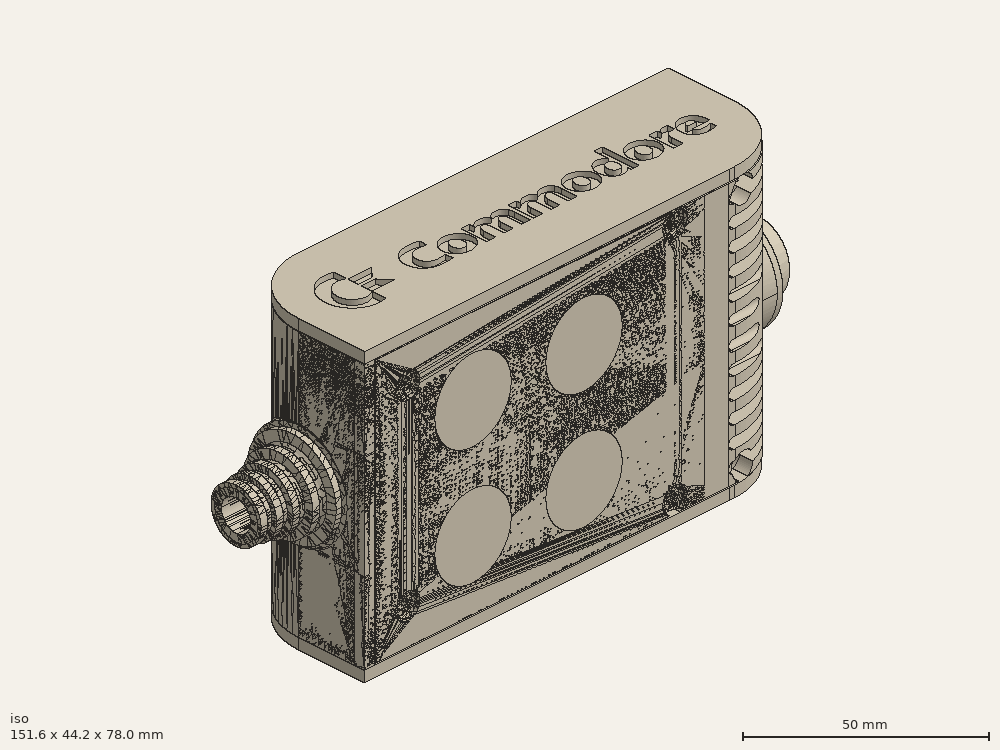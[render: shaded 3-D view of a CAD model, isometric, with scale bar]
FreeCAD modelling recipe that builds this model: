
FCSTD DOCUMENT  (FreeCAD 0.19R0.19.2)
Label: enclosure_218FCStd
License: All rights reserved
LicenseURL: http://en.wikipedia.org/wiki/All_rights_reserved
objects: Part::Revolution×152, Part::MultiFuse×146, Part::Feature×146, Sketcher::SketchObject×89, Part::Extrusion×74, Part::Cut×72, Part::Cylinder×70, Part::Fillet×58, Part::Box×36, App::MeasureDistance×4, Part::Chamfer×4, Part::FeaturePython×2, Image::ImagePlane×1, PartDesign::Body×1, Part::Mirroring×1
note: 851 computed .brp shape members not serialized (recipe doc carries the construction recipe); baked Part::Feature solids carry a one-line shape summary decoded from their .brp

FEATURE [Sketcher::SketchObject] Sketch  label="topSketch"
  FullyConstrained = true
  sketch-geometry (20):
    g0: LineSegment StartX=5.21097e-06 StartY=3 StartZ=0 EndX=5.21097e-06 EndY=19 EndZ=0
    g1: ArcOfCircle CenterX=19 CenterY=19 CenterZ=0 NormalX=0 NormalY=0 NormalZ=1 AngleXU=0 Radius=19 StartAngle=1.5708 EndAngle=3.14159
    g2: ArcOfCircle CenterX=19 CenterY=19 CenterZ=0 NormalX=0 NormalY=0 NormalZ=1 AngleXU=0 Radius=16 StartAngle=1.5708 EndAngle=3.14159
    g3: LineSegment StartX=114 StartY=35 StartZ=0 EndX=19 EndY=35 EndZ=0
    g4: LineSegment StartX=5.21097e-06 StartY=3 StartZ=0 EndX=5.21097e-06 EndY=0 EndZ=0
    g5: LineSegment StartX=3 StartY=0 StartZ=0 EndX=5.21097e-06 EndY=0 EndZ=0
    g6: LineSegment StartX=3 StartY=19 StartZ=0 EndX=3 EndY=0 EndZ=0
    g7: LineSegment StartX=19 StartY=38 StartZ=0 EndX=124 EndY=38 EndZ=0
    g8: Circle CenterX=119 CenterY=35 CenterZ=0 NormalX=0 NormalY=0 NormalZ=1 AngleXU=0 Radius=1
    g9: Circle CenterX=121 CenterY=35 CenterZ=0 NormalX=0 NormalY=0 NormalZ=1 AngleXU=0 Radius=1
    g10: Circle CenterX=121 CenterY=33 CenterZ=0 NormalX=0 NormalY=0 NormalZ=1 AngleXU=0 Radius=1
    g11: BSplineCurve PolesCount=3 KnotsCount=2 Degree=2 IsPeriodic=0
    g12: GeomPoint X=119 Y=35 Z=0
    g13: GeomPoint X=121 Y=33 Z=0
    g14: LineSegment StartX=119 StartY=35 StartZ=0 EndX=114 EndY=35 EndZ=0
    g15: ArcOfCircle CenterX=105 CenterY=19 CenterZ=0 NormalX=0 NormalY=0 NormalZ=1 AngleXU=0 Radius=19 StartAngle=5.7297 EndAngle=6.28319
    g16: ArcOfCircle CenterX=105 CenterY=19 CenterZ=0 NormalX=0 NormalY=0 NormalZ=1 AngleXU=0 Radius=16 StartAngle=5.60905 EndAngle=6.28319
    g17: LineSegment StartX=121 StartY=33 StartZ=0 EndX=121 EndY=19 EndZ=0
    g18: LineSegment StartX=124 StartY=38 StartZ=0 EndX=124 EndY=19 EndZ=0
    g19: LineSegment StartX=117.5 StartY=9.01251 StartZ=0 EndX=121.163 EndY=9.0125 EndZ=0
  constraints (46):
    c: Vertical(g0)
    c: Block(g0)
    c: Coincident(g1,g0)
    c: Block(g1)
    c: Coincident(g2,g1)
    c: Block(g2)
    c: Coincident(g3,g2)
    c: Horizontal(g3)
    c: Tangent(g3,g2)
    c: Coincident(g4,g0)
    c: Distance(g4) = 3
    c: Vertical(g4)
    c: Coincident(g5,g4)
    c: Horizontal(g5)
    c: Coincident(g6,g2)
    c: Coincident(g6,g5)
    c: Vertical(g6)
    c: Horizontal(g7)
    c: Distance(g7) = 105
    c: Coincident(g7,g1)
    c: Block(g3)
    c: Weight(g8) = 1
    c: Equal(g8,g9)
    c: Equal(g8,g10)
    c: InternalAlignment(g8,g11)
    c: InternalAlignment(g9,g11)
    c: InternalAlignment(g10,g11)
    c: InternalAlignment(g12,g11)
    c: InternalAlignment(g13,g11)
    c: Block(g11)
    c: Coincident(g14,g11)
    c: Coincident(g14,g3)
    c: Horizontal(g14)
    c: Block(g15)
    c: Coincident(g16,g15)
    c: Block(g16)
    c: Coincident(g17,g11)
    c: Coincident(g17,g16)
    c: Vertical(g17)
    c: Distance(g17) = 14
    c: Coincident(g18,g7)
    c: Coincident(g18,g15)
    c: Vertical(g18)
    c: Distance(g18) = 19
    c: Coincident(g19,g16)
    c: Coincident(g19,g15)
FEATURE [Sketcher::SketchObject] Sketch001  label="bottomSketch"
  FullyConstrained = true
  sketch-geometry (32):
    g0: LineSegment StartX=3.3 StartY=-6.03275e-07 StartZ=0 EndX=98 EndY=-6.03275e-07 EndZ=0
    g1: ArcOfCircle CenterX=98 CenterY=19 CenterZ=0 NormalX=0 NormalY=0 NormalZ=1 AngleXU=0 Radius=19 StartAngle=4.71239 EndAngle=5.71103
    g2: LineSegment StartX=6.3 StartY=8 StartZ=0 EndX=3.3 EndY=8 EndZ=0
    g3: LineSegment StartX=3.3 StartY=8 StartZ=0 EndX=3.3 EndY=-6.03275e-07 EndZ=0
    g4: ArcOfCircle CenterX=8.3 CenterY=5 CenterZ=0 NormalX=0 NormalY=0 NormalZ=1 AngleXU=0 Radius=2 StartAngle=3.14159 EndAngle=4.71239
    g5: LineSegment StartX=6.3 StartY=8 StartZ=0 EndX=6.3 EndY=5 EndZ=0
    g6: ArcOfCircle CenterX=98 CenterY=19 CenterZ=0 NormalX=0 NormalY=0 NormalZ=1 AngleXU=0 Radius=12.7 StartAngle=4.71239 EndAngle=6.28319
    g7: LineSegment StartX=94.7 StartY=3 StartZ=0 EndX=8.3 EndY=3 EndZ=0
    g8-g12: Circle x5 (B-spline internal-alignment scaffolding for g13; pole/knot coordinates omitted)
    g13: BSplineCurve PolesCount=5 KnotsCount=3 Degree=3 IsPeriodic=0
    g14: GeomPoint X=98 Y=6.3 Z=0
    g15: GeomPoint X=96.3938 Y=4.71946 Z=0
    g16: GeomPoint X=94.7 Y=3 Z=0
    g17-g23: Circle x7 (B-spline internal-alignment scaffolding for g24; pole/knot coordinates omitted)
    g24: BSplineCurve PolesCount=7 KnotsCount=5 Degree=3 IsPeriodic=0
    g25-g29: GeomPoint x5 (B-spline internal-alignment scaffolding for g24; pole/knot coordinates omitted)
    g30: ArcOfCircle CenterX=98 CenterY=19 CenterZ=0 NormalX=0 NormalY=0 NormalZ=1 AngleXU=0 Radius=15.7 StartAngle=5.81226 EndAngle=6.28319
    g31: LineSegment StartX=110.7 StartY=19 StartZ=0 EndX=113.7 EndY=19 EndZ=0
  constraints (41):
    c: Horizontal(g0)
    c: Coincident(g1,g0)
    c: Block(g1)
    c: Horizontal(g2)
    c: Distance(g2) = 3
    c: Coincident(g3,g2)
    c: Vertical(g3)
    c: Coincident(g3,g0)
    c: Block(g4)
    c: Block(g2)
    c: Coincident(g5,g2)
    c: Coincident(g5,g4)
    c: Vertical(g5)
    c: Coincident(g6,g1)
    c: Block(g6)
    c: Coincident(g7,g4)
    c: Horizontal(g7)
    c: Block(g0)
    c: Block(g7)
    c: Block(g3)
    c: Coincident(g13,g6)
    c: Weight(g8) = 1
    c: Equal(g8, g9-g12) x4
    c: Coincident(g13,g7)
    c: InternalAlignment(g8-g12 -> g13) x5
    c: InternalAlignment(g14,g13)
    c: InternalAlignment(g15,g13)
    c: InternalAlignment(g16,g13)
    c: Block(g13)
    c: Weight(g17) = 1
    c: Equal(g17, g18-g23) x6
    c: Coincident(g24,g1)
    c: InternalAlignment(g17-g23 -> g24) x7
    c: InternalAlignment(g25-g29 -> g24) x5
    c: Block(g24)
    c: Coincident(g30,g24)
    c: Coincident(g31,g6)
    c: Coincident(g31,g30)
    c: Horizontal(g31)
    c: Block(g31)
    c: Block(g30)
FEATURE [Part::Extrusion] Extrude  label="top"
  Base = -> Sketch
  Dir = (0,0,1)
  DirMode = 2
  FaceMakerClass = Part::FaceMakerBullseye
  LengthFwd = 72
  LengthRev = 0
  Solid = true
  Symmetric = false
FEATURE [Part::Extrusion] Extrude001  label="bottom"
  Base = -> Sketch001
  Dir = (0,0,1)
  DirMode = 2
  FaceMakerClass = Part::FaceMakerBullseye
  LengthFwd = 71.4
  LengthRev = 0
  Placement = pos=(0,0,0.3) rot=(0,0,1;0rad)
  Solid = true
  Symmetric = false
FEATURE [Sketcher::SketchObject] Sketch002  label="topSketch001"
  FullyConstrained = true
  sketch-geometry (8):
    g0: ArcOfCircle CenterX=19 CenterY=19.0975 CenterZ=0 NormalX=0 NormalY=0 NormalZ=1 AngleXU=0 Radius=18.9025 StartAngle=1.5708 EndAngle=3.14674
    g1: LineSegment StartX=0.0977805 StartY=19.0003 StartZ=0 EndX=0.0977805 EndY=0.000251602 EndZ=0
    g2: LineSegment StartX=19 StartY=38 StartZ=0 EndX=124 EndY=38 EndZ=0
    g3: LineSegment StartX=0.0977805 StartY=0.000251602 StartZ=0 EndX=105.098 EndY=0.000251602 EndZ=0
    g4: LineSegment StartX=124 StartY=38 StartZ=0 EndX=125.616 EndY=38 EndZ=0
    g5: LineSegment StartX=105.098 StartY=0.000251602 StartZ=0 EndX=106.713 EndY=0.000251602 EndZ=0
    g6: ArcOfCircle CenterX=106.616 CenterY=19 CenterZ=0 NormalX=0 NormalY=0 NormalZ=1 AngleXU=0 Radius=19 StartAngle=4.71754 EndAngle=6.28319
    g7: LineSegment StartX=125.616 StartY=38 StartZ=0 EndX=125.616 EndY=19 EndZ=0
  constraints (21):
    c: Block(g0)
    c: Coincident(g1,g0)
    c: Vertical(g1)
    c: Horizontal(g2)
    c: Distance(g2) = 105
    c: Coincident(g2,g0)
    c: Distance(g1) = 19
    c: Coincident(g3,g1)
    c: Horizontal(g3)
    c: Distance(g3) = 105
    c: Coincident(g4,g2)
    c: Horizontal(g4)
    c: Distance(g4) = 1.61553
    c: Horizontal(g5)
    c: Equal(g4,g5) = 1.61553
    c: Coincident(g5,g3)
    c: Block(g6)
    c: Coincident(g6,g5)
    c: Coincident(g7,g4)
    c: Coincident(g7,g6)
    c: Vertical(g7)
FEATURE [Part::Extrusion] Extrude002  label="sideA"
  Base = -> Sketch002
  Dir = (0,0,1)
  DirMode = 2
  FaceMakerClass = Part::FaceMakerBullseye
  LengthFwd = 3
  LengthRev = 0
  Placement = pos=(0,0,-3) rot=(0,0,1;0rad)
  Solid = true
  Symmetric = false
FEATURE [Sketcher::SketchObject] Sketch003  label="topSketch002"
  FullyConstrained = true
  sketch-geometry (6):
    g0: LineSegment StartX=19 StartY=38 StartZ=0 EndX=117 EndY=38 EndZ=0
    g1: ArcOfCircle CenterX=19 CenterY=19 CenterZ=0 NormalX=0 NormalY=0 NormalZ=1 AngleXU=0 Radius=19 StartAngle=1.5708 EndAngle=3.14159
    g2: LineSegment StartX=117 StartY=38 StartZ=0 EndX=117 EndY=19 EndZ=0
    g3: LineSegment StartX=98 StartY=1.0161e-12 StartZ=0 EndX=5.22862e-06 EndY=1.0161e-12 EndZ=0
    g4: LineSegment StartX=5.22862e-06 StartY=19 StartZ=0 EndX=5.22862e-06 EndY=1.0161e-12 EndZ=0
    g5: ArcOfCircle CenterX=98 CenterY=19 CenterZ=0 NormalX=0 NormalY=0 NormalZ=1 AngleXU=0 Radius=19 StartAngle=4.71239 EndAngle=6.28319
  constraints (16):
    c: Horizontal(g0)
    c: Distance(g0) = 98
    c: Coincident(g1,g0)
    c: Block(g1)
    c: Coincident(g2,g0)
    c: Vertical(g2)
    c: Distance(g2) = 19
    c: Horizontal(g3)
    c: Coincident(g4,g1)
    c: Vertical(g4)
    c: Coincident(g3,g4)
    c: Block(g3)
    c: Coincident(g5,g2)
    c: Coincident(g5,g3)
    c: Block(g0)
    c: Block(g5)
FEATURE [Sketcher::SketchObject] Sketch004
  FullyConstrained = true
  MapMode = 3
  Placement = pos=(0,0,0) rot=(1,0,0;1.5708rad)
  Support = -> [Extrude]
  sketch-geometry (8):
    g0: Circle CenterX=80.351 CenterY=-67.6202 CenterZ=0 NormalX=0 NormalY=0 NormalZ=1 AngleXU=0 Radius=2
    g1: Circle CenterX=80.351 CenterY=-67.6202 CenterZ=0 NormalX=0 NormalY=0 NormalZ=1 AngleXU=0 Radius=3
    g2: Circle CenterX=80.351 CenterY=-4.92017 CenterZ=0 NormalX=0 NormalY=0 NormalZ=1 AngleXU=0 Radius=2
    g3: Circle CenterX=80.351 CenterY=-4.92017 CenterZ=0 NormalX=0 NormalY=0 NormalZ=1 AngleXU=0 Radius=3
    g4: Circle CenterX=23.851 CenterY=-4.92017 CenterZ=0 NormalX=0 NormalY=0 NormalZ=1 AngleXU=0 Radius=2
    g5: Circle CenterX=23.851 CenterY=-4.92017 CenterZ=0 NormalX=0 NormalY=0 NormalZ=1 AngleXU=0 Radius=3
    g6: Circle CenterX=23.851 CenterY=-67.6202 CenterZ=0 NormalX=0 NormalY=0 NormalZ=1 AngleXU=0 Radius=2
    g7: Circle CenterX=23.851 CenterY=-67.6202 CenterZ=0 NormalX=0 NormalY=0 NormalZ=1 AngleXU=0 Radius=3
  constraints (8):
    c: Block(g3)
    c: Block(g2)
    c: Block(g1)
    c: Block(g0)
    c: Block(g6)
    c: Block(g7)
    c: Block(g4)
    c: Block(g5)
FEATURE [Part::Extrusion] Extrude004
  Base = -> Sketch004
  Dir = (0,-1,2e-16)
  DirMode = 2
  FaceMakerClass = Part::FaceMakerBullseye
  LengthFwd = 6
  LengthRev = 0
  Placement = pos=(0,9,0) rot=(0,0,1;0rad)
  Solid = true
  Symmetric = false
FEATURE [Sketcher::SketchObject] Sketch005
  FullyConstrained = true
  MapMode = 3
  Placement = pos=(0,0,0) rot=(1,0,0;1.5708rad)
  Support = -> [Extrude]
  sketch-geometry (8):
    g0: Circle CenterX=80.351 CenterY=-67.6202 CenterZ=0 NormalX=0 NormalY=0 NormalZ=1 AngleXU=0 Radius=3
    g1: Circle CenterX=80.351 CenterY=-4.92017 CenterZ=0 NormalX=0 NormalY=0 NormalZ=1 AngleXU=0 Radius=3
    g2: Circle CenterX=23.851 CenterY=-4.92017 CenterZ=0 NormalX=0 NormalY=0 NormalZ=1 AngleXU=0 Radius=3
    g3: Circle CenterX=23.851 CenterY=-67.6202 CenterZ=0 NormalX=0 NormalY=0 NormalZ=1 AngleXU=0 Radius=3
    g4: Circle CenterX=23.851 CenterY=-67.6202 CenterZ=0 NormalX=0 NormalY=0 NormalZ=1 AngleXU=0 Radius=5
    g5: Circle CenterX=80.351 CenterY=-67.6202 CenterZ=0 NormalX=0 NormalY=0 NormalZ=1 AngleXU=0 Radius=5
    g6: Circle CenterX=23.851 CenterY=-4.92017 CenterZ=0 NormalX=0 NormalY=0 NormalZ=1 AngleXU=0 Radius=5
    g7: Circle CenterX=80.351 CenterY=-4.92017 CenterZ=0 NormalX=0 NormalY=0 NormalZ=1 AngleXU=0 Radius=5
  constraints (8):
    c: Block(g1)
    c: Block(g0)
    c: Block(g3)
    c: Block(g2)
    c: Block(g5)
    c: Block(g4)
    c: Block(g6)
    c: Block(g7)
FEATURE [Part::Extrusion] Extrude005
  Base = -> Sketch005
  Dir = (0,-1,2e-16)
  DirMode = 2
  FaceMakerClass = Part::FaceMakerBullseye
  LengthFwd = 2
  LengthRev = 0
  Solid = true
  Symmetric = false
FEATURE [Sketcher::SketchObject] Sketch006
  FullyConstrained = true
  MapMode = 3
  Placement = pos=(0,0,0) rot=(1,0,0;1.5708rad)
  sketch-geometry (8):
    g0: Circle CenterX=80.351 CenterY=-67.6202 CenterZ=0 NormalX=0 NormalY=0 NormalZ=1 AngleXU=0 Radius=3
    g1: Circle CenterX=80.351 CenterY=-4.92017 CenterZ=0 NormalX=0 NormalY=0 NormalZ=1 AngleXU=0 Radius=3
    g2: Circle CenterX=23.851 CenterY=-4.92017 CenterZ=0 NormalX=0 NormalY=0 NormalZ=1 AngleXU=0 Radius=3
    g3: Circle CenterX=23.851 CenterY=-67.6202 CenterZ=0 NormalX=0 NormalY=0 NormalZ=1 AngleXU=0 Radius=3
    g4: Circle CenterX=23.851 CenterY=-67.6202 CenterZ=0 NormalX=0 NormalY=0 NormalZ=1 AngleXU=0 Radius=5
    g5: Circle CenterX=80.351 CenterY=-67.6202 CenterZ=0 NormalX=0 NormalY=0 NormalZ=1 AngleXU=0 Radius=5
    g6: Circle CenterX=23.851 CenterY=-4.92017 CenterZ=0 NormalX=0 NormalY=0 NormalZ=1 AngleXU=0 Radius=5
    g7: Circle CenterX=80.351 CenterY=-4.92017 CenterZ=0 NormalX=0 NormalY=0 NormalZ=1 AngleXU=0 Radius=5
  constraints (8):
    c: Block(g1)
    c: Block(g0)
    c: Block(g3)
    c: Block(g2)
    c: Block(g5)
    c: Block(g4)
    c: Block(g6)
    c: Block(g7)
FEATURE [Part::Extrusion] Extrude007
  Base = -> Sketch006
  Dir = (0,-1,2e-16)
  DirMode = 2
  FaceMakerClass = Part::FaceMakerBullseye
  LengthFwd = 2
  LengthRev = 0
  Solid = true
  Symmetric = false
FEATURE [Part::Fillet] Fillet
  Base = -> Extrude007
  Edges = 4 edges r=1.99: [Edge6,Edge12,Edge18,Edge24]
FEATURE [Part::Cut] Cut
  Base = -> Extrude005
  Placement = pos=(0,5,0) rot=(0,0,1;0rad)
  Tool = -> Fillet
FEATURE [Part::MultiFuse] Fusion  label="pCBScrews"
  Placement = pos=(-2.5,0,72.3) rot=(0,0,1;0rad)
  Shapes = -> [Extrude004,Cut]
FEATURE [App::MeasureDistance] Distance  label="Distance: 0.69 mm"
  Distance = 0.685967
  P1 = (24.0138,2.9647,0.3)
  P2 = (23.8901,3,-0.373787)
FEATURE [App::MeasureDistance] Distance001  label="Distance: 0.53 mm"
  Distance = 0.533607
  P1 = (80.2939,3,72.2334)
  P2 = (80.281,2.99661,71.7)
FEATURE [Part::Fillet] Fillet001
  Base = -> Extrude001
  Edges = 1 edges r=2.4: [Edge17]
FEATURE [Part::Fillet] Fillet002  label="bottom001"
  Base = -> Fillet001
  Edges = 1 edges r=2.4: [Edge36]
FEATURE [Part::Fillet] Fillet003  label="top001"
  Base = -> Extrude
  Edges = 1 edges r=2: [Edge1]
FEATURE [Sketcher::SketchObject] Sketch007
  FullyConstrained = true
  sketch-geometry (16):
    g0: LineSegment StartX=4 StartY=0 StartZ=0 EndX=4 EndY=2.4 EndZ=0
    g1: LineSegment StartX=4 StartY=2.4 StartZ=0 EndX=7 EndY=2.4 EndZ=0
    g2: LineSegment StartX=4 StartY=0 StartZ=0 EndX=5.7 EndY=0 EndZ=0
    g3: LineSegment StartX=5.7 StartY=0 StartZ=0 EndX=5.7 EndY=-5.6 EndZ=0
    g4-g8: Circle x5 (B-spline internal-alignment scaffolding for g9; pole/knot coordinates omitted)
    g9: BSplineCurve PolesCount=5 KnotsCount=3 Degree=3 IsPeriodic=0
    g10: GeomPoint X=7 Y=2.4 Z=0
    g11: GeomPoint X=10.4582 Y=-1.55472 Z=0
    g12: GeomPoint X=14 Y=-5.6 Z=0
    g13: LineSegment StartX=14 StartY=-5.6 StartZ=0 EndX=14 EndY=-14.1 EndZ=0
    g14: LineSegment StartX=14 StartY=-14.1 StartZ=0 EndX=6.5 EndY=-14.1 EndZ=0
    g15: LineSegment StartX=5.7 StartY=-5.6 StartZ=0 EndX=6.5 EndY=-14.1 EndZ=0
  constraints (28):
    c: Distance(g0) = 2.4
    c: Vertical(g0)
    c: Block(g0)
    c: Coincident(g1,g0)
    c: Horizontal(g1)
    c: Distance(g1) = 3
    c: Coincident(g2,g0)
    c: Horizontal(g2)
    c: Distance(g2) = 1.7
    c: Coincident(g3,g2)
    c: Vertical(g3)
    c: Distance(g3) = 5.6
    c: Coincident(g9,g1)
    c: Weight(g4) = 1
    c: Equal(g4, g5-g8) x4
    c: InternalAlignment(g4-g8 -> g9) x5
    c: InternalAlignment(g10,g9)
    c: InternalAlignment(g11,g9)
    c: InternalAlignment(g12,g9)
    c: Block(g9)
    c: Coincident(g13,g9)
    c: Vertical(g13)
    c: Distance(g13) = 8.5
    c: Coincident(g14,g13)
    c: Horizontal(g14)
    c: Distance(g14) = 7.5
    c: Coincident(g15,g3)
    c: Coincident(g15,g14)
FEATURE [Part::Feature] Face
  shape: bbox 10 x 16.5 x 2e-07 mm, 1 faces, 0 solids (baked)
FEATURE [Part::Revolution] Revolve  label="plugHousing"
  Angle = 360
  Axis = (0,1,0)
  Base = (0,0,0)
  FaceMakerClass = Part::FaceMakerBullseye
  Placement = pos=(0,0,36.15) rot=(0,0,1;0rad)
  Solid = false
  Source = -> Face
  Symmetric = false
FEATURE [Part::Feature] Face001
  shape: bbox 10 x 16.5 x 2e-07 mm, 1 faces, 0 solids (baked)
FEATURE [Part::Revolution] Revolve001  label="plugHousing001"
  Angle = 360
  Axis = (0,1,0)
  Base = (0,0,0)
  FaceMakerClass = Part::FaceMakerBullseye
  Placement = pos=(0,0,36.15) rot=(0,0,1;0rad)
  Solid = false
  Source = -> Face001
  Symmetric = false
FEATURE [Part::MultiFuse] Fusion001  label="plugHousing002"
  Placement = pos=(0,0,0) rot=(0,0,1;1.5708rad)
  Shapes = -> [Revolve001,Revolve]
FEATURE [Part::Feature] Face002
  shape: bbox 10 x 16.5 x 2e-07 mm, 1 faces, 0 solids (baked)
FEATURE [Part::Revolution] Revolve003  label="plugHousing005"
  Angle = 360
  Axis = (0,1,0)
  Base = (0,0,0)
  FaceMakerClass = Part::FaceMakerBullseye
  Placement = pos=(0,0,36.15) rot=(0,0,1;0rad)
  Solid = false
  Source = -> Face002
  Symmetric = false
FEATURE [Part::Feature] Face003
  shape: bbox 10 x 16.5 x 2e-07 mm, 1 faces, 0 solids (baked)
FEATURE [Part::Revolution] Revolve002  label="plugHousing003"
  Angle = 360
  Axis = (0,1,0)
  Base = (0,0,0)
  FaceMakerClass = Part::FaceMakerBullseye
  Placement = pos=(0,0,36.15) rot=(0,0,1;0rad)
  Solid = false
  Source = -> Face003
  Symmetric = false
FEATURE [Part::MultiFuse] Fusion002  label="plugHousing004"
  Placement = pos=(0,0,0) rot=(0,0,1;1.5708rad)
  Shapes = -> [Revolve002,Revolve003]
FEATURE [Part::MultiFuse] Fusion003  label="plugHousing006"
  Placement = pos=(0,19,0) rot=(0,0,1;3.14159rad)
  Shapes = -> [Fusion002,Fusion001]
FEATURE [Part::Feature] Face004
  shape: bbox 10 x 16.5 x 2e-07 mm, 1 faces, 0 solids (baked)
FEATURE [Part::Revolution] Revolve006  label="plugHousing010"
  Angle = 360
  Axis = (0,1,0)
  Base = (0,0,0)
  FaceMakerClass = Part::FaceMakerBullseye
  Placement = pos=(0,0,36.15) rot=(0,0,1;0rad)
  Solid = false
  Source = -> Face004
  Symmetric = false
FEATURE [Part::Feature] Face005
  shape: bbox 10 x 16.5 x 2e-07 mm, 1 faces, 0 solids (baked)
FEATURE [Part::Revolution] Revolve007  label="plugHousing011"
  Angle = 360
  Axis = (0,1,0)
  Base = (0,0,0)
  FaceMakerClass = Part::FaceMakerBullseye
  Placement = pos=(0,0,36.15) rot=(0,0,1;0rad)
  Solid = false
  Source = -> Face005
  Symmetric = false
FEATURE [Part::Feature] Face006
  shape: bbox 10 x 16.5 x 2e-07 mm, 1 faces, 0 solids (baked)
FEATURE [Part::Revolution] Revolve004  label="plugHousing007"
  Angle = 360
  Axis = (0,1,0)
  Base = (0,0,0)
  FaceMakerClass = Part::FaceMakerBullseye
  Placement = pos=(0,0,36.15) rot=(0,0,1;0rad)
  Solid = false
  Source = -> Face006
  Symmetric = false
FEATURE [Part::MultiFuse] Fusion004  label="plugHousing009"
  Placement = pos=(0,0,0) rot=(0,0,1;1.5708rad)
  Shapes = -> [Revolve004,Revolve007]
FEATURE [Part::Feature] Face007
  shape: bbox 10 x 16.5 x 2e-07 mm, 1 faces, 0 solids (baked)
FEATURE [Part::Revolution] Revolve005  label="plugHousing008"
  Angle = 360
  Axis = (0,1,0)
  Base = (0,0,0)
  FaceMakerClass = Part::FaceMakerBullseye
  Placement = pos=(0,0,36.15) rot=(0,0,1;0rad)
  Solid = false
  Source = -> Face007
  Symmetric = false
FEATURE [Part::MultiFuse] Fusion005  label="plugHousing012"
  Placement = pos=(0,0,0) rot=(0,0,1;1.5708rad)
  Shapes = -> [Revolve006,Revolve005]
FEATURE [Part::MultiFuse] Fusion006  label="plugHousing013"
  Placement = pos=(0,19,0) rot=(0,0,1;3.14159rad)
  Shapes = -> [Fusion005,Fusion004]
FEATURE [Part::MultiFuse] Fusion007  label="plugHousing014"
  Placement = pos=(122.621,0,-0.15) rot=(0,0,1;0rad)
  Shapes = -> [Fusion003,Fusion006]
FEATURE [Part::Cylinder] Cylinder002
  Angle = 360
  AttacherType = Attacher::AttachEngine3D
  Height = 20
  Placement = pos=(0,0,36.15) rot=(0,0,1;0rad)
  Radius = 4
FEATURE [Part::Cylinder] Cylinder003
  Angle = 360
  AttacherType = Attacher::AttachEngine3D
  Height = 10
  Placement = pos=(0,0,36.15) rot=(0,0,1;0rad)
  Radius = 4
FEATURE [Part::MultiFuse] Fusion009  label="removeToCreateHoleForPlugHousing"
  Placement = pos=(70,19,36.15) rot=(0,1,0;1.5708rad)
  Shapes = -> [Cylinder002,Cylinder003]
FEATURE [Part::Cylinder] Cylinder004
  Angle = 360
  AttacherType = Attacher::AttachEngine3D
  Height = 20
  Placement = pos=(0,0,36.15) rot=(0,0,1;0rad)
  Radius = 4
FEATURE [Part::Cylinder] Cylinder005
  Angle = 360
  AttacherType = Attacher::AttachEngine3D
  Height = 10
  Placement = pos=(0,0,36.15) rot=(0,0,1;0rad)
  Radius = 4
FEATURE [Part::MultiFuse] Fusion010  label="removeToCreateHoleForPlugHousing001"
  Placement = pos=(70,19,36.15) rot=(0,1,0;1.5708rad)
  Shapes = -> [Cylinder004,Cylinder005]
FEATURE [Part::Cut] Cut001
  Base = -> Fillet003
  Tool = -> Fusion010
FEATURE [Part::Cut] Cut002  label="Bottom"
  Base = -> Fillet002
  Tool = -> Fusion009
FEATURE [Part::Feature] Face008
  shape: bbox 10 x 16.5 x 2e-07 mm, 1 faces, 0 solids (baked)
FEATURE [Part::Revolution] Revolve011  label="plugHousing021"
  Angle = 360
  Axis = (0,1,0)
  Base = (0,0,0)
  FaceMakerClass = Part::FaceMakerBullseye
  Placement = pos=(0,0,36.15) rot=(0,0,1;0rad)
  Solid = false
  Source = -> Face008
  Symmetric = false
FEATURE [Part::Feature] Face009
  shape: bbox 10 x 16.5 x 2e-07 mm, 1 faces, 0 solids (baked)
FEATURE [Part::Revolution] Revolve012  label="plugHousing022"
  Angle = 360
  Axis = (0,1,0)
  Base = (0,0,0)
  FaceMakerClass = Part::FaceMakerBullseye
  Placement = pos=(0,0,36.15) rot=(0,0,1;0rad)
  Solid = false
  Source = -> Face009
  Symmetric = false
FEATURE [Part::Feature] Face010 .. Face013  x4 (patterned run collapsed; names and placements below)
  shape: bbox 10 x 16.5 x 2e-07 mm, 1 faces, 0 solids (baked)
FEATURE [Part::Revolution] Revolve015  label="plugHousing027"
  Angle = 360
  Axis = (0,1,0)
  Base = (0,0,0)
  FaceMakerClass = Part::FaceMakerBullseye
  Placement = pos=(0,0,36.15) rot=(0,0,1;0rad)
  Solid = false
  Source = -> Face013
  Symmetric = false
FEATURE [Part::Feature] Face014
  shape: bbox 10 x 16.5 x 2e-07 mm, 1 faces, 0 solids (baked)
FEATURE [Part::Feature] Face015
  shape: bbox 10 x 16.5 x 2e-07 mm, 1 faces, 0 solids (baked)
FEATURE [Part::Feature] Face016
  shape: bbox 10 x 16.5 x 2e-07 mm, 1 faces, 0 solids (baked)
FEATURE [Part::Revolution] Revolve019  label="plugHousing033"
  Angle = 360
  Axis = (0,1,0)
  Base = (0,0,0)
  FaceMakerClass = Part::FaceMakerBullseye
  Placement = pos=(0,0,36.15) rot=(0,0,1;0rad)
  Solid = false
  Source = -> Face016
  Symmetric = false
FEATURE [Part::Feature] Face017
  shape: bbox 10 x 16.5 x 2e-07 mm, 1 faces, 0 solids (baked)
FEATURE [Part::Revolution] Revolve020  label="plugHousing034"
  Angle = 360
  Axis = (0,1,0)
  Base = (0,0,0)
  FaceMakerClass = Part::FaceMakerBullseye
  Placement = pos=(0,0,36.15) rot=(0,0,1;0rad)
  Solid = false
  Source = -> Face017
  Symmetric = false
FEATURE [Part::Feature] Face018
  shape: bbox 10 x 16.5 x 2e-07 mm, 1 faces, 0 solids (baked)
FEATURE [Part::Revolution] Revolve016  label="plugHousing030"
  Angle = 360
  Axis = (0,1,0)
  Base = (0,0,0)
  FaceMakerClass = Part::FaceMakerBullseye
  Placement = pos=(0,0,36.15) rot=(0,0,1;0rad)
  Solid = false
  Source = -> Face018
  Symmetric = false
FEATURE [Part::MultiFuse] Fusion020  label="plugHousing038"
  Placement = pos=(0,0,0) rot=(0,0,1;1.5708rad)
  Shapes = -> [Revolve016,Revolve020]
FEATURE [Part::Feature] Face019
  shape: bbox 10 x 16.5 x 2e-07 mm, 1 faces, 0 solids (baked)
FEATURE [Part::Feature] Face020
  shape: bbox 10 x 16.5 x 2e-07 mm, 1 faces, 0 solids (baked)
FEATURE [Part::Revolution] Revolve017  label="plugHousing031"
  Angle = 360
  Axis = (0,1,0)
  Base = (0,0,0)
  FaceMakerClass = Part::FaceMakerBullseye
  Placement = pos=(0,0,36.15) rot=(0,0,1;0rad)
  Solid = false
  Source = -> Face020
  Symmetric = false
FEATURE [Part::MultiFuse] Fusion021  label="plugHousing039"
  Placement = pos=(0,0,0) rot=(0,0,1;1.5708rad)
  Shapes = -> [Revolve019,Revolve017]
FEATURE [Part::MultiFuse] Fusion023  label="plugHousing041"
  Placement = pos=(0,19,0) rot=(0,0,1;3.14159rad)
  Shapes = -> [Fusion021,Fusion020]
FEATURE [Part::Revolution] Revolve022  label="plugHousing043"
  Angle = 360
  Axis = (0,1,0)
  Base = (0,0,0)
  FaceMakerClass = Part::FaceMakerBullseye
  Placement = pos=(0,0,36.15) rot=(0,0,1;0rad)
  Solid = false
  Source = -> Face019
  Symmetric = false
FEATURE [Part::Feature] Face021
  shape: bbox 10 x 16.5 x 2e-07 mm, 1 faces, 0 solids (baked)
FEATURE [Part::Revolution] Revolve023  label="plugHousing044"
  Angle = 360
  Axis = (0,1,0)
  Base = (0,0,0)
  FaceMakerClass = Part::FaceMakerBullseye
  Placement = pos=(0,0,36.15) rot=(0,0,1;0rad)
  Solid = false
  Source = -> Face021
  Symmetric = false
FEATURE [Part::Feature] Face022
  shape: bbox 10 x 16.5 x 2e-07 mm, 1 faces, 0 solids (baked)
FEATURE [Part::Revolution] Revolve018  label="plugHousing032"
  Angle = 360
  Axis = (0,1,0)
  Base = (0,0,0)
  FaceMakerClass = Part::FaceMakerBullseye
  Placement = pos=(0,0,36.15) rot=(0,0,1;0rad)
  Solid = false
  Source = -> Face022
  Symmetric = false
FEATURE [Part::MultiFuse] Fusion022  label="plugHousing040"
  Placement = pos=(0,0,0) rot=(0,0,1;1.5708rad)
  Shapes = -> [Revolve018,Revolve023]
FEATURE [Part::Feature] Face023
  shape: bbox 10 x 16.5 x 2e-07 mm, 1 faces, 0 solids (baked)
FEATURE [Part::Revolution] Revolve021  label="plugHousing035"
  Angle = 360
  Axis = (0,1,0)
  Base = (0,0,0)
  FaceMakerClass = Part::FaceMakerBullseye
  Placement = pos=(0,0,36.15) rot=(0,0,1;0rad)
  Solid = false
  Source = -> Face023
  Symmetric = false
FEATURE [Part::MultiFuse] Fusion018  label="plugHousing036"
  Placement = pos=(0,0,0) rot=(0,0,1;1.5708rad)
  Shapes = -> [Revolve022,Revolve021]
FEATURE [Part::MultiFuse] Fusion019  label="plugHousing037"
  Placement = pos=(0,19,0) rot=(0,0,1;3.14159rad)
  Shapes = -> [Fusion018,Fusion022]
FEATURE [Part::MultiFuse] Fusion024  label="plugHousing042"
  Placement = pos=(122.621,0,-0.15) rot=(0,0,1;0rad)
  Shapes = -> [Fusion023,Fusion019]
FEATURE [Part::Cylinder] Cylinder006
  Angle = 360
  AttacherType = Attacher::AttachEngine3D
  Height = 20
  Placement = pos=(0,0,36.15) rot=(0,0,1;0rad)
  Radius = 14.3
FEATURE [Part::Cylinder] Cylinder007
  Angle = 360
  AttacherType = Attacher::AttachEngine3D
  Height = 10
  Placement = pos=(0,0,36.15) rot=(0,0,1;0rad)
  Radius = 4
FEATURE [Part::MultiFuse] Fusion026  label="removeToCreteHoleForPlugHousing"
  Placement = pos=(70,19,36) rot=(0,1,0;1.5708rad)
  Shapes = -> [Cylinder006,Cylinder007]
FEATURE [Part::Box] Box001  label="Cube001"
  AttacherType = Attacher::AttachEngine3D
  Height = 28
  Length = 3
  Placement = pos=(110.7,19,22) rot=(0,0,1;0rad)
  Width = 15.7
FEATURE [Part::Cut] Cut003  label="top002"
  Base = -> Cut001
  Tool = -> Fusion007
FEATURE [Part::Revolution] Revolve008  label="plugHousing015"
  Angle = 360
  Axis = (0,1,0)
  Base = (0,0,0)
  FaceMakerClass = Part::FaceMakerBullseye
  Placement = pos=(0,0,36.15) rot=(0,0,1;0rad)
  Solid = false
  Source = -> Face010
  Symmetric = false
FEATURE [Part::MultiFuse] Fusion013  label="plugHousing020"
  Placement = pos=(0,0,0) rot=(0,0,1;1.5708rad)
  Shapes = -> [Revolve008,Revolve012]
FEATURE [Part::Cut] Cut004  label="top003"
  Base = -> Cut003
  Placement = pos=(1,0,0) rot=(0,0,1;0rad)
  Tool = -> Fusion026
FEATURE [Part::Cylinder] Cylinder008
  Angle = 360
  AttacherType = Attacher::AttachEngine3D
  Height = 20
  Placement = pos=(0,0,36.15) rot=(0,0,1;0rad)
  Radius = 10.3
FEATURE [Part::Cylinder] Cylinder009
  Angle = 360
  AttacherType = Attacher::AttachEngine3D
  Height = 10
  Placement = pos=(0,0,36.15) rot=(0,0,1;0rad)
  Radius = 4
FEATURE [Part::MultiFuse] Fusion027  label="removeToCreteHoleForPlugHousing001"
  Placement = pos=(70,19,36) rot=(0,1,0;1.5708rad)
  Shapes = -> [Cylinder008,Cylinder009]
FEATURE [Part::Cut] Cut005  label="plugHousingTab"
  Base = -> Box001
  Tool = -> Fusion027
FEATURE [Part::MultiFuse] Fusion028  label="plugHousing045"
  Shapes = -> [Fusion024,Cut005]
FEATURE [Part::Box] Box002  label="Cube002"
  AttacherType = Attacher::AttachEngine3D
  Height = 28.8
  Length = 3
  Placement = pos=(107.3,28,21.6) rot=(0,0,1;0rad)
  Width = 7
FEATURE [Part::Box] Box003  label="Cube003"
  AttacherType = Attacher::AttachEngine3D
  Height = 3
  Length = 6.4
  Placement = pos=(107.3,28,18.6) rot=(0,0,1;0rad)
  Width = 7
FEATURE [Part::Box] Box004  label="Cube004"
  AttacherType = Attacher::AttachEngine3D
  Height = 3
  Length = 6.4
  Placement = pos=(107.3,28,50.4) rot=(0,0,1;0rad)
  Width = 7
FEATURE [Part::MultiFuse] Fusion029  label="plugHousingBracketHolder"
  Shapes = -> [Box004,Box002,Box003]
FEATURE [Part::Cylinder] Cylinder010
  Angle = 360
  AttacherType = Attacher::AttachEngine3D
  Height = 20
  Placement = pos=(0,0,36.15) rot=(0,0,1;0rad)
  Radius = 14.3
FEATURE [Part::Cylinder] Cylinder011
  Angle = 360
  AttacherType = Attacher::AttachEngine3D
  Height = 10
  Placement = pos=(0,0,36.15) rot=(0,0,1;0rad)
  Radius = 4
FEATURE [Part::MultiFuse] Fusion030  label="removeToCreteHoleForPlugHousing002"
  Placement = pos=(70,19,36) rot=(0,1,0;1.5708rad)
  Shapes = -> [Cylinder010,Cylinder011]
FEATURE [Part::Cut] Cut006  label="plugHousingBracketHolder001"
  Base = -> Fusion029
  Tool = -> Fusion030
FEATURE [Part::Cylinder] Cylinder012
  Angle = 360
  AttacherType = Attacher::AttachEngine3D
  Height = 20
  Placement = pos=(0,0,36.15) rot=(0,0,1;0rad)
  Radius = 7
FEATURE [Part::Cylinder] Cylinder013
  Angle = 360
  AttacherType = Attacher::AttachEngine3D
  Height = 10
  Placement = pos=(0,0,36.15) rot=(0,0,1;0rad)
  Radius = 4
FEATURE [Part::MultiFuse] Fusion032  label="removeToCreteHoleForPlugHousing003"
  Placement = pos=(70,19,36) rot=(0,1,0;1.5708rad)
  Shapes = -> [Cylinder012,Cylinder013]
FEATURE [Part::Cut] Cut007  label="bottom002"
  Base = -> Cut002
  Tool = -> Fusion032
FEATURE [Sketcher::SketchObject] Sketch008
  FullyConstrained = true
  sketch-geometry (54):
    g0: LineSegment StartX=-4.2 StartY=0 StartZ=0 EndX=-6.2 EndY=0 EndZ=0
    g1: LineSegment StartX=-14 StartY=-18 StartZ=0 EndX=-14 EndY=-26.5 EndZ=0
    g2: LineSegment StartX=-4.2 StartY=0 StartZ=0 EndX=-4.2 EndY=-13.4877 EndZ=0
    g3: Circle CenterX=-4.2 CenterY=-13.4877 CenterZ=0 NormalX=0 NormalY=0 NormalZ=1 AngleXU=0 Radius=1
    g4: Circle CenterX=-4.2 CenterY=-26.5 CenterZ=0 NormalX=0 NormalY=0 NormalZ=1 AngleXU=0 Radius=1
    g5: Circle CenterX=-8.2 CenterY=-26.5 CenterZ=0 NormalX=0 NormalY=0 NormalZ=1 AngleXU=0 Radius=1
    g6: BSplineCurve PolesCount=3 KnotsCount=2 Degree=2 IsPeriodic=0
    g7: GeomPoint X=-4.2 Y=-13.4877 Z=0
    g8: GeomPoint X=-8.2 Y=-26.5 Z=0
    g9: LineSegment StartX=-14 StartY=-26.5 StartZ=0 EndX=-8.2 EndY=-26.5 EndZ=0
    g10: LineSegment StartX=-10.15 StartY=-12 StartZ=0 EndX=-10.15 EndY=-14 EndZ=0
    g11: LineSegment StartX=-12.8401 StartY=-16 StartZ=0 EndX=-10.1571 EndY=-16 EndZ=0
    g12: LineSegment StartX=-10.15 StartY=-14 StartZ=0 EndX=-8.70761 EndY=-14 EndZ=0
    g13: LineSegment StartX=-12.8401 StartY=-16 StartZ=0 EndX=-12.8401 EndY=-17.6958 EndZ=0
    g14: LineSegment StartX=-10.15 StartY=-12 StartZ=0 EndX=-7.79258 EndY=-12 EndZ=0
    g15: Circle CenterX=-6.2215 CenterY=-2 CenterZ=0 NormalX=0 NormalY=0 NormalZ=1 AngleXU=0 Radius=1
    g16: Circle CenterX=-6.22762 CenterY=-2.58724 CenterZ=0 NormalX=0 NormalY=0 NormalZ=1 AngleXU=0 Radius=1
    g17: Circle CenterX=-6.32538 CenterY=-4 CenterZ=0 NormalX=0 NormalY=0 NormalZ=1 AngleXU=0 Radius=1
    g18: BSplineCurve PolesCount=3 KnotsCount=2 Degree=2 IsPeriodic=0
    g19: GeomPoint X=-6.2215 Y=-2 Z=0
    g20: GeomPoint X=-6.32538 Y=-4 Z=0
    g21: Circle CenterX=-6.48644 CenterY=-5.99526 CenterZ=0 NormalX=0 NormalY=0 NormalZ=1 AngleXU=0 Radius=1
    g22: Circle CenterX=-6.58486 CenterY=-6.99526 CenterZ=0 NormalX=0 NormalY=0 NormalZ=1 AngleXU=0 Radius=1
    g23: Circle CenterX=-6.77343 CenterY=-8 CenterZ=0 NormalX=0 NormalY=0 NormalZ=1 AngleXU=0 Radius=1
    g24: BSplineCurve PolesCount=3 KnotsCount=2 Degree=2 IsPeriodic=0
    g25: GeomPoint X=-6.48644 Y=-5.99526 Z=0
    g26: GeomPoint X=-6.77343 Y=-8 Z=0
    g27: Circle CenterX=-7.19003 CenterY=-10 CenterZ=0 NormalX=0 NormalY=0 NormalZ=1 AngleXU=0 Radius=1
    g28: Circle CenterX=-7.44407 CenterY=-11.0915 CenterZ=0 NormalX=0 NormalY=0 NormalZ=1 AngleXU=0 Radius=1
    g29: Circle CenterX=-7.79258 CenterY=-12 CenterZ=0 NormalX=0 NormalY=0 NormalZ=1 AngleXU=0 Radius=1
    g30: BSplineCurve PolesCount=3 KnotsCount=2 Degree=2 IsPeriodic=0
    g31: GeomPoint X=-7.19003 Y=-10 Z=0
    g32: GeomPoint X=-7.79258 Y=-12 Z=0
    g33: Circle CenterX=-8.70761 CenterY=-14 CenterZ=0 NormalX=0 NormalY=0 NormalZ=1 AngleXU=0 Radius=1
    g34: Circle CenterX=-9.33087 CenterY=-15.1837 CenterZ=0 NormalX=0 NormalY=0 NormalZ=1 AngleXU=0 Radius=1
    g35: Circle CenterX=-10.1571 CenterY=-16 CenterZ=0 NormalX=0 NormalY=0 NormalZ=1 AngleXU=0 Radius=1
    g36: BSplineCurve PolesCount=3 KnotsCount=2 Degree=2 IsPeriodic=0
    g37: GeomPoint X=-8.70761 Y=-14 Z=0
    g38: GeomPoint X=-10.1571 Y=-16 Z=0
    g39: Circle CenterX=-12.8401 CenterY=-17.6958 CenterZ=0 NormalX=0 NormalY=0 NormalZ=1 AngleXU=0 Radius=1
    g40: Circle CenterX=-13.3521 CenterY=-17.9027 CenterZ=0 NormalX=0 NormalY=0 NormalZ=1 AngleXU=0 Radius=1
    g41: Circle CenterX=-14 CenterY=-18 CenterZ=0 NormalX=0 NormalY=0 NormalZ=1 AngleXU=0 Radius=1
    g42: BSplineCurve PolesCount=3 KnotsCount=2 Degree=2 IsPeriodic=0
    g43: GeomPoint X=-12.8401 Y=-17.6958 Z=0
    g44: GeomPoint X=-14 Y=-18 Z=0
    g45: LineSegment StartX=-6.2 StartY=0 StartZ=0 EndX=-7.2 EndY=0 EndZ=0
    g46: LineSegment StartX=-7.2 StartY=0 StartZ=0 EndX=-7.2 EndY=-2 EndZ=0
    g47: LineSegment StartX=-7.2 StartY=-2 StartZ=0 EndX=-6.2215 EndY=-2 EndZ=0
    g48: LineSegment StartX=-6.32538 StartY=-4 StartZ=0 EndX=-7.65538 EndY=-4 EndZ=0
    g49: LineSegment StartX=-7.65538 StartY=-4 StartZ=0 EndX=-7.65538 EndY=-5.99526 EndZ=0
    g50: LineSegment StartX=-7.65538 StartY=-5.99526 StartZ=0 EndX=-6.48644 EndY=-5.99526 EndZ=0
    g51: LineSegment StartX=-6.77343 StartY=-8 StartZ=0 EndX=-8.43343 EndY=-8 EndZ=0
    g52: LineSegment StartX=-8.43343 StartY=-8 StartZ=0 EndX=-8.43343 EndY=-10 EndZ=0
    g53: LineSegment StartX=-8.43343 StartY=-10 StartZ=0 EndX=-7.19003 EndY=-10 EndZ=0
  constraints (112):
    c: Horizontal(g0)
    c: Distance(g0) = 2
    c: Block(g0)
    c: Vertical(g1)
    c: Coincident(g2,g0)
    c: Vertical(g2)
    c: Block(g2)
    c: Coincident(g6,g2)
    c: Weight(g3) = 1
    c: Equal(g3,g4)
    c: Equal(g3,g5)
    c: InternalAlignment(g3,g6)
    c: InternalAlignment(g4,g6)
    c: InternalAlignment(g5,g6)
    c: InternalAlignment(g7,g6)
    c: InternalAlignment(g8,g6)
    c: Block(g6)
    c: Coincident(g9,g1)
    c: Coincident(g9,g6)
    c: Horizontal(g9)
    c: Vertical(g10)
    c: Block(g10)
    c: Horizontal(g11)
    c: Block(g11)
    c: Coincident(g12,g10)
    c: Horizontal(g12)
    c: Block(g12)
    c: Coincident(g13,g11)
    c: Vertical(g13)
    c: Block(g13)
    c: Coincident(g14,g10)
    c: Horizontal(g14)
    c: Block(g14)
    c: Block(g9)
    c: Block(g1)
    c: Weight(g15) = 1
    c: Equal(g15,g16)
    c: Equal(g15,g17)
    c: InternalAlignment(g15,g18)
    c: InternalAlignment(g16,g18)
    c: InternalAlignment(g17,g18)
    c: InternalAlignment(g19,g18)
    c: InternalAlignment(g20,g18)
    c: Weight(g21) = 1
    c: Equal(g21,g22)
    c: Equal(g21,g23)
    c: InternalAlignment(g21,g24)
    c: InternalAlignment(g22,g24)
    c: InternalAlignment(g23,g24)
    c: InternalAlignment(g25,g24)
    c: InternalAlignment(g26,g24)
    c: Weight(g27) = 1
    c: Equal(g27,g28)
    c: Equal(g27,g29)
    c: Coincident(g30,g14)
    c: InternalAlignment(g27,g30)
    c: InternalAlignment(g28,g30)
    c: InternalAlignment(g29,g30)
    c: InternalAlignment(g31,g30)
    c: InternalAlignment(g32,g30)
    c: Coincident(g36,g12)
    c: Weight(g33) = 1
    c: Equal(g33,g34)
    c: Equal(g33,g35)
    c: Coincident(g36,g11)
    c: InternalAlignment(g33,g36)
    c: InternalAlignment(g34,g36)
    c: InternalAlignment(g35,g36)
    c: InternalAlignment(g37,g36)
    c: InternalAlignment(g38,g36)
    c: Coincident(g42,g13)
    c: Weight(g39) = 1
    c: Equal(g39,g40)
    c: Equal(g39,g41)
    c: Coincident(g42,g1)
    c: InternalAlignment(g39,g42)
    c: InternalAlignment(g40,g42)
    c: InternalAlignment(g41,g42)
    c: InternalAlignment(g43,g42)
    c: InternalAlignment(g44,g42)
    c: Block(g18)
    c: Block(g24)
    c: Block(g30)
    c: Block(g36)
    c: Block(g42)
    c: Horizontal(g45)
    c: Coincident(g45,g0)
    c: Vertical(g46)
    c: Coincident(g46,g45)
    c: Coincident(g47,g46)
    c: Coincident(g47,g18)
    c: Horizontal(g47)
    c: Block(g46)
    c: Coincident(g48,g18)
    c: Horizontal(g48)
    c: Distance(g48) = 1.33
    c: Vertical(g49)
    c: Coincident(g49,g48)
    c: Coincident(g50,g49)
    c: Coincident(g50,g24)
    c: Horizontal(g50)
    c: Tangent(g50,g22)
    c: Horizontal(g51)
    c: Coincident(g51,g24)
    c: Block(g51)
    c: Vertical(g52)
    c: Block(g52)
    c: Coincident(g52,g51)
    c: Coincident(g53,g52)
    c: Coincident(g53,g30)
    c: Horizontal(g53)
    c: Distance(g1) = 8.5
FEATURE [Part::Feature] Face024
  shape: bbox 9.8 x 26.5 x 2e-07 mm, 1 faces, 0 solids (baked)
FEATURE [Part::Revolution] Revolve024
  Angle = 360
  Axis = (0,1,0)
  Base = (0,0,0)
  FaceMakerClass = Part::FaceMakerBullseye
  Placement = pos=(0,0,0) rot=(0,0,1;1.5708rad)
  Solid = false
  Source = -> Face024
  Symmetric = false
FEATURE [Part::Feature] Face025
  shape: bbox 9.8 x 26.5 x 2e-07 mm, 1 faces, 0 solids (baked)
FEATURE [Part::Revolution] Revolve025
  Angle = 360
  Axis = (0,1,0)
  Base = (0,0,0)
  FaceMakerClass = Part::FaceMakerBullseye
  Placement = pos=(0,0,0) rot=(0,0,1;1.5708rad)
  Solid = false
  Source = -> Face025
  Symmetric = false
FEATURE [Part::MultiFuse] Fusion033
  Placement = pos=(-18,19,36) rot=(0,0,1;0rad)
  Shapes = -> [Revolve025,Revolve024]
FEATURE [Part::Cylinder] Cylinder014
  Angle = 360
  AttacherType = Attacher::AttachEngine3D
  Height = 20
  Placement = pos=(0,0,36.15) rot=(0,0,1;0rad)
  Radius = 14.3
FEATURE [Part::Cylinder] Cylinder015
  Angle = 360
  AttacherType = Attacher::AttachEngine3D
  Height = 10
  Placement = pos=(0,0,36.15) rot=(0,0,1;0rad)
  Radius = 4
FEATURE [Part::MultiFuse] Fusion034  label="removeToCreteHoleForPlugHousing004"
  Placement = pos=(-42,19,36) rot=(0,1,0;1.5708rad)
  Shapes = -> [Cylinder014,Cylinder015]
FEATURE [Part::Cut] Cut008  label="top004"
  Base = -> Cut004
  Placement = pos=(-1,0,0) rot=(0,0,1;0rad)
  Tool = -> Fusion034
FEATURE [Part::Box] Box005  label="Cube005"
  AttacherType = Attacher::AttachEngine3D
  Height = 28
  Length = 3
  Placement = pos=(110.7,19,22) rot=(0,0,1;0rad)
  Width = 15.7
FEATURE [Part::Cylinder] Cylinder016
  Angle = 360
  AttacherType = Attacher::AttachEngine3D
  Height = 10
  Placement = pos=(0,0,36.15) rot=(0,0,1;0rad)
  Radius = 4
FEATURE [Part::Cylinder] Cylinder017
  Angle = 360
  AttacherType = Attacher::AttachEngine3D
  Height = 20
  Placement = pos=(0,0,36.15) rot=(0,0,1;0rad)
  Radius = 10.3
FEATURE [Part::MultiFuse] Fusion035  label="removeToCreteHoleForPlugHousing005"
  Placement = pos=(70,19,36) rot=(0,1,0;1.5708rad)
  Shapes = -> [Cylinder017,Cylinder016]
FEATURE [Part::Cut] Cut009  label="plugHousingTab001"
  Base = -> Box005
  Placement = pos=(-107.4,-14,0) rot=(0,0,1;0rad)
  Tool = -> Fusion035
FEATURE [Part::Box] Box006  label="Cube006"
  AttacherType = Attacher::AttachEngine3D
  Height = 28
  Length = 3
  Placement = pos=(110.7,19,22) rot=(0,0,1;0rad)
  Width = 15.7
FEATURE [Part::Cylinder] Cylinder018
  Angle = 360
  AttacherType = Attacher::AttachEngine3D
  Height = 10
  Placement = pos=(0,0,36.15) rot=(0,0,1;0rad)
  Radius = 4
FEATURE [Part::Cylinder] Cylinder019
  Angle = 360
  AttacherType = Attacher::AttachEngine3D
  Height = 20
  Placement = pos=(0,0,36.15) rot=(0,0,1;0rad)
  Radius = 10.3
FEATURE [Part::MultiFuse] Fusion036  label="removeToCreteHoleForPlugHousing006"
  Placement = pos=(70,19,36) rot=(0,1,0;1.5708rad)
  Shapes = -> [Cylinder019,Cylinder018]
FEATURE [Part::Cut] Cut010  label="plugHousingTab002"
  Base = -> Box006
  Placement = pos=(-107.4,-14,0) rot=(0,0,1;0rad)
  Tool = -> Fusion036
FEATURE [Part::MultiFuse] Fusion037
  Placement = pos=(9.6,23,0) rot=(0,0,1;3.14159rad)
  Shapes = -> [Cut009,Cut010]
FEATURE [Part::Box] Box  label="Cube"
  AttacherType = Attacher::AttachEngine3D
  Height = 10
  Length = 3
  Placement = pos=(3.3,4,12) rot=(0,0,1;0rad)
  Width = 10
FEATURE [Part::Fillet] Fillet004
  Base = -> Fusion028
  Edges = 1 edges r=2: [Edge25]
FEATURE [Part::Fillet] Fillet005  label="plugHousing046"
  Base = -> Fillet004
  Edges = 1 edges r=2: [Edge8]
FEATURE [Part::Fillet] Fillet006
  Base = -> Box
  Edges = 1 edges r=2: [Edge11]
FEATURE [Part::Box] Box007  label="Cube007"
  AttacherType = Attacher::AttachEngine3D
  Height = 10
  Length = 3
  Placement = pos=(3.3,4,50) rot=(0,0,1;0rad)
  Width = 10
FEATURE [Part::Fillet] Fillet007
  Base = -> Box007
  Edges = 1 edges r=2: [Edge12]
FEATURE [Part::Box] Box008  label="Cube008"
  AttacherType = Attacher::AttachEngine3D
  Height = 28
  Length = 4
  Placement = pos=(5,0,22) rot=(0,0,1;0rad)
  Width = 10
FEATURE [Part::Fillet] Fillet008
  Base = -> Box008
  Edges = 1 edges r=1: [Edge7]
FEATURE [Part::Fillet] Fillet009
  Base = -> Fillet008
  Edges = 1 edges r=2: [Edge5]
FEATURE [Part::Fillet] Fillet010
  Base = -> Fillet009
  Edges = 1 edges r=2: [Edge2]
FEATURE [Sketcher::SketchObject] Sketch009  label="topSketch003"
  FullyConstrained = true
  sketch-geometry (4):
    g0: LineSegment StartX=16.8446 StartY=31.512 StartZ=0 EndX=16.3251 EndY=34.4666 EndZ=0
    g1: ArcOfCircle CenterX=19 CenterY=19.2524 CenterZ=0 NormalX=0 NormalY=0 NormalZ=1 AngleXU=0 Radius=15.4476 StartAngle=1.74483 EndAngle=2.72717
    g2: ArcOfCircle CenterX=19 CenterY=19.2524 CenterZ=0 NormalX=0 NormalY=0 NormalZ=1 AngleXU=0 Radius=12.4476 StartAngle=1.74483 EndAngle=2.73189
    g3: LineSegment StartX=4.86004 StartY=25.4725 StartZ=0 EndX=7.58253 EndY=24.2107 EndZ=0
  constraints (7):
    c: Block(g0)
    c: Coincident(g1,g0)
    c: Coincident(g2,g0)
    c: Coincident(g3,g1)
    c: Coincident(g3,g2)
    c: Block(g1)
    c: Block(g2)
FEATURE [Part::Extrusion] Extrude008
  Base = -> Sketch009
  Dir = (0,0,1)
  DirMode = 2
  FaceMakerClass = Part::FaceMakerBullseye
  LengthFwd = 10
  LengthRev = 0
  Placement = pos=(0,0,31) rot=(0,0,1;0rad)
  Solid = true
  Symmetric = false
FEATURE [Part::Cylinder] Cylinder020
  Angle = 360
  AttacherType = Attacher::AttachEngine3D
  Height = 20
  Placement = pos=(0,0,36.15) rot=(0,0,1;0rad)
  Radius = 8.2
FEATURE [Part::Cylinder] Cylinder021
  Angle = 360
  AttacherType = Attacher::AttachEngine3D
  Height = 10
  Placement = pos=(0,0,36.15) rot=(0,0,1;0rad)
  Radius = 4
FEATURE [Part::MultiFuse] Fusion038  label="removeToCreteHoleForPlugHousing007"
  Placement = pos=(-42,19,36) rot=(0,1,0;1.5708rad)
  Shapes = -> [Cylinder020,Cylinder021]
FEATURE [Part::Cut] Cut011
  Base = -> Extrude008
  Tool = -> Fusion038
FEATURE [Part::Fillet] Fillet011
  Base = -> Cut011
  Edges = 1 edges r=2: [Edge1]
FEATURE [Part::Fillet] Fillet012
  Base = -> Fillet011
  Edges = 1 edges r=2.5: [Edge1]
FEATURE [Part::Fillet] Fillet013
  Base = -> Fillet012
  Edges = 1 edges r=2.5: [Edge2]
FEATURE [Part::Box] Box010  label="Cube010"
  AttacherType = Attacher::AttachEngine3D
  Height = 16
  Length = 8
  Placement = pos=(12.7,31.52,28) rot=(0,0,1;0rad)
  Width = 4
FEATURE [Sketcher::SketchObject] Sketch010  label="topSketch004"
  FullyConstrained = true
  sketch-geometry (4):
    g0: LineSegment StartX=16.8446 StartY=31.512 StartZ=0 EndX=16.3251 EndY=34.4666 EndZ=0
    g1: ArcOfCircle CenterX=19 CenterY=19.2524 CenterZ=0 NormalX=0 NormalY=0 NormalZ=1 AngleXU=0 Radius=15.4476 StartAngle=1.74483 EndAngle=2.72717
    g2: ArcOfCircle CenterX=19 CenterY=19.2524 CenterZ=0 NormalX=0 NormalY=0 NormalZ=1 AngleXU=0 Radius=12.4476 StartAngle=1.74483 EndAngle=2.73189
    g3: LineSegment StartX=4.86004 StartY=25.4725 StartZ=0 EndX=7.58253 EndY=24.2107 EndZ=0
  constraints (7):
    c: Block(g0)
    c: Coincident(g1,g0)
    c: Coincident(g2,g0)
    c: Coincident(g3,g1)
    c: Coincident(g3,g2)
    c: Block(g1)
    c: Block(g2)
FEATURE [Part::Cylinder] Cylinder022
  Angle = 360
  AttacherType = Attacher::AttachEngine3D
  Height = 10
  Placement = pos=(0,0,36.15) rot=(0,0,1;0rad)
  Radius = 4
FEATURE [Sketcher::SketchObject] Sketch011  label="topSketch005"
  FullyConstrained = true
  sketch-geometry (4):
    g0: LineSegment StartX=16.8446 StartY=31.512 StartZ=0 EndX=16.3251 EndY=34.4666 EndZ=0
    g1: ArcOfCircle CenterX=19 CenterY=19.2524 CenterZ=0 NormalX=0 NormalY=0 NormalZ=1 AngleXU=0 Radius=15.4476 StartAngle=1.74483 EndAngle=2.72717
    g2: ArcOfCircle CenterX=19 CenterY=19.2524 CenterZ=0 NormalX=0 NormalY=0 NormalZ=1 AngleXU=0 Radius=12.4476 StartAngle=1.74483 EndAngle=2.73189
    g3: LineSegment StartX=4.86004 StartY=25.4725 StartZ=0 EndX=7.58253 EndY=24.2107 EndZ=0
  constraints (7):
    c: Block(g0)
    c: Coincident(g1,g0)
    c: Coincident(g2,g0)
    c: Coincident(g3,g1)
    c: Coincident(g3,g2)
    c: Block(g1)
    c: Block(g2)
FEATURE [Part::Extrusion] Extrude010
  Base = -> Sketch011
  Dir = (0,0,1)
  DirMode = 2
  FaceMakerClass = Part::FaceMakerBullseye
  LengthFwd = 10.6
  LengthRev = 0
  Placement = pos=(0,0,31) rot=(0,0,1;0rad)
  Solid = true
  Symmetric = false
FEATURE [Part::Cylinder] Cylinder023
  Angle = 360
  AttacherType = Attacher::AttachEngine3D
  Height = 20
  Placement = pos=(0,0,36.15) rot=(0,0,1;0rad)
  Radius = 8.2
FEATURE [Part::MultiFuse] Fusion039  label="removeToCreteHoleForPlugHousing008"
  Placement = pos=(-42,19,36) rot=(0,1,0;1.5708rad)
  Shapes = -> [Cylinder023,Cylinder022]
FEATURE [Part::Cut] Cut012
  Base = -> Extrude010
  Placement = pos=(0,0,-0.3) rot=(0,0,1;0rad)
  Tool = -> Fusion039
FEATURE [Part::Cut] Cut013
  Base = -> Box010
  Tool = -> Cut012
FEATURE [Part::Fillet] Fillet014
  Base = -> Cut013
  Edges = 1 edges r=0.7: [Edge13]
FEATURE [Part::Fillet] Fillet015
  Base = -> Fillet014
  Edges = 1 edges r=0.7: [Edge13]
FEATURE [Part::Fillet] Fillet016
  Base = -> Fillet015
  Edges = 1 edges r=0.7: [Edge16]
FEATURE [Part::Fillet] Fillet017
  Base = -> Fillet016
  Edges = 1 edges r=0.7: [Edge11]
FEATURE [Part::Fillet] Fillet018
  Base = -> Fillet017
  Edges = 1 edges r=0.7: [Edge10]
FEATURE [Part::Fillet] Fillet019
  Base = -> Fillet018
  Edges = 1 edges r=1.2: [Edge5]
FEATURE [Part::Fillet] Fillet020
  Base = -> Fillet019
  Edges = 1 edges r=1.2: [Edge12]
FEATURE [Part::Fillet] Fillet021
  Base = -> Fillet020
  Edges = 1 edges r=2: [Edge1]
  Placement = pos=(0.3,0,0) rot=(0,0,1;0rad)
FEATURE [Part::MultiFuse] Fusion040  label="top005"
  Shapes = -> [Cut008,Fillet021]
FEATURE [Part::MultiFuse] Fusion041  label="wireHolder"
  Shapes = -> [Fusion033,Fillet013]
FEATURE [Part::MultiFuse] Fusion042
  Shapes = -> [Fillet007,Fusion041]
FEATURE [Part::MultiFuse] Fusion043  label="wireHolder001"
  Shapes = -> [Fusion042,Fillet010]
FEATURE [Part::MultiFuse] Fusion044  label="wireHolder002"
  Shapes = -> [Fillet006,Fusion037,Fusion043]
FEATURE [Part::Feature] Face026
  shape: bbox 11 x 6 x 2e-07 mm, 1 faces, 0 solids (baked)
FEATURE [Part::Revolution] Revolve026
  Angle = 360
  Axis = (0,1,0)
  Base = (0,0,0)
  FaceMakerClass = Part::FaceMakerBullseye
  Placement = pos=(30.3,-1,19.7) rot=(0,0,1;0rad)
  Solid = false
  Source = -> Face026
  Symmetric = false
FEATURE [Sketcher::SketchObject] Sketch013  label="topSketch006"
  FullyConstrained = true
  sketch-geometry (13):
    g0: LineSegment StartX=117 StartY=19 StartZ=0 EndX=117 EndY=38 EndZ=0
    g1: ArcOfCircle CenterX=98 CenterY=19 CenterZ=0 NormalX=0 NormalY=0 NormalZ=1 AngleXU=0 Radius=19 StartAngle=5.7297 EndAngle=6.28319
    g2: LineSegment StartX=0 StartY=3 StartZ=0 EndX=0 EndY=19 EndZ=0
    g3: LineSegment StartX=19 StartY=38 StartZ=0 EndX=117 EndY=38 EndZ=0
    g4: ArcOfCircle CenterX=19 CenterY=19 CenterZ=0 NormalX=0 NormalY=0 NormalZ=1 AngleXU=0 Radius=19 StartAngle=1.5708 EndAngle=3.14159
    g5: ArcOfCircle CenterX=19 CenterY=19 CenterZ=0 NormalX=0 NormalY=0 NormalZ=1 AngleXU=0 Radius=16 StartAngle=1.5708 EndAngle=3.14159
    g6: ArcOfCircle CenterX=98 CenterY=19 CenterZ=0 NormalX=0 NormalY=0 NormalZ=1 AngleXU=0 Radius=16 StartAngle=5.60905 EndAngle=6.28319
    g7: LineSegment StartX=114 StartY=19 StartZ=0 EndX=114 EndY=35 EndZ=0
    g8: LineSegment StartX=110.5 StartY=9.01251 StartZ=0 EndX=114.163 EndY=9.01251 EndZ=0
    g9: LineSegment StartX=114 StartY=35 StartZ=0 EndX=19 EndY=35 EndZ=0
    g10: LineSegment StartX=0 StartY=3 StartZ=0 EndX=0 EndY=0 EndZ=0
    g11: LineSegment StartX=3 StartY=0 StartZ=0 EndX=0 EndY=0 EndZ=0
    g12: LineSegment StartX=3 StartY=19 StartZ=0 EndX=3 EndY=0 EndZ=0
  constraints (33):
    c: Vertical(g0)
    c: Distance(g0) = 19
    c: Block(g0)
    c: Coincident(g1,g0)
    c: Block(g1)
    c: Vertical(g2)
    c: Block(g2)
    c: Coincident(g3,g0)
    c: Horizontal(g3)
    c: Distance(g3) = 98
    c: Coincident(g4,g3)
    c: Coincident(g4,g2)
    c: Block(g4)
    c: Coincident(g5,g4)
    c: Coincident(g6,g1)
    c: Block(g6)
    c: Block(g5)
    c: Coincident(g7,g6)
    c: Vertical(g7)
    c: Coincident(g8,g6)
    c: Coincident(g8,g1)
    c: Coincident(g9,g7)
    c: Coincident(g9,g5)
    c: Horizontal(g9)
    c: Tangent(g9,g5)
    c: Coincident(g10,g2)
    c: Distance(g10) = 3
    c: Vertical(g10)
    c: Coincident(g11,g10)
    c: Horizontal(g11)
    c: Coincident(g12,g5)
    c: Coincident(g12,g11)
    c: Vertical(g12)
FEATURE [Part::Extrusion] Extrude011  label="top006"
  Base = -> Sketch013
  Dir = (0,0,1)
  DirMode = 2
  FaceMakerClass = Part::FaceMakerBullseye
  LengthFwd = 72
  LengthRev = 0
  Solid = true
  Symmetric = false
FEATURE [Sketcher::SketchObject] Sketch014
  FullyConstrained = true
  MapMode = 3
  Placement = pos=(0,0,0) rot=(1,0,0;1.5708rad)
  Support = -> [Extrude011]
  sketch-geometry (8):
    g0: Circle CenterX=80.351 CenterY=-67.6202 CenterZ=0 NormalX=0 NormalY=0 NormalZ=1 AngleXU=0 Radius=2
    g1: Circle CenterX=80.351 CenterY=-67.6202 CenterZ=0 NormalX=0 NormalY=0 NormalZ=1 AngleXU=0 Radius=3
    g2: Circle CenterX=80.351 CenterY=-4.92017 CenterZ=0 NormalX=0 NormalY=0 NormalZ=1 AngleXU=0 Radius=2
    g3: Circle CenterX=80.351 CenterY=-4.92017 CenterZ=0 NormalX=0 NormalY=0 NormalZ=1 AngleXU=0 Radius=3
    g4: Circle CenterX=23.851 CenterY=-4.92017 CenterZ=0 NormalX=0 NormalY=0 NormalZ=1 AngleXU=0 Radius=2
    g5: Circle CenterX=23.851 CenterY=-4.92017 CenterZ=0 NormalX=0 NormalY=0 NormalZ=1 AngleXU=0 Radius=3
    g6: Circle CenterX=23.851 CenterY=-67.6202 CenterZ=0 NormalX=0 NormalY=0 NormalZ=1 AngleXU=0 Radius=2
    g7: Circle CenterX=23.851 CenterY=-67.6202 CenterZ=0 NormalX=0 NormalY=0 NormalZ=1 AngleXU=0 Radius=3
  constraints (8):
    c: Block(g3)
    c: Block(g2)
    c: Block(g1)
    c: Block(g0)
    c: Block(g6)
    c: Block(g7)
    c: Block(g4)
    c: Block(g5)
FEATURE [Part::Feature] Face027
  shape: bbox 11 x 6 x 2e-07 mm, 1 faces, 0 solids (baked)
FEATURE [Part::Revolution] Revolve027
  Angle = 360
  Axis = (0,1,0)
  Base = (0,0,0)
  FaceMakerClass = Part::FaceMakerBullseye
  Placement = pos=(30.3,-1,51.7) rot=(0,0,1;0rad)
  Solid = false
  Source = -> Face027
  Symmetric = false
FEATURE [Part::Feature] Face028
  shape: bbox 11 x 6 x 2e-07 mm, 1 faces, 0 solids (baked)
FEATURE [Part::Revolution] Revolve028
  Angle = 360
  Axis = (0,1,0)
  Base = (0,0,0)
  FaceMakerClass = Part::FaceMakerBullseye
  Placement = pos=(62.3,-1,19.7) rot=(0,0,1;0rad)
  Solid = false
  Source = -> Face028
  Symmetric = false
FEATURE [Part::Feature] Face029
  shape: bbox 11 x 6 x 2e-07 mm, 1 faces, 0 solids (baked)
FEATURE [Part::Revolution] Revolve029
  Angle = 360
  Axis = (0,1,0)
  Base = (0,0,0)
  FaceMakerClass = Part::FaceMakerBullseye
  Placement = pos=(62.3,-1,51.7) rot=(0,0,1;0rad)
  Solid = false
  Source = -> Face029
  Symmetric = false
FEATURE [Part::Feature] Wire
  shape: bbox 11 x 5.2 x 2e-07 mm, 0 faces, 0 solids (baked)
FEATURE [Part::Revolution] Revolve030
  Angle = 360
  Axis = (0,1,0)
  Base = (0,0,0)
  FaceMakerClass = Part::FaceMakerBullseye
  Placement = pos=(30.3,38,19.7) rot=(0,0,1;0rad)
  Solid = true
  Source = -> Wire
  Symmetric = false
FEATURE [Part::Feature] Wire001
  shape: bbox 11 x 5.2 x 2e-07 mm, 0 faces, 0 solids (baked)
FEATURE [Part::Revolution] Revolve031
  Angle = 360
  Axis = (0,1,0)
  Base = (0,0,0)
  FaceMakerClass = Part::FaceMakerBullseye
  Placement = pos=(30.3,38,51.7) rot=(0,0,1;0rad)
  Solid = true
  Source = -> Wire001
  Symmetric = false
FEATURE [Part::Feature] Wire002
  shape: bbox 11 x 5.2 x 2e-07 mm, 0 faces, 0 solids (baked)
FEATURE [Part::Revolution] Revolve032
  Angle = 360
  Axis = (0,1,0)
  Base = (0,0,0)
  FaceMakerClass = Part::FaceMakerBullseye
  Placement = pos=(62.3,38,51.7) rot=(0,0,1;0rad)
  Solid = true
  Source = -> Wire002
  Symmetric = false
FEATURE [Part::Feature] Wire003
  shape: bbox 11 x 5.2 x 2e-07 mm, 0 faces, 0 solids (baked)
FEATURE [Part::Revolution] Revolve033
  Angle = 360
  Axis = (0,1,0)
  Base = (0,0,0)
  FaceMakerClass = Part::FaceMakerBullseye
  Placement = pos=(62.3,38,19.7) rot=(0,0,1;0rad)
  Solid = true
  Source = -> Wire003
  Symmetric = false
FEATURE [Part::MultiFuse] Fusion045  label="altRandScrewHousing"
  Shapes = -> [Revolve029,Revolve027,Revolve028,Revolve026]
FEATURE [Part::MultiFuse] Fusion046  label="fanScrewHousing"
  Shapes = -> [Revolve033,Revolve032,Revolve031,Revolve030]
FEATURE [Sketcher::SketchObject] Sketch015
  FullyConstrained = true
  sketch-geometry (17):
    g0: Circle CenterX=-3.5 CenterY=23.5 CenterZ=0 NormalX=0 NormalY=0 NormalZ=1 AngleXU=0 Radius=1
    g1: Circle CenterX=-1 CenterY=15.25 CenterZ=0 NormalX=0 NormalY=0 NormalZ=1 AngleXU=0 Radius=1
    g2: Circle CenterX=-3.5 CenterY=7 CenterZ=0 NormalX=0 NormalY=0 NormalZ=1 AngleXU=0 Radius=1
    g3: BSplineCurve PolesCount=3 KnotsCount=2 Degree=2 IsPeriodic=0
    g4: GeomPoint X=-3.5 Y=23.5 Z=0
    g5: GeomPoint X=-3.5 Y=7 Z=0
    g6: Circle CenterX=-4.8 CenterY=30.5 CenterZ=0 NormalX=0 NormalY=0 NormalZ=1 AngleXU=0 Radius=1
    g7: Circle CenterX=-3.5 CenterY=30.5 CenterZ=0 NormalX=0 NormalY=0 NormalZ=1 AngleXU=0 Radius=1
    g8: Circle CenterX=-3.5 CenterY=29.2 CenterZ=0 NormalX=0 NormalY=0 NormalZ=1 AngleXU=0 Radius=1
    g9: BSplineCurve PolesCount=3 KnotsCount=2 Degree=2 IsPeriodic=0
    g10: GeomPoint X=-4.8 Y=30.5 Z=0
    g11: GeomPoint X=-3.5 Y=29.2 Z=0
    g12: LineSegment StartX=-3.5 StartY=29.2 StartZ=0 EndX=-3.5 EndY=23.5 EndZ=0
    g13: LineSegment StartX=-4.8 StartY=30.5 StartZ=0 EndX=0 EndY=30.5 EndZ=0
    g14: LineSegment StartX=-3.5 StartY=0.3 StartZ=0 EndX=0 EndY=0.3 EndZ=0
    g15: LineSegment StartX=-3.5 StartY=0.3 StartZ=0 EndX=-3.5 EndY=7 EndZ=0
    g16: LineSegment StartX=0 StartY=0.3 StartZ=0 EndX=0 EndY=30.5 EndZ=0
  constraints (34):
    c: Weight(g0) = 1
    c: Equal(g0,g1)
    c: Equal(g0,g2)
    c: InternalAlignment(g0,g3)
    c: InternalAlignment(g1,g3)
    c: InternalAlignment(g2,g3)
    c: InternalAlignment(g4,g3)
    c: InternalAlignment(g5,g3)
    c: Block(g3)
    c: Weight(g6) = 1
    c: Equal(g6,g7)
    c: Equal(g6,g8)
    c: InternalAlignment(g6,g9)
    c: InternalAlignment(g7,g9)
    c: InternalAlignment(g8,g9)
    c: InternalAlignment(g10,g9)
    c: InternalAlignment(g11,g9)
    c: Block(g9)
    c: Coincident(g12,g9)
    c: Coincident(g12,g3)
    c: Vertical(g12)
    c: Coincident(g13,g9)
    c: Horizontal(g13)
    c: Distance(g13) = 4.8
    c: Horizontal(g14)
    c: Block(g14)
    c: Coincident(g15,g14)
    c: Coincident(g15,g3)
    c: Vertical(g15)
    c: Coincident(g16,g14)
    c: Coincident(g16,g13)
    c: Vertical(g16)
    c: Tangent(g16,g1)
    c: Distance(g14) = 3.5
FEATURE [Sketcher::SketchObject] Sketch016
  FullyConstrained = true
  sketch-geometry (16):
    g0: Circle CenterX=-3.5 CenterY=23.5 CenterZ=0 NormalX=0 NormalY=0 NormalZ=1 AngleXU=0 Radius=1
    g1: Circle CenterX=-1 CenterY=15.25 CenterZ=0 NormalX=0 NormalY=0 NormalZ=1 AngleXU=0 Radius=1
    g2: Circle CenterX=-3.5 CenterY=7 CenterZ=0 NormalX=0 NormalY=0 NormalZ=1 AngleXU=0 Radius=1
    g3: BSplineCurve PolesCount=3 KnotsCount=2 Degree=2 IsPeriodic=0
    g4: GeomPoint X=-3.5 Y=23.5 Z=0
    g5: GeomPoint X=-3.5 Y=7 Z=0
    g6: LineSegment StartX=-3.5 StartY=28.2 StartZ=0 EndX=-3.5 EndY=23.5 EndZ=0
    g7: LineSegment StartX=0 StartY=29.5 StartZ=0 EndX=0 EndY=30 EndZ=0
    g8: LineSegment StartX=-3.5 StartY=28.2 StartZ=0 EndX=-3.5 EndY=30 EndZ=0
    g9: LineSegment StartX=0 StartY=30 StartZ=0 EndX=0 EndY=30.5 EndZ=0
    g10: LineSegment StartX=0 StartY=30.5 StartZ=0 EndX=-3.5 EndY=30.5 EndZ=0
    g11: LineSegment StartX=-3.5 StartY=30.5 StartZ=0 EndX=-3.5 EndY=30 EndZ=0
    g12: LineSegment StartX=0 StartY=29.5 StartZ=0 EndX=0 EndY=5 EndZ=0
    g13: LineSegment StartX=-3.5 StartY=0.3 StartZ=0 EndX=-3.5 EndY=7 EndZ=0
    g14: LineSegment StartX=-3.5 StartY=0.3 StartZ=0 EndX=0 EndY=0.3 EndZ=0
    g15: LineSegment StartX=0 StartY=5 StartZ=0 EndX=0 EndY=0.3 EndZ=0
  constraints (39):
    c: Weight(g0) = 1
    c: Equal(g0,g1)
    c: Equal(g0,g2)
    c: InternalAlignment(g0,g3)
    c: InternalAlignment(g1,g3)
    c: InternalAlignment(g2,g3)
    c: InternalAlignment(g4,g3)
    c: InternalAlignment(g5,g3)
    c: Block(g3)
    c: Coincident(g6,g3)
    c: Vertical(g6)
    c: Vertical(g7)
    c: Distance(g7) = 0.5
    c: Coincident(g8,g6)
    c: Vertical(g8)
    c: Block(g6)
    c: Block(g7)
    c: Vertical(g9)
    c: Equal(g7,g9) = 0.5
    c: Block(g9)
    c: Coincident(g9,g7)
    c: Horizontal(g10)
    c: Coincident(g10,g9)
    c: Coincident(g11,g10)
    c: Coincident(g11,g8)
    c: Vertical(g11)
    c: Block(g11)
    c: Coincident(g12,g7)
    c: Vertical(g12)
    c: Coincident(g13,g3)
    c: Vertical(g13)
    c: Distance(g13) = 6.7
    c: Coincident(g14,g13)
    c: Horizontal(g14)
    c: Block(g14)
    c: Coincident(g15,g12)
    c: Coincident(g15,g14)
    c: Vertical(g15)
    c: Block(g15)
FEATURE [Sketcher::SketchObject] Sketch017
  FullyConstrained = true
  sketch-geometry (11):
    g0: LineSegment StartX=-3.5 StartY=1e-16 StartZ=0 EndX=-1.6 EndY=1e-16 EndZ=0
    g1: LineSegment StartX=-1.6 StartY=1e-16 StartZ=0 EndX=-1.6 EndY=1.5 EndZ=0
    g2: LineSegment StartX=-3.5 StartY=1.5 StartZ=0 EndX=-1.6 EndY=1.5 EndZ=0
    g3: LineSegment StartX=-3.5 StartY=1e-16 StartZ=0 EndX=-4.8 EndY=1e-16 EndZ=0
    g4: Circle CenterX=-3.5 CenterY=1.3 CenterZ=0 NormalX=0 NormalY=0 NormalZ=1 AngleXU=0 Radius=1
    g5: Circle CenterX=-3.5 CenterY=1e-16 CenterZ=0 NormalX=0 NormalY=0 NormalZ=1 AngleXU=0 Radius=1
    g6: Circle CenterX=-4.8 CenterY=1e-16 CenterZ=0 NormalX=0 NormalY=0 NormalZ=1 AngleXU=0 Radius=1
    g7: BSplineCurve PolesCount=3 KnotsCount=2 Degree=2 IsPeriodic=0
    g8: GeomPoint X=-3.5 Y=1.3 Z=0
    g9: GeomPoint X=-4.8 Y=1e-16 Z=0
    g10: LineSegment StartX=-3.5 StartY=1.3 StartZ=0 EndX=-3.5 EndY=1.5 EndZ=0
  constraints (24):
    c: Horizontal(g0)
    c: Distance(g0) = 1.9
    c: Block(g0)
    c: Coincident(g1,g0)
    c: Vertical(g1)
    c: Coincident(g2,g1)
    c: Horizontal(g2)
    c: Coincident(g3,g0)
    c: Horizontal(g3)
    c: Distance(g3) = 1.3
    c: Weight(g4) = 1
    c: Equal(g4,g5)
    c: Coincident(g5,g0)
    c: Equal(g4,g6)
    c: Coincident(g7,g3)
    c: InternalAlignment(g4,g7)
    c: InternalAlignment(g5,g7)
    c: InternalAlignment(g6,g7)
    c: InternalAlignment(g8,g7)
    c: InternalAlignment(g9,g7)
    c: Coincident(g10,g7)
    c: Coincident(g10,g2)
    c: Vertical(g10)
    c: Block(g10)
FEATURE [Part::Feature] Face035
  shape: bbox 3.2 x 1.5 x 2e-07 mm, 1 faces, 0 solids (baked)
FEATURE [Part::Revolution] Revolve039  label="backCaseScrewRetainer"
  Angle = 360
  Axis = (0,1,0)
  Base = (0,0,0)
  FaceMakerClass = Part::FaceMakerBullseye
  Placement = pos=(12.5,3,62) rot=(0,0,1;0rad)
  Solid = false
  Source = -> Face035
  Symmetric = false
FEATURE [Part::Feature] Face036
  shape: bbox 3.2 x 1.5 x 2e-07 mm, 1 faces, 0 solids (baked)
FEATURE [Part::Feature] Face039
  shape: bbox 4.8 x 30.2 x 2e-07 mm, 1 faces, 0 solids (baked)
FEATURE [Part::Revolution] Revolve043  label="frontCaseScrewPost002"
  Angle = 360
  Axis = (0,1,0)
  Base = (0,0,0)
  FaceMakerClass = Part::FaceMakerBullseye
  Placement = pos=(89.5,4.5,3.5) rot=(0,0,1;0rad)
  Solid = false
  Source = -> Face039
  Symmetric = false
FEATURE [Part::Feature] Face042
  shape: bbox 4.8 x 30.2 x 2e-07 mm, 1 faces, 0 solids (baked)
FEATURE [Part::Revolution] Revolve046  label="frontCaseScrewPost003"
  Angle = 360
  Axis = (0,1,0)
  Base = (0,0,0)
  FaceMakerClass = Part::FaceMakerBullseye
  Placement = pos=(89.5,4.5,68.5) rot=(0,0,1;0rad)
  Solid = false
  Source = -> Face042
  Symmetric = false
FEATURE [Part::Feature] Face043
  shape: bbox 3.2 x 1.5 x 2e-07 mm, 1 faces, 0 solids (baked)
FEATURE [Part::Revolution] Revolve047  label="frontCaseScrewRetainer002"
  Angle = 360
  Axis = (0,1,0)
  Base = (0,0,0)
  FaceMakerClass = Part::FaceMakerBullseye
  Placement = pos=(89.5,3,68.5) rot=(0,0,1;0rad)
  Solid = false
  Source = -> Face043
  Symmetric = false
FEATURE [Part::Feature] Face044
  shape: bbox 3.2 x 1.5 x 2e-07 mm, 1 faces, 0 solids (baked)
FEATURE [Part::Revolution] Revolve048  label="frontCaseScrewRetainer003"
  Angle = 360
  Axis = (0,1,0)
  Base = (0,0,0)
  FaceMakerClass = Part::FaceMakerBullseye
  Placement = pos=(89.5,3,3.5) rot=(0,0,1;0rad)
  Solid = false
  Source = -> Face044
  Symmetric = false
FEATURE [App::MeasureDistance] Distance002  label="Distance: 1.67 mm"
  Distance = 1.66921
  P1 = (99.2361,4.7524,71.7)
  P2 = (99.2347,6.42161,71.7)
FEATURE [Sketcher::SketchObject] Sketch018
  FullyConstrained = true
  sketch-geometry (7):
    g0: LineSegment StartX=0 StartY=0 StartZ=0 EndX=0 EndY=6 EndZ=0
    g1: Circle CenterX=0 CenterY=0 CenterZ=0 NormalX=0 NormalY=0 NormalZ=1 AngleXU=0 Radius=1
    g2: Circle CenterX=8 CenterY=6 CenterZ=0 NormalX=0 NormalY=0 NormalZ=1 AngleXU=0 Radius=1
    g3: BSplineCurve PolesCount=3 KnotsCount=2 Degree=2 IsPeriodic=0
    g4: GeomPoint X=0 Y=0 Z=0
    g5: GeomPoint X=8 Y=6 Z=0
    g6: LineSegment StartX=0 StartY=6 StartZ=0 EndX=8 EndY=6 EndZ=0
  constraints (14):
    c: Coincident(g0,g-1)
    c: Distance(g0) = 6
    c: Vertical(g0)
    c: Coincident(g3,g0)
    c: Weight(g1) = 1
    c: Equal(g1,g2)
    c: InternalAlignment(g1,g3)
    c: InternalAlignment(g2,g3)
    c: InternalAlignment(g4,g3)
    c: InternalAlignment(g5,g3)
    c: Block(g3)
    c: Coincident(g6,g0)
    c: Coincident(g6,g3)
    c: Horizontal(g6)
FEATURE [Part::Extrusion] Extrude012  label="caseScrewPillarBracket"
  Base = -> Sketch018
  Dir = (0,0,1)
  DirMode = 2
  FaceMakerClass = Part::FaceMakerBullseye
  LengthFwd = 2.4
  LengthRev = 0
  Placement = pos=(15.76,29,8.8) rot=(0,1,0;0rad)
  Solid = true
  Symmetric = false
FEATURE [Sketcher::SketchObject] Sketch019
  FullyConstrained = true
  sketch-geometry (7):
    g0: LineSegment StartX=0 StartY=0 StartZ=0 EndX=0 EndY=6 EndZ=0
    g1: Circle CenterX=0 CenterY=0 CenterZ=0 NormalX=0 NormalY=0 NormalZ=1 AngleXU=0 Radius=1
    g2: Circle CenterX=8 CenterY=6 CenterZ=0 NormalX=0 NormalY=0 NormalZ=1 AngleXU=0 Radius=1
    g3: BSplineCurve PolesCount=3 KnotsCount=2 Degree=2 IsPeriodic=0
    g4: GeomPoint X=0 Y=0 Z=0
    g5: GeomPoint X=8 Y=6 Z=0
    g6: LineSegment StartX=0 StartY=6 StartZ=0 EndX=8 EndY=6 EndZ=0
  constraints (14):
    c: Coincident(g0,g-1)
    c: Distance(g0) = 6
    c: Vertical(g0)
    c: Coincident(g3,g0)
    c: Weight(g1) = 1
    c: Equal(g1,g2)
    c: InternalAlignment(g1,g3)
    c: InternalAlignment(g2,g3)
    c: InternalAlignment(g4,g3)
    c: InternalAlignment(g5,g3)
    c: Block(g3)
    c: Coincident(g6,g0)
    c: Coincident(g6,g3)
    c: Horizontal(g6)
FEATURE [Part::Extrusion] Extrude013  label="caseScrewPillarBracket001"
  Base = -> Sketch019
  Dir = (0,0,1)
  DirMode = 2
  FaceMakerClass = Part::FaceMakerBullseye
  LengthFwd = 2.4
  LengthRev = 0
  Placement = pos=(15.76,29,60.8) rot=(0,0,1;0rad)
  Solid = true
  Symmetric = false
FEATURE [Sketcher::SketchObject] Sketch020
  FullyConstrained = true
  sketch-geometry (7):
    g0: LineSegment StartX=0 StartY=0 StartZ=0 EndX=0 EndY=6 EndZ=0
    g1: Circle CenterX=0 CenterY=0 CenterZ=0 NormalX=0 NormalY=0 NormalZ=1 AngleXU=0 Radius=1
    g2: Circle CenterX=8 CenterY=6 CenterZ=0 NormalX=0 NormalY=0 NormalZ=1 AngleXU=0 Radius=1
    g3: BSplineCurve PolesCount=3 KnotsCount=2 Degree=2 IsPeriodic=0
    g4: GeomPoint X=0 Y=0 Z=0
    g5: GeomPoint X=8 Y=6 Z=0
    g6: LineSegment StartX=0 StartY=6 StartZ=0 EndX=8 EndY=6 EndZ=0
  constraints (14):
    c: Coincident(g0,g-1)
    c: Distance(g0) = 6
    c: Vertical(g0)
    c: Coincident(g3,g0)
    c: Weight(g1) = 1
    c: Equal(g1,g2)
    c: InternalAlignment(g1,g3)
    c: InternalAlignment(g2,g3)
    c: InternalAlignment(g4,g3)
    c: InternalAlignment(g5,g3)
    c: Block(g3)
    c: Coincident(g6,g0)
    c: Coincident(g6,g3)
    c: Horizontal(g6)
FEATURE [Part::Extrusion] Extrude014  label="caseScrewPillarBracket002"
  Base = -> Sketch020
  Dir = (0,0,1)
  DirMode = 2
  FaceMakerClass = Part::FaceMakerBullseye
  LengthFwd = 2.4
  LengthRev = 0
  Placement = pos=(13.7,29,13.26) rot=(0,-1,0;1.5708rad)
  Solid = true
  Symmetric = false
FEATURE [Sketcher::SketchObject] Sketch021
  FullyConstrained = true
  sketch-geometry (7):
    g0: LineSegment StartX=0 StartY=0 StartZ=0 EndX=0 EndY=6 EndZ=0
    g1: Circle CenterX=0 CenterY=0 CenterZ=0 NormalX=0 NormalY=0 NormalZ=1 AngleXU=0 Radius=1
    g2: Circle CenterX=8 CenterY=6 CenterZ=0 NormalX=0 NormalY=0 NormalZ=1 AngleXU=0 Radius=1
    g3: BSplineCurve PolesCount=3 KnotsCount=2 Degree=2 IsPeriodic=0
    g4: GeomPoint X=0 Y=0 Z=0
    g5: GeomPoint X=8 Y=6 Z=0
    g6: LineSegment StartX=0 StartY=6 StartZ=0 EndX=8 EndY=6 EndZ=0
  constraints (14):
    c: Coincident(g0,g-1)
    c: Distance(g0) = 6
    c: Vertical(g0)
    c: Coincident(g3,g0)
    c: Weight(g1) = 1
    c: Equal(g1,g2)
    c: InternalAlignment(g1,g3)
    c: InternalAlignment(g2,g3)
    c: InternalAlignment(g4,g3)
    c: InternalAlignment(g5,g3)
    c: Block(g3)
    c: Coincident(g6,g0)
    c: Coincident(g6,g3)
    c: Horizontal(g6)
FEATURE [Part::Extrusion] Extrude015  label="caseScrewPillarBracket003"
  Base = -> Sketch021
  Dir = (0,0,1)
  DirMode = 2
  FaceMakerClass = Part::FaceMakerBullseye
  LengthFwd = 2.4
  LengthRev = 0
  Placement = pos=(11.3,29,58.74) rot=(0,1,0;1.5708rad)
  Solid = true
  Symmetric = false
FEATURE [Sketcher::SketchObject] Sketch022
  FullyConstrained = true
  sketch-geometry (7):
    g0: LineSegment StartX=0 StartY=0 StartZ=0 EndX=0 EndY=6 EndZ=0
    g1: Circle CenterX=0 CenterY=0 CenterZ=0 NormalX=0 NormalY=0 NormalZ=1 AngleXU=0 Radius=1
    g2: Circle CenterX=8 CenterY=6 CenterZ=0 NormalX=0 NormalY=0 NormalZ=1 AngleXU=0 Radius=1
    g3: BSplineCurve PolesCount=3 KnotsCount=2 Degree=2 IsPeriodic=0
    g4: GeomPoint X=0 Y=0 Z=0
    g5: GeomPoint X=8 Y=6 Z=0
    g6: LineSegment StartX=0 StartY=6 StartZ=0 EndX=8 EndY=6 EndZ=0
  constraints (14):
    c: Coincident(g0,g-1)
    c: Distance(g0) = 6
    c: Vertical(g0)
    c: Coincident(g3,g0)
    c: Weight(g1) = 1
    c: Equal(g1,g2)
    c: InternalAlignment(g1,g3)
    c: InternalAlignment(g2,g3)
    c: InternalAlignment(g4,g3)
    c: InternalAlignment(g5,g3)
    c: Block(g3)
    c: Coincident(g6,g0)
    c: Coincident(g6,g3)
    c: Horizontal(g6)
FEATURE [Part::Extrusion] Extrude016  label="caseScrewPillarBracket004"
  Base = -> Sketch022
  Dir = (0,0,1)
  DirMode = 2
  FaceMakerClass = Part::FaceMakerBullseye
  LengthFwd = 2.4
  LengthRev = 0
  Placement = pos=(88.3,29,65.23) rot=(0,1,0;1.5708rad)
  Solid = true
  Symmetric = false
FEATURE [Sketcher::SketchObject] Sketch023
  FullyConstrained = true
  sketch-geometry (7):
    g0: LineSegment StartX=0 StartY=0 StartZ=0 EndX=0 EndY=6 EndZ=0
    g1: Circle CenterX=0 CenterY=0 CenterZ=0 NormalX=0 NormalY=0 NormalZ=1 AngleXU=0 Radius=1
    g2: Circle CenterX=8 CenterY=6 CenterZ=0 NormalX=0 NormalY=0 NormalZ=1 AngleXU=0 Radius=1
    g3: BSplineCurve PolesCount=3 KnotsCount=2 Degree=2 IsPeriodic=0
    g4: GeomPoint X=0 Y=0 Z=0
    g5: GeomPoint X=8 Y=6 Z=0
    g6: LineSegment StartX=0 StartY=6 StartZ=0 EndX=8 EndY=6 EndZ=0
  constraints (14):
    c: Coincident(g0,g-1)
    c: Distance(g0) = 6
    c: Vertical(g0)
    c: Coincident(g3,g0)
    c: Weight(g1) = 1
    c: Equal(g1,g2)
    c: InternalAlignment(g1,g3)
    c: InternalAlignment(g2,g3)
    c: InternalAlignment(g4,g3)
    c: InternalAlignment(g5,g3)
    c: Block(g3)
    c: Coincident(g6,g0)
    c: Coincident(g6,g3)
    c: Horizontal(g6)
FEATURE [Part::Extrusion] Extrude017  label="caseScrewPillarBracket005"
  Base = -> Sketch023
  Dir = (0,0,1)
  DirMode = 2
  FaceMakerClass = Part::FaceMakerBullseye
  LengthFwd = 2.4
  LengthRev = 0
  Placement = pos=(90.7,29,6.77) rot=(0,-1,0;1.5708rad)
  Solid = true
  Symmetric = false
FEATURE [Sketcher::SketchObject] Sketch024
  FullyConstrained = true
  sketch-geometry (7):
    g0: LineSegment StartX=0 StartY=0 StartZ=0 EndX=0 EndY=6 EndZ=0
    g1: Circle CenterX=0 CenterY=0 CenterZ=0 NormalX=0 NormalY=0 NormalZ=1 AngleXU=0 Radius=1
    g2: Circle CenterX=8 CenterY=6 CenterZ=0 NormalX=0 NormalY=0 NormalZ=1 AngleXU=0 Radius=1
    g3: BSplineCurve PolesCount=3 KnotsCount=2 Degree=2 IsPeriodic=0
    g4: GeomPoint X=0 Y=0 Z=0
    g5: GeomPoint X=8 Y=6 Z=0
    g6: LineSegment StartX=0 StartY=6 StartZ=0 EndX=8 EndY=6 EndZ=0
  constraints (14):
    c: Coincident(g0,g-1)
    c: Distance(g0) = 6
    c: Vertical(g0)
    c: Coincident(g3,g0)
    c: Weight(g1) = 1
    c: Equal(g1,g2)
    c: InternalAlignment(g1,g3)
    c: InternalAlignment(g2,g3)
    c: InternalAlignment(g4,g3)
    c: InternalAlignment(g5,g3)
    c: Block(g3)
    c: Coincident(g6,g0)
    c: Coincident(g6,g3)
    c: Horizontal(g6)
FEATURE [Part::Extrusion] Extrude018  label="caseScrewPillarBracket006"
  Base = -> Sketch024
  Dir = (0,0,1)
  DirMode = 2
  FaceMakerClass = Part::FaceMakerBullseye
  LengthFwd = 2.4
  LengthRev = 0
  Placement = pos=(103.7,29,6.77) rot=(0,-1,0;1.5708rad)
  Solid = true
  Symmetric = false
FEATURE [Sketcher::SketchObject] Sketch025
  FullyConstrained = true
  sketch-geometry (7):
    g0: LineSegment StartX=0 StartY=0 StartZ=0 EndX=0 EndY=6 EndZ=0
    g1: Circle CenterX=0 CenterY=0 CenterZ=0 NormalX=0 NormalY=0 NormalZ=1 AngleXU=0 Radius=1
    g2: Circle CenterX=8 CenterY=6 CenterZ=0 NormalX=0 NormalY=0 NormalZ=1 AngleXU=0 Radius=1
    g3: BSplineCurve PolesCount=3 KnotsCount=2 Degree=2 IsPeriodic=0
    g4: GeomPoint X=0 Y=0 Z=0
    g5: GeomPoint X=8 Y=6 Z=0
    g6: LineSegment StartX=0 StartY=6 StartZ=0 EndX=8 EndY=6 EndZ=0
  constraints (14):
    c: Coincident(g0,g-1)
    c: Distance(g0) = 6
    c: Vertical(g0)
    c: Coincident(g3,g0)
    c: Weight(g1) = 1
    c: Equal(g1,g2)
    c: InternalAlignment(g1,g3)
    c: InternalAlignment(g2,g3)
    c: InternalAlignment(g4,g3)
    c: InternalAlignment(g5,g3)
    c: Block(g3)
    c: Coincident(g6,g0)
    c: Coincident(g6,g3)
    c: Horizontal(g6)
FEATURE [Part::Extrusion] Extrude019  label="caseScrewPillarBracket007"
  Base = -> Sketch025
  Dir = (0,0,1)
  DirMode = 2
  FaceMakerClass = Part::FaceMakerBullseye
  LengthFwd = 2.4
  LengthRev = 0
  Placement = pos=(101.3,29,65.23) rot=(0,1,0;1.5708rad)
  Solid = true
  Symmetric = false
FEATURE [Part::Box] Box011  label="frontCaseScrewPillarBracket"
  AttacherType = Attacher::AttachEngine3D
  Height = 2.4
  Length = 16
  Placement = pos=(87,28,2.3) rot=(0,0,1;0rad)
  Width = 7
FEATURE [Part::Box] Box012  label="frontCaseScrewPillarBracket001"
  AttacherType = Attacher::AttachEngine3D
  Height = 2.4
  Length = 16
  Placement = pos=(87,28,67.3) rot=(0,0,1;0rad)
  Width = 7
FEATURE [Sketcher::SketchObject] Sketch026
  FullyConstrained = true
  sketch-geometry (17):
    g0: Circle CenterX=-3.5 CenterY=23.5 CenterZ=0 NormalX=0 NormalY=0 NormalZ=1 AngleXU=0 Radius=1
    g1: Circle CenterX=-1 CenterY=15.25 CenterZ=0 NormalX=0 NormalY=0 NormalZ=1 AngleXU=0 Radius=1
    g2: Circle CenterX=-3.5 CenterY=7 CenterZ=0 NormalX=0 NormalY=0 NormalZ=1 AngleXU=0 Radius=1
    g3: BSplineCurve PolesCount=3 KnotsCount=2 Degree=2 IsPeriodic=0
    g4: GeomPoint X=-3.5 Y=23.5 Z=0
    g5: GeomPoint X=-3.5 Y=7 Z=0
    g6: Circle CenterX=-4.8 CenterY=30.5 CenterZ=0 NormalX=0 NormalY=0 NormalZ=1 AngleXU=0 Radius=1
    g7: Circle CenterX=-3.5 CenterY=30.5 CenterZ=0 NormalX=0 NormalY=0 NormalZ=1 AngleXU=0 Radius=1
    g8: Circle CenterX=-3.5 CenterY=29.2 CenterZ=0 NormalX=0 NormalY=0 NormalZ=1 AngleXU=0 Radius=1
    g9: BSplineCurve PolesCount=3 KnotsCount=2 Degree=2 IsPeriodic=0
    g10: GeomPoint X=-4.8 Y=30.5 Z=0
    g11: GeomPoint X=-3.5 Y=29.2 Z=0
    g12: LineSegment StartX=-3.5 StartY=29.2 StartZ=0 EndX=-3.5 EndY=23.5 EndZ=0
    g13: LineSegment StartX=-4.8 StartY=30.5 StartZ=0 EndX=0 EndY=30.5 EndZ=0
    g14: LineSegment StartX=-3.5 StartY=5 StartZ=0 EndX=-3.5 EndY=7 EndZ=0
    g15: LineSegment StartX=0 StartY=5 StartZ=0 EndX=0 EndY=30.5 EndZ=0
    g16: LineSegment StartX=-3.5 StartY=5 StartZ=0 EndX=0 EndY=5 EndZ=0
  constraints (33):
    c: Weight(g0) = 1
    c: Equal(g0,g1)
    c: Equal(g0,g2)
    c: InternalAlignment(g0,g3)
    c: InternalAlignment(g1,g3)
    c: InternalAlignment(g2,g3)
    c: InternalAlignment(g4,g3)
    c: InternalAlignment(g5,g3)
    c: Block(g3)
    c: Weight(g6) = 1
    c: Equal(g6,g7)
    c: Equal(g6,g8)
    c: InternalAlignment(g6,g9)
    c: InternalAlignment(g7,g9)
    c: InternalAlignment(g8,g9)
    c: InternalAlignment(g10,g9)
    c: InternalAlignment(g11,g9)
    c: Block(g9)
    c: Coincident(g12,g9)
    c: Coincident(g12,g3)
    c: Vertical(g12)
    c: Coincident(g13,g9)
    c: Horizontal(g13)
    c: Distance(g13) = 4.8
    c: Coincident(g14,g3)
    c: Vertical(g14)
    c: Coincident(g15,g13)
    c: Vertical(g15)
    c: Tangent(g15,g1)
    c: Distance(g14) = 2
    c: Coincident(g16,g14)
    c: Horizontal(g16)
    c: Coincident(g15,g16)
FEATURE [Part::Feature] Face050
  shape: bbox 4.8 x 25.5 x 2e-07 mm, 1 faces, 0 solids (baked)
FEATURE [Part::Revolution] Revolve054  label="moreFrontCaseScrewPost001"
  Angle = 360
  Axis = (0,1,0)
  Base = (0,0,0)
  FaceMakerClass = Part::FaceMakerBullseye
  Placement = pos=(102.5,4.5,3.5) rot=(0,0,1;0rad)
  Solid = false
  Source = -> Face050
  Symmetric = false
FEATURE [Part::Feature] Face051
  shape: bbox 4.8 x 25.5 x 2e-07 mm, 1 faces, 0 solids (baked)
FEATURE [Part::Revolution] Revolve055  label="moreFrontCaseScrewPost002"
  Angle = 360
  Axis = (0,1,0)
  Base = (0,0,0)
  FaceMakerClass = Part::FaceMakerBullseye
  Placement = pos=(102.5,4.5,68.5) rot=(0,0,1;0rad)
  Solid = false
  Source = -> Face051
  Symmetric = false
FEATURE [Sketcher::SketchObject] Sketch027
  FullyConstrained = true
  sketch-geometry (10):
    g0: LineSegment StartX=-1.6 StartY=4.7 StartZ=0 EndX=-1.6 EndY=1.7 EndZ=0
    g1: LineSegment StartX=-3.5 StartY=4.7 StartZ=0 EndX=-1.6 EndY=4.7 EndZ=0
    g2: LineSegment StartX=-1.6 StartY=1.7 StartZ=0 EndX=-1.6 EndY=1.5 EndZ=0
    g3: LineSegment StartX=-1.6 StartY=1.5 StartZ=0 EndX=-5.2 EndY=1.5 EndZ=0
    g4: Circle CenterX=-3.5 CenterY=4.7 CenterZ=0 NormalX=0 NormalY=0 NormalZ=1 AngleXU=0 Radius=1
    g5: Circle CenterX=-3.59627 CenterY=2.99743 CenterZ=0 NormalX=0 NormalY=0 NormalZ=1 AngleXU=0 Radius=1
    g6: Circle CenterX=-5.2 CenterY=1.5 CenterZ=0 NormalX=0 NormalY=0 NormalZ=1 AngleXU=0 Radius=1
    g7: BSplineCurve PolesCount=3 KnotsCount=2 Degree=2 IsPeriodic=0
    g8: GeomPoint X=-3.5 Y=4.7 Z=0
    g9: GeomPoint X=-5.2 Y=1.5 Z=0
  constraints (23):
    c: Vertical(g0)
    c: Distance(g0) = 3
    c: Coincident(g1,g0)
    c: Horizontal(g1)
    c: Block(g0)
    c: Block(g1)
    c: Coincident(g2,g0)
    c: Vertical(g2)
    c: Distance(g2) = 0.2
    c: Coincident(g3,g2)
    c: Horizontal(g3)
    c: Block(g3)
    c: Coincident(g7,g1)
    c: Weight(g4) = 1
    c: Equal(g4,g5)
    c: Equal(g4,g6)
    c: Coincident(g7,g3)
    c: InternalAlignment(g4,g7)
    c: InternalAlignment(g5,g7)
    c: InternalAlignment(g6,g7)
    c: InternalAlignment(g8,g7)
    c: InternalAlignment(g9,g7)
    c: Block(g7)
FEATURE [Sketcher::SketchObject] Sketch028
  FullyConstrained = true
  sketch-geometry (18):
    g0: LineSegment StartX=0 StartY=3e-16 StartZ=0 EndX=0 EndY=1.7 EndZ=0
    g1: LineSegment StartX=-3.5 StartY=0 StartZ=0 EndX=-3.5 EndY=0.9 EndZ=0
    g2: Circle CenterX=-2.7 CenterY=1.7 CenterZ=0 NormalX=0 NormalY=0 NormalZ=1 AngleXU=0 Radius=1
    g3: Circle CenterX=-3.5 CenterY=1.7 CenterZ=0 NormalX=0 NormalY=0 NormalZ=1 AngleXU=0 Radius=1
    g4: Circle CenterX=-3.5 CenterY=0.9 CenterZ=0 NormalX=0 NormalY=0 NormalZ=1 AngleXU=0 Radius=1
    g5: BSplineCurve PolesCount=3 KnotsCount=2 Degree=2 IsPeriodic=0
    g6: GeomPoint X=-2.7 Y=1.7 Z=0
    g7: GeomPoint X=-3.5 Y=0.9 Z=0
    g8: LineSegment StartX=-3.5 StartY=0 StartZ=0 EndX=-3.5 EndY=-7 EndZ=0
    g9: LineSegment StartX=0 StartY=3e-16 StartZ=0 EndX=0 EndY=-7 EndZ=0
    g10: LineSegment StartX=-3.5 StartY=-7 StartZ=0 EndX=0 EndY=-7 EndZ=0
    g11: LineSegment StartX=-2.7 StartY=1.7 StartZ=0 EndX=-1.6 EndY=1.7 EndZ=0
    g12: LineSegment StartX=0 StartY=1.7 StartZ=0 EndX=0 EndY=4.5 EndZ=0
    g13: LineSegment StartX=0 StartY=4.5 StartZ=0 EndX=0 EndY=10.8 EndZ=0
    g14: LineSegment StartX=0 StartY=10.8 StartZ=0 EndX=-2 EndY=10.8 EndZ=0
    g15: LineSegment StartX=-1.6 StartY=4.7 StartZ=0 EndX=-1.6 EndY=1.7 EndZ=0
    g16: LineSegment StartX=-1.6 StartY=4.7 StartZ=0 EndX=-2 EndY=4.7 EndZ=0
    g17: LineSegment StartX=-2 StartY=4.7 StartZ=0 EndX=-2 EndY=10.8 EndZ=0
  constraints (44):
    c: Vertical(g0)
    c: Vertical(g1)
    c: Distance(g1) = 0.9
    c: Block(g0)
    c: Distance(g0) = 1.7
    c: Weight(g2) = 1
    c: Equal(g2,g3)
    c: Equal(g2,g4)
    c: Coincident(g5,g1)
    c: InternalAlignment(g2,g5)
    c: InternalAlignment(g3,g5)
    c: InternalAlignment(g4,g5)
    c: InternalAlignment(g6,g5)
    c: InternalAlignment(g7,g5)
    c: Block(g5)
    c: Coincident(g8,g1)
    c: Vertical(g8)
    c: Distance(g8) = 7
    c: Vertical(g9)
    c: Equal(g8,g9) = 7
    c: Coincident(g9,g0)
    c: Coincident(g10,g8)
    c: Coincident(g10,g9)
    c: Horizontal(g10)
    c: Coincident(g11,g5)
    c: Horizontal(g11)
    c: Coincident(g12,g0)
    c: Vertical(g12)
    c: Distance(g12) = 2.8
    c: Coincident(g13,g12)
    c: Vertical(g13)
    c: Distance(g13) = 6.3
    c: Coincident(g14,g13)
    c: Horizontal(g14)
    c: Distance(g14) = 2
    c: Vertical(g15)
    c: Distance(g15) = 3
    c: Block(g11)
    c: Coincident(g15,g11)
    c: Coincident(g16,g15)
    c: Horizontal(g16)
    c: Coincident(g17,g16)
    c: Coincident(g17,g14)
    c: Vertical(g17)
FEATURE [Part::Revolution] Revolve040  label="backCaseScrewRetainer001"
  Angle = 360
  Axis = (0,1,0)
  Base = (0,0,0)
  FaceMakerClass = Part::FaceMakerBullseye
  Placement = pos=(12.5,3,10) rot=(0,0,1;0rad)
  Solid = false
  Source = -> Face036
  Symmetric = false
FEATURE [Part::Feature] Face055
  shape: bbox 3.5 x 30.2 x 2e-07 mm, 1 faces, 0 solids (baked)
FEATURE [Part::Revolution] Revolve059  label="backCaseScrewPost"
  Angle = 360
  Axis = (0,1,0)
  Base = (0,0,0)
  FaceMakerClass = Part::FaceMakerBullseye
  Placement = pos=(12.5,4.5,10) rot=(0,0,1;0rad)
  Solid = false
  Source = -> Face055
  Symmetric = false
FEATURE [Part::Feature] Face056
  shape: bbox 3.5 x 30.2 x 2e-07 mm, 1 faces, 0 solids (baked)
FEATURE [Part::Revolution] Revolve060  label="backCaseScrewPost001"
  Angle = 360
  Axis = (0,1,0)
  Base = (0,0,0)
  FaceMakerClass = Part::FaceMakerBullseye
  Placement = pos=(12.5,4.5,62) rot=(0,0,1;0rad)
  Solid = false
  Source = -> Face056
  Symmetric = false
FEATURE [Part::Feature] Face057
  shape: bbox 3.5 x 17.8 x 2e-07 mm, 1 faces, 0 solids (baked)
FEATURE [Part::Revolution] Revolve061  label="removeToCreateScrewAndThreadedInsertHole"
  Angle = 360
  Axis = (0,1,0)
  Base = (0,0,0)
  FaceMakerClass = Part::FaceMakerBullseye
  Placement = pos=(12.5,0,10) rot=(0,0,1;0rad)
  Solid = false
  Source = -> Face057
  Symmetric = false
FEATURE [Part::Feature] Face058
  shape: bbox 3.5 x 17.8 x 2e-07 mm, 1 faces, 0 solids (baked)
FEATURE [Part::Revolution] Revolve062  label="removeToCreateScrewAndThreadedInsertHole001"
  Angle = 360
  Axis = (0,1,0)
  Base = (0,0,0)
  FaceMakerClass = Part::FaceMakerBullseye
  Placement = pos=(12.5,0,62) rot=(0,0,1;0rad)
  Solid = false
  Source = -> Face058
  Symmetric = false
FEATURE [Part::Feature] Face059
  shape: bbox 3.5 x 17.8 x 2e-07 mm, 1 faces, 0 solids (baked)
FEATURE [Part::Revolution] Revolve063  label="removeToCreateScrewAndThreadedInsertHole002"
  Angle = 360
  Axis = (0,1,0)
  Base = (0,0,0)
  FaceMakerClass = Part::FaceMakerBullseye
  Placement = pos=(89.5,0,68.5) rot=(0,0,1;0rad)
  Solid = false
  Source = -> Face059
  Symmetric = false
FEATURE [Part::Feature] Face060
  shape: bbox 3.5 x 17.8 x 2e-07 mm, 1 faces, 0 solids (baked)
FEATURE [Part::Revolution] Revolve064  label="removeToCreateScrewAndThreadedInsertHole003"
  Angle = 360
  Axis = (0,1,0)
  Base = (0,0,0)
  FaceMakerClass = Part::FaceMakerBullseye
  Placement = pos=(89.5,0,3.5) rot=(0,0,1;0rad)
  Solid = false
  Source = -> Face060
  Symmetric = false
FEATURE [Part::Feature] Face061
  shape: bbox 3.5 x 17.8 x 2e-07 mm, 1 faces, 0 solids (baked)
FEATURE [Part::Revolution] Revolve065  label="removeToCreateScrewAndThreadedInsertHole004"
  Angle = 360
  Axis = (0,1,0)
  Base = (0,0,0)
  FaceMakerClass = Part::FaceMakerBullseye
  Placement = pos=(102.5,4.7,3.5) rot=(0,0,1;0rad)
  Solid = false
  Source = -> Face061
  Symmetric = false
FEATURE [Part::Feature] Face062
  shape: bbox 3.5 x 17.8 x 2e-07 mm, 1 faces, 0 solids (baked)
FEATURE [Part::Revolution] Revolve066  label="removeToCreateScrewAndThreadedInsertHole005"
  Angle = 360
  Axis = (0,1,0)
  Base = (0,0,0)
  FaceMakerClass = Part::FaceMakerBullseye
  Placement = pos=(102.5,4.7,68.5) rot=(0,0,1;0rad)
  Solid = false
  Source = -> Face062
  Symmetric = false
FEATURE [Part::MultiFuse] Fusion047  label="makeHoles"
  Shapes = -> [Revolve066,Revolve065,Revolve064,Revolve063,Revolve062,Revolve061]
FEATURE [Part::Feature] Face063
  shape: bbox 3.6 x 3.2 x 2e-07 mm, 1 faces, 0 solids (baked)
FEATURE [Part::Revolution] Revolve067  label="moreFrontCaseScrewRetainer002"
  Angle = 360
  Axis = (0,1,0)
  Base = (0,0,0)
  FaceMakerClass = Part::FaceMakerBullseye
  Placement = pos=(102.5,4.5,68.5) rot=(0,0,1;0rad)
  Solid = false
  Source = -> Face063
  Symmetric = false
FEATURE [Part::Feature] Face064
  shape: bbox 3.6 x 3.2 x 2e-07 mm, 1 faces, 0 solids (baked)
FEATURE [Part::Revolution] Revolve068  label="moreFrontCaseScrewRetainer003"
  Angle = 360
  Axis = (0,1,0)
  Base = (0,0,0)
  FaceMakerClass = Part::FaceMakerBullseye
  Placement = pos=(102.5,4.5,3.5) rot=(0,0,1;0rad)
  Solid = false
  Source = -> Face064
  Symmetric = false
FEATURE [Part::Feature] Face065
  shape: bbox 3.5 x 17.8 x 2e-07 mm, 1 faces, 0 solids (baked)
FEATURE [Part::Revolution] Revolve069  label="removeToCreateScrewAndThreadedInsertHole006"
  Angle = 360
  Axis = (0,1,0)
  Base = (0,0,0)
  FaceMakerClass = Part::FaceMakerBullseye
  Placement = pos=(12.5,0,10) rot=(0,0,1;0rad)
  Solid = false
  Source = -> Face065
  Symmetric = false
FEATURE [Part::Feature] Face066
  shape: bbox 3.5 x 17.8 x 2e-07 mm, 1 faces, 0 solids (baked)
FEATURE [Part::Revolution] Revolve070  label="removeToCreateScrewAndThreadedInsertHole007"
  Angle = 360
  Axis = (0,1,0)
  Base = (0,0,0)
  FaceMakerClass = Part::FaceMakerBullseye
  Placement = pos=(12.5,0,62) rot=(0,0,1;0rad)
  Solid = false
  Source = -> Face066
  Symmetric = false
FEATURE [Part::Feature] Face067
  shape: bbox 3.5 x 17.8 x 2e-07 mm, 1 faces, 0 solids (baked)
FEATURE [Part::Revolution] Revolve071  label="removeToCreateScrewAndThreadedInsertHole008"
  Angle = 360
  Axis = (0,1,0)
  Base = (0,0,0)
  FaceMakerClass = Part::FaceMakerBullseye
  Placement = pos=(89.5,0,68.5) rot=(0,0,1;0rad)
  Solid = false
  Source = -> Face067
  Symmetric = false
FEATURE [Part::Feature] Face068
  shape: bbox 3.5 x 17.8 x 2e-07 mm, 1 faces, 0 solids (baked)
FEATURE [Part::Revolution] Revolve072  label="removeToCreateScrewAndThreadedInsertHole009"
  Angle = 360
  Axis = (0,1,0)
  Base = (0,0,0)
  FaceMakerClass = Part::FaceMakerBullseye
  Placement = pos=(89.5,0,3.5) rot=(0,0,1;0rad)
  Solid = false
  Source = -> Face068
  Symmetric = false
FEATURE [Part::Feature] Face069
  shape: bbox 3.5 x 17.8 x 2e-07 mm, 1 faces, 0 solids (baked)
FEATURE [Part::Feature] Face070
  shape: bbox 3.5 x 17.8 x 2e-07 mm, 1 faces, 0 solids (baked)
FEATURE [Part::Revolution] Revolve073  label="removeToCreateScrewAndThreadedInsertHole010"
  Angle = 360
  Axis = (0,1,0)
  Base = (0,0,0)
  FaceMakerClass = Part::FaceMakerBullseye
  Placement = pos=(102.5,4.7,3.5) rot=(0,0,1;0rad)
  Solid = false
  Source = -> Face069
  Symmetric = false
FEATURE [Part::Revolution] Revolve074  label="removeToCreateScrewAndThreadedInsertHole011"
  Angle = 360
  Axis = (0,1,0)
  Base = (0,0,0)
  FaceMakerClass = Part::FaceMakerBullseye
  Placement = pos=(102.5,4.7,68.5) rot=(0,0,1;0rad)
  Solid = false
  Source = -> Face070
  Symmetric = false
FEATURE [Part::MultiFuse] Fusion048  label="makeHoles001"
  Shapes = -> [Revolve074,Revolve073,Revolve072,Revolve071,Revolve070,Revolve069]
FEATURE [Part::MultiFuse] Fusion049  label="caseScrewRetainers"
  Shapes = -> [Revolve067,Revolve068,Revolve048,Revolve047,Revolve039,Revolve040]
FEATURE [Part::Cut] Cut015  label="caseScrewRetainers001"
  Base = -> Fusion049
  Tool = -> Fusion048
FEATURE [Part::MultiFuse] Fusion050  label="casePillars"
  Shapes = -> [Revolve055,Revolve054,Revolve043,Revolve046,Revolve059,Revolve060]
FEATURE [Part::Feature] Face071 .. Face076  x6 (patterned run collapsed; names and placements below)
  shape: bbox 3.5 x 17.8 x 2e-07 mm, 1 faces, 0 solids (baked)
FEATURE [Part::Revolution] Revolve075  label="removeToCreateScrewAndThreadedInsertHole012"
  Angle = 360
  Axis = (0,1,0)
  Base = (0,0,0)
  FaceMakerClass = Part::FaceMakerBullseye
  Placement = pos=(12.5,0,10) rot=(0,0,1;0rad)
  Solid = false
  Source = -> Face071
  Symmetric = false
FEATURE [Part::Revolution] Revolve076  label="removeToCreateScrewAndThreadedInsertHole013"
  Angle = 360
  Axis = (0,1,0)
  Base = (0,0,0)
  FaceMakerClass = Part::FaceMakerBullseye
  Placement = pos=(12.5,0,62) rot=(0,0,1;0rad)
  Solid = false
  Source = -> Face072
  Symmetric = false
FEATURE [Part::Revolution] Revolve077  label="removeToCreateScrewAndThreadedInsertHole014"
  Angle = 360
  Axis = (0,1,0)
  Base = (0,0,0)
  FaceMakerClass = Part::FaceMakerBullseye
  Placement = pos=(89.5,0,68.5) rot=(0,0,1;0rad)
  Solid = false
  Source = -> Face073
  Symmetric = false
FEATURE [Part::Revolution] Revolve078  label="removeToCreateScrewAndThreadedInsertHole015"
  Angle = 360
  Axis = (0,1,0)
  Base = (0,0,0)
  FaceMakerClass = Part::FaceMakerBullseye
  Placement = pos=(89.5,0,3.5) rot=(0,0,1;0rad)
  Solid = false
  Source = -> Face074
  Symmetric = false
FEATURE [Part::Revolution] Revolve079  label="removeToCreateScrewAndThreadedInsertHole016"
  Angle = 360
  Axis = (0,1,0)
  Base = (0,0,0)
  FaceMakerClass = Part::FaceMakerBullseye
  Placement = pos=(102.5,4.7,3.5) rot=(0,0,1;0rad)
  Solid = false
  Source = -> Face075
  Symmetric = false
FEATURE [Part::Revolution] Revolve080  label="removeToCreateScrewAndThreadedInsertHole017"
  Angle = 360
  Axis = (0,1,0)
  Base = (0,0,0)
  FaceMakerClass = Part::FaceMakerBullseye
  Placement = pos=(102.5,4.7,68.5) rot=(0,0,1;0rad)
  Solid = false
  Source = -> Face076
  Symmetric = false
FEATURE [Part::MultiFuse] Fusion051  label="makeHoles002"
  Shapes = -> [Revolve080,Revolve079,Revolve078,Revolve077,Revolve076,Revolve075]
FEATURE [Part::Cut] Cut016  label="caesPillars"
  Base = -> Fusion050
  Tool = -> Fusion051
FEATURE [Part::Revolution] Revolve009  label="plugHousing016"
  Angle = 360
  Axis = (0,1,0)
  Base = (0,0,0)
  FaceMakerClass = Part::FaceMakerBullseye
  Placement = pos=(0,0,36.15) rot=(0,0,1;0rad)
  Solid = false
  Source = -> Face012
  Symmetric = false
FEATURE [Part::MultiFuse] Fusion014  label="plugHousing023"
  Placement = pos=(0,0,0) rot=(0,0,1;1.5708rad)
  Shapes = -> [Revolve011,Revolve009]
FEATURE [Part::Revolution] Revolve010  label="plugHousing017"
  Angle = 360
  Axis = (0,1,0)
  Base = (0,0,0)
  FaceMakerClass = Part::FaceMakerBullseye
  Placement = pos=(0,0,36.15) rot=(0,0,1;0rad)
  Solid = false
  Source = -> Face014
  Symmetric = false
FEATURE [Part::MultiFuse] Fusion015  label="plugHousing024"
  Placement = pos=(0,0,0) rot=(0,0,1;1.5708rad)
  Shapes = -> [Revolve010,Revolve015]
FEATURE [Part::Revolution] Revolve014  label="plugHousing026"
  Angle = 360
  Axis = (0,1,0)
  Base = (0,0,0)
  FaceMakerClass = Part::FaceMakerBullseye
  Placement = pos=(0,0,36.15) rot=(0,0,1;0rad)
  Solid = false
  Source = -> Face011
  Symmetric = false
FEATURE [Part::Revolution] Revolve013  label="plugHousing025"
  Angle = 360
  Axis = (0,1,0)
  Base = (0,0,0)
  FaceMakerClass = Part::FaceMakerBullseye
  Placement = pos=(0,0,36.15) rot=(0,0,1;0rad)
  Solid = false
  Source = -> Face015
  Symmetric = false
FEATURE [Part::MultiFuse] Fusion016  label="plugHousing028"
  Placement = pos=(0,19,0) rot=(0,0,1;3.14159rad)
  Shapes = -> [Fusion014,Fusion013]
FEATURE [Part::MultiFuse] Fusion011  label="plugHousing018"
  Placement = pos=(0,0,0) rot=(0,0,1;1.5708rad)
  Shapes = -> [Revolve014,Revolve013]
FEATURE [Part::MultiFuse] Fusion012  label="plugHousing019"
  Placement = pos=(0,19,0) rot=(0,0,1;3.14159rad)
  Shapes = -> [Fusion011,Fusion015]
FEATURE [Part::MultiFuse] Fusion017  label="plugHousing029"
  Placement = pos=(122.621,0,-0.15) rot=(0,0,1;0rad)
  Shapes = -> [Fusion016,Fusion012]
FEATURE [Part::MultiFuse] Fusion052  label="casePillarRetainers"
  Shapes = -> [Extrude012,Extrude013,Extrude014,Extrude015,Extrude016,Extrude017,Extrude018,Extrude019,Box011,Box012]
FEATURE [Part::Feature] Face077
  shape: bbox 3.5 x 17.8 x 2e-07 mm, 1 faces, 0 solids (baked)
FEATURE [Part::Revolution] Revolve081  label="removeToCreateScrewAndThreadedInsertHole018"
  Angle = 360
  Axis = (0,1,0)
  Base = (0,0,0)
  FaceMakerClass = Part::FaceMakerBullseye
  Placement = pos=(62.3,30.3,19.7) rot=(0,0,1;0rad)
  Solid = false
  Source = -> Face077
  Symmetric = false
FEATURE [Part::Feature] Face078
  shape: bbox 3.5 x 17.8 x 2e-07 mm, 1 faces, 0 solids (baked)
FEATURE [Part::Revolution] Revolve082  label="removeToCreateScrewAndThreadedInsertHole019"
  Angle = 360
  Axis = (0,1,0)
  Base = (0,0,0)
  FaceMakerClass = Part::FaceMakerBullseye
  Placement = pos=(62.3,30.3,51.7) rot=(0,0,1;0rad)
  Solid = false
  Source = -> Face078
  Symmetric = false
FEATURE [Part::Feature] Face079
  shape: bbox 3.5 x 17.8 x 2e-07 mm, 1 faces, 0 solids (baked)
FEATURE [Part::Revolution] Revolve083  label="removeToCreateScrewAndThreadedInsertHole020"
  Angle = 360
  Axis = (0,1,0)
  Base = (0,0,0)
  FaceMakerClass = Part::FaceMakerBullseye
  Placement = pos=(30.3,30.3,19.7) rot=(0,0,1;0rad)
  Solid = false
  Source = -> Face079
  Symmetric = false
FEATURE [Part::Feature] Face080
  shape: bbox 3.5 x 17.8 x 2e-07 mm, 1 faces, 0 solids (baked)
FEATURE [Part::Revolution] Revolve084  label="removeToCreateScrewAndThreadedInsertHole021"
  Angle = 360
  Axis = (0,1,0)
  Base = (0,0,0)
  FaceMakerClass = Part::FaceMakerBullseye
  Placement = pos=(30.3,30.3,51.7) rot=(0,0,1;0rad)
  Solid = false
  Source = -> Face080
  Symmetric = false
FEATURE [Part::MultiFuse] Fusion053  label="createThreadedInsertHolesForFan"
  Shapes = -> [Revolve081,Revolve082,Revolve083,Revolve084]
FEATURE [Part::Cut] Cut017  label="fanScrewHousing001"
  Base = -> Fusion046
  Tool = -> Fusion053
FEATURE [Part::Feature] Face081
  shape: bbox 3.5 x 17.8 x 2e-07 mm, 1 faces, 0 solids (baked)
FEATURE [Part::Revolution] Revolve085  label="removeToCreateScrewAndThreadedInsertHole022"
  Angle = 360
  Axis = (0,1,0)
  Base = (0,0,0)
  FaceMakerClass = Part::FaceMakerBullseye
  Placement = pos=(62.3,30.3,19.7) rot=(0,0,1;0rad)
  Solid = false
  Source = -> Face081
  Symmetric = false
FEATURE [Part::Feature] Face082
  shape: bbox 3.5 x 17.8 x 2e-07 mm, 1 faces, 0 solids (baked)
FEATURE [Part::Revolution] Revolve086  label="removeToCreateScrewAndThreadedInsertHole023"
  Angle = 360
  Axis = (0,1,0)
  Base = (0,0,0)
  FaceMakerClass = Part::FaceMakerBullseye
  Placement = pos=(62.3,30.3,51.7) rot=(0,0,1;0rad)
  Solid = false
  Source = -> Face082
  Symmetric = false
FEATURE [Part::Feature] Face083
  shape: bbox 3.5 x 17.8 x 2e-07 mm, 1 faces, 0 solids (baked)
FEATURE [Part::Revolution] Revolve087  label="removeToCreateScrewAndThreadedInsertHole024"
  Angle = 360
  Axis = (0,1,0)
  Base = (0,0,0)
  FaceMakerClass = Part::FaceMakerBullseye
  Placement = pos=(30.3,30.3,19.7) rot=(0,0,1;0rad)
  Solid = false
  Source = -> Face083
  Symmetric = false
FEATURE [Part::Feature] Face084
  shape: bbox 3.5 x 17.8 x 2e-07 mm, 1 faces, 0 solids (baked)
FEATURE [Part::Revolution] Revolve088  label="removeToCreateScrewAndThreadedInsertHole025"
  Angle = 360
  Axis = (0,1,0)
  Base = (0,0,0)
  FaceMakerClass = Part::FaceMakerBullseye
  Placement = pos=(30.3,30.3,51.7) rot=(0,0,1;0rad)
  Solid = false
  Source = -> Face084
  Symmetric = false
FEATURE [Part::MultiFuse] Fusion054  label="createThreadedInsertHolesForFan001"
  Shapes = -> [Revolve085,Revolve086,Revolve087,Revolve088]
FEATURE [Part::Cut] Cut018  label="top007"
  Base = -> Fusion040
  Tool = -> Fusion054
FEATURE [Sketcher::SketchObject] Sketch029
  FullyConstrained = false
  Placement = pos=(0,0,0) rot=(1,0,0;1.5708rad)
  sketch-geometry (24):
    g0: ArcOfCircle CenterX=-4 CenterY=-10.5 CenterZ=0 NormalX=0 NormalY=0 NormalZ=1 AngleXU=0 Radius=1.5 StartAngle=6e-16 EndAngle=3.14159
    g1: ArcOfCircle CenterX=-34.2 CenterY=-10.5 CenterZ=0 NormalX=0 NormalY=0 NormalZ=1 AngleXU=0 Radius=1.5 StartAngle=0 EndAngle=3.14159
    g2: ArcOfCircle CenterX=-34.2 CenterY=-27.7 CenterZ=0 NormalX=0 NormalY=0 NormalZ=1 AngleXU=0 Radius=1.5 StartAngle=3.14159 EndAngle=6.28319
    g3: ArcOfCircle CenterX=-4 CenterY=-27.7 CenterZ=0 NormalX=0 NormalY=0 NormalZ=1 AngleXU=0 Radius=1.5 StartAngle=3.1416 EndAngle=6.28319
    g4: ArcOfCircle CenterX=-10 CenterY=-4.3 CenterZ=0 NormalX=0 NormalY=0 NormalZ=1 AngleXU=0 Radius=1.5 StartAngle=2e-16 EndAngle=3.14159
    g5: ArcOfCircle CenterX=-16.1 CenterY=-1.8 CenterZ=0 NormalX=0 NormalY=0 NormalZ=1 AngleXU=0 Radius=1.5 StartAngle=5e-16 EndAngle=3.14159
    g6: ArcOfCircle CenterX=-22.1 CenterY=-1.8 CenterZ=0 NormalX=0 NormalY=0 NormalZ=1 AngleXU=0 Radius=1.5 StartAngle=5e-16 EndAngle=3.14159
    g7: ArcOfCircle CenterX=-28.2 CenterY=-4.3 CenterZ=0 NormalX=0 NormalY=0 NormalZ=1 AngleXU=0 Radius=1.5 StartAngle=2e-16 EndAngle=3.14159
    g8: ArcOfCircle CenterX=-10 CenterY=-33.9 CenterZ=0 NormalX=0 NormalY=0 NormalZ=1 AngleXU=0 Radius=1.5 StartAngle=3.14159 EndAngle=6.28319
    g9: ArcOfCircle CenterX=-16.1 CenterY=-36.4 CenterZ=0 NormalX=0 NormalY=0 NormalZ=1 AngleXU=0 Radius=1.5 StartAngle=3.14159 EndAngle=6.28319
    g10: ArcOfCircle CenterX=-22.1 CenterY=-36.4 CenterZ=0 NormalX=0 NormalY=0 NormalZ=1 AngleXU=0 Radius=1.5 StartAngle=3.14159 EndAngle=6.28319
    g11: ArcOfCircle CenterX=-28.2 CenterY=-33.9 CenterZ=0 NormalX=0 NormalY=0 NormalZ=1 AngleXU=0 Radius=1.5 StartAngle=3.14159 EndAngle=6.28319
    g12: LineSegment StartX=-35.7 StartY=-10.5 StartZ=0 EndX=-35.7 EndY=-27.7 EndZ=0
    g13: LineSegment StartX=-32.7 StartY=-10.5 StartZ=0 EndX=-32.7 EndY=-27.7 EndZ=0
    g14: LineSegment StartX=-29.7 StartY=-33.9 StartZ=0 EndX=-29.7 EndY=-4.3 EndZ=0
    g15: LineSegment StartX=-26.7 StartY=-33.9 StartZ=0 EndX=-26.7 EndY=-4.3 EndZ=0
    g16: LineSegment StartX=-2.5 StartY=-10.5 StartZ=0 EndX=-2.5 EndY=-27.7 EndZ=0
    g17: LineSegment StartX=-8.5 StartY=-4.3 StartZ=0 EndX=-8.5 EndY=-33.9 EndZ=0
    g18: LineSegment StartX=-5.5 StartY=-10.5 StartZ=0 EndX=-5.5 EndY=-27.7 EndZ=0
    g19: LineSegment StartX=-11.5 StartY=-4.3 StartZ=0 EndX=-11.5 EndY=-33.9 EndZ=0
    g20: LineSegment StartX=-14.6 StartY=-1.8 StartZ=0 EndX=-14.6 EndY=-36.4 EndZ=0
    g21: LineSegment StartX=-17.6 StartY=-1.8 StartZ=0 EndX=-17.6 EndY=-36.4 EndZ=0
    g22: LineSegment StartX=-20.6 StartY=-36.4 StartZ=0 EndX=-20.6 EndY=-1.8 EndZ=0
    g23: LineSegment StartX=-23.6 StartY=-1.8 StartZ=0 EndX=-23.6 EndY=-36.4 EndZ=0
  constraints (48):
    c: Block(g0)
    c: Block(g1)
    c: Block(g2)
    c: Block(g3)
    c: Block(g4)
    c: Block(g5)
    c: Block(g6)
    c: Block(g7)
    c: Block(g8)
    c: Block(g9)
    c: Block(g10)
    c: Block(g11)
    c: Coincident(g12,g1)
    c: Coincident(g12,g2)
    c: Vertical(g12)
    c: Coincident(g13,g1)
    c: Coincident(g13,g2)
    c: Vertical(g13)
    c: Coincident(g14,g11)
    c: Coincident(g14,g7)
    c: Vertical(g14)
    c: Coincident(g15,g11)
    c: Coincident(g15,g7)
    c: Vertical(g15)
    c: Coincident(g16,g0)
    c: Coincident(g16,g3)
    c: Vertical(g16)
    c: Coincident(g17,g4)
    c: Coincident(g17,g8)
    c: Vertical(g17)
    c: Coincident(g18,g0)
    c: Coincident(g18,g3)
    c: Vertical(g18)
    c: Coincident(g19,g4)
    c: Coincident(g19,g8)
    c: Vertical(g19)
    c: Coincident(g20,g5)
    c: Coincident(g20,g9)
    c: Vertical(g20)
    c: Coincident(g21,g5)
    c: Coincident(g21,g9)
    c: Vertical(g21)
    c: Coincident(g22,g10)
    c: Coincident(g22,g6)
    c: Vertical(g22)
    c: Coincident(g23,g6)
    c: Coincident(g23,g10)
    c: Vertical(g23)
FEATURE [Part::Extrusion] Extrude020  label="removeToCreateFanGrillHoles"
  Base = -> Sketch029
  Dir = (0,-1,6e-16)
  DirMode = 2
  FaceMakerClass = Part::FaceMakerBullseye
  LengthFwd = 10
  LengthRev = 0
  Placement = pos=(65.4,44,54.82) rot=(0,0,1;0rad)
  Solid = true
  Symmetric = false
FEATURE [Part::MultiFuse] Fusion055  label="top008"
  Shapes = -> [Cut017,Cut018]
FEATURE [Part::Cut] Cut019  label="top009"
  Base = -> Fusion055
  Tool = -> Extrude020
FEATURE [App::MeasureDistance] Distance003  label="Distance: 71.95 mm"
  Distance = 71.9513
  P1 = (117,38,72)
  P2 = (117,38,0.0487319)
FEATURE [Sketcher::SketchObject] Sketch030
  FullyConstrained = true
  Placement = pos=(117,19,0) rot=(0.57735,0.57735,0.57735;2.0944rad)
  sketch-geometry (48):
    g0: LineSegment StartX=-49.19 StartY=69.25 StartZ=0 EndX=-49.19 EndY=66.25 EndZ=0
    g1: LineSegment StartX=-49.19 StartY=63.5 StartZ=0 EndX=-49.19 EndY=60.5 EndZ=0
    g2: LineSegment StartX=-49.19 StartY=57.75 StartZ=0 EndX=-49.19 EndY=54.75 EndZ=0
    g3: LineSegment StartX=-49.19 StartY=52 StartZ=0 EndX=-49.19 EndY=49 EndZ=0
    g4: LineSegment StartX=-49.19 StartY=46.25 StartZ=0 EndX=-49.19 EndY=43.25 EndZ=0
    g5: LineSegment StartX=-49.19 StartY=40.5 StartZ=0 EndX=-49.19 EndY=37.5 EndZ=0
    g6: LineSegment StartX=-49.19 StartY=34.5 StartZ=0 EndX=-49.19 EndY=31.5 EndZ=0
    g7: LineSegment StartX=-49.19 StartY=28.75 StartZ=0 EndX=-49.19 EndY=25.75 EndZ=0
    g8: LineSegment StartX=-49.19 StartY=23 StartZ=0 EndX=-49.19 EndY=20 EndZ=0
    g9: LineSegment StartX=-49.19 StartY=17.25 StartZ=0 EndX=-49.19 EndY=14.25 EndZ=0
    g10: LineSegment StartX=-49.19 StartY=11.5 StartZ=0 EndX=-49.19 EndY=8.5 EndZ=0
    g11: LineSegment StartX=-49.19 StartY=5.75 StartZ=0 EndX=-49.19 EndY=2.75 EndZ=0
    g12: ArcOfCircle CenterX=-1.5 CenterY=67.75 CenterZ=0 NormalX=0 NormalY=0 NormalZ=1 AngleXU=0 Radius=1.5 StartAngle=4.71239 EndAngle=7.85398
    g13: ArcOfCircle CenterX=-1.5 CenterY=62 CenterZ=0 NormalX=0 NormalY=0 NormalZ=1 AngleXU=0 Radius=1.5 StartAngle=4.71239 EndAngle=7.85398
    g14: ArcOfCircle CenterX=-1.5 CenterY=56.25 CenterZ=0 NormalX=0 NormalY=0 NormalZ=1 AngleXU=0 Radius=1.5 StartAngle=4.71239 EndAngle=7.85398
    g15: ArcOfCircle CenterX=-11.49 CenterY=50.5 CenterZ=0 NormalX=0 NormalY=0 NormalZ=1 AngleXU=0 Radius=1.5 StartAngle=4.71239 EndAngle=7.85398
    g16: ArcOfCircle CenterX=-16.28 CenterY=44.75 CenterZ=0 NormalX=0 NormalY=0 NormalZ=1 AngleXU=0 Radius=1.5 StartAngle=4.71239 EndAngle=7.85398
    g17: ArcOfCircle CenterX=-18.2337 CenterY=39 CenterZ=0 NormalX=0 NormalY=0 NormalZ=1 AngleXU=0 Radius=1.5 StartAngle=4.71485 EndAngle=7.85398
    g18: ArcOfCircle CenterX=-16.2837 CenterY=27.25 CenterZ=0 NormalX=0 NormalY=0 NormalZ=1 AngleXU=0 Radius=1.5 StartAngle=4.71485 EndAngle=7.85398
    g19: ArcOfCircle CenterX=-18.2337 CenterY=33 CenterZ=0 NormalX=0 NormalY=0 NormalZ=1 AngleXU=0 Radius=1.5 StartAngle=4.71485 EndAngle=7.85398
    g20: ArcOfCircle CenterX=-11.49 CenterY=21.5 CenterZ=0 NormalX=0 NormalY=0 NormalZ=1 AngleXU=0 Radius=1.5 StartAngle=4.71239 EndAngle=7.85398
    g21: ArcOfCircle CenterX=-1.5 CenterY=4.25 CenterZ=0 NormalX=0 NormalY=0 NormalZ=1 AngleXU=0 Radius=1.5 StartAngle=4.71239 EndAngle=7.85398
    g22: ArcOfCircle CenterX=-1.5 CenterY=10 CenterZ=0 NormalX=0 NormalY=0 NormalZ=1 AngleXU=0 Radius=1.5 StartAngle=4.71239 EndAngle=7.85398
    g23: ArcOfCircle CenterX=-1.5 CenterY=15.75 CenterZ=0 NormalX=0 NormalY=0 NormalZ=1 AngleXU=0 Radius=1.5 StartAngle=4.71239 EndAngle=7.85398
    g24: LineSegment StartX=-49.19 StartY=69.25 StartZ=0 EndX=-1.5 EndY=69.25 EndZ=0
    g25: LineSegment StartX=-49.19 StartY=66.25 StartZ=0 EndX=-1.5 EndY=66.25 EndZ=0
    g26: LineSegment StartX=-49.19 StartY=63.5 StartZ=0 EndX=-1.5 EndY=63.5 EndZ=0
    g27: LineSegment StartX=-49.19 StartY=60.5 StartZ=0 EndX=-1.5 EndY=60.5 EndZ=0
    g28: LineSegment StartX=-49.19 StartY=57.75 StartZ=0 EndX=-1.5 EndY=57.75 EndZ=0
    g29: LineSegment StartX=-49.19 StartY=54.75 StartZ=0 EndX=-1.5 EndY=54.75 EndZ=0
    g30: LineSegment StartX=-49.19 StartY=52 StartZ=0 EndX=-11.49 EndY=52 EndZ=0
    g31: LineSegment StartX=-49.19 StartY=49 StartZ=0 EndX=-11.49 EndY=49 EndZ=0
    g32: LineSegment StartX=-49.19 StartY=46.25 StartZ=0 EndX=-16.28 EndY=46.25 EndZ=0
    g33: LineSegment StartX=-49.19 StartY=43.25 StartZ=0 EndX=-16.28 EndY=43.25 EndZ=0
    g34: LineSegment StartX=-49.19 StartY=40.5 StartZ=0 EndX=-18.2337 EndY=40.5 EndZ=0
    g35: LineSegment StartX=-49.19 StartY=37.5 StartZ=0 EndX=-18.23 EndY=37.5 EndZ=0
    g36: LineSegment StartX=-49.19 StartY=34.5 StartZ=0 EndX=-18.2337 EndY=34.5 EndZ=0
    g37: LineSegment StartX=-49.19 StartY=31.5 StartZ=0 EndX=-18.23 EndY=31.5 EndZ=0
    g38: LineSegment StartX=-49.19 StartY=28.75 StartZ=0 EndX=-16.2837 EndY=28.75 EndZ=0
    g39: LineSegment StartX=-49.19 StartY=25.75 StartZ=0 EndX=-16.28 EndY=25.75 EndZ=0
    g40: LineSegment StartX=-49.19 StartY=23 StartZ=0 EndX=-11.49 EndY=23 EndZ=0
    g41: LineSegment StartX=-49.19 StartY=20 StartZ=0 EndX=-11.49 EndY=20 EndZ=0
    g42: LineSegment StartX=-49.19 StartY=17.25 StartZ=0 EndX=-1.5 EndY=17.25 EndZ=0
    g43: LineSegment StartX=-49.19 StartY=14.25 StartZ=0 EndX=-1.5 EndY=14.25 EndZ=0
    g44: LineSegment StartX=-49.19 StartY=11.5 StartZ=0 EndX=-1.5 EndY=11.5 EndZ=0
    g45: LineSegment StartX=-49.19 StartY=8.5 StartZ=0 EndX=-1.5 EndY=8.5 EndZ=0
    g46: LineSegment StartX=-49.19 StartY=5.75 StartZ=0 EndX=-1.5 EndY=5.75 EndZ=0
    g47: LineSegment StartX=-49.19 StartY=2.75 StartZ=0 EndX=-1.5 EndY=2.75 EndZ=0
  constraints (120):
    c: Vertical(g0)
    c: Distance(g0) = 3
    c: Block(g0)
    c: Vertical(g1)
    c: Distance(g1) = 3
    c: Vertical(g2)
    c: Equal(g0,g2) = 3
    c: Block(g2)
    c: Vertical(g3)
    c: Equal(g1,g3) = 3
    c: Vertical(g4)
    c: Equal(g0,g4) = 3
    c: Block(g4)
    c: Vertical(g5)
    c: Equal(g1,g5) = 3
    c: Vertical(g6)
    c: Equal(g0,g6) = 3
    c: Block(g6)
    c: Vertical(g7)
    c: Equal(g1,g7) = 3
    c: Vertical(g8)
    c: Equal(g0,g8) = 3
    c: Block(g8)
    c: Vertical(g9)
    c: Equal(g1,g9) = 3
    c: Vertical(g10)
    c: Equal(g0,g10) = 3
    c: Block(g10)
    c: Vertical(g11)
    c: Equal(g1,g11) = 3
    c: Block(g12)
    c: Block(g13)
    c: Block(g14)
    c: Block(g15)
    c: Block(g16)
    c: Block(g17)
    c: Block(g18)
    c: Block(g19)
    c: Block(g20)
    c: Block(g21)
    c: Block(g22)
    c: Block(g23)
    c: Block(g11)
    c: Block(g9)
    c: Block(g7)
    c: Block(g5)
    c: Block(g3)
    c: Block(g1)
    c: Coincident(g24,g0)
    c: Coincident(g24,g12)
    c: Horizontal(g24)
    c: Coincident(g25,g0)
    c: Coincident(g25,g12)
    c: Horizontal(g25)
    c: Coincident(g26,g1)
    c: Coincident(g26,g13)
    c: Horizontal(g26)
    c: Coincident(g27,g1)
    c: Coincident(g27,g13)
    c: Horizontal(g27)
    c: Coincident(g28,g2)
    c: Coincident(g28,g14)
    c: Horizontal(g28)
    c: Coincident(g29,g2)
    c: Coincident(g29,g14)
    c: Horizontal(g29)
    c: Coincident(g30,g3)
    c: Coincident(g30,g15)
    c: Horizontal(g30)
    c: Coincident(g31,g3)
    c: Coincident(g31,g15)
    c: Horizontal(g31)
    c: Coincident(g32,g4)
    c: Coincident(g32,g16)
    c: Horizontal(g32)
    c: Coincident(g33,g4)
    c: Coincident(g33,g16)
    c: Horizontal(g33)
    c: Coincident(g34,g5)
    c: Coincident(g34,g17)
    c: Horizontal(g34)
    c: Coincident(g35,g5)
    c: Coincident(g35,g17)
    c: Horizontal(g35)
    c: Coincident(g36,g6)
    c: Coincident(g36,g19)
    c: Horizontal(g36)
    c: Coincident(g37,g6)
    c: Coincident(g37,g19)
    c: Horizontal(g37)
    c: Coincident(g38,g7)
    c: Coincident(g38,g18)
    c: Horizontal(g38)
    c: Coincident(g39,g7)
    c: Coincident(g39,g18)
    c: Horizontal(g39)
    c: Coincident(g40,g8)
    c: Coincident(g40,g20)
    c: Horizontal(g40)
    c: Coincident(g41,g8)
    c: Coincident(g41,g20)
    c: Horizontal(g41)
    c: Coincident(g42,g9)
    c: Coincident(g42,g23)
    c: Horizontal(g42)
    c: Coincident(g43,g9)
    c: Coincident(g43,g23)
    c: Horizontal(g43)
    c: Coincident(g44,g10)
    c: Coincident(g44,g22)
    c: Horizontal(g44)
    c: Coincident(g45,g10)
    c: Coincident(g45,g22)
    c: Horizontal(g45)
    c: Coincident(g46,g11)
    c: Coincident(g46,g21)
    c: Horizontal(g46)
    c: Coincident(g47,g11)
    c: Coincident(g47,g21)
    c: Horizontal(g47)
FEATURE [Sketcher::SketchObject] Sketch031
  FullyConstrained = true
  Placement = pos=(117,19,0) rot=(0.57735,0.57735,0.57735;2.0944rad)
  sketch-geometry (24):
    g0: ArcOfCircle CenterX=-49.19 CenterY=67.75 CenterZ=0 NormalX=0 NormalY=0 NormalZ=1 AngleXU=0 Radius=1.5 StartAngle=1.5708 EndAngle=4.71239
    g1: ArcOfCircle CenterX=-49.19 CenterY=62 CenterZ=0 NormalX=0 NormalY=0 NormalZ=1 AngleXU=0 Radius=1.5 StartAngle=1.5708 EndAngle=4.71239
    g2: ArcOfCircle CenterX=-49.19 CenterY=56.25 CenterZ=0 NormalX=0 NormalY=0 NormalZ=1 AngleXU=0 Radius=1.5 StartAngle=1.5708 EndAngle=4.71239
    g3: ArcOfCircle CenterX=-49.19 CenterY=50.5 CenterZ=0 NormalX=0 NormalY=0 NormalZ=1 AngleXU=0 Radius=1.5 StartAngle=1.5708 EndAngle=4.71239
    g4: ArcOfCircle CenterX=-49.19 CenterY=44.75 CenterZ=0 NormalX=0 NormalY=0 NormalZ=1 AngleXU=0 Radius=1.5 StartAngle=1.5708 EndAngle=4.71239
    g5: ArcOfCircle CenterX=-49.19 CenterY=39 CenterZ=0 NormalX=0 NormalY=0 NormalZ=1 AngleXU=0 Radius=1.5 StartAngle=1.5708 EndAngle=4.71239
    g6: ArcOfCircle CenterX=-49.19 CenterY=33 CenterZ=0 NormalX=0 NormalY=0 NormalZ=1 AngleXU=0 Radius=1.5 StartAngle=1.5708 EndAngle=4.71239
    g7: ArcOfCircle CenterX=-49.19 CenterY=27.25 CenterZ=0 NormalX=0 NormalY=0 NormalZ=1 AngleXU=0 Radius=1.5 StartAngle=1.5708 EndAngle=4.71239
    g8: ArcOfCircle CenterX=-49.19 CenterY=21.5 CenterZ=0 NormalX=0 NormalY=0 NormalZ=1 AngleXU=0 Radius=1.5 StartAngle=1.5708 EndAngle=4.71239
    g9: ArcOfCircle CenterX=-49.19 CenterY=15.75 CenterZ=0 NormalX=0 NormalY=0 NormalZ=1 AngleXU=0 Radius=1.5 StartAngle=1.5708 EndAngle=4.71239
    g10: ArcOfCircle CenterX=-49.19 CenterY=10 CenterZ=0 NormalX=0 NormalY=0 NormalZ=1 AngleXU=0 Radius=1.5 StartAngle=1.5708 EndAngle=4.71239
    g11: ArcOfCircle CenterX=-49.19 CenterY=4.25 CenterZ=0 NormalX=0 NormalY=0 NormalZ=1 AngleXU=0 Radius=1.5 StartAngle=1.5708 EndAngle=4.71239
    g12: LineSegment StartX=-49.19 StartY=69.25 StartZ=0 EndX=-49.19 EndY=66.25 EndZ=0
    g13: LineSegment StartX=-49.19 StartY=63.5 StartZ=0 EndX=-49.19 EndY=60.5 EndZ=0
    g14: LineSegment StartX=-49.19 StartY=57.75 StartZ=0 EndX=-49.19 EndY=54.75 EndZ=0
    g15: LineSegment StartX=-49.19 StartY=52 StartZ=0 EndX=-49.19 EndY=49 EndZ=0
    g16: LineSegment StartX=-49.19 StartY=46.25 StartZ=0 EndX=-49.19 EndY=43.25 EndZ=0
    g17: LineSegment StartX=-49.19 StartY=40.5 StartZ=0 EndX=-49.19 EndY=37.5 EndZ=0
    g18: LineSegment StartX=-49.19 StartY=34.5 StartZ=0 EndX=-49.19 EndY=31.5 EndZ=0
    g19: LineSegment StartX=-49.19 StartY=28.75 StartZ=0 EndX=-49.19 EndY=25.75 EndZ=0
    g20: LineSegment StartX=-49.19 StartY=23 StartZ=0 EndX=-49.19 EndY=20 EndZ=0
    g21: LineSegment StartX=-49.19 StartY=17.25 StartZ=0 EndX=-49.19 EndY=14.25 EndZ=0
    g22: LineSegment StartX=-49.19 StartY=11.5 StartZ=0 EndX=-49.19 EndY=8.5 EndZ=0
    g23: LineSegment StartX=-49.19 StartY=5.75 StartZ=0 EndX=-49.19 EndY=2.75 EndZ=0
  constraints (48):
    c: Block(g0)
    c: Block(g1)
    c: Block(g2)
    c: Block(g3)
    c: Block(g4)
    c: Block(g5)
    c: Block(g6)
    c: Block(g7)
    c: Block(g8)
    c: Block(g9)
    c: Block(g10)
    c: Block(g11)
    c: Coincident(g12,g0)
    c: Coincident(g12,g0)
    c: Vertical(g12)
    c: Vertical(g13)
    c: Coincident(g13,g1)
    c: Vertical(g14)
    c: Coincident(g14,g2)
    c: Vertical(g15)
    c: Coincident(g15,g3)
    c: Vertical(g16)
    c: Coincident(g16,g4)
    c: Vertical(g17)
    c: Coincident(g17,g5)
    c: Vertical(g18)
    c: Coincident(g18,g6)
    c: Vertical(g19)
    c: Coincident(g19,g7)
    c: Vertical(g20)
    c: Coincident(g20,g8)
    c: Vertical(g21)
    c: Coincident(g21,g9)
    c: Vertical(g22)
    c: Coincident(g22,g10)
    c: Vertical(g23)
    c: Coincident(g23,g11)
    c: Block(g23)
    c: Block(g22)
    c: Block(g21)
    c: Block(g20)
    c: Block(g13)
    c: Block(g14)
    c: Block(g15)
    c: Block(g16)
    c: Block(g17)
    c: Block(g18)
    c: Block(g19)
FEATURE [Part::Extrusion] Extrude022
  Base = -> Sketch030
  Dir = (1,-2e-16,2e-16)
  DirMode = 2
  FaceMakerClass = Part::FaceMakerBullseye
  LengthFwd = 19
  LengthRev = 0
  Placement = pos=(-19,0,0) rot=(0,0,1;0rad)
  Solid = true
  Symmetric = false
FEATURE [Part::Fillet] Fillet022
  Base = -> Extrude022
  Edges = 24 edges r=1.49: [Edge6,Edge11,Edge18,Edge23,Edge30,Edge35,Edge42,Edge47,Edge54,Edge59,Edge66,Edge71,Edge78,Edge83,Edge90,Edge95,Edge102,Edge107,Edge114,Edge119,Edge126,Edge131,Edge138,Edge143]
FEATURE [Part::Cut] Cut020  label="top010"
  Base = -> Cut019
  Tool = -> Fillet022
FEATURE [Sketcher::SketchObject] Sketch032
  FullyConstrained = true
  Placement = pos=(117,19,0) rot=(0.57735,0.57735,0.57735;2.0944rad)
  sketch-geometry (48):
    g0: LineSegment StartX=-49.19 StartY=69.25 StartZ=0 EndX=-49.19 EndY=66.25 EndZ=0
    g1: LineSegment StartX=-49.19 StartY=63.5 StartZ=0 EndX=-49.19 EndY=60.5 EndZ=0
    g2: LineSegment StartX=-49.19 StartY=57.75 StartZ=0 EndX=-49.19 EndY=54.75 EndZ=0
    g3: LineSegment StartX=-49.19 StartY=52 StartZ=0 EndX=-49.19 EndY=49 EndZ=0
    g4: LineSegment StartX=-49.19 StartY=46.25 StartZ=0 EndX=-49.19 EndY=43.25 EndZ=0
    g5: LineSegment StartX=-49.19 StartY=40.5 StartZ=0 EndX=-49.19 EndY=37.5 EndZ=0
    g6: LineSegment StartX=-49.19 StartY=34.5 StartZ=0 EndX=-49.19 EndY=31.5 EndZ=0
    g7: LineSegment StartX=-49.19 StartY=28.75 StartZ=0 EndX=-49.19 EndY=25.75 EndZ=0
    g8: LineSegment StartX=-49.19 StartY=23 StartZ=0 EndX=-49.19 EndY=20 EndZ=0
    g9: LineSegment StartX=-49.19 StartY=17.25 StartZ=0 EndX=-49.19 EndY=14.25 EndZ=0
    g10: LineSegment StartX=-49.19 StartY=11.5 StartZ=0 EndX=-49.19 EndY=8.5 EndZ=0
    g11: LineSegment StartX=-49.19 StartY=5.75 StartZ=0 EndX=-49.19 EndY=2.75 EndZ=0
    g12: ArcOfCircle CenterX=-1.5 CenterY=67.75 CenterZ=0 NormalX=0 NormalY=0 NormalZ=1 AngleXU=0 Radius=1.5 StartAngle=4.71239 EndAngle=7.85398
    g13: ArcOfCircle CenterX=-1.5 CenterY=62 CenterZ=0 NormalX=0 NormalY=0 NormalZ=1 AngleXU=0 Radius=1.5 StartAngle=4.71239 EndAngle=7.85398
    g14: ArcOfCircle CenterX=-1.5 CenterY=56.25 CenterZ=0 NormalX=0 NormalY=0 NormalZ=1 AngleXU=0 Radius=1.5 StartAngle=4.71239 EndAngle=7.85398
    g15: ArcOfCircle CenterX=-11.49 CenterY=50.5 CenterZ=0 NormalX=0 NormalY=0 NormalZ=1 AngleXU=0 Radius=1.5 StartAngle=4.71239 EndAngle=7.85398
    g16: ArcOfCircle CenterX=-16.28 CenterY=44.75 CenterZ=0 NormalX=0 NormalY=0 NormalZ=1 AngleXU=0 Radius=1.5 StartAngle=4.71239 EndAngle=7.85398
    g17: ArcOfCircle CenterX=-18.2337 CenterY=39 CenterZ=0 NormalX=0 NormalY=0 NormalZ=1 AngleXU=0 Radius=1.5 StartAngle=4.71485 EndAngle=7.85398
    g18: ArcOfCircle CenterX=-16.2837 CenterY=27.25 CenterZ=0 NormalX=0 NormalY=0 NormalZ=1 AngleXU=0 Radius=1.5 StartAngle=4.71485 EndAngle=7.85398
    g19: ArcOfCircle CenterX=-18.2337 CenterY=33 CenterZ=0 NormalX=0 NormalY=0 NormalZ=1 AngleXU=0 Radius=1.5 StartAngle=4.71485 EndAngle=7.85398
    g20: ArcOfCircle CenterX=-11.49 CenterY=21.5 CenterZ=0 NormalX=0 NormalY=0 NormalZ=1 AngleXU=0 Radius=1.5 StartAngle=4.71239 EndAngle=7.85398
    g21: ArcOfCircle CenterX=-1.5 CenterY=4.25 CenterZ=0 NormalX=0 NormalY=0 NormalZ=1 AngleXU=0 Radius=1.5 StartAngle=4.71239 EndAngle=7.85398
    g22: ArcOfCircle CenterX=-1.5 CenterY=10 CenterZ=0 NormalX=0 NormalY=0 NormalZ=1 AngleXU=0 Radius=1.5 StartAngle=4.71239 EndAngle=7.85398
    g23: ArcOfCircle CenterX=-1.5 CenterY=15.75 CenterZ=0 NormalX=0 NormalY=0 NormalZ=1 AngleXU=0 Radius=1.5 StartAngle=4.71239 EndAngle=7.85398
    g24: LineSegment StartX=-49.19 StartY=69.25 StartZ=0 EndX=-1.5 EndY=69.25 EndZ=0
    g25: LineSegment StartX=-49.19 StartY=66.25 StartZ=0 EndX=-1.5 EndY=66.25 EndZ=0
    g26: LineSegment StartX=-49.19 StartY=63.5 StartZ=0 EndX=-1.5 EndY=63.5 EndZ=0
    g27: LineSegment StartX=-49.19 StartY=60.5 StartZ=0 EndX=-1.5 EndY=60.5 EndZ=0
    g28: LineSegment StartX=-49.19 StartY=57.75 StartZ=0 EndX=-1.5 EndY=57.75 EndZ=0
    g29: LineSegment StartX=-49.19 StartY=54.75 StartZ=0 EndX=-1.5 EndY=54.75 EndZ=0
    g30: LineSegment StartX=-49.19 StartY=52 StartZ=0 EndX=-11.49 EndY=52 EndZ=0
    g31: LineSegment StartX=-49.19 StartY=49 StartZ=0 EndX=-11.49 EndY=49 EndZ=0
    g32: LineSegment StartX=-49.19 StartY=46.25 StartZ=0 EndX=-16.28 EndY=46.25 EndZ=0
    g33: LineSegment StartX=-49.19 StartY=43.25 StartZ=0 EndX=-16.28 EndY=43.25 EndZ=0
    g34: LineSegment StartX=-49.19 StartY=40.5 StartZ=0 EndX=-18.2337 EndY=40.5 EndZ=0
    g35: LineSegment StartX=-49.19 StartY=37.5 StartZ=0 EndX=-18.23 EndY=37.5 EndZ=0
    g36: LineSegment StartX=-49.19 StartY=34.5 StartZ=0 EndX=-18.2337 EndY=34.5 EndZ=0
    g37: LineSegment StartX=-49.19 StartY=31.5 StartZ=0 EndX=-18.23 EndY=31.5 EndZ=0
    g38: LineSegment StartX=-49.19 StartY=28.75 StartZ=0 EndX=-16.2837 EndY=28.75 EndZ=0
    g39: LineSegment StartX=-49.19 StartY=25.75 StartZ=0 EndX=-16.28 EndY=25.75 EndZ=0
    g40: LineSegment StartX=-49.19 StartY=23 StartZ=0 EndX=-11.49 EndY=23 EndZ=0
    g41: LineSegment StartX=-49.19 StartY=20 StartZ=0 EndX=-11.49 EndY=20 EndZ=0
    g42: LineSegment StartX=-49.19 StartY=17.25 StartZ=0 EndX=-1.5 EndY=17.25 EndZ=0
    g43: LineSegment StartX=-49.19 StartY=14.25 StartZ=0 EndX=-1.5 EndY=14.25 EndZ=0
    g44: LineSegment StartX=-49.19 StartY=11.5 StartZ=0 EndX=-1.5 EndY=11.5 EndZ=0
    g45: LineSegment StartX=-49.19 StartY=8.5 StartZ=0 EndX=-1.5 EndY=8.5 EndZ=0
    g46: LineSegment StartX=-49.19 StartY=5.75 StartZ=0 EndX=-1.5 EndY=5.75 EndZ=0
    g47: LineSegment StartX=-49.19 StartY=2.75 StartZ=0 EndX=-1.5 EndY=2.75 EndZ=0
  constraints (120):
    c: Vertical(g0)
    c: Distance(g0) = 3
    c: Block(g0)
    c: Vertical(g1)
    c: Distance(g1) = 3
    c: Vertical(g2)
    c: Equal(g0,g2) = 3
    c: Block(g2)
    c: Vertical(g3)
    c: Equal(g1,g3) = 3
    c: Vertical(g4)
    c: Equal(g0,g4) = 3
    c: Block(g4)
    c: Vertical(g5)
    c: Equal(g1,g5) = 3
    c: Vertical(g6)
    c: Equal(g0,g6) = 3
    c: Block(g6)
    c: Vertical(g7)
    c: Equal(g1,g7) = 3
    c: Vertical(g8)
    c: Equal(g0,g8) = 3
    c: Block(g8)
    c: Vertical(g9)
    c: Equal(g1,g9) = 3
    c: Vertical(g10)
    c: Equal(g0,g10) = 3
    c: Block(g10)
    c: Vertical(g11)
    c: Equal(g1,g11) = 3
    c: Block(g12)
    c: Block(g13)
    c: Block(g14)
    c: Block(g15)
    c: Block(g16)
    c: Block(g17)
    c: Block(g18)
    c: Block(g19)
    c: Block(g20)
    c: Block(g21)
    c: Block(g22)
    c: Block(g23)
    c: Block(g11)
    c: Block(g9)
    c: Block(g7)
    c: Block(g5)
    c: Block(g3)
    c: Block(g1)
    c: Coincident(g24,g0)
    c: Coincident(g24,g12)
    c: Horizontal(g24)
    c: Coincident(g25,g0)
    c: Coincident(g25,g12)
    c: Horizontal(g25)
    c: Coincident(g26,g1)
    c: Coincident(g26,g13)
    c: Horizontal(g26)
    c: Coincident(g27,g1)
    c: Coincident(g27,g13)
    c: Horizontal(g27)
    c: Coincident(g28,g2)
    c: Coincident(g28,g14)
    c: Horizontal(g28)
    c: Coincident(g29,g2)
    c: Coincident(g29,g14)
    c: Horizontal(g29)
    c: Coincident(g30,g3)
    c: Coincident(g30,g15)
    c: Horizontal(g30)
    c: Coincident(g31,g3)
    c: Coincident(g31,g15)
    c: Horizontal(g31)
    c: Coincident(g32,g4)
    c: Coincident(g32,g16)
    c: Horizontal(g32)
    c: Coincident(g33,g4)
    c: Coincident(g33,g16)
    c: Horizontal(g33)
    c: Coincident(g34,g5)
    c: Coincident(g34,g17)
    c: Horizontal(g34)
    c: Coincident(g35,g5)
    c: Coincident(g35,g17)
    c: Horizontal(g35)
    c: Coincident(g36,g6)
    c: Coincident(g36,g19)
    c: Horizontal(g36)
    c: Coincident(g37,g6)
    c: Coincident(g37,g19)
    c: Horizontal(g37)
    c: Coincident(g38,g7)
    c: Coincident(g38,g18)
    c: Horizontal(g38)
    c: Coincident(g39,g7)
    c: Coincident(g39,g18)
    c: Horizontal(g39)
    c: Coincident(g40,g8)
    c: Coincident(g40,g20)
    c: Horizontal(g40)
    c: Coincident(g41,g8)
    c: Coincident(g41,g20)
    c: Horizontal(g41)
    c: Coincident(g42,g9)
    c: Coincident(g42,g23)
    c: Horizontal(g42)
    c: Coincident(g43,g9)
    c: Coincident(g43,g23)
    c: Horizontal(g43)
    c: Coincident(g44,g10)
    c: Coincident(g44,g22)
    c: Horizontal(g44)
    c: Coincident(g45,g10)
    c: Coincident(g45,g22)
    c: Horizontal(g45)
    c: Coincident(g46,g11)
    c: Coincident(g46,g21)
    c: Horizontal(g46)
    c: Coincident(g47,g11)
    c: Coincident(g47,g21)
    c: Horizontal(g47)
FEATURE [Part::Extrusion] Extrude023
  Base = -> Sketch032
  Dir = (1,-2e-16,2e-16)
  DirMode = 2
  FaceMakerClass = Part::FaceMakerBullseye
  LengthFwd = 19
  LengthRev = 0
  Placement = pos=(-19,0,0) rot=(0,0,1;0rad)
  Solid = true
  Symmetric = false
FEATURE [Part::Fillet] Fillet023
  Base = -> Extrude023
  Edges = <same value as first occurrence — deduplicated (x6 in doc)>
  Placement = pos=(0,0.05,0) rot=(0,0,1;0rad)
FEATURE [Part::Cut] Cut014  label="bottom003"
  Base = -> Cut007
  Tool = -> Fusion047
FEATURE [Part::Cut] Cut021  label="bottom004"
  Base = -> Cut014
  Tool = -> Fillet023
FEATURE [Sketcher::SketchObject] Sketch033
  FullyConstrained = true
  Placement = pos=(117,19,0) rot=(0.57735,0.57735,0.57735;2.0944rad)
  sketch-geometry (8):
    g0: LineSegment StartX=-49.19 StartY=69.25 StartZ=0 EndX=-49.19 EndY=66.25 EndZ=0
    g1: LineSegment StartX=-49.19 StartY=5.75 StartZ=0 EndX=-49.19 EndY=2.75 EndZ=0
    g2: ArcOfCircle CenterX=-1.5 CenterY=67.75 CenterZ=0 NormalX=0 NormalY=0 NormalZ=1 AngleXU=0 Radius=1.5 StartAngle=4.71239 EndAngle=7.85398
    g3: ArcOfCircle CenterX=-1.5 CenterY=4.25 CenterZ=0 NormalX=0 NormalY=0 NormalZ=1 AngleXU=0 Radius=1.5 StartAngle=4.71239 EndAngle=7.85398
    g4: LineSegment StartX=-49.19 StartY=69.25 StartZ=0 EndX=-1.5 EndY=69.25 EndZ=0
    g5: LineSegment StartX=-49.19 StartY=66.25 StartZ=0 EndX=-1.5 EndY=66.25 EndZ=0
    g6: LineSegment StartX=-49.19 StartY=5.75 StartZ=0 EndX=-1.5 EndY=5.75 EndZ=0
    g7: LineSegment StartX=-49.19 StartY=2.75 StartZ=0 EndX=-1.5 EndY=2.75 EndZ=0
  constraints (19):
    c: Vertical(g0)
    c: Distance(g0) = 3
    c: Block(g0)
    c: Vertical(g1)
    c: Block(g2)
    c: Block(g3)
    c: Block(g1)
    c: Coincident(g4,g0)
    c: Coincident(g4,g2)
    c: Horizontal(g4)
    c: Coincident(g5,g0)
    c: Coincident(g5,g2)
    c: Horizontal(g5)
    c: Coincident(g6,g1)
    c: Coincident(g6,g3)
    c: Horizontal(g6)
    c: Coincident(g7,g1)
    c: Coincident(g7,g3)
    c: Horizontal(g7)
FEATURE [Sketcher::SketchObject] Sketch034
  FullyConstrained = true
  Placement = pos=(117,19,0) rot=(0.57735,0.57735,0.57735;2.0944rad)
  sketch-geometry (8):
    g0: LineSegment StartX=-49.19 StartY=63.5 StartZ=0 EndX=-49.19 EndY=60.5 EndZ=0
    g1: LineSegment StartX=-49.19 StartY=11.5 StartZ=0 EndX=-49.19 EndY=8.5 EndZ=0
    g2: ArcOfCircle CenterX=-1.5 CenterY=62 CenterZ=0 NormalX=0 NormalY=0 NormalZ=1 AngleXU=0 Radius=1.5 StartAngle=4.71239 EndAngle=7.85398
    g3: ArcOfCircle CenterX=-1.5 CenterY=10 CenterZ=0 NormalX=0 NormalY=0 NormalZ=1 AngleXU=0 Radius=1.5 StartAngle=4.71239 EndAngle=7.85398
    g4: LineSegment StartX=-49.19 StartY=63.5 StartZ=0 EndX=-1.5 EndY=63.5 EndZ=0
    g5: LineSegment StartX=-49.19 StartY=60.5 StartZ=0 EndX=-1.5 EndY=60.5 EndZ=0
    g6: LineSegment StartX=-49.19 StartY=11.5 StartZ=0 EndX=-1.5 EndY=11.5 EndZ=0
    g7: LineSegment StartX=-49.19 StartY=8.5 StartZ=0 EndX=-1.5 EndY=8.5 EndZ=0
  constraints (19):
    c: Vertical(g0)
    c: Distance(g0) = 3
    c: Vertical(g1)
    c: Block(g1)
    c: Block(g2)
    c: Block(g3)
    c: Block(g0)
    c: Coincident(g4,g0)
    c: Coincident(g4,g2)
    c: Horizontal(g4)
    c: Coincident(g5,g0)
    c: Coincident(g5,g2)
    c: Horizontal(g5)
    c: Coincident(g6,g1)
    c: Coincident(g6,g3)
    c: Horizontal(g6)
    c: Coincident(g7,g1)
    c: Coincident(g7,g3)
    c: Horizontal(g7)
FEATURE [Part::Extrusion] Extrude024
  Base = -> Sketch033
  Dir = (1,0,0)
  DirMode = 2
  FaceMakerClass = Part::FaceMakerBullseye
  LengthFwd = 10
  LengthRev = 0
  Solid = true
  Symmetric = false
FEATURE [Part::Extrusion] Extrude025
  Base = -> Sketch034
  Dir = (1,0,0)
  DirMode = 2
  FaceMakerClass = Part::FaceMakerBullseye
  LengthFwd = 10
  LengthRev = 0
  Solid = true
  Symmetric = false
FEATURE [Part::Fillet] Fillet024  label="removeFromtMoreFrontCaseScrewRetainers"
  Base = -> Extrude024
  Edges = 4 edges r=1.49: [Edge6,Edge11,Edge18,Edge23]
  Placement = pos=(-11,0,0) rot=(0,0,1;0rad)
FEATURE [Part::Fillet] Fillet025  label="removeFromtMoreFrontCaseScrewRetainers001"
  Base = -> Extrude025
  Edges = 4 edges r=1.49: [Edge6,Edge11,Edge18,Edge23]
  Placement = pos=(-19,0,0) rot=(0,0,1;0rad)
FEATURE [Part::Cut] Cut022
  Base = -> Cut015
  Tool = -> Fillet025
FEATURE [Part::Cut] Cut023  label="screwRetainers"
  Base = -> Cut022
  Tool = -> Fillet024
FEATURE [Part::MultiFuse] Fusion056  label="bottom005"
  Shapes = -> [Fusion044,Cut021]
FEATURE [Part::MultiFuse] Fusion057  label="casePillars001"
  Shapes = -> [Cut016,Fusion052]
FEATURE [Part::MultiFuse] Fusion058  label="bottom006"
  Shapes = -> [Fusion056,Cut023]
FEATURE [Part::MultiFuse] Fusion059  label="bottom007"
  Shapes = -> [Fusion058,Fillet005]
FEATURE [Part::MultiFuse] Fusion060  label="bottom008"
  Shapes = -> [Fusion059,Fusion]
FEATURE [Part::MultiFuse] Fusion061  label="top011"
  Shapes = -> [Cut006,Cut020]
FEATURE [Part::MultiFuse] Fusion062  label="top012"
  Shapes = -> [Fusion057,Fusion061]
FEATURE [Sketcher::SketchObject] Sketch035  label="topSketch007"
  FullyConstrained = true
  sketch-geometry (6):
    g0: LineSegment StartX=19 StartY=38 StartZ=0 EndX=117 EndY=38 EndZ=0
    g1: ArcOfCircle CenterX=19 CenterY=19 CenterZ=0 NormalX=0 NormalY=0 NormalZ=1 AngleXU=0 Radius=19 StartAngle=1.5708 EndAngle=3.14159
    g2: LineSegment StartX=117 StartY=38 StartZ=0 EndX=117 EndY=19 EndZ=0
    g3: LineSegment StartX=98 StartY=1.0161e-12 StartZ=0 EndX=5.22862e-06 EndY=1.0161e-12 EndZ=0
    g4: LineSegment StartX=5.22862e-06 StartY=19 StartZ=0 EndX=5.22862e-06 EndY=1.0161e-12 EndZ=0
    g5: ArcOfCircle CenterX=98 CenterY=19 CenterZ=0 NormalX=0 NormalY=0 NormalZ=1 AngleXU=0 Radius=19 StartAngle=4.71239 EndAngle=6.28319
  constraints (16):
    c: Horizontal(g0)
    c: Distance(g0) = 98
    c: Coincident(g1,g0)
    c: Block(g1)
    c: Coincident(g2,g0)
    c: Vertical(g2)
    c: Distance(g2) = 19
    c: Horizontal(g3)
    c: Coincident(g4,g1)
    c: Vertical(g4)
    c: Coincident(g3,g4)
    c: Block(g3)
    c: Coincident(g5,g2)
    c: Coincident(g5,g3)
    c: Block(g0)
    c: Block(g5)
FEATURE [Part::Extrusion] Extrude026  label="sideA001"
  Base = -> Sketch035
  Dir = (0,0,1)
  DirMode = 2
  FaceMakerClass = Part::FaceMakerBullseye
  LengthFwd = 3
  LengthRev = 0
  Placement = pos=(0,0,-2.7) rot=(0,0,1;0rad)
  Solid = true
  Symmetric = false
FEATURE [Sketcher::SketchObject] Sketch036  label="topSketch008"
  FullyConstrained = true
  sketch-geometry (6):
    g0: LineSegment StartX=19 StartY=38 StartZ=0 EndX=117 EndY=38 EndZ=0
    g1: ArcOfCircle CenterX=19 CenterY=19 CenterZ=0 NormalX=0 NormalY=0 NormalZ=1 AngleXU=0 Radius=19 StartAngle=1.5708 EndAngle=3.14159
    g2: LineSegment StartX=117 StartY=38 StartZ=0 EndX=117 EndY=19 EndZ=0
    g3: LineSegment StartX=98 StartY=1.0161e-12 StartZ=0 EndX=5.22862e-06 EndY=1.0161e-12 EndZ=0
    g4: LineSegment StartX=5.22862e-06 StartY=19 StartZ=0 EndX=5.22862e-06 EndY=1.0161e-12 EndZ=0
    g5: ArcOfCircle CenterX=98 CenterY=19 CenterZ=0 NormalX=0 NormalY=0 NormalZ=1 AngleXU=0 Radius=19 StartAngle=4.71239 EndAngle=6.28319
  constraints (16):
    c: Horizontal(g0)
    c: Distance(g0) = 98
    c: Coincident(g1,g0)
    c: Block(g1)
    c: Coincident(g2,g0)
    c: Vertical(g2)
    c: Distance(g2) = 19
    c: Horizontal(g3)
    c: Coincident(g4,g1)
    c: Vertical(g4)
    c: Coincident(g3,g4)
    c: Block(g3)
    c: Coincident(g5,g2)
    c: Coincident(g5,g3)
    c: Block(g0)
    c: Block(g5)
FEATURE [Part::Extrusion] Extrude027  label="sideB001"
  Base = -> Sketch036
  Dir = (0,0,1)
  DirMode = 2
  FaceMakerClass = Part::FaceMakerBullseye
  LengthFwd = 3
  LengthRev = 0
  Placement = pos=(0,0,71.7) rot=(0,0,1;0rad)
  Solid = true
  Symmetric = false
FEATURE [Part::MultiFuse] Fusion064  label="removeFromBottom"
  Shapes = -> [Extrude026,Extrude027]
FEATURE [Part::Cut] Cut024  label="bottom009"
  Base = -> Fusion060
  Tool = -> Fusion064
FEATURE [Sketcher::SketchObject] Sketch037  label="topSketch009"
  FullyConstrained = true
  sketch-geometry (8):
    g0: ArcOfCircle CenterX=19 CenterY=19.1201 CenterZ=0 NormalX=0 NormalY=0 NormalZ=1 AngleXU=0 Radius=18.8799 StartAngle=1.5708 EndAngle=3.14793
    g1: LineSegment StartX=0.120501 StartY=19.0004 StartZ=0 EndX=0.120501 EndY=0.000382114 EndZ=0
    g2: LineSegment StartX=19 StartY=38 StartZ=0 EndX=124 EndY=38 EndZ=0
    g3: LineSegment StartX=0.120501 StartY=0.000382114 StartZ=0 EndX=105.121 EndY=0.000382114 EndZ=0
    g4: LineSegment StartX=124 StartY=38 StartZ=0 EndX=125.616 EndY=38 EndZ=0
    g5: LineSegment StartX=105.121 StartY=0.000382114 StartZ=0 EndX=106.736 EndY=0.000382114 EndZ=0
    g6: ArcOfCircle CenterX=106.616 CenterY=19 CenterZ=0 NormalX=0 NormalY=0 NormalZ=1 AngleXU=0 Radius=19 StartAngle=4.71873 EndAngle=6.28319
    g7: LineSegment StartX=125.616 StartY=38 StartZ=0 EndX=125.616 EndY=19 EndZ=0
  constraints (21):
    c: Block(g0)
    c: Coincident(g1,g0)
    c: Vertical(g1)
    c: Horizontal(g2)
    c: Distance(g2) = 105
    c: Coincident(g2,g0)
    c: Distance(g1) = 19
    c: Coincident(g3,g1)
    c: Horizontal(g3)
    c: Distance(g3) = 105
    c: Coincident(g4,g2)
    c: Horizontal(g4)
    c: Distance(g4) = 1.61553
    c: Horizontal(g5)
    c: Equal(g4,g5) = 1.61553
    c: Coincident(g5,g3)
    c: Block(g6)
    c: Coincident(g6,g5)
    c: Coincident(g7,g4)
    c: Coincident(g7,g6)
    c: Vertical(g7)
FEATURE [Part::Extrusion] Extrude028  label="sideB"
  Base = -> Sketch037
  Dir = (0,0,1)
  DirMode = 2
  FaceMakerClass = Part::FaceMakerBullseye
  LengthFwd = 3
  LengthRev = 0
  Placement = pos=(0,0,72) rot=(0,0,1;0rad)
  Solid = true
  Symmetric = false
FEATURE [Sketcher::SketchObject] Sketch038  label="topSketch010"
  FullyConstrained = true
  sketch-geometry (22):
    g0: LineSegment StartX=5.21097e-06 StartY=3 StartZ=0 EndX=5.21097e-06 EndY=19 EndZ=0
    g1: ArcOfCircle CenterX=19 CenterY=19 CenterZ=0 NormalX=0 NormalY=0 NormalZ=1 AngleXU=0 Radius=19 StartAngle=1.5708 EndAngle=3.14159
    g2: ArcOfCircle CenterX=19 CenterY=19 CenterZ=0 NormalX=0 NormalY=0 NormalZ=1 AngleXU=0 Radius=16 StartAngle=1.5708 EndAngle=3.14159
    g3: LineSegment StartX=114 StartY=35 StartZ=0 EndX=19 EndY=35 EndZ=0
    g4: LineSegment StartX=5.21097e-06 StartY=3 StartZ=0 EndX=5.21097e-06 EndY=0 EndZ=0
    g5: LineSegment StartX=3 StartY=0 StartZ=0 EndX=5.21097e-06 EndY=0 EndZ=0
    g6: LineSegment StartX=3 StartY=19 StartZ=0 EndX=3 EndY=0 EndZ=0
    g7: LineSegment StartX=19 StartY=38 StartZ=0 EndX=124 EndY=38 EndZ=0
    g8: Circle CenterX=119 CenterY=35 CenterZ=0 NormalX=0 NormalY=0 NormalZ=1 AngleXU=0 Radius=1
    g9: Circle CenterX=121 CenterY=35 CenterZ=0 NormalX=0 NormalY=0 NormalZ=1 AngleXU=0 Radius=1
    g10: Circle CenterX=121 CenterY=33 CenterZ=0 NormalX=0 NormalY=0 NormalZ=1 AngleXU=0 Radius=1
    g11: BSplineCurve PolesCount=3 KnotsCount=2 Degree=2 IsPeriodic=0
    g12: GeomPoint X=119 Y=35 Z=0
    g13: GeomPoint X=121 Y=33 Z=0
    g14: LineSegment StartX=119 StartY=35 StartZ=0 EndX=114 EndY=35 EndZ=0
    g15: ArcOfCircle CenterX=105 CenterY=19 CenterZ=0 NormalX=0 NormalY=0 NormalZ=1 AngleXU=0 Radius=16 StartAngle=5.60905 EndAngle=6.28319
    g16: LineSegment StartX=121 StartY=33 StartZ=0 EndX=121 EndY=19 EndZ=0
    g17: LineSegment StartX=117.5 StartY=9.01251 StartZ=0 EndX=121.163 EndY=9.0125 EndZ=0
    g18: ArcOfCircle CenterX=105 CenterY=19 CenterZ=0 NormalX=0 NormalY=0 NormalZ=1 AngleXU=0 Radius=20.6155 StartAngle=5.7297 EndAngle=6.28319
    g19: LineSegment StartX=121.163 StartY=9.0125 StartZ=0 EndX=122.538 EndY=8.16329 EndZ=0
    g20: LineSegment StartX=124 StartY=38 StartZ=0 EndX=125.616 EndY=38 EndZ=0
    g21: LineSegment StartX=125.616 StartY=19 StartZ=0 EndX=125.616 EndY=38 EndZ=0
  constraints (49):
    c: Vertical(g0)
    c: Block(g0)
    c: Coincident(g1,g0)
    c: Block(g1)
    c: Coincident(g2,g1)
    c: Block(g2)
    c: Coincident(g3,g2)
    c: Horizontal(g3)
    c: Tangent(g3,g2)
    c: Coincident(g4,g0)
    c: Distance(g4) = 3
    c: Vertical(g4)
    c: Coincident(g5,g4)
    c: Horizontal(g5)
    c: Coincident(g6,g2)
    c: Coincident(g6,g5)
    c: Vertical(g6)
    c: Horizontal(g7)
    c: Distance(g7) = 105
    c: Coincident(g7,g1)
    c: Block(g3)
    c: Weight(g8) = 1
    c: Equal(g8,g9)
    c: Equal(g8,g10)
    c: InternalAlignment(g8,g11)
    c: InternalAlignment(g9,g11)
    c: InternalAlignment(g10,g11)
    c: InternalAlignment(g12,g11)
    c: InternalAlignment(g13,g11)
    c: Block(g11)
    c: Coincident(g14,g11)
    c: Coincident(g14,g3)
    c: Horizontal(g14)
    c: Block(g15)
    c: Coincident(g16,g11)
    c: Coincident(g16,g15)
    c: Vertical(g16)
    c: Distance(g16) = 14
    c: Coincident(g17,g15)
    c: Block(g18)
    c: Coincident(g19,g18)
    c: Coincident(g20,g7)
    c: Horizontal(g20)
    c: Vertical(g21)
    c: Coincident(g20,g21)
    c: Block(g20)
    c: Block(g21)
    c: Block(g19)
    c: Block(g17)
FEATURE [Part::Extrusion] Extrude029
  Base = -> Sketch038
  Dir = (0,0,1)
  DirMode = 2
  FaceMakerClass = Part::FaceMakerBullseye
  LengthFwd = 72
  LengthRev = 0
  Solid = true
  Symmetric = false
FEATURE [Part::Feature] Face085
  shape: bbox 4.8 x 25.5 x 2e-07 mm, 1 faces, 0 solids (baked)
FEATURE [Part::Revolution] Revolve089  label="moreFrontCaseScrewPost003"
  Angle = 360
  Axis = (0,1,0)
  Base = (0,0,0)
  FaceMakerClass = Part::FaceMakerBullseye
  Placement = pos=(109.5,4.5,3.5) rot=(0,0,1;0rad)
  Solid = false
  Source = -> Face085
  Symmetric = false
FEATURE [Part::Feature] Face086
  shape: bbox 4.8 x 25.5 x 2e-07 mm, 1 faces, 0 solids (baked)
FEATURE [Part::Revolution] Revolve090  label="moreFrontCaseScrewPost004"
  Angle = 360
  Axis = (0,1,0)
  Base = (0,0,0)
  FaceMakerClass = Part::FaceMakerBullseye
  Placement = pos=(109.5,4.5,68.5) rot=(0,0,1;0rad)
  Solid = false
  Source = -> Face086
  Symmetric = false
FEATURE [Part::Fillet] Fillet026  label="top013"
  Base = -> Extrude029
  Edges = 1 edges r=2: [Edge35]
FEATURE [Sketcher::SketchObject] Sketch039
  FullyConstrained = true
  sketch-geometry (7):
    g0: LineSegment StartX=0 StartY=0 StartZ=0 EndX=0 EndY=6 EndZ=0
    g1: Circle CenterX=0 CenterY=0 CenterZ=0 NormalX=0 NormalY=0 NormalZ=1 AngleXU=0 Radius=1
    g2: Circle CenterX=8 CenterY=6 CenterZ=0 NormalX=0 NormalY=0 NormalZ=1 AngleXU=0 Radius=1
    g3: BSplineCurve PolesCount=3 KnotsCount=2 Degree=2 IsPeriodic=0
    g4: GeomPoint X=0 Y=0 Z=0
    g5: GeomPoint X=8 Y=6 Z=0
    g6: LineSegment StartX=0 StartY=6 StartZ=0 EndX=8 EndY=6 EndZ=0
  constraints (14):
    c: Coincident(g0,g-1)
    c: Distance(g0) = 6
    c: Vertical(g0)
    c: Coincident(g3,g0)
    c: Weight(g1) = 1
    c: Equal(g1,g2)
    c: InternalAlignment(g1,g3)
    c: InternalAlignment(g2,g3)
    c: InternalAlignment(g4,g3)
    c: InternalAlignment(g5,g3)
    c: Block(g3)
    c: Coincident(g6,g0)
    c: Coincident(g6,g3)
    c: Horizontal(g6)
FEATURE [Sketcher::SketchObject] Sketch040
  FullyConstrained = true
  sketch-geometry (7):
    g0: LineSegment StartX=0 StartY=0 StartZ=0 EndX=0 EndY=6 EndZ=0
    g1: Circle CenterX=0 CenterY=0 CenterZ=0 NormalX=0 NormalY=0 NormalZ=1 AngleXU=0 Radius=1
    g2: Circle CenterX=8 CenterY=6 CenterZ=0 NormalX=0 NormalY=0 NormalZ=1 AngleXU=0 Radius=1
    g3: BSplineCurve PolesCount=3 KnotsCount=2 Degree=2 IsPeriodic=0
    g4: GeomPoint X=0 Y=0 Z=0
    g5: GeomPoint X=8 Y=6 Z=0
    g6: LineSegment StartX=0 StartY=6 StartZ=0 EndX=8 EndY=6 EndZ=0
  constraints (14):
    c: Coincident(g0,g-1)
    c: Distance(g0) = 6
    c: Vertical(g0)
    c: Coincident(g3,g0)
    c: Weight(g1) = 1
    c: Equal(g1,g2)
    c: InternalAlignment(g1,g3)
    c: InternalAlignment(g2,g3)
    c: InternalAlignment(g4,g3)
    c: InternalAlignment(g5,g3)
    c: Block(g3)
    c: Coincident(g6,g0)
    c: Coincident(g6,g3)
    c: Horizontal(g6)
FEATURE [Sketcher::SketchObject] Sketch041
  FullyConstrained = true
  sketch-geometry (7):
    g0: LineSegment StartX=0 StartY=0 StartZ=0 EndX=0 EndY=6 EndZ=0
    g1: Circle CenterX=0 CenterY=0 CenterZ=0 NormalX=0 NormalY=0 NormalZ=1 AngleXU=0 Radius=1
    g2: Circle CenterX=8 CenterY=6 CenterZ=0 NormalX=0 NormalY=0 NormalZ=1 AngleXU=0 Radius=1
    g3: BSplineCurve PolesCount=3 KnotsCount=2 Degree=2 IsPeriodic=0
    g4: GeomPoint X=0 Y=0 Z=0
    g5: GeomPoint X=8 Y=6 Z=0
    g6: LineSegment StartX=0 StartY=6 StartZ=0 EndX=8 EndY=6 EndZ=0
  constraints (14):
    c: Coincident(g0,g-1)
    c: Distance(g0) = 6
    c: Vertical(g0)
    c: Coincident(g3,g0)
    c: Weight(g1) = 1
    c: Equal(g1,g2)
    c: InternalAlignment(g1,g3)
    c: InternalAlignment(g2,g3)
    c: InternalAlignment(g4,g3)
    c: InternalAlignment(g5,g3)
    c: Block(g3)
    c: Coincident(g6,g0)
    c: Coincident(g6,g3)
    c: Horizontal(g6)
FEATURE [Sketcher::SketchObject] Sketch042
  FullyConstrained = true
  sketch-geometry (7):
    g0: LineSegment StartX=0 StartY=0 StartZ=0 EndX=0 EndY=6 EndZ=0
    g1: Circle CenterX=0 CenterY=0 CenterZ=0 NormalX=0 NormalY=0 NormalZ=1 AngleXU=0 Radius=1
    g2: Circle CenterX=8 CenterY=6 CenterZ=0 NormalX=0 NormalY=0 NormalZ=1 AngleXU=0 Radius=1
    g3: BSplineCurve PolesCount=3 KnotsCount=2 Degree=2 IsPeriodic=0
    g4: GeomPoint X=0 Y=0 Z=0
    g5: GeomPoint X=8 Y=6 Z=0
    g6: LineSegment StartX=0 StartY=6 StartZ=0 EndX=8 EndY=6 EndZ=0
  constraints (14):
    c: Coincident(g0,g-1)
    c: Distance(g0) = 6
    c: Vertical(g0)
    c: Coincident(g3,g0)
    c: Weight(g1) = 1
    c: Equal(g1,g2)
    c: InternalAlignment(g1,g3)
    c: InternalAlignment(g2,g3)
    c: InternalAlignment(g4,g3)
    c: InternalAlignment(g5,g3)
    c: Block(g3)
    c: Coincident(g6,g0)
    c: Coincident(g6,g3)
    c: Horizontal(g6)
FEATURE [Part::Extrusion] Extrude030  label="caseScrewPillarBracket008"
  Base = -> Sketch039
  Dir = (0,0,1)
  DirMode = 2
  FaceMakerClass = Part::FaceMakerBullseye
  LengthFwd = 2.4
  LengthRev = 0
  Placement = pos=(15.76,29,8.8) rot=(0,1,0;0rad)
  Solid = true
  Symmetric = false
FEATURE [Part::Extrusion] Extrude031  label="caseScrewPillarBracket009"
  Base = -> Sketch040
  Dir = (0,0,1)
  DirMode = 2
  FaceMakerClass = Part::FaceMakerBullseye
  LengthFwd = 2.4
  LengthRev = 0
  Placement = pos=(15.76,29,60.8) rot=(0,0,1;0rad)
  Solid = true
  Symmetric = false
FEATURE [Part::Extrusion] Extrude032  label="caseScrewPillarBracket010"
  Base = -> Sketch041
  Dir = (0,0,1)
  DirMode = 2
  FaceMakerClass = Part::FaceMakerBullseye
  LengthFwd = 2.4
  LengthRev = 0
  Placement = pos=(13.7,29,13.26) rot=(0,-1,0;1.5708rad)
  Solid = true
  Symmetric = false
FEATURE [Part::Extrusion] Extrude033  label="caseScrewPillarBracket011"
  Base = -> Sketch042
  Dir = (0,0,1)
  DirMode = 2
  FaceMakerClass = Part::FaceMakerBullseye
  LengthFwd = 2.4
  LengthRev = 0
  Placement = pos=(11.3,29,58.74) rot=(0,1,0;1.5708rad)
  Solid = true
  Symmetric = false
FEATURE [Sketcher::SketchObject] Sketch043
  FullyConstrained = true
  sketch-geometry (7):
    g0: LineSegment StartX=0 StartY=0 StartZ=0 EndX=0 EndY=6 EndZ=0
    g1: Circle CenterX=0 CenterY=0 CenterZ=0 NormalX=0 NormalY=0 NormalZ=1 AngleXU=0 Radius=1
    g2: Circle CenterX=8 CenterY=6 CenterZ=0 NormalX=0 NormalY=0 NormalZ=1 AngleXU=0 Radius=1
    g3: BSplineCurve PolesCount=3 KnotsCount=2 Degree=2 IsPeriodic=0
    g4: GeomPoint X=0 Y=0 Z=0
    g5: GeomPoint X=8 Y=6 Z=0
    g6: LineSegment StartX=0 StartY=6 StartZ=0 EndX=8 EndY=6 EndZ=0
  constraints (14):
    c: Coincident(g0,g-1)
    c: Distance(g0) = 6
    c: Vertical(g0)
    c: Coincident(g3,g0)
    c: Weight(g1) = 1
    c: Equal(g1,g2)
    c: InternalAlignment(g1,g3)
    c: InternalAlignment(g2,g3)
    c: InternalAlignment(g4,g3)
    c: InternalAlignment(g5,g3)
    c: Block(g3)
    c: Coincident(g6,g0)
    c: Coincident(g6,g3)
    c: Horizontal(g6)
FEATURE [Part::Extrusion] Extrude034  label="caseScrewPillarBracket012"
  Base = -> Sketch043
  Dir = (0,0,1)
  DirMode = 2
  FaceMakerClass = Part::FaceMakerBullseye
  LengthFwd = 2.4
  LengthRev = 0
  Placement = pos=(88.3,29,65.23) rot=(0,1,0;1.5708rad)
  Solid = true
  Symmetric = false
FEATURE [Sketcher::SketchObject] Sketch044
  FullyConstrained = true
  sketch-geometry (7):
    g0: LineSegment StartX=0 StartY=0 StartZ=0 EndX=0 EndY=6 EndZ=0
    g1: Circle CenterX=0 CenterY=0 CenterZ=0 NormalX=0 NormalY=0 NormalZ=1 AngleXU=0 Radius=1
    g2: Circle CenterX=8 CenterY=6 CenterZ=0 NormalX=0 NormalY=0 NormalZ=1 AngleXU=0 Radius=1
    g3: BSplineCurve PolesCount=3 KnotsCount=2 Degree=2 IsPeriodic=0
    g4: GeomPoint X=0 Y=0 Z=0
    g5: GeomPoint X=8 Y=6 Z=0
    g6: LineSegment StartX=0 StartY=6 StartZ=0 EndX=8 EndY=6 EndZ=0
  constraints (14):
    c: Coincident(g0,g-1)
    c: Distance(g0) = 6
    c: Vertical(g0)
    c: Coincident(g3,g0)
    c: Weight(g1) = 1
    c: Equal(g1,g2)
    c: InternalAlignment(g1,g3)
    c: InternalAlignment(g2,g3)
    c: InternalAlignment(g4,g3)
    c: InternalAlignment(g5,g3)
    c: Block(g3)
    c: Coincident(g6,g0)
    c: Coincident(g6,g3)
    c: Horizontal(g6)
FEATURE [Part::Extrusion] Extrude035  label="caseScrewPillarBracket013"
  Base = -> Sketch044
  Dir = (0,0,1)
  DirMode = 2
  FaceMakerClass = Part::FaceMakerBullseye
  LengthFwd = 2.4
  LengthRev = 0
  Placement = pos=(90.7,29,6.77) rot=(0,-1,0;1.5708rad)
  Solid = true
  Symmetric = false
FEATURE [Sketcher::SketchObject] Sketch045
  FullyConstrained = true
  sketch-geometry (7):
    g0: LineSegment StartX=0 StartY=0 StartZ=0 EndX=0 EndY=6 EndZ=0
    g1: Circle CenterX=0 CenterY=0 CenterZ=0 NormalX=0 NormalY=0 NormalZ=1 AngleXU=0 Radius=1
    g2: Circle CenterX=8 CenterY=6 CenterZ=0 NormalX=0 NormalY=0 NormalZ=1 AngleXU=0 Radius=1
    g3: BSplineCurve PolesCount=3 KnotsCount=2 Degree=2 IsPeriodic=0
    g4: GeomPoint X=0 Y=0 Z=0
    g5: GeomPoint X=8 Y=6 Z=0
    g6: LineSegment StartX=0 StartY=6 StartZ=0 EndX=8 EndY=6 EndZ=0
  constraints (14):
    c: Coincident(g0,g-1)
    c: Distance(g0) = 6
    c: Vertical(g0)
    c: Coincident(g3,g0)
    c: Weight(g1) = 1
    c: Equal(g1,g2)
    c: InternalAlignment(g1,g3)
    c: InternalAlignment(g2,g3)
    c: InternalAlignment(g4,g3)
    c: InternalAlignment(g5,g3)
    c: Block(g3)
    c: Coincident(g6,g0)
    c: Coincident(g6,g3)
    c: Horizontal(g6)
FEATURE [Sketcher::SketchObject] Sketch046
  FullyConstrained = true
  sketch-geometry (7):
    g0: LineSegment StartX=0 StartY=0 StartZ=0 EndX=0 EndY=6 EndZ=0
    g1: Circle CenterX=0 CenterY=0 CenterZ=0 NormalX=0 NormalY=0 NormalZ=1 AngleXU=0 Radius=1
    g2: Circle CenterX=8 CenterY=6 CenterZ=0 NormalX=0 NormalY=0 NormalZ=1 AngleXU=0 Radius=1
    g3: BSplineCurve PolesCount=3 KnotsCount=2 Degree=2 IsPeriodic=0
    g4: GeomPoint X=0 Y=0 Z=0
    g5: GeomPoint X=8 Y=6 Z=0
    g6: LineSegment StartX=0 StartY=6 StartZ=0 EndX=8 EndY=6 EndZ=0
  constraints (14):
    c: Coincident(g0,g-1)
    c: Distance(g0) = 6
    c: Vertical(g0)
    c: Coincident(g3,g0)
    c: Weight(g1) = 1
    c: Equal(g1,g2)
    c: InternalAlignment(g1,g3)
    c: InternalAlignment(g2,g3)
    c: InternalAlignment(g4,g3)
    c: InternalAlignment(g5,g3)
    c: Block(g3)
    c: Coincident(g6,g0)
    c: Coincident(g6,g3)
    c: Horizontal(g6)
FEATURE [Part::Extrusion] Extrude036  label="caseScrewPillarBracket014"
  Base = -> Sketch045
  Dir = (0,0,1)
  DirMode = 2
  FaceMakerClass = Part::FaceMakerBullseye
  LengthFwd = 2.4
  LengthRev = 0
  Placement = pos=(110.7,29,6.77) rot=(0,-1,0;1.5708rad)
  Solid = true
  Symmetric = false
FEATURE [Part::Extrusion] Extrude037  label="caseScrewPillarBracket015"
  Base = -> Sketch046
  Dir = (0,0,1)
  DirMode = 2
  FaceMakerClass = Part::FaceMakerBullseye
  LengthFwd = 2.4
  LengthRev = 0
  Placement = pos=(108.3,29,65.23) rot=(0,1,0;1.5708rad)
  Solid = true
  Symmetric = false
FEATURE [Part::Box] Box013  label="frontCaseScrewPillarBracket002"
  AttacherType = Attacher::AttachEngine3D
  Height = 2.4
  Length = 22
  Placement = pos=(87,28,2.3) rot=(0,0,1;0rad)
  Width = 7
FEATURE [Part::Box] Box014  label="frontCaseScrewPillarBracket003"
  AttacherType = Attacher::AttachEngine3D
  Height = 2.4
  Length = 22
  Placement = pos=(87,28,67.3) rot=(0,0,1;0rad)
  Width = 7
FEATURE [Part::Feature] Face087
  shape: bbox 4.8 x 30.2 x 2e-07 mm, 1 faces, 0 solids (baked)
FEATURE [Part::Revolution] Revolve091  label="frontCaseScrewPost004"
  Angle = 360
  Axis = (0,1,0)
  Base = (0,0,0)
  FaceMakerClass = Part::FaceMakerBullseye
  Placement = pos=(89.5,4.5,3.5) rot=(0,0,1;0rad)
  Solid = false
  Source = -> Face087
  Symmetric = false
FEATURE [Part::Feature] Face088
  shape: bbox 4.8 x 30.2 x 2e-07 mm, 1 faces, 0 solids (baked)
FEATURE [Part::Revolution] Revolve092  label="frontCaseScrewPost005"
  Angle = 360
  Axis = (0,1,0)
  Base = (0,0,0)
  FaceMakerClass = Part::FaceMakerBullseye
  Placement = pos=(89.5,4.5,68.5) rot=(0,0,1;0rad)
  Solid = false
  Source = -> Face088
  Symmetric = false
FEATURE [Part::Feature] Face089
  shape: bbox 3.5 x 30.2 x 2e-07 mm, 1 faces, 0 solids (baked)
FEATURE [Part::Revolution] Revolve093  label="backCaseScrewPost002"
  Angle = 360
  Axis = (0,1,0)
  Base = (0,0,0)
  FaceMakerClass = Part::FaceMakerBullseye
  Placement = pos=(12.5,4.5,10) rot=(0,0,1;0rad)
  Solid = false
  Source = -> Face089
  Symmetric = false
FEATURE [Part::Feature] Face090
  shape: bbox 3.5 x 30.2 x 2e-07 mm, 1 faces, 0 solids (baked)
FEATURE [Part::Revolution] Revolve094  label="backCaseScrewPost003"
  Angle = 360
  Axis = (0,1,0)
  Base = (0,0,0)
  FaceMakerClass = Part::FaceMakerBullseye
  Placement = pos=(12.5,4.5,62) rot=(0,0,1;0rad)
  Solid = false
  Source = -> Face090
  Symmetric = false
FEATURE [Part::Box] Box015  label="Cube011"
  AttacherType = Attacher::AttachEngine3D
  Height = 28.8
  Length = 3
  Placement = pos=(107.3,28,21.6) rot=(0,0,1;0rad)
  Width = 7
FEATURE [Part::Box] Box016  label="Cube012"
  AttacherType = Attacher::AttachEngine3D
  Height = 3
  Length = 7.4
  Placement = pos=(107.3,28,18.6) rot=(0,0,1;0rad)
  Width = 7
FEATURE [Part::Box] Box017  label="Cube013"
  AttacherType = Attacher::AttachEngine3D
  Height = 3
  Length = 7.4
  Placement = pos=(107.3,28,50.4) rot=(0,0,1;0rad)
  Width = 7
FEATURE [Part::Cylinder] Cylinder024
  Angle = 360
  AttacherType = Attacher::AttachEngine3D
  Height = 20
  Placement = pos=(0,0,36.15) rot=(0,0,1;0rad)
  Radius = 14.3
FEATURE [Part::Cylinder] Cylinder025
  Angle = 360
  AttacherType = Attacher::AttachEngine3D
  Height = 10
  Placement = pos=(0,0,36.15) rot=(0,0,1;0rad)
  Radius = 4
FEATURE [Part::MultiFuse] Fusion066  label="removeToCreteHoleForPlugHousing009"
  Placement = pos=(70,19,36) rot=(0,1,0;1.5708rad)
  Shapes = -> [Cylinder024,Cylinder025]
FEATURE [Part::MultiFuse] Fusion065  label="plugHousingBracketHolder002"
  Shapes = -> [Box017,Box015,Box016]
FEATURE [Part::Cut] Cut025  label="plugHousingBracketHolder003"
  Base = -> Fusion065
  Placement = pos=(7,0,0) rot=(0,0,1;0rad)
  Tool = -> Fusion066
FEATURE [Sketcher::SketchObject] Sketch047
  FullyConstrained = false
  Placement = pos=(0,0,0) rot=(1,0,0;1.5708rad)
  sketch-geometry (24):
    g0: ArcOfCircle CenterX=-4 CenterY=-10.5 CenterZ=0 NormalX=0 NormalY=0 NormalZ=1 AngleXU=0 Radius=1.5 StartAngle=6e-16 EndAngle=3.14159
    g1: ArcOfCircle CenterX=-34.2 CenterY=-10.5 CenterZ=0 NormalX=0 NormalY=0 NormalZ=1 AngleXU=0 Radius=1.5 StartAngle=0 EndAngle=3.14159
    g2: ArcOfCircle CenterX=-34.2 CenterY=-27.7 CenterZ=0 NormalX=0 NormalY=0 NormalZ=1 AngleXU=0 Radius=1.5 StartAngle=3.14159 EndAngle=6.28319
    g3: ArcOfCircle CenterX=-4 CenterY=-27.7 CenterZ=0 NormalX=0 NormalY=0 NormalZ=1 AngleXU=0 Radius=1.5 StartAngle=3.1416 EndAngle=6.28319
    g4: ArcOfCircle CenterX=-10 CenterY=-4.3 CenterZ=0 NormalX=0 NormalY=0 NormalZ=1 AngleXU=0 Radius=1.5 StartAngle=2e-16 EndAngle=3.14159
    g5: ArcOfCircle CenterX=-16.1 CenterY=-1.8 CenterZ=0 NormalX=0 NormalY=0 NormalZ=1 AngleXU=0 Radius=1.5 StartAngle=5e-16 EndAngle=3.14159
    g6: ArcOfCircle CenterX=-22.1 CenterY=-1.8 CenterZ=0 NormalX=0 NormalY=0 NormalZ=1 AngleXU=0 Radius=1.5 StartAngle=5e-16 EndAngle=3.14159
    g7: ArcOfCircle CenterX=-28.2 CenterY=-4.3 CenterZ=0 NormalX=0 NormalY=0 NormalZ=1 AngleXU=0 Radius=1.5 StartAngle=2e-16 EndAngle=3.14159
    g8: ArcOfCircle CenterX=-10 CenterY=-33.9 CenterZ=0 NormalX=0 NormalY=0 NormalZ=1 AngleXU=0 Radius=1.5 StartAngle=3.14159 EndAngle=6.28319
    g9: ArcOfCircle CenterX=-16.1 CenterY=-36.4 CenterZ=0 NormalX=0 NormalY=0 NormalZ=1 AngleXU=0 Radius=1.5 StartAngle=3.14159 EndAngle=6.28319
    g10: ArcOfCircle CenterX=-22.1 CenterY=-36.4 CenterZ=0 NormalX=0 NormalY=0 NormalZ=1 AngleXU=0 Radius=1.5 StartAngle=3.14159 EndAngle=6.28319
    g11: ArcOfCircle CenterX=-28.2 CenterY=-33.9 CenterZ=0 NormalX=0 NormalY=0 NormalZ=1 AngleXU=0 Radius=1.5 StartAngle=3.14159 EndAngle=6.28319
    g12: LineSegment StartX=-35.7 StartY=-10.5 StartZ=0 EndX=-35.7 EndY=-27.7 EndZ=0
    g13: LineSegment StartX=-32.7 StartY=-10.5 StartZ=0 EndX=-32.7 EndY=-27.7 EndZ=0
    g14: LineSegment StartX=-29.7 StartY=-33.9 StartZ=0 EndX=-29.7 EndY=-4.3 EndZ=0
    g15: LineSegment StartX=-26.7 StartY=-33.9 StartZ=0 EndX=-26.7 EndY=-4.3 EndZ=0
    g16: LineSegment StartX=-2.5 StartY=-10.5 StartZ=0 EndX=-2.5 EndY=-27.7 EndZ=0
    g17: LineSegment StartX=-8.5 StartY=-4.3 StartZ=0 EndX=-8.5 EndY=-33.9 EndZ=0
    g18: LineSegment StartX=-5.5 StartY=-10.5 StartZ=0 EndX=-5.5 EndY=-27.7 EndZ=0
    g19: LineSegment StartX=-11.5 StartY=-4.3 StartZ=0 EndX=-11.5 EndY=-33.9 EndZ=0
    g20: LineSegment StartX=-14.6 StartY=-1.8 StartZ=0 EndX=-14.6 EndY=-36.4 EndZ=0
    g21: LineSegment StartX=-17.6 StartY=-1.8 StartZ=0 EndX=-17.6 EndY=-36.4 EndZ=0
    g22: LineSegment StartX=-20.6 StartY=-36.4 StartZ=0 EndX=-20.6 EndY=-1.8 EndZ=0
    g23: LineSegment StartX=-23.6 StartY=-1.8 StartZ=0 EndX=-23.6 EndY=-36.4 EndZ=0
  constraints (48):
    c: Block(g0)
    c: Block(g1)
    c: Block(g2)
    c: Block(g3)
    c: Block(g4)
    c: Block(g5)
    c: Block(g6)
    c: Block(g7)
    c: Block(g8)
    c: Block(g9)
    c: Block(g10)
    c: Block(g11)
    c: Coincident(g12,g1)
    c: Coincident(g12,g2)
    c: Vertical(g12)
    c: Coincident(g13,g1)
    c: Coincident(g13,g2)
    c: Vertical(g13)
    c: Coincident(g14,g11)
    c: Coincident(g14,g7)
    c: Vertical(g14)
    c: Coincident(g15,g11)
    c: Coincident(g15,g7)
    c: Vertical(g15)
    c: Coincident(g16,g0)
    c: Coincident(g16,g3)
    c: Vertical(g16)
    c: Coincident(g17,g4)
    c: Coincident(g17,g8)
    c: Vertical(g17)
    c: Coincident(g18,g0)
    c: Coincident(g18,g3)
    c: Vertical(g18)
    c: Coincident(g19,g4)
    c: Coincident(g19,g8)
    c: Vertical(g19)
    c: Coincident(g20,g5)
    c: Coincident(g20,g9)
    c: Vertical(g20)
    c: Coincident(g21,g5)
    c: Coincident(g21,g9)
    c: Vertical(g21)
    c: Coincident(g22,g10)
    c: Coincident(g22,g6)
    c: Vertical(g22)
    c: Coincident(g23,g6)
    c: Coincident(g23,g10)
    c: Vertical(g23)
FEATURE [Part::Extrusion] Extrude038  label="removeToCreateFanGrillHoles001"
  Base = -> Sketch047
  Dir = (0,-1,6e-16)
  DirMode = 2
  FaceMakerClass = Part::FaceMakerBullseye
  LengthFwd = 10
  LengthRev = 0
  Placement = pos=(65.4,44,54.82) rot=(0,0,1;0rad)
  Solid = true
  Symmetric = false
FEATURE [Part::Feature] Wire004
  shape: bbox 11 x 5.2 x 2e-07 mm, 0 faces, 0 solids (baked)
FEATURE [Part::Revolution] Revolve095
  Angle = 360
  Axis = (0,1,0)
  Base = (0,0,0)
  FaceMakerClass = Part::FaceMakerBullseye
  Placement = pos=(30.3,38,19.7) rot=(0,0,1;0rad)
  Solid = true
  Source = -> Wire004
  Symmetric = false
FEATURE [Part::Feature] Wire005
  shape: bbox 11 x 5.2 x 2e-07 mm, 0 faces, 0 solids (baked)
FEATURE [Part::Revolution] Revolve096
  Angle = 360
  Axis = (0,1,0)
  Base = (0,0,0)
  FaceMakerClass = Part::FaceMakerBullseye
  Placement = pos=(30.3,38,51.7) rot=(0,0,1;0rad)
  Solid = true
  Source = -> Wire005
  Symmetric = false
FEATURE [Part::Feature] Wire006
  shape: bbox 11 x 5.2 x 2e-07 mm, 0 faces, 0 solids (baked)
FEATURE [Part::Revolution] Revolve097
  Angle = 360
  Axis = (0,1,0)
  Base = (0,0,0)
  FaceMakerClass = Part::FaceMakerBullseye
  Placement = pos=(62.3,38,51.7) rot=(0,0,1;0rad)
  Solid = true
  Source = -> Wire006
  Symmetric = false
FEATURE [Part::Feature] Wire007
  shape: bbox 11 x 5.2 x 2e-07 mm, 0 faces, 0 solids (baked)
FEATURE [Part::Revolution] Revolve098
  Angle = 360
  Axis = (0,1,0)
  Base = (0,0,0)
  FaceMakerClass = Part::FaceMakerBullseye
  Placement = pos=(62.3,38,19.7) rot=(0,0,1;0rad)
  Solid = true
  Source = -> Wire007
  Symmetric = false
FEATURE [Part::MultiFuse] Fusion067  label="fanScrewHousing002"
  Shapes = -> [Revolve098,Revolve097,Revolve096,Revolve095]
FEATURE [Part::Feature] Face091 .. Face094  x4 (patterned run collapsed; names and placements below)
  shape: bbox 3.5 x 17.8 x 2e-07 mm, 1 faces, 0 solids (baked)
FEATURE [Part::Revolution] Revolve099  label="removeToCreateScrewAndThreadedInsertHole026"
  Angle = 360
  Axis = (0,1,0)
  Base = (0,0,0)
  FaceMakerClass = Part::FaceMakerBullseye
  Placement = pos=(62.3,30.3,19.7) rot=(0,0,1;0rad)
  Solid = false
  Source = -> Face091
  Symmetric = false
FEATURE [Part::Revolution] Revolve100  label="removeToCreateScrewAndThreadedInsertHole027"
  Angle = 360
  Axis = (0,1,0)
  Base = (0,0,0)
  FaceMakerClass = Part::FaceMakerBullseye
  Placement = pos=(62.3,30.3,51.7) rot=(0,0,1;0rad)
  Solid = false
  Source = -> Face092
  Symmetric = false
FEATURE [Part::Revolution] Revolve101  label="removeToCreateScrewAndThreadedInsertHole028"
  Angle = 360
  Axis = (0,1,0)
  Base = (0,0,0)
  FaceMakerClass = Part::FaceMakerBullseye
  Placement = pos=(30.3,30.3,19.7) rot=(0,0,1;0rad)
  Solid = false
  Source = -> Face093
  Symmetric = false
FEATURE [Part::Revolution] Revolve102  label="removeToCreateScrewAndThreadedInsertHole029"
  Angle = 360
  Axis = (0,1,0)
  Base = (0,0,0)
  FaceMakerClass = Part::FaceMakerBullseye
  Placement = pos=(30.3,30.3,51.7) rot=(0,0,1;0rad)
  Solid = false
  Source = -> Face094
  Symmetric = false
FEATURE [Part::MultiFuse] Fusion068  label="createThreadedInsertHolesForFan002"
  Shapes = -> [Revolve099,Revolve100,Revolve101,Revolve102]
FEATURE [Part::Cut] Cut026  label="fanScrewHousing003"
  Base = -> Fusion067
  Tool = -> Fusion068
FEATURE [Sketcher::SketchObject] Sketch048
  FullyConstrained = false
  Placement = pos=(0,0,0) rot=(1,0,0;1.5708rad)
  sketch-geometry (24):
    g0: ArcOfCircle CenterX=-4 CenterY=-10.5 CenterZ=0 NormalX=0 NormalY=0 NormalZ=1 AngleXU=0 Radius=1.5 StartAngle=6e-16 EndAngle=3.14159
    g1: ArcOfCircle CenterX=-34.2 CenterY=-10.5 CenterZ=0 NormalX=0 NormalY=0 NormalZ=1 AngleXU=0 Radius=1.5 StartAngle=0 EndAngle=3.14159
    g2: ArcOfCircle CenterX=-34.2 CenterY=-27.7 CenterZ=0 NormalX=0 NormalY=0 NormalZ=1 AngleXU=0 Radius=1.5 StartAngle=3.14159 EndAngle=6.28319
    g3: ArcOfCircle CenterX=-4 CenterY=-27.7 CenterZ=0 NormalX=0 NormalY=0 NormalZ=1 AngleXU=0 Radius=1.5 StartAngle=3.1416 EndAngle=6.28319
    g4: ArcOfCircle CenterX=-10 CenterY=-4.3 CenterZ=0 NormalX=0 NormalY=0 NormalZ=1 AngleXU=0 Radius=1.5 StartAngle=2e-16 EndAngle=3.14159
    g5: ArcOfCircle CenterX=-16.1 CenterY=-1.8 CenterZ=0 NormalX=0 NormalY=0 NormalZ=1 AngleXU=0 Radius=1.5 StartAngle=5e-16 EndAngle=3.14159
    g6: ArcOfCircle CenterX=-22.1 CenterY=-1.8 CenterZ=0 NormalX=0 NormalY=0 NormalZ=1 AngleXU=0 Radius=1.5 StartAngle=5e-16 EndAngle=3.14159
    g7: ArcOfCircle CenterX=-28.2 CenterY=-4.3 CenterZ=0 NormalX=0 NormalY=0 NormalZ=1 AngleXU=0 Radius=1.5 StartAngle=2e-16 EndAngle=3.14159
    g8: ArcOfCircle CenterX=-10 CenterY=-33.9 CenterZ=0 NormalX=0 NormalY=0 NormalZ=1 AngleXU=0 Radius=1.5 StartAngle=3.14159 EndAngle=6.28319
    g9: ArcOfCircle CenterX=-16.1 CenterY=-36.4 CenterZ=0 NormalX=0 NormalY=0 NormalZ=1 AngleXU=0 Radius=1.5 StartAngle=3.14159 EndAngle=6.28319
    g10: ArcOfCircle CenterX=-22.1 CenterY=-36.4 CenterZ=0 NormalX=0 NormalY=0 NormalZ=1 AngleXU=0 Radius=1.5 StartAngle=3.14159 EndAngle=6.28319
    g11: ArcOfCircle CenterX=-28.2 CenterY=-33.9 CenterZ=0 NormalX=0 NormalY=0 NormalZ=1 AngleXU=0 Radius=1.5 StartAngle=3.14159 EndAngle=6.28319
    g12: LineSegment StartX=-35.7 StartY=-10.5 StartZ=0 EndX=-35.7 EndY=-27.7 EndZ=0
    g13: LineSegment StartX=-32.7 StartY=-10.5 StartZ=0 EndX=-32.7 EndY=-27.7 EndZ=0
    g14: LineSegment StartX=-29.7 StartY=-33.9 StartZ=0 EndX=-29.7 EndY=-4.3 EndZ=0
    g15: LineSegment StartX=-26.7 StartY=-33.9 StartZ=0 EndX=-26.7 EndY=-4.3 EndZ=0
    g16: LineSegment StartX=-2.5 StartY=-10.5 StartZ=0 EndX=-2.5 EndY=-27.7 EndZ=0
    g17: LineSegment StartX=-8.5 StartY=-4.3 StartZ=0 EndX=-8.5 EndY=-33.9 EndZ=0
    g18: LineSegment StartX=-5.5 StartY=-10.5 StartZ=0 EndX=-5.5 EndY=-27.7 EndZ=0
    g19: LineSegment StartX=-11.5 StartY=-4.3 StartZ=0 EndX=-11.5 EndY=-33.9 EndZ=0
    g20: LineSegment StartX=-14.6 StartY=-1.8 StartZ=0 EndX=-14.6 EndY=-36.4 EndZ=0
    g21: LineSegment StartX=-17.6 StartY=-1.8 StartZ=0 EndX=-17.6 EndY=-36.4 EndZ=0
    g22: LineSegment StartX=-20.6 StartY=-36.4 StartZ=0 EndX=-20.6 EndY=-1.8 EndZ=0
    g23: LineSegment StartX=-23.6 StartY=-1.8 StartZ=0 EndX=-23.6 EndY=-36.4 EndZ=0
  constraints (48):
    c: Block(g0)
    c: Block(g1)
    c: Block(g2)
    c: Block(g3)
    c: Block(g4)
    c: Block(g5)
    c: Block(g6)
    c: Block(g7)
    c: Block(g8)
    c: Block(g9)
    c: Block(g10)
    c: Block(g11)
    c: Coincident(g12,g1)
    c: Coincident(g12,g2)
    c: Vertical(g12)
    c: Coincident(g13,g1)
    c: Coincident(g13,g2)
    c: Vertical(g13)
    c: Coincident(g14,g11)
    c: Coincident(g14,g7)
    c: Vertical(g14)
    c: Coincident(g15,g11)
    c: Coincident(g15,g7)
    c: Vertical(g15)
    c: Coincident(g16,g0)
    c: Coincident(g16,g3)
    c: Vertical(g16)
    c: Coincident(g17,g4)
    c: Coincident(g17,g8)
    c: Vertical(g17)
    c: Coincident(g18,g0)
    c: Coincident(g18,g3)
    c: Vertical(g18)
    c: Coincident(g19,g4)
    c: Coincident(g19,g8)
    c: Vertical(g19)
    c: Coincident(g20,g5)
    c: Coincident(g20,g9)
    c: Vertical(g20)
    c: Coincident(g21,g5)
    c: Coincident(g21,g9)
    c: Vertical(g21)
    c: Coincident(g22,g10)
    c: Coincident(g22,g6)
    c: Vertical(g22)
    c: Coincident(g23,g6)
    c: Coincident(g23,g10)
    c: Vertical(g23)
FEATURE [Part::Extrusion] Extrude039  label="removeToCreateFanGrillHoles002"
  Base = -> Sketch048
  Dir = (0,-1,6e-16)
  DirMode = 2
  FaceMakerClass = Part::FaceMakerBullseye
  LengthFwd = 10
  LengthRev = 0
  Placement = pos=(65.4,44,54.82) rot=(0,0,1;0rad)
  Solid = true
  Symmetric = false
FEATURE [Part::Cut] Cut027  label="fanScrewHousing004"
  Base = -> Cut026
  Tool = -> Extrude038
FEATURE [Part::Cut] Cut028  label="top014"
  Base = -> Fillet026
  Tool = -> Extrude039
FEATURE [Part::Feature] Face095 .. Face098  x4 (patterned run collapsed; names and placements below)
  shape: bbox 3.5 x 17.8 x 2e-07 mm, 1 faces, 0 solids (baked)
FEATURE [Part::Revolution] Revolve103  label="removeToCreateScrewAndThreadedInsertHole030"
  Angle = 360
  Axis = (0,1,0)
  Base = (0,0,0)
  FaceMakerClass = Part::FaceMakerBullseye
  Placement = pos=(62.3,30.3,19.7) rot=(0,0,1;0rad)
  Solid = false
  Source = -> Face095
  Symmetric = false
FEATURE [Part::Revolution] Revolve104  label="removeToCreateScrewAndThreadedInsertHole031"
  Angle = 360
  Axis = (0,1,0)
  Base = (0,0,0)
  FaceMakerClass = Part::FaceMakerBullseye
  Placement = pos=(62.3,30.3,51.7) rot=(0,0,1;0rad)
  Solid = false
  Source = -> Face096
  Symmetric = false
FEATURE [Part::Revolution] Revolve105  label="removeToCreateScrewAndThreadedInsertHole032"
  Angle = 360
  Axis = (0,1,0)
  Base = (0,0,0)
  FaceMakerClass = Part::FaceMakerBullseye
  Placement = pos=(30.3,30.3,19.7) rot=(0,0,1;0rad)
  Solid = false
  Source = -> Face097
  Symmetric = false
FEATURE [Part::Revolution] Revolve106  label="removeToCreateScrewAndThreadedInsertHole033"
  Angle = 360
  Axis = (0,1,0)
  Base = (0,0,0)
  FaceMakerClass = Part::FaceMakerBullseye
  Placement = pos=(30.3,30.3,51.7) rot=(0,0,1;0rad)
  Solid = false
  Source = -> Face098
  Symmetric = false
FEATURE [Part::MultiFuse] Fusion069  label="createThreadedInsertHolesForFan003"
  Shapes = -> [Revolve103,Revolve104,Revolve105,Revolve106]
FEATURE [Part::Cut] Cut029  label="top015"
  Base = -> Cut028
  Tool = -> Fusion054
FEATURE [Part::Cut] Cut030  label="fanScrewHousing005"
  Base = -> Cut027
  Tool = -> Fusion069
FEATURE [Part::Cylinder] Cylinder026  label="removeToCreteHoleForPlugHousing010"
  Angle = 360
  AttacherType = Attacher::AttachEngine3D
  Height = 20
  Placement = pos=(-2,19,36) rot=(0,1,0;1.5708rad)
  Radius = 14.3
FEATURE [Part::Box] Box018  label="removeToCreteHoleForPlugHousing011"
  AttacherType = Attacher::AttachEngine3D
  Height = 28.6
  Length = 10
  Placement = pos=(-2,0,21.7) rot=(0,0,1;0rad)
  Width = 19
FEATURE [Part::Box] Box019  label="wireHolderBottomCaseBit"
  AttacherType = Attacher::AttachEngine3D
  Height = 28
  Length = 3
  Placement = pos=(0,0,22) rot=(0,0,1;0rad)
  Width = 21
FEATURE [Part::Cylinder] Cylinder027  label="removeToCreteHoleForPlugHousing012"
  Angle = 360
  AttacherType = Attacher::AttachEngine3D
  Height = 20
  Placement = pos=(-2,19,36) rot=(0,1,0;1.5708rad)
  Radius = 14.3
FEATURE [Part::Cut] Cut031  label="wireHolderBottomCaseBit001"
  Base = -> Box019
  Tool = -> Cylinder027
FEATURE [Part::MultiFuse] Fusion070  label="removeToCreteHoleForPlugHousing013"
  Shapes = -> [Box018,Cylinder026]
FEATURE [Part::Cut] Cut032  label="top016"
  Base = -> Cut029
  Tool = -> Fusion070
FEATURE [Part::Cylinder] Cylinder028
  Angle = 360
  AttacherType = Attacher::AttachEngine3D
  Height = 20
  Placement = pos=(0,0,36.15) rot=(0,0,1;0rad)
  Radius = 14.3
FEATURE [Part::Cylinder] Cylinder029
  Angle = 360
  AttacherType = Attacher::AttachEngine3D
  Height = 10
  Placement = pos=(0,0,36.15) rot=(0,0,1;0rad)
  Radius = 4
FEATURE [Part::MultiFuse] Fusion071  label="removeToCreteHoleForPlugHousing014"
  Placement = pos=(70,19,36) rot=(0,1,0;1.5708rad)
  Shapes = -> [Cylinder028,Cylinder029]
FEATURE [Sketcher::SketchObject] Sketch049  label="topSketch011"
  FullyConstrained = true
  sketch-geometry (4):
    g0: ArcOfCircle CenterX=105 CenterY=19 CenterZ=0 NormalX=0 NormalY=0 NormalZ=1 AngleXU=0 Radius=20.6155 StartAngle=5.54125 EndAngle=6.28319
    g1: ArcOfCircle CenterX=105 CenterY=19 CenterZ=0 NormalX=0 NormalY=0 NormalZ=1 AngleXU=0 Radius=13 StartAngle=5.54125 EndAngle=6.28319
    g2: LineSegment StartX=118 StartY=19 StartZ=0 EndX=125.616 EndY=19 EndZ=0
    g3: LineSegment StartX=114.583 StartY=10.2157 StartZ=0 EndX=120.197 EndY=5.06982 EndZ=0
  constraints (7):
    c: Block(g0)
    c: Block(g1)
    c: Coincident(g2,g1)
    c: Coincident(g2,g0)
    c: Horizontal(g2)
    c: Coincident(g3,g1)
    c: Coincident(g3,g0)
FEATURE [Part::Box] Box020  label="removeToCreteHoleForPlugHousing015"
  AttacherType = Attacher::AttachEngine3D
  Height = 28.6
  Length = 20
  Placement = pos=(106.15,0,21.7) rot=(0,0,1;0rad)
  Width = 19
FEATURE [Part::MultiFuse] Fusion072  label="removeToCreteHoleForPlugHousing016"
  Shapes = -> [Box020,Fusion071]
FEATURE [Part::Cut] Cut033  label="removeToCreteHoleForPlugHousing017"
  Base = -> Cut032
  Tool = -> Fusion072
FEATURE [Part::Cylinder] Cylinder030
  Angle = 360
  AttacherType = Attacher::AttachEngine3D
  Height = 20
  Placement = pos=(0,0,36.15) rot=(0,0,1;0rad)
  Radius = 14.3
FEATURE [Part::Cylinder] Cylinder031
  Angle = 360
  AttacherType = Attacher::AttachEngine3D
  Height = 10
  Placement = pos=(0,0,36.15) rot=(0,0,1;0rad)
  Radius = 4
FEATURE [Part::Box] Box021  label="removeToCreteHoleForPlugHousing019"
  AttacherType = Attacher::AttachEngine3D
  Height = 28.6
  Length = 20
  Placement = pos=(106.15,0,21.7) rot=(0,0,1;0rad)
  Width = 19
FEATURE [Part::MultiFuse] Fusion074  label="removeToCreteHoleForPlugHousing020"
  Placement = pos=(70,19,36) rot=(0,1,0;1.5708rad)
  Shapes = -> [Cylinder030,Cylinder031]
FEATURE [Part::MultiFuse] Fusion073  label="removeToCreteHoleForPlugHousing018"
  Placement = pos=(0,0,28.3) rot=(0,0,1;0rad)
  Shapes = -> [Box021,Fusion074]
FEATURE [Part::Cylinder] Cylinder032
  Angle = 360
  AttacherType = Attacher::AttachEngine3D
  Height = 20
  Placement = pos=(0,0,36.15) rot=(0,0,1;0rad)
  Radius = 14.3
FEATURE [Part::Cylinder] Cylinder033
  Angle = 360
  AttacherType = Attacher::AttachEngine3D
  Height = 10
  Placement = pos=(0,0,36.15) rot=(0,0,1;0rad)
  Radius = 4
FEATURE [Part::Box] Box022  label="removeToCreteHoleForPlugHousing021"
  AttacherType = Attacher::AttachEngine3D
  Height = 28.6
  Length = 20
  Placement = pos=(106.15,0,21.7) rot=(0,0,1;0rad)
  Width = 19
FEATURE [Part::MultiFuse] Fusion076  label="removeToCreteHoleForPlugHousing023"
  Placement = pos=(70,19,36) rot=(0,1,0;1.5708rad)
  Shapes = -> [Cylinder032,Cylinder033]
FEATURE [Part::MultiFuse] Fusion075  label="removeToCreteHoleForPlugHousing022"
  Placement = pos=(0,0,-28.3) rot=(0,0,1;0rad)
  Shapes = -> [Box022,Fusion076]
FEATURE [Part::MultiFuse] Fusion077  label="removeToCreatePlugHousingBottomBit"
  Shapes = -> [Fusion075,Fusion073]
FEATURE [Part::Cylinder] Cylinder034
  Angle = 360
  AttacherType = Attacher::AttachEngine3D
  Height = 20
  Placement = pos=(0,0,36.15) rot=(0,0,1;0rad)
  Radius = 14
FEATURE [Part::Cylinder] Cylinder035
  Angle = 360
  AttacherType = Attacher::AttachEngine3D
  Height = 10
  Placement = pos=(0,0,36.15) rot=(0,0,1;0rad)
  Radius = 4
FEATURE [Part::MultiFuse] Fusion078  label="removeToCreteHoleForPlugHousing024"
  Placement = pos=(70,19,36) rot=(0,1,0;1.5708rad)
  Shapes = -> [Cylinder034,Cylinder035]
FEATURE [Part::MultiFuse] Fusion079  label="removeToCreatePlugHousingBottomBit001"
  Shapes = -> [Fusion078,Fusion077]
FEATURE [Part::Extrusion] Extrude040  label="bottomPlugHousingBit"
  Base = -> Sketch049
  Dir = (0,0,1)
  DirMode = 2
  FaceMakerClass = Part::FaceMakerBullseye
  LengthFwd = 72
  LengthRev = 0
  Solid = true
  Symmetric = false
FEATURE [Part::Cut] Cut034  label="bottomPlugHousingBit001"
  Base = -> Extrude040
  Placement = pos=(-0.09,0,0) rot=(0,0,1;0rad)
  Tool = -> Fusion079
FEATURE [Part::Box] Box023  label="Cube014"
  AttacherType = Attacher::AttachEngine3D
  Height = 16
  Length = 8
  Placement = pos=(12.7,31.52,28) rot=(0,0,1;0rad)
  Width = 4
FEATURE [Part::Cylinder] Cylinder036
  Angle = 360
  AttacherType = Attacher::AttachEngine3D
  Height = 10
  Placement = pos=(0,0,36.15) rot=(0,0,1;0rad)
  Radius = 4
FEATURE [Part::Cylinder] Cylinder037
  Angle = 360
  AttacherType = Attacher::AttachEngine3D
  Height = 20
  Placement = pos=(0,0,36.15) rot=(0,0,1;0rad)
  Radius = 8.2
FEATURE [Part::MultiFuse] Fusion080  label="removeToCreteHoleForPlugHousing025"
  Placement = pos=(-42,19,36) rot=(0,1,0;1.5708rad)
  Shapes = -> [Cylinder037,Cylinder036]
FEATURE [Sketcher::SketchObject] Sketch050  label="topSketch012"
  FullyConstrained = true
  sketch-geometry (4):
    g0: LineSegment StartX=16.8446 StartY=31.512 StartZ=0 EndX=16.3251 EndY=34.4666 EndZ=0
    g1: ArcOfCircle CenterX=19 CenterY=19.2524 CenterZ=0 NormalX=0 NormalY=0 NormalZ=1 AngleXU=0 Radius=15.4476 StartAngle=1.74483 EndAngle=2.72717
    g2: ArcOfCircle CenterX=19 CenterY=19.2524 CenterZ=0 NormalX=0 NormalY=0 NormalZ=1 AngleXU=0 Radius=12.4476 StartAngle=1.74483 EndAngle=2.73189
    g3: LineSegment StartX=4.86004 StartY=25.4725 StartZ=0 EndX=7.58253 EndY=24.2107 EndZ=0
  constraints (7):
    c: Block(g0)
    c: Coincident(g1,g0)
    c: Coincident(g2,g0)
    c: Coincident(g3,g1)
    c: Coincident(g3,g2)
    c: Block(g1)
    c: Block(g2)
FEATURE [Part::Extrusion] Extrude041
  Base = -> Sketch050
  Dir = (0,0,1)
  DirMode = 2
  FaceMakerClass = Part::FaceMakerBullseye
  LengthFwd = 10.6
  LengthRev = 0
  Placement = pos=(0,0,31) rot=(0,0,1;0rad)
  Solid = true
  Symmetric = false
FEATURE [Part::Cut] Cut035
  Base = -> Extrude041
  Placement = pos=(0,0,-0.3) rot=(0,0,1;0rad)
  Tool = -> Fusion080
FEATURE [Part::Cut] Cut036
  Base = -> Box023
  Tool = -> Cut035
FEATURE [Part::Fillet] Fillet027
  Base = -> Cut036
  Edges = 1 edges r=0.7: [Edge13]
FEATURE [Part::Fillet] Fillet028
  Base = -> Fillet027
  Edges = 1 edges r=0.7: [Edge13]
FEATURE [Part::Fillet] Fillet029
  Base = -> Fillet028
  Edges = 1 edges r=0.7: [Edge16]
FEATURE [Part::Fillet] Fillet030
  Base = -> Fillet029
  Edges = 1 edges r=0.7: [Edge11]
FEATURE [Part::Fillet] Fillet031
  Base = -> Fillet030
  Edges = 1 edges r=0.7: [Edge10]
FEATURE [Part::Fillet] Fillet032
  Base = -> Fillet031
  Edges = 1 edges r=1.2: [Edge5]
FEATURE [Part::Fillet] Fillet033
  Base = -> Fillet032
  Edges = 1 edges r=1.2: [Edge12]
FEATURE [Part::Fillet] Fillet034  label="wireHousingRetainer"
  Base = -> Fillet033
  Edges = 1 edges r=2: [Edge1]
  Placement = pos=(0.3,0,0) rot=(0,0,1;0rad)
FEATURE [Part::Feature] Face099
  shape: bbox 3.5 x 17.8 x 2e-07 mm, 1 faces, 0 solids (baked)
FEATURE [Part::Revolution] Revolve107  label="removeToCreateScrewAndThreadedInsertHole034"
  Angle = 360
  Axis = (0,1,0)
  Base = (0,0,0)
  FaceMakerClass = Part::FaceMakerBullseye
  Placement = pos=(12.5,0,10) rot=(0,0,1;0rad)
  Solid = false
  Source = -> Face099
  Symmetric = false
FEATURE [Part::Feature] Face100
  shape: bbox 3.5 x 17.8 x 2e-07 mm, 1 faces, 0 solids (baked)
FEATURE [Part::Revolution] Revolve108  label="removeToCreateScrewAndThreadedInsertHole035"
  Angle = 360
  Axis = (0,1,0)
  Base = (0,0,0)
  FaceMakerClass = Part::FaceMakerBullseye
  Placement = pos=(12.5,0,62) rot=(0,0,1;0rad)
  Solid = false
  Source = -> Face100
  Symmetric = false
FEATURE [Part::Feature] Face101
  shape: bbox 3.5 x 17.8 x 2e-07 mm, 1 faces, 0 solids (baked)
FEATURE [Part::Revolution] Revolve109  label="removeToCreateScrewAndThreadedInsertHole036"
  Angle = 360
  Axis = (0,1,0)
  Base = (0,0,0)
  FaceMakerClass = Part::FaceMakerBullseye
  Placement = pos=(89.5,0,68.5) rot=(0,0,1;0rad)
  Solid = false
  Source = -> Face101
  Symmetric = false
FEATURE [Part::Feature] Face102
  shape: bbox 3.5 x 17.8 x 2e-07 mm, 1 faces, 0 solids (baked)
FEATURE [Part::Revolution] Revolve110  label="removeToCreateScrewAndThreadedInsertHole037"
  Angle = 360
  Axis = (0,1,0)
  Base = (0,0,0)
  FaceMakerClass = Part::FaceMakerBullseye
  Placement = pos=(89.5,0,3.5) rot=(0,0,1;0rad)
  Solid = false
  Source = -> Face102
  Symmetric = false
FEATURE [Part::Feature] Face103
  shape: bbox 3.5 x 17.8 x 2e-07 mm, 1 faces, 0 solids (baked)
FEATURE [Part::Revolution] Revolve111  label="removeToCreateScrewAndThreadedInsertHole038"
  Angle = 360
  Axis = (0,1,0)
  Base = (0,0,0)
  FaceMakerClass = Part::FaceMakerBullseye
  Placement = pos=(109.5,4.7,3.5) rot=(0,0,1;0rad)
  Solid = false
  Source = -> Face103
  Symmetric = false
FEATURE [Part::Feature] Face104
  shape: bbox 3.5 x 17.8 x 2e-07 mm, 1 faces, 0 solids (baked)
FEATURE [Part::Revolution] Revolve112  label="removeToCreateScrewAndThreadedInsertHole039"
  Angle = 360
  Axis = (0,1,0)
  Base = (0,0,0)
  FaceMakerClass = Part::FaceMakerBullseye
  Placement = pos=(109.5,4.7,68.5) rot=(0,0,1;0rad)
  Solid = false
  Source = -> Face104
  Symmetric = false
FEATURE [Part::MultiFuse] Fusion081  label="removeToCreateScrewAndThreadedInsertHole040"
  Shapes = -> [Revolve107,Revolve108,Revolve109,Revolve110,Revolve111,Revolve112]
FEATURE [Part::MultiFuse] Fusion082  label="casePillars002"
  Shapes = -> [Revolve094,Revolve092,Revolve090,Revolve089,Revolve091,Revolve093]
FEATURE [Part::Cut] Cut037  label="casePillars003"
  Base = -> Fusion082
  Tool = -> Fusion081
FEATURE [Sketcher::SketchObject] Sketch051
  FullyConstrained = true
  Placement = pos=(117,19,0) rot=(0.57735,0.57735,0.57735;2.0944rad)
  sketch-geometry (48):
    g0: LineSegment StartX=-49.19 StartY=69.25 StartZ=0 EndX=-49.19 EndY=66.25 EndZ=0
    g1: LineSegment StartX=-49.19 StartY=63.5 StartZ=0 EndX=-49.19 EndY=60.5 EndZ=0
    g2: LineSegment StartX=-49.19 StartY=57.75 StartZ=0 EndX=-49.19 EndY=54.75 EndZ=0
    g3: LineSegment StartX=-49.19 StartY=52 StartZ=0 EndX=-49.19 EndY=49 EndZ=0
    g4: LineSegment StartX=-49.19 StartY=46.25 StartZ=0 EndX=-49.19 EndY=43.25 EndZ=0
    g5: LineSegment StartX=-49.19 StartY=40.5 StartZ=0 EndX=-49.19 EndY=37.5 EndZ=0
    g6: LineSegment StartX=-49.19 StartY=34.5 StartZ=0 EndX=-49.19 EndY=31.5 EndZ=0
    g7: LineSegment StartX=-49.19 StartY=28.75 StartZ=0 EndX=-49.19 EndY=25.75 EndZ=0
    g8: LineSegment StartX=-49.19 StartY=23 StartZ=0 EndX=-49.19 EndY=20 EndZ=0
    g9: LineSegment StartX=-49.19 StartY=17.25 StartZ=0 EndX=-49.19 EndY=14.25 EndZ=0
    g10: LineSegment StartX=-49.19 StartY=11.5 StartZ=0 EndX=-49.19 EndY=8.5 EndZ=0
    g11: LineSegment StartX=-49.19 StartY=5.75 StartZ=0 EndX=-49.19 EndY=2.75 EndZ=0
    g12: ArcOfCircle CenterX=-1.5 CenterY=67.75 CenterZ=0 NormalX=0 NormalY=0 NormalZ=1 AngleXU=0 Radius=1.5 StartAngle=4.71239 EndAngle=7.85398
    g13: ArcOfCircle CenterX=-1.5 CenterY=62 CenterZ=0 NormalX=0 NormalY=0 NormalZ=1 AngleXU=0 Radius=1.5 StartAngle=4.71239 EndAngle=7.85398
    g14: ArcOfCircle CenterX=-1.5 CenterY=56.25 CenterZ=0 NormalX=0 NormalY=0 NormalZ=1 AngleXU=0 Radius=1.5 StartAngle=4.71239 EndAngle=7.85398
    g15: ArcOfCircle CenterX=-11.49 CenterY=50.5 CenterZ=0 NormalX=0 NormalY=0 NormalZ=1 AngleXU=0 Radius=1.5 StartAngle=4.71239 EndAngle=7.85398
    g16: ArcOfCircle CenterX=-16.28 CenterY=44.75 CenterZ=0 NormalX=0 NormalY=0 NormalZ=1 AngleXU=0 Radius=1.5 StartAngle=4.71239 EndAngle=7.85398
    g17: ArcOfCircle CenterX=-18.2337 CenterY=39 CenterZ=0 NormalX=0 NormalY=0 NormalZ=1 AngleXU=0 Radius=1.5 StartAngle=4.71485 EndAngle=7.85398
    g18: ArcOfCircle CenterX=-16.2837 CenterY=27.25 CenterZ=0 NormalX=0 NormalY=0 NormalZ=1 AngleXU=0 Radius=1.5 StartAngle=4.71485 EndAngle=7.85398
    g19: ArcOfCircle CenterX=-18.2337 CenterY=33 CenterZ=0 NormalX=0 NormalY=0 NormalZ=1 AngleXU=0 Radius=1.5 StartAngle=4.71485 EndAngle=7.85398
    g20: ArcOfCircle CenterX=-11.49 CenterY=21.5 CenterZ=0 NormalX=0 NormalY=0 NormalZ=1 AngleXU=0 Radius=1.5 StartAngle=4.71239 EndAngle=7.85398
    g21: ArcOfCircle CenterX=-1.5 CenterY=4.25 CenterZ=0 NormalX=0 NormalY=0 NormalZ=1 AngleXU=0 Radius=1.5 StartAngle=4.71239 EndAngle=7.85398
    g22: ArcOfCircle CenterX=-1.5 CenterY=10 CenterZ=0 NormalX=0 NormalY=0 NormalZ=1 AngleXU=0 Radius=1.5 StartAngle=4.71239 EndAngle=7.85398
    g23: ArcOfCircle CenterX=-1.5 CenterY=15.75 CenterZ=0 NormalX=0 NormalY=0 NormalZ=1 AngleXU=0 Radius=1.5 StartAngle=4.71239 EndAngle=7.85398
    g24: LineSegment StartX=-49.19 StartY=69.25 StartZ=0 EndX=-1.5 EndY=69.25 EndZ=0
    g25: LineSegment StartX=-49.19 StartY=66.25 StartZ=0 EndX=-1.5 EndY=66.25 EndZ=0
    g26: LineSegment StartX=-49.19 StartY=63.5 StartZ=0 EndX=-1.5 EndY=63.5 EndZ=0
    g27: LineSegment StartX=-49.19 StartY=60.5 StartZ=0 EndX=-1.5 EndY=60.5 EndZ=0
    g28: LineSegment StartX=-49.19 StartY=57.75 StartZ=0 EndX=-1.5 EndY=57.75 EndZ=0
    g29: LineSegment StartX=-49.19 StartY=54.75 StartZ=0 EndX=-1.5 EndY=54.75 EndZ=0
    g30: LineSegment StartX=-49.19 StartY=52 StartZ=0 EndX=-11.49 EndY=52 EndZ=0
    g31: LineSegment StartX=-49.19 StartY=49 StartZ=0 EndX=-11.49 EndY=49 EndZ=0
    g32: LineSegment StartX=-49.19 StartY=46.25 StartZ=0 EndX=-16.28 EndY=46.25 EndZ=0
    g33: LineSegment StartX=-49.19 StartY=43.25 StartZ=0 EndX=-16.28 EndY=43.25 EndZ=0
    g34: LineSegment StartX=-49.19 StartY=40.5 StartZ=0 EndX=-18.2337 EndY=40.5 EndZ=0
    g35: LineSegment StartX=-49.19 StartY=37.5 StartZ=0 EndX=-18.23 EndY=37.5 EndZ=0
    g36: LineSegment StartX=-49.19 StartY=34.5 StartZ=0 EndX=-18.2337 EndY=34.5 EndZ=0
    g37: LineSegment StartX=-49.19 StartY=31.5 StartZ=0 EndX=-18.23 EndY=31.5 EndZ=0
    g38: LineSegment StartX=-49.19 StartY=28.75 StartZ=0 EndX=-16.2837 EndY=28.75 EndZ=0
    g39: LineSegment StartX=-49.19 StartY=25.75 StartZ=0 EndX=-16.28 EndY=25.75 EndZ=0
    g40: LineSegment StartX=-49.19 StartY=23 StartZ=0 EndX=-11.49 EndY=23 EndZ=0
    g41: LineSegment StartX=-49.19 StartY=20 StartZ=0 EndX=-11.49 EndY=20 EndZ=0
    g42: LineSegment StartX=-49.19 StartY=17.25 StartZ=0 EndX=-1.5 EndY=17.25 EndZ=0
    g43: LineSegment StartX=-49.19 StartY=14.25 StartZ=0 EndX=-1.5 EndY=14.25 EndZ=0
    g44: LineSegment StartX=-49.19 StartY=11.5 StartZ=0 EndX=-1.5 EndY=11.5 EndZ=0
    g45: LineSegment StartX=-49.19 StartY=8.5 StartZ=0 EndX=-1.5 EndY=8.5 EndZ=0
    g46: LineSegment StartX=-49.19 StartY=5.75 StartZ=0 EndX=-1.5 EndY=5.75 EndZ=0
    g47: LineSegment StartX=-49.19 StartY=2.75 StartZ=0 EndX=-1.5 EndY=2.75 EndZ=0
  constraints (120):
    c: Vertical(g0)
    c: Distance(g0) = 3
    c: Block(g0)
    c: Vertical(g1)
    c: Distance(g1) = 3
    c: Vertical(g2)
    c: Equal(g0,g2) = 3
    c: Block(g2)
    c: Vertical(g3)
    c: Equal(g1,g3) = 3
    c: Vertical(g4)
    c: Equal(g0,g4) = 3
    c: Block(g4)
    c: Vertical(g5)
    c: Equal(g1,g5) = 3
    c: Vertical(g6)
    c: Equal(g0,g6) = 3
    c: Block(g6)
    c: Vertical(g7)
    c: Equal(g1,g7) = 3
    c: Vertical(g8)
    c: Equal(g0,g8) = 3
    c: Block(g8)
    c: Vertical(g9)
    c: Equal(g1,g9) = 3
    c: Vertical(g10)
    c: Equal(g0,g10) = 3
    c: Block(g10)
    c: Vertical(g11)
    c: Equal(g1,g11) = 3
    c: Block(g12)
    c: Block(g13)
    c: Block(g14)
    c: Block(g15)
    c: Block(g16)
    c: Block(g17)
    c: Block(g18)
    c: Block(g19)
    c: Block(g20)
    c: Block(g21)
    c: Block(g22)
    c: Block(g23)
    c: Block(g11)
    c: Block(g9)
    c: Block(g7)
    c: Block(g5)
    c: Block(g3)
    c: Block(g1)
    c: Coincident(g24,g0)
    c: Coincident(g24,g12)
    c: Horizontal(g24)
    c: Coincident(g25,g0)
    c: Coincident(g25,g12)
    c: Horizontal(g25)
    c: Coincident(g26,g1)
    c: Coincident(g26,g13)
    c: Horizontal(g26)
    c: Coincident(g27,g1)
    c: Coincident(g27,g13)
    c: Horizontal(g27)
    c: Coincident(g28,g2)
    c: Coincident(g28,g14)
    c: Horizontal(g28)
    c: Coincident(g29,g2)
    c: Coincident(g29,g14)
    c: Horizontal(g29)
    c: Coincident(g30,g3)
    c: Coincident(g30,g15)
    c: Horizontal(g30)
    c: Coincident(g31,g3)
    c: Coincident(g31,g15)
    c: Horizontal(g31)
    c: Coincident(g32,g4)
    c: Coincident(g32,g16)
    c: Horizontal(g32)
    c: Coincident(g33,g4)
    c: Coincident(g33,g16)
    c: Horizontal(g33)
    c: Coincident(g34,g5)
    c: Coincident(g34,g17)
    c: Horizontal(g34)
    c: Coincident(g35,g5)
    c: Coincident(g35,g17)
    c: Horizontal(g35)
    c: Coincident(g36,g6)
    c: Coincident(g36,g19)
    c: Horizontal(g36)
    c: Coincident(g37,g6)
    c: Coincident(g37,g19)
    c: Horizontal(g37)
    c: Coincident(g38,g7)
    c: Coincident(g38,g18)
    c: Horizontal(g38)
    c: Coincident(g39,g7)
    c: Coincident(g39,g18)
    c: Horizontal(g39)
    c: Coincident(g40,g8)
    c: Coincident(g40,g20)
    c: Horizontal(g40)
    c: Coincident(g41,g8)
    c: Coincident(g41,g20)
    c: Horizontal(g41)
    c: Coincident(g42,g9)
    c: Coincident(g42,g23)
    c: Horizontal(g42)
    c: Coincident(g43,g9)
    c: Coincident(g43,g23)
    c: Horizontal(g43)
    c: Coincident(g44,g10)
    c: Coincident(g44,g22)
    c: Horizontal(g44)
    c: Coincident(g45,g10)
    c: Coincident(g45,g22)
    c: Horizontal(g45)
    c: Coincident(g46,g11)
    c: Coincident(g46,g21)
    c: Horizontal(g46)
    c: Coincident(g47,g11)
    c: Coincident(g47,g21)
    c: Horizontal(g47)
FEATURE [Part::Extrusion] Extrude042
  Base = -> Sketch051
  Dir = (1,-2e-16,2e-16)
  DirMode = 2
  FaceMakerClass = Part::FaceMakerBullseye
  LengthFwd = 19
  LengthRev = 0
  Placement = pos=(-19,0,0) rot=(0,0,1;0rad)
  Solid = true
  Symmetric = false
FEATURE [Part::Fillet] Fillet035  label="removeToCreateVentalationHoles"
  Base = -> Extrude042
  Edges = <same value as first occurrence — deduplicated (x6 in doc)>
  Placement = pos=(7,0,0) rot=(0,0,1;0rad)
FEATURE [Part::Cut] Cut038  label="top017"
  Base = -> Cut033
  Tool = -> Fillet035
FEATURE [Sketcher::SketchObject] Sketch052  label="bottomSketch001"
  FullyConstrained = true
  sketch-geometry (45):
    g0: LineSegment StartX=6.29999 StartY=8 StartZ=0 EndX=3.29999 EndY=8 EndZ=0
    g1: LineSegment StartX=3.29999 StartY=8 StartZ=0 EndX=3.29999 EndY=-6.03275e-07 EndZ=0
    g2: ArcOfCircle CenterX=8.29999 CenterY=5 CenterZ=0 NormalX=0 NormalY=0 NormalZ=1 AngleXU=0 Radius=2 StartAngle=3.14159 EndAngle=4.71239
    g3: LineSegment StartX=6.29999 StartY=8 StartZ=0 EndX=6.29999 EndY=5 EndZ=0
    g4: ArcOfCircle CenterX=105 CenterY=19 CenterZ=0 NormalX=0 NormalY=0 NormalZ=1 AngleXU=0 Radius=12.7 StartAngle=4.71239 EndAngle=5.94289
    g5-g11: Circle x7 (B-spline internal-alignment scaffolding for g12; pole/knot coordinates omitted)
    g12: BSplineCurve PolesCount=7 KnotsCount=5 Degree=3 IsPeriodic=0
    g13-g17: GeomPoint x5 (B-spline internal-alignment scaffolding for g12; pole/knot coordinates omitted)
    g18: ArcOfCircle CenterX=105 CenterY=19 CenterZ=0 NormalX=0 NormalY=0 NormalZ=1 AngleXU=0 Radius=15.7 StartAngle=5.81226 EndAngle=6.28319
    g19: BSplineCurve PolesCount=5 KnotsCount=3 Degree=3 IsPeriodic=0
    g20: LineSegment StartX=8.29999 StartY=3 StartZ=0 EndX=101.7 EndY=3 EndZ=0
    g21: LineSegment StartX=3.29999 StartY=-6.03275e-07 StartZ=0 EndX=105 EndY=-6.03275e-07 EndZ=0
    g22: LineSegment StartX=120.974 StartY=8.71251 StartZ=0 EndX=122.332 EndY=7.83778 EndZ=0
    g23: LineSegment StartX=105 StartY=-6.03274e-07 StartZ=0 EndX=113 EndY=-6.03274e-07 EndZ=0
    g24: ArcOfCircle CenterX=105 CenterY=19 CenterZ=0 NormalX=0 NormalY=0 NormalZ=1 AngleXU=0 Radius=20.6155 StartAngle=5.11091 EndAngle=5.71103
    g25: ArcOfCircle CenterX=117.7 CenterY=19 CenterZ=0 NormalX=0 NormalY=0 NormalZ=1 AngleXU=0 Radius=3 StartAngle=1.2e-15 EndAngle=2.10468
    g26: Circle CenterX=116.345 CenterY=16.3232 CenterZ=0 NormalX=0 NormalY=0 NormalZ=1 AngleXU=0 Radius=1
    g27: Circle CenterX=117.24 CenterY=15.7584 CenterZ=0 NormalX=0 NormalY=0 NormalZ=1 AngleXU=0 Radius=1
    g28: Circle CenterX=116.972 CenterY=14.7612 CenterZ=0 NormalX=0 NormalY=0 NormalZ=1 AngleXU=0 Radius=1
    g29: BSplineCurve PolesCount=3 KnotsCount=2 Degree=2 IsPeriodic=0
    g30: GeomPoint X=116.345 Y=16.3232 Z=0
    g31: GeomPoint X=116.972 Y=14.7612 Z=0
    g32: Circle CenterX=115.828 CenterY=17.157 CenterZ=0 NormalX=0 NormalY=0 NormalZ=1 AngleXU=0 Radius=1
    g33: Circle CenterX=115.841 CenterY=16.639 CenterZ=0 NormalX=0 NormalY=0 NormalZ=1 AngleXU=0 Radius=1
    g34: Circle CenterX=116.345 CenterY=16.3232 CenterZ=0 NormalX=0 NormalY=0 NormalZ=1 AngleXU=0 Radius=1
    g35: BSplineCurve PolesCount=3 KnotsCount=2 Degree=2 IsPeriodic=0
    g36: GeomPoint X=115.828 Y=17.157 Z=0
    g37: GeomPoint X=116.345 Y=16.3232 Z=0
    g38: LineSegment StartX=115.828 StartY=17.157 StartZ=0 EndX=115.828 EndY=20.8307 EndZ=0
    g39: Circle CenterX=115.828 CenterY=20.8307 CenterZ=0 NormalX=0 NormalY=0 NormalZ=1 AngleXU=0 Radius=1
    g40: Circle CenterX=115.831 CenterY=21.3396 CenterZ=0 NormalX=0 NormalY=0 NormalZ=1 AngleXU=0 Radius=1
    g41: Circle CenterX=116.173 CenterY=21.5825 CenterZ=0 NormalX=0 NormalY=0 NormalZ=1 AngleXU=0 Radius=1
    g42: BSplineCurve PolesCount=3 KnotsCount=2 Degree=2 IsPeriodic=0
    g43: GeomPoint X=115.828 Y=20.8307 Z=0
    g44: GeomPoint X=116.173 Y=21.5825 Z=0
  constraints (70):
    c: Horizontal(g0)
    c: Distance(g0) = 3
    c: Coincident(g1,g0)
    c: Vertical(g1)
    c: Block(g2)
    c: Block(g0)
    c: Coincident(g3,g0)
    c: Coincident(g3,g2)
    c: Vertical(g3)
    c: Block(g1)
    c: Block(g4)
    c: Coincident(g19,g4)
    c: Block(g19)
    c: Equal(g5, g6-g11) x6
    c: InternalAlignment(g5-g11 -> g12) x7
    c: InternalAlignment(g13-g17 -> g12) x5
    c: Block(g12)
    c: Coincident(g18,g12)
    c: Block(g18)
    c: Coincident(g20,g2)
    c: Coincident(g20,g19)
    c: Horizontal(g20)
    c: Distance(g20) = 93.4
    c: Coincident(g21,g1)
    c: Horizontal(g21)
    c: Distance(g21) = 101.7
    c: Horizontal(g23)
    c: Distance(g23) = 8
    c: Coincident(g24,g23)
    c: Block(g23)
    c: Coincident(g22,g24)
    c: Block(g24)
    c: Block(g22)
    c: Distance(g22) = 1.61553
    c: Coincident(g25,g18)
    c: Block(g25)
    c: Weight(g26) = 1
    c: Equal(g26,g27)
    c: Equal(g26,g28)
    c: Coincident(g29,g4)
    c: InternalAlignment(g26,g29)
    c: InternalAlignment(g27,g29)
    c: InternalAlignment(g28,g29)
    c: InternalAlignment(g30,g29)
    c: InternalAlignment(g31,g29)
    c: Block(g29)
    c: Weight(g32) = 1
    c: Equal(g32,g33)
    c: Equal(g32,g34)
    c: Coincident(g35,g29)
    c: InternalAlignment(g32,g35)
    c: InternalAlignment(g33,g35)
    c: InternalAlignment(g34,g35)
    c: InternalAlignment(g36,g35)
    c: InternalAlignment(g37,g35)
    c: Block(g35)
    c: Coincident(g38,g35)
    c: Vertical(g38)
    c: Block(g38)
    c: Coincident(g42,g38)
    c: Weight(g39) = 1
    c: Equal(g39,g40)
    c: Equal(g39,g41)
    c: Coincident(g42,g25)
    c: InternalAlignment(g39,g42)
    c: InternalAlignment(g40,g42)
    c: InternalAlignment(g41,g42)
    c: InternalAlignment(g43,g42)
    c: InternalAlignment(g44,g42)
    c: Block(g42)
FEATURE [Part::Extrusion] Extrude043  label="bottom010"
  Base = -> Sketch052
  Dir = (0,0,1)
  DirMode = 2
  FaceMakerClass = Part::FaceMakerBullseye
  LengthFwd = 71.4
  LengthRev = 0
  Placement = pos=(0,0,0.3) rot=(0,0,1;0rad)
  Solid = true
  Symmetric = false
FEATURE [Sketcher::SketchObject] Sketch053  label="topSketch013"
  FullyConstrained = true
  sketch-geometry (22):
    g0: LineSegment StartX=5.21097e-06 StartY=3 StartZ=0 EndX=5.21097e-06 EndY=19 EndZ=0
    g1: ArcOfCircle CenterX=19 CenterY=19 CenterZ=0 NormalX=0 NormalY=0 NormalZ=1 AngleXU=0 Radius=19 StartAngle=1.5708 EndAngle=3.14159
    g2: ArcOfCircle CenterX=19 CenterY=19 CenterZ=0 NormalX=0 NormalY=0 NormalZ=1 AngleXU=0 Radius=16 StartAngle=1.5708 EndAngle=3.14159
    g3: LineSegment StartX=114 StartY=35 StartZ=0 EndX=19 EndY=35 EndZ=0
    g4: LineSegment StartX=5.21097e-06 StartY=3 StartZ=0 EndX=5.21097e-06 EndY=0 EndZ=0
    g5: LineSegment StartX=3 StartY=0 StartZ=0 EndX=5.21097e-06 EndY=0 EndZ=0
    g6: LineSegment StartX=3 StartY=19 StartZ=0 EndX=3 EndY=0 EndZ=0
    g7: LineSegment StartX=19 StartY=38 StartZ=0 EndX=124 EndY=38 EndZ=0
    g8: Circle CenterX=119 CenterY=35 CenterZ=0 NormalX=0 NormalY=0 NormalZ=1 AngleXU=0 Radius=1
    g9: Circle CenterX=121 CenterY=35 CenterZ=0 NormalX=0 NormalY=0 NormalZ=1 AngleXU=0 Radius=1
    g10: Circle CenterX=121 CenterY=33 CenterZ=0 NormalX=0 NormalY=0 NormalZ=1 AngleXU=0 Radius=1
    g11: BSplineCurve PolesCount=3 KnotsCount=2 Degree=2 IsPeriodic=0
    g12: GeomPoint X=119 Y=35 Z=0
    g13: GeomPoint X=121 Y=33 Z=0
    g14: LineSegment StartX=119 StartY=35 StartZ=0 EndX=114 EndY=35 EndZ=0
    g15: ArcOfCircle CenterX=105 CenterY=19 CenterZ=0 NormalX=0 NormalY=0 NormalZ=1 AngleXU=0 Radius=16 StartAngle=5.60905 EndAngle=6.28319
    g16: LineSegment StartX=121 StartY=33 StartZ=0 EndX=121 EndY=19 EndZ=0
    g17: LineSegment StartX=117.5 StartY=9.01251 StartZ=0 EndX=121.163 EndY=9.0125 EndZ=0
    g18: ArcOfCircle CenterX=105 CenterY=19 CenterZ=0 NormalX=0 NormalY=0 NormalZ=1 AngleXU=0 Radius=20.6155 StartAngle=5.7297 EndAngle=6.28319
    g19: LineSegment StartX=121.163 StartY=9.0125 StartZ=0 EndX=122.538 EndY=8.16329 EndZ=0
    g20: LineSegment StartX=124 StartY=38 StartZ=0 EndX=125.616 EndY=38 EndZ=0
    g21: LineSegment StartX=125.616 StartY=19 StartZ=0 EndX=125.616 EndY=38 EndZ=0
  constraints (50):
    c: Vertical(g0)
    c: Block(g0)
    c: Coincident(g1,g0)
    c: Block(g1)
    c: Coincident(g2,g1)
    c: Block(g2)
    c: Coincident(g3,g2)
    c: Horizontal(g3)
    c: Tangent(g3,g2)
    c: Coincident(g4,g0)
    c: Distance(g4) = 3
    c: Vertical(g4)
    c: Coincident(g5,g4)
    c: Horizontal(g5)
    c: Coincident(g6,g2)
    c: Coincident(g6,g5)
    c: Vertical(g6)
    c: Horizontal(g7)
    c: Distance(g7) = 105
    c: Coincident(g7,g1)
    c: Block(g3)
    c: Weight(g8) = 1
    c: Equal(g8,g9)
    c: Equal(g8,g10)
    c: InternalAlignment(g8,g11)
    c: InternalAlignment(g9,g11)
    c: InternalAlignment(g10,g11)
    c: InternalAlignment(g12,g11)
    c: InternalAlignment(g13,g11)
    c: Block(g11)
    c: Coincident(g14,g11)
    c: Coincident(g14,g3)
    c: Horizontal(g14)
    c: Block(g15)
    c: Coincident(g16,g11)
    c: Coincident(g16,g15)
    c: Vertical(g16)
    c: Distance(g16) = 14
    c: Coincident(g17,g15)
    c: Block(g18)
    c: Coincident(g19,g18)
    c: Coincident(g20,g7)
    c: Horizontal(g20)
    c: Vertical(g21)
    c: Coincident(g20,g21)
    c: Block(g20)
    c: Block(g21)
    c: Block(g19)
    c: Block(g17)
    c: Distance(g20) = 1.61553
FEATURE [Part::Extrusion] Extrude044
  Base = -> Sketch053
  Dir = (0,0,1)
  DirMode = 2
  FaceMakerClass = Part::FaceMakerBullseye
  LengthFwd = 72
  LengthRev = 0
  Solid = true
  Symmetric = false
FEATURE [Part::Fillet] Fillet036  label="top018"
  Base = -> Extrude044
  Edges = 1 edges r=2: [Edge41]
FEATURE [Sketcher::SketchObject] Sketch054
  FullyConstrained = false
  Placement = pos=(0,0,0) rot=(1,0,0;1.5708rad)
  sketch-geometry (24):
    g0: ArcOfCircle CenterX=-4 CenterY=-10.5 CenterZ=0 NormalX=0 NormalY=0 NormalZ=1 AngleXU=0 Radius=1.5 StartAngle=6e-16 EndAngle=3.14159
    g1: ArcOfCircle CenterX=-34.2 CenterY=-10.5 CenterZ=0 NormalX=0 NormalY=0 NormalZ=1 AngleXU=0 Radius=1.5 StartAngle=0 EndAngle=3.14159
    g2: ArcOfCircle CenterX=-34.2 CenterY=-27.7 CenterZ=0 NormalX=0 NormalY=0 NormalZ=1 AngleXU=0 Radius=1.5 StartAngle=3.14159 EndAngle=6.28319
    g3: ArcOfCircle CenterX=-4 CenterY=-27.7 CenterZ=0 NormalX=0 NormalY=0 NormalZ=1 AngleXU=0 Radius=1.5 StartAngle=3.1416 EndAngle=6.28319
    g4: ArcOfCircle CenterX=-10 CenterY=-4.3 CenterZ=0 NormalX=0 NormalY=0 NormalZ=1 AngleXU=0 Radius=1.5 StartAngle=2e-16 EndAngle=3.14159
    g5: ArcOfCircle CenterX=-16.1 CenterY=-1.8 CenterZ=0 NormalX=0 NormalY=0 NormalZ=1 AngleXU=0 Radius=1.5 StartAngle=5e-16 EndAngle=3.14159
    g6: ArcOfCircle CenterX=-22.1 CenterY=-1.8 CenterZ=0 NormalX=0 NormalY=0 NormalZ=1 AngleXU=0 Radius=1.5 StartAngle=5e-16 EndAngle=3.14159
    g7: ArcOfCircle CenterX=-28.2 CenterY=-4.3 CenterZ=0 NormalX=0 NormalY=0 NormalZ=1 AngleXU=0 Radius=1.5 StartAngle=2e-16 EndAngle=3.14159
    g8: ArcOfCircle CenterX=-10 CenterY=-33.9 CenterZ=0 NormalX=0 NormalY=0 NormalZ=1 AngleXU=0 Radius=1.5 StartAngle=3.14159 EndAngle=6.28319
    g9: ArcOfCircle CenterX=-16.1 CenterY=-36.4 CenterZ=0 NormalX=0 NormalY=0 NormalZ=1 AngleXU=0 Radius=1.5 StartAngle=3.14159 EndAngle=6.28319
    g10: ArcOfCircle CenterX=-22.1 CenterY=-36.4 CenterZ=0 NormalX=0 NormalY=0 NormalZ=1 AngleXU=0 Radius=1.5 StartAngle=3.14159 EndAngle=6.28319
    g11: ArcOfCircle CenterX=-28.2 CenterY=-33.9 CenterZ=0 NormalX=0 NormalY=0 NormalZ=1 AngleXU=0 Radius=1.5 StartAngle=3.14159 EndAngle=6.28319
    g12: LineSegment StartX=-35.7 StartY=-10.5 StartZ=0 EndX=-35.7 EndY=-27.7 EndZ=0
    g13: LineSegment StartX=-32.7 StartY=-10.5 StartZ=0 EndX=-32.7 EndY=-27.7 EndZ=0
    g14: LineSegment StartX=-29.7 StartY=-33.9 StartZ=0 EndX=-29.7 EndY=-4.3 EndZ=0
    g15: LineSegment StartX=-26.7 StartY=-33.9 StartZ=0 EndX=-26.7 EndY=-4.3 EndZ=0
    g16: LineSegment StartX=-2.5 StartY=-10.5 StartZ=0 EndX=-2.5 EndY=-27.7 EndZ=0
    g17: LineSegment StartX=-8.5 StartY=-4.3 StartZ=0 EndX=-8.5 EndY=-33.9 EndZ=0
    g18: LineSegment StartX=-5.5 StartY=-10.5 StartZ=0 EndX=-5.5 EndY=-27.7 EndZ=0
    g19: LineSegment StartX=-11.5 StartY=-4.3 StartZ=0 EndX=-11.5 EndY=-33.9 EndZ=0
    g20: LineSegment StartX=-14.6 StartY=-1.8 StartZ=0 EndX=-14.6 EndY=-36.4 EndZ=0
    g21: LineSegment StartX=-17.6 StartY=-1.8 StartZ=0 EndX=-17.6 EndY=-36.4 EndZ=0
    g22: LineSegment StartX=-20.6 StartY=-36.4 StartZ=0 EndX=-20.6 EndY=-1.8 EndZ=0
    g23: LineSegment StartX=-23.6 StartY=-1.8 StartZ=0 EndX=-23.6 EndY=-36.4 EndZ=0
  constraints (48):
    c: Block(g0)
    c: Block(g1)
    c: Block(g2)
    c: Block(g3)
    c: Block(g4)
    c: Block(g5)
    c: Block(g6)
    c: Block(g7)
    c: Block(g8)
    c: Block(g9)
    c: Block(g10)
    c: Block(g11)
    c: Coincident(g12,g1)
    c: Coincident(g12,g2)
    c: Vertical(g12)
    c: Coincident(g13,g1)
    c: Coincident(g13,g2)
    c: Vertical(g13)
    c: Coincident(g14,g11)
    c: Coincident(g14,g7)
    c: Vertical(g14)
    c: Coincident(g15,g11)
    c: Coincident(g15,g7)
    c: Vertical(g15)
    c: Coincident(g16,g0)
    c: Coincident(g16,g3)
    c: Vertical(g16)
    c: Coincident(g17,g4)
    c: Coincident(g17,g8)
    c: Vertical(g17)
    c: Coincident(g18,g0)
    c: Coincident(g18,g3)
    c: Vertical(g18)
    c: Coincident(g19,g4)
    c: Coincident(g19,g8)
    c: Vertical(g19)
    c: Coincident(g20,g5)
    c: Coincident(g20,g9)
    c: Vertical(g20)
    c: Coincident(g21,g5)
    c: Coincident(g21,g9)
    c: Vertical(g21)
    c: Coincident(g22,g10)
    c: Coincident(g22,g6)
    c: Vertical(g22)
    c: Coincident(g23,g6)
    c: Coincident(g23,g10)
    c: Vertical(g23)
FEATURE [Part::Extrusion] Extrude045  label="removeToCreateFanGrillHoles003"
  Base = -> Sketch054
  Dir = (0,-1,6e-16)
  DirMode = 2
  FaceMakerClass = Part::FaceMakerBullseye
  LengthFwd = 10
  LengthRev = 0
  Placement = pos=(65.4,44,54.82) rot=(0,0,1;0rad)
  Solid = true
  Symmetric = false
FEATURE [Part::Feature] Face105 .. Face108  x4 (patterned run collapsed; names and placements below)
  shape: bbox 3.5 x 17.8 x 2e-07 mm, 1 faces, 0 solids (baked)
FEATURE [Part::Revolution] Revolve113  label="removeToCreateScrewAndThreadedInsertHole041"
  Angle = 360
  Axis = (0,1,0)
  Base = (0,0,0)
  FaceMakerClass = Part::FaceMakerBullseye
  Placement = pos=(62.3,30.3,19.7) rot=(0,0,1;0rad)
  Solid = false
  Source = -> Face105
  Symmetric = false
FEATURE [Part::Revolution] Revolve114  label="removeToCreateScrewAndThreadedInsertHole042"
  Angle = 360
  Axis = (0,1,0)
  Base = (0,0,0)
  FaceMakerClass = Part::FaceMakerBullseye
  Placement = pos=(62.3,30.3,51.7) rot=(0,0,1;0rad)
  Solid = false
  Source = -> Face106
  Symmetric = false
FEATURE [Part::Revolution] Revolve115  label="removeToCreateScrewAndThreadedInsertHole043"
  Angle = 360
  Axis = (0,1,0)
  Base = (0,0,0)
  FaceMakerClass = Part::FaceMakerBullseye
  Placement = pos=(30.3,30.3,19.7) rot=(0,0,1;0rad)
  Solid = false
  Source = -> Face107
  Symmetric = false
FEATURE [Part::Revolution] Revolve116  label="removeToCreateScrewAndThreadedInsertHole044"
  Angle = 360
  Axis = (0,1,0)
  Base = (0,0,0)
  FaceMakerClass = Part::FaceMakerBullseye
  Placement = pos=(30.3,30.3,51.7) rot=(0,0,1;0rad)
  Solid = false
  Source = -> Face108
  Symmetric = false
FEATURE [Part::MultiFuse] Fusion083  label="createThreadedInsertHolesForFan004"
  Shapes = -> [Revolve113,Revolve114,Revolve115,Revolve116]
FEATURE [Part::Box] Box024  label="removeToCreteHoleForPlugHousing026"
  AttacherType = Attacher::AttachEngine3D
  Height = 28.6
  Length = 10
  Placement = pos=(-2,0,21.7) rot=(0,0,1;0rad)
  Width = 19
FEATURE [Part::Cylinder] Cylinder038  label="removeToCreteHoleForPlugHousing027"
  Angle = 360
  AttacherType = Attacher::AttachEngine3D
  Height = 20
  Placement = pos=(-2,19,36) rot=(0,1,0;1.5708rad)
  Radius = 14.3
FEATURE [Part::MultiFuse] Fusion084  label="removeToCreteHoleForPlugHousing028"
  Shapes = -> [Box024,Cylinder038]
FEATURE [Part::Cylinder] Cylinder039
  Angle = 360
  AttacherType = Attacher::AttachEngine3D
  Height = 20
  Placement = pos=(0,0,36.15) rot=(0,0,1;0rad)
  Radius = 14.3
FEATURE [Part::Cylinder] Cylinder040
  Angle = 360
  AttacherType = Attacher::AttachEngine3D
  Height = 10
  Placement = pos=(0,0,36.15) rot=(0,0,1;0rad)
  Radius = 4
FEATURE [Part::Box] Box025  label="removeToCreteHoleForPlugHousing030"
  AttacherType = Attacher::AttachEngine3D
  Height = 28.6
  Length = 20
  Placement = pos=(106.15,0,21.7) rot=(0,0,1;0rad)
  Width = 19
FEATURE [Part::MultiFuse] Fusion086  label="removeToCreteHoleForPlugHousing031"
  Placement = pos=(70,19,36) rot=(0,1,0;1.5708rad)
  Shapes = -> [Cylinder039,Cylinder040]
FEATURE [Part::MultiFuse] Fusion085  label="removeToCreteHoleForPlugHousing029"
  Shapes = -> [Box025,Fusion086]
FEATURE [Sketcher::SketchObject] Sketch055
  FullyConstrained = true
  Placement = pos=(117,19,0) rot=(0.57735,0.57735,0.57735;2.0944rad)
  sketch-geometry (48):
    g0: LineSegment StartX=-49.19 StartY=69.25 StartZ=0 EndX=-49.19 EndY=66.25 EndZ=0
    g1: LineSegment StartX=-49.19 StartY=63.5 StartZ=0 EndX=-49.19 EndY=60.5 EndZ=0
    g2: LineSegment StartX=-49.19 StartY=57.75 StartZ=0 EndX=-49.19 EndY=54.75 EndZ=0
    g3: LineSegment StartX=-49.19 StartY=52 StartZ=0 EndX=-49.19 EndY=49 EndZ=0
    g4: LineSegment StartX=-49.19 StartY=46.25 StartZ=0 EndX=-49.19 EndY=43.25 EndZ=0
    g5: LineSegment StartX=-49.19 StartY=40.5 StartZ=0 EndX=-49.19 EndY=37.5 EndZ=0
    g6: LineSegment StartX=-49.19 StartY=34.5 StartZ=0 EndX=-49.19 EndY=31.5 EndZ=0
    g7: LineSegment StartX=-49.19 StartY=28.75 StartZ=0 EndX=-49.19 EndY=25.75 EndZ=0
    g8: LineSegment StartX=-49.19 StartY=23 StartZ=0 EndX=-49.19 EndY=20 EndZ=0
    g9: LineSegment StartX=-49.19 StartY=17.25 StartZ=0 EndX=-49.19 EndY=14.25 EndZ=0
    g10: LineSegment StartX=-49.19 StartY=11.5 StartZ=0 EndX=-49.19 EndY=8.5 EndZ=0
    g11: LineSegment StartX=-49.19 StartY=5.75 StartZ=0 EndX=-49.19 EndY=2.75 EndZ=0
    g12: ArcOfCircle CenterX=-1.5 CenterY=67.75 CenterZ=0 NormalX=0 NormalY=0 NormalZ=1 AngleXU=0 Radius=1.5 StartAngle=4.71239 EndAngle=7.85398
    g13: ArcOfCircle CenterX=-1.5 CenterY=62 CenterZ=0 NormalX=0 NormalY=0 NormalZ=1 AngleXU=0 Radius=1.5 StartAngle=4.71239 EndAngle=7.85398
    g14: ArcOfCircle CenterX=-1.5 CenterY=56.25 CenterZ=0 NormalX=0 NormalY=0 NormalZ=1 AngleXU=0 Radius=1.5 StartAngle=4.71239 EndAngle=7.85398
    g15: ArcOfCircle CenterX=-11.49 CenterY=50.5 CenterZ=0 NormalX=0 NormalY=0 NormalZ=1 AngleXU=0 Radius=1.5 StartAngle=4.71239 EndAngle=7.85398
    g16: ArcOfCircle CenterX=-16.28 CenterY=44.75 CenterZ=0 NormalX=0 NormalY=0 NormalZ=1 AngleXU=0 Radius=1.5 StartAngle=4.71239 EndAngle=7.85398
    g17: ArcOfCircle CenterX=-18.2337 CenterY=39 CenterZ=0 NormalX=0 NormalY=0 NormalZ=1 AngleXU=0 Radius=1.5 StartAngle=4.71485 EndAngle=7.85398
    g18: ArcOfCircle CenterX=-16.2837 CenterY=27.25 CenterZ=0 NormalX=0 NormalY=0 NormalZ=1 AngleXU=0 Radius=1.5 StartAngle=4.71485 EndAngle=7.85398
    g19: ArcOfCircle CenterX=-18.2337 CenterY=33 CenterZ=0 NormalX=0 NormalY=0 NormalZ=1 AngleXU=0 Radius=1.5 StartAngle=4.71485 EndAngle=7.85398
    g20: ArcOfCircle CenterX=-11.49 CenterY=21.5 CenterZ=0 NormalX=0 NormalY=0 NormalZ=1 AngleXU=0 Radius=1.5 StartAngle=4.71239 EndAngle=7.85398
    g21: ArcOfCircle CenterX=-1.5 CenterY=4.25 CenterZ=0 NormalX=0 NormalY=0 NormalZ=1 AngleXU=0 Radius=1.5 StartAngle=4.71239 EndAngle=7.85398
    g22: ArcOfCircle CenterX=-1.5 CenterY=10 CenterZ=0 NormalX=0 NormalY=0 NormalZ=1 AngleXU=0 Radius=1.5 StartAngle=4.71239 EndAngle=7.85398
    g23: ArcOfCircle CenterX=-1.5 CenterY=15.75 CenterZ=0 NormalX=0 NormalY=0 NormalZ=1 AngleXU=0 Radius=1.5 StartAngle=4.71239 EndAngle=7.85398
    g24: LineSegment StartX=-49.19 StartY=69.25 StartZ=0 EndX=-1.5 EndY=69.25 EndZ=0
    g25: LineSegment StartX=-49.19 StartY=66.25 StartZ=0 EndX=-1.5 EndY=66.25 EndZ=0
    g26: LineSegment StartX=-49.19 StartY=63.5 StartZ=0 EndX=-1.5 EndY=63.5 EndZ=0
    g27: LineSegment StartX=-49.19 StartY=60.5 StartZ=0 EndX=-1.5 EndY=60.5 EndZ=0
    g28: LineSegment StartX=-49.19 StartY=57.75 StartZ=0 EndX=-1.5 EndY=57.75 EndZ=0
    g29: LineSegment StartX=-49.19 StartY=54.75 StartZ=0 EndX=-1.5 EndY=54.75 EndZ=0
    g30: LineSegment StartX=-49.19 StartY=52 StartZ=0 EndX=-11.49 EndY=52 EndZ=0
    g31: LineSegment StartX=-49.19 StartY=49 StartZ=0 EndX=-11.49 EndY=49 EndZ=0
    g32: LineSegment StartX=-49.19 StartY=46.25 StartZ=0 EndX=-16.28 EndY=46.25 EndZ=0
    g33: LineSegment StartX=-49.19 StartY=43.25 StartZ=0 EndX=-16.28 EndY=43.25 EndZ=0
    g34: LineSegment StartX=-49.19 StartY=40.5 StartZ=0 EndX=-18.2337 EndY=40.5 EndZ=0
    g35: LineSegment StartX=-49.19 StartY=37.5 StartZ=0 EndX=-18.23 EndY=37.5 EndZ=0
    g36: LineSegment StartX=-49.19 StartY=34.5 StartZ=0 EndX=-18.2337 EndY=34.5 EndZ=0
    g37: LineSegment StartX=-49.19 StartY=31.5 StartZ=0 EndX=-18.23 EndY=31.5 EndZ=0
    g38: LineSegment StartX=-49.19 StartY=28.75 StartZ=0 EndX=-16.2837 EndY=28.75 EndZ=0
    g39: LineSegment StartX=-49.19 StartY=25.75 StartZ=0 EndX=-16.28 EndY=25.75 EndZ=0
    g40: LineSegment StartX=-49.19 StartY=23 StartZ=0 EndX=-11.49 EndY=23 EndZ=0
    g41: LineSegment StartX=-49.19 StartY=20 StartZ=0 EndX=-11.49 EndY=20 EndZ=0
    g42: LineSegment StartX=-49.19 StartY=17.25 StartZ=0 EndX=-1.5 EndY=17.25 EndZ=0
    g43: LineSegment StartX=-49.19 StartY=14.25 StartZ=0 EndX=-1.5 EndY=14.25 EndZ=0
    g44: LineSegment StartX=-49.19 StartY=11.5 StartZ=0 EndX=-1.5 EndY=11.5 EndZ=0
    g45: LineSegment StartX=-49.19 StartY=8.5 StartZ=0 EndX=-1.5 EndY=8.5 EndZ=0
    g46: LineSegment StartX=-49.19 StartY=5.75 StartZ=0 EndX=-1.5 EndY=5.75 EndZ=0
    g47: LineSegment StartX=-49.19 StartY=2.75 StartZ=0 EndX=-1.5 EndY=2.75 EndZ=0
  constraints (120):
    c: Vertical(g0)
    c: Distance(g0) = 3
    c: Block(g0)
    c: Vertical(g1)
    c: Distance(g1) = 3
    c: Vertical(g2)
    c: Equal(g0,g2) = 3
    c: Block(g2)
    c: Vertical(g3)
    c: Equal(g1,g3) = 3
    c: Vertical(g4)
    c: Equal(g0,g4) = 3
    c: Block(g4)
    c: Vertical(g5)
    c: Equal(g1,g5) = 3
    c: Vertical(g6)
    c: Equal(g0,g6) = 3
    c: Block(g6)
    c: Vertical(g7)
    c: Equal(g1,g7) = 3
    c: Vertical(g8)
    c: Equal(g0,g8) = 3
    c: Block(g8)
    c: Vertical(g9)
    c: Equal(g1,g9) = 3
    c: Vertical(g10)
    c: Equal(g0,g10) = 3
    c: Block(g10)
    c: Vertical(g11)
    c: Equal(g1,g11) = 3
    c: Block(g12)
    c: Block(g13)
    c: Block(g14)
    c: Block(g15)
    c: Block(g16)
    c: Block(g17)
    c: Block(g18)
    c: Block(g19)
    c: Block(g20)
    c: Block(g21)
    c: Block(g22)
    c: Block(g23)
    c: Block(g11)
    c: Block(g9)
    c: Block(g7)
    c: Block(g5)
    c: Block(g3)
    c: Block(g1)
    c: Coincident(g24,g0)
    c: Coincident(g24,g12)
    c: Horizontal(g24)
    c: Coincident(g25,g0)
    c: Coincident(g25,g12)
    c: Horizontal(g25)
    c: Coincident(g26,g1)
    c: Coincident(g26,g13)
    c: Horizontal(g26)
    c: Coincident(g27,g1)
    c: Coincident(g27,g13)
    c: Horizontal(g27)
    c: Coincident(g28,g2)
    c: Coincident(g28,g14)
    c: Horizontal(g28)
    c: Coincident(g29,g2)
    c: Coincident(g29,g14)
    c: Horizontal(g29)
    c: Coincident(g30,g3)
    c: Coincident(g30,g15)
    c: Horizontal(g30)
    c: Coincident(g31,g3)
    c: Coincident(g31,g15)
    c: Horizontal(g31)
    c: Coincident(g32,g4)
    c: Coincident(g32,g16)
    c: Horizontal(g32)
    c: Coincident(g33,g4)
    c: Coincident(g33,g16)
    c: Horizontal(g33)
    c: Coincident(g34,g5)
    c: Coincident(g34,g17)
    c: Horizontal(g34)
    c: Coincident(g35,g5)
    c: Coincident(g35,g17)
    c: Horizontal(g35)
    c: Coincident(g36,g6)
    c: Coincident(g36,g19)
    c: Horizontal(g36)
    c: Coincident(g37,g6)
    c: Coincident(g37,g19)
    c: Horizontal(g37)
    c: Coincident(g38,g7)
    c: Coincident(g38,g18)
    c: Horizontal(g38)
    c: Coincident(g39,g7)
    c: Coincident(g39,g18)
    c: Horizontal(g39)
    c: Coincident(g40,g8)
    c: Coincident(g40,g20)
    c: Horizontal(g40)
    c: Coincident(g41,g8)
    c: Coincident(g41,g20)
    c: Horizontal(g41)
    c: Coincident(g42,g9)
    c: Coincident(g42,g23)
    c: Horizontal(g42)
    c: Coincident(g43,g9)
    c: Coincident(g43,g23)
    c: Horizontal(g43)
    c: Coincident(g44,g10)
    c: Coincident(g44,g22)
    c: Horizontal(g44)
    c: Coincident(g45,g10)
    c: Coincident(g45,g22)
    c: Horizontal(g45)
    c: Coincident(g46,g11)
    c: Coincident(g46,g21)
    c: Horizontal(g46)
    c: Coincident(g47,g11)
    c: Coincident(g47,g21)
    c: Horizontal(g47)
FEATURE [Part::Extrusion] Extrude046
  Base = -> Sketch055
  Dir = (1,0,0)
  DirMode = 2
  FaceMakerClass = Part::FaceMakerBullseye
  LengthFwd = 23
  LengthRev = 0
  Placement = pos=(-19,0,0) rot=(0,0,1;0rad)
  Solid = true
  Symmetric = false
FEATURE [Part::Fillet] Fillet038  label="removeToCreateVentalationHoles001"
  Base = -> Extrude046
  Edges = <same value as first occurrence — deduplicated (x6 in doc)>
  Placement = pos=(7,0,0) rot=(0,0,1;0rad)
FEATURE [Sketcher::SketchObject] Sketch056  label="topSketch014"
  FullyConstrained = true
  sketch-geometry (22):
    g0: LineSegment StartX=5.21097e-06 StartY=3 StartZ=0 EndX=5.21097e-06 EndY=19 EndZ=0
    g1: ArcOfCircle CenterX=19 CenterY=19 CenterZ=0 NormalX=0 NormalY=0 NormalZ=1 AngleXU=0 Radius=19 StartAngle=1.5708 EndAngle=3.14159
    g2: ArcOfCircle CenterX=19 CenterY=19 CenterZ=0 NormalX=0 NormalY=0 NormalZ=1 AngleXU=0 Radius=16 StartAngle=1.5708 EndAngle=3.14159
    g3: LineSegment StartX=114 StartY=35 StartZ=0 EndX=19 EndY=35 EndZ=0
    g4: LineSegment StartX=5.21097e-06 StartY=3 StartZ=0 EndX=5.21097e-06 EndY=0 EndZ=0
    g5: LineSegment StartX=3 StartY=0 StartZ=0 EndX=5.21097e-06 EndY=0 EndZ=0
    g6: LineSegment StartX=3 StartY=19 StartZ=0 EndX=3 EndY=0 EndZ=0
    g7: LineSegment StartX=19 StartY=38 StartZ=0 EndX=124 EndY=38 EndZ=0
    g8: Circle CenterX=119 CenterY=35 CenterZ=0 NormalX=0 NormalY=0 NormalZ=1 AngleXU=0 Radius=1
    g9: Circle CenterX=121 CenterY=35 CenterZ=0 NormalX=0 NormalY=0 NormalZ=1 AngleXU=0 Radius=1
    g10: Circle CenterX=121 CenterY=33 CenterZ=0 NormalX=0 NormalY=0 NormalZ=1 AngleXU=0 Radius=1
    g11: BSplineCurve PolesCount=3 KnotsCount=2 Degree=2 IsPeriodic=0
    g12: GeomPoint X=119 Y=35 Z=0
    g13: GeomPoint X=121 Y=33 Z=0
    g14: LineSegment StartX=119 StartY=35 StartZ=0 EndX=114 EndY=35 EndZ=0
    g15: ArcOfCircle CenterX=105 CenterY=19 CenterZ=0 NormalX=0 NormalY=0 NormalZ=1 AngleXU=0 Radius=16 StartAngle=5.60905 EndAngle=6.28319
    g16: LineSegment StartX=121 StartY=33 StartZ=0 EndX=121 EndY=19 EndZ=0
    g17: LineSegment StartX=117.5 StartY=9.01251 StartZ=0 EndX=121.163 EndY=9.0125 EndZ=0
    g18: ArcOfCircle CenterX=105 CenterY=19 CenterZ=0 NormalX=0 NormalY=0 NormalZ=1 AngleXU=0 Radius=20.6155 StartAngle=5.7297 EndAngle=6.28319
    g19: LineSegment StartX=121.163 StartY=9.0125 StartZ=0 EndX=122.538 EndY=8.16329 EndZ=0
    g20: LineSegment StartX=124 StartY=38 StartZ=0 EndX=125.616 EndY=38 EndZ=0
    g21: LineSegment StartX=125.616 StartY=19 StartZ=0 EndX=125.616 EndY=38 EndZ=0
  constraints (49):
    c: Vertical(g0)
    c: Block(g0)
    c: Coincident(g1,g0)
    c: Block(g1)
    c: Coincident(g2,g1)
    c: Block(g2)
    c: Coincident(g3,g2)
    c: Horizontal(g3)
    c: Tangent(g3,g2)
    c: Coincident(g4,g0)
    c: Distance(g4) = 3
    c: Vertical(g4)
    c: Coincident(g5,g4)
    c: Horizontal(g5)
    c: Coincident(g6,g2)
    c: Coincident(g6,g5)
    c: Vertical(g6)
    c: Horizontal(g7)
    c: Distance(g7) = 105
    c: Coincident(g7,g1)
    c: Block(g3)
    c: Weight(g8) = 1
    c: Equal(g8,g9)
    c: Equal(g8,g10)
    c: InternalAlignment(g8,g11)
    c: InternalAlignment(g9,g11)
    c: InternalAlignment(g10,g11)
    c: InternalAlignment(g12,g11)
    c: InternalAlignment(g13,g11)
    c: Block(g11)
    c: Coincident(g14,g11)
    c: Coincident(g14,g3)
    c: Horizontal(g14)
    c: Block(g15)
    c: Coincident(g16,g11)
    c: Coincident(g16,g15)
    c: Vertical(g16)
    c: Distance(g16) = 14
    c: Coincident(g17,g15)
    c: Block(g18)
    c: Coincident(g19,g18)
    c: Coincident(g20,g7)
    c: Horizontal(g20)
    c: Vertical(g21)
    c: Coincident(g20,g21)
    c: Block(g20)
    c: Block(g21)
    c: Block(g19)
    c: Block(g17)
FEATURE [Part::Box] Box026  label="removeToCreteHoleForPlugHousing032"
  AttacherType = Attacher::AttachEngine3D
  Height = 28.6
  Length = 10
  Placement = pos=(-2,0,21.7) rot=(0,0,1;0rad)
  Width = 19
FEATURE [Part::Feature] Face109 .. Face112  x4 (patterned run collapsed; names and placements below)
  shape: bbox 3.5 x 17.8 x 2e-07 mm, 1 faces, 0 solids (baked)
FEATURE [Part::Revolution] Revolve117  label="removeToCreateScrewAndThreadedInsertHole045"
  Angle = 360
  Axis = (0,1,0)
  Base = (0,0,0)
  FaceMakerClass = Part::FaceMakerBullseye
  Placement = pos=(62.3,30.3,19.7) rot=(0,0,1;0rad)
  Solid = false
  Source = -> Face109
  Symmetric = false
FEATURE [Part::Revolution] Revolve118  label="removeToCreateScrewAndThreadedInsertHole046"
  Angle = 360
  Axis = (0,1,0)
  Base = (0,0,0)
  FaceMakerClass = Part::FaceMakerBullseye
  Placement = pos=(62.3,30.3,51.7) rot=(0,0,1;0rad)
  Solid = false
  Source = -> Face110
  Symmetric = false
FEATURE [Part::Revolution] Revolve119  label="removeToCreateScrewAndThreadedInsertHole047"
  Angle = 360
  Axis = (0,1,0)
  Base = (0,0,0)
  FaceMakerClass = Part::FaceMakerBullseye
  Placement = pos=(30.3,30.3,19.7) rot=(0,0,1;0rad)
  Solid = false
  Source = -> Face111
  Symmetric = false
FEATURE [Part::Revolution] Revolve120  label="removeToCreateScrewAndThreadedInsertHole048"
  Angle = 360
  Axis = (0,1,0)
  Base = (0,0,0)
  FaceMakerClass = Part::FaceMakerBullseye
  Placement = pos=(30.3,30.3,51.7) rot=(0,0,1;0rad)
  Solid = false
  Source = -> Face112
  Symmetric = false
FEATURE [Part::MultiFuse] Fusion087  label="createThreadedInsertHolesForFan005"
  Shapes = -> [Revolve117,Revolve118,Revolve119,Revolve120]
FEATURE [Part::Extrusion] Extrude047
  Base = -> Sketch056
  Dir = (0,0,1)
  DirMode = 2
  FaceMakerClass = Part::FaceMakerBullseye
  LengthFwd = 72
  LengthRev = 0
  Solid = true
  Symmetric = false
FEATURE [Part::Fillet] Fillet039  label="top019"
  Base = -> Extrude047
  Edges = 1 edges r=2: [Edge35]
FEATURE [Sketcher::SketchObject] Sketch057
  FullyConstrained = false
  Placement = pos=(0,0,0) rot=(1,0,0;1.5708rad)
  sketch-geometry (24):
    g0: ArcOfCircle CenterX=-4 CenterY=-10.5 CenterZ=0 NormalX=0 NormalY=0 NormalZ=1 AngleXU=0 Radius=1.5 StartAngle=6e-16 EndAngle=3.14159
    g1: ArcOfCircle CenterX=-34.2 CenterY=-10.5 CenterZ=0 NormalX=0 NormalY=0 NormalZ=1 AngleXU=0 Radius=1.5 StartAngle=0 EndAngle=3.14159
    g2: ArcOfCircle CenterX=-34.2 CenterY=-27.7 CenterZ=0 NormalX=0 NormalY=0 NormalZ=1 AngleXU=0 Radius=1.5 StartAngle=3.14159 EndAngle=6.28319
    g3: ArcOfCircle CenterX=-4 CenterY=-27.7 CenterZ=0 NormalX=0 NormalY=0 NormalZ=1 AngleXU=0 Radius=1.5 StartAngle=3.1416 EndAngle=6.28319
    g4: ArcOfCircle CenterX=-10 CenterY=-4.3 CenterZ=0 NormalX=0 NormalY=0 NormalZ=1 AngleXU=0 Radius=1.5 StartAngle=2e-16 EndAngle=3.14159
    g5: ArcOfCircle CenterX=-16.1 CenterY=-1.8 CenterZ=0 NormalX=0 NormalY=0 NormalZ=1 AngleXU=0 Radius=1.5 StartAngle=5e-16 EndAngle=3.14159
    g6: ArcOfCircle CenterX=-22.1 CenterY=-1.8 CenterZ=0 NormalX=0 NormalY=0 NormalZ=1 AngleXU=0 Radius=1.5 StartAngle=5e-16 EndAngle=3.14159
    g7: ArcOfCircle CenterX=-28.2 CenterY=-4.3 CenterZ=0 NormalX=0 NormalY=0 NormalZ=1 AngleXU=0 Radius=1.5 StartAngle=2e-16 EndAngle=3.14159
    g8: ArcOfCircle CenterX=-10 CenterY=-33.9 CenterZ=0 NormalX=0 NormalY=0 NormalZ=1 AngleXU=0 Radius=1.5 StartAngle=3.14159 EndAngle=6.28319
    g9: ArcOfCircle CenterX=-16.1 CenterY=-36.4 CenterZ=0 NormalX=0 NormalY=0 NormalZ=1 AngleXU=0 Radius=1.5 StartAngle=3.14159 EndAngle=6.28319
    g10: ArcOfCircle CenterX=-22.1 CenterY=-36.4 CenterZ=0 NormalX=0 NormalY=0 NormalZ=1 AngleXU=0 Radius=1.5 StartAngle=3.14159 EndAngle=6.28319
    g11: ArcOfCircle CenterX=-28.2 CenterY=-33.9 CenterZ=0 NormalX=0 NormalY=0 NormalZ=1 AngleXU=0 Radius=1.5 StartAngle=3.14159 EndAngle=6.28319
    g12: LineSegment StartX=-35.7 StartY=-10.5 StartZ=0 EndX=-35.7 EndY=-27.7 EndZ=0
    g13: LineSegment StartX=-32.7 StartY=-10.5 StartZ=0 EndX=-32.7 EndY=-27.7 EndZ=0
    g14: LineSegment StartX=-29.7 StartY=-33.9 StartZ=0 EndX=-29.7 EndY=-4.3 EndZ=0
    g15: LineSegment StartX=-26.7 StartY=-33.9 StartZ=0 EndX=-26.7 EndY=-4.3 EndZ=0
    g16: LineSegment StartX=-2.5 StartY=-10.5 StartZ=0 EndX=-2.5 EndY=-27.7 EndZ=0
    g17: LineSegment StartX=-8.5 StartY=-4.3 StartZ=0 EndX=-8.5 EndY=-33.9 EndZ=0
    g18: LineSegment StartX=-5.5 StartY=-10.5 StartZ=0 EndX=-5.5 EndY=-27.7 EndZ=0
    g19: LineSegment StartX=-11.5 StartY=-4.3 StartZ=0 EndX=-11.5 EndY=-33.9 EndZ=0
    g20: LineSegment StartX=-14.6 StartY=-1.8 StartZ=0 EndX=-14.6 EndY=-36.4 EndZ=0
    g21: LineSegment StartX=-17.6 StartY=-1.8 StartZ=0 EndX=-17.6 EndY=-36.4 EndZ=0
    g22: LineSegment StartX=-20.6 StartY=-36.4 StartZ=0 EndX=-20.6 EndY=-1.8 EndZ=0
    g23: LineSegment StartX=-23.6 StartY=-1.8 StartZ=0 EndX=-23.6 EndY=-36.4 EndZ=0
  constraints (48):
    c: Block(g0)
    c: Block(g1)
    c: Block(g2)
    c: Block(g3)
    c: Block(g4)
    c: Block(g5)
    c: Block(g6)
    c: Block(g7)
    c: Block(g8)
    c: Block(g9)
    c: Block(g10)
    c: Block(g11)
    c: Coincident(g12,g1)
    c: Coincident(g12,g2)
    c: Vertical(g12)
    c: Coincident(g13,g1)
    c: Coincident(g13,g2)
    c: Vertical(g13)
    c: Coincident(g14,g11)
    c: Coincident(g14,g7)
    c: Vertical(g14)
    c: Coincident(g15,g11)
    c: Coincident(g15,g7)
    c: Vertical(g15)
    c: Coincident(g16,g0)
    c: Coincident(g16,g3)
    c: Vertical(g16)
    c: Coincident(g17,g4)
    c: Coincident(g17,g8)
    c: Vertical(g17)
    c: Coincident(g18,g0)
    c: Coincident(g18,g3)
    c: Vertical(g18)
    c: Coincident(g19,g4)
    c: Coincident(g19,g8)
    c: Vertical(g19)
    c: Coincident(g20,g5)
    c: Coincident(g20,g9)
    c: Vertical(g20)
    c: Coincident(g21,g5)
    c: Coincident(g21,g9)
    c: Vertical(g21)
    c: Coincident(g22,g10)
    c: Coincident(g22,g6)
    c: Vertical(g22)
    c: Coincident(g23,g6)
    c: Coincident(g23,g10)
    c: Vertical(g23)
FEATURE [Part::Extrusion] Extrude048  label="removeToCreateFanGrillHoles004"
  Base = -> Sketch057
  Dir = (0,-1,6e-16)
  DirMode = 2
  FaceMakerClass = Part::FaceMakerBullseye
  LengthFwd = 10
  LengthRev = 0
  Placement = pos=(65.4,44,54.82) rot=(0,0,1;0rad)
  Solid = true
  Symmetric = false
FEATURE [Part::Cut] Cut040  label="top021"
  Base = -> Fillet039
  Tool = -> Extrude048
FEATURE [Part::Cylinder] Cylinder041  label="removeToCreteHoleForPlugHousing034"
  Angle = 360
  AttacherType = Attacher::AttachEngine3D
  Height = 20
  Placement = pos=(-2,19,36) rot=(0,1,0;1.5708rad)
  Radius = 14.3
FEATURE [Part::MultiFuse] Fusion089  label="removeToCreteHoleForPlugHousing035"
  Shapes = -> [Box026,Cylinder041]
FEATURE [Part::Cylinder] Cylinder042
  Angle = 360
  AttacherType = Attacher::AttachEngine3D
  Height = 20
  Placement = pos=(0,0,36.15) rot=(0,0,1;0rad)
  Radius = 14.3
FEATURE [Part::Cylinder] Cylinder043
  Angle = 360
  AttacherType = Attacher::AttachEngine3D
  Height = 10
  Placement = pos=(0,0,36.15) rot=(0,0,1;0rad)
  Radius = 4
FEATURE [Part::Box] Box027  label="removeToCreteHoleForPlugHousing036"
  AttacherType = Attacher::AttachEngine3D
  Height = 28.6
  Length = 20
  Placement = pos=(106.15,0,21.7) rot=(0,0,1;0rad)
  Width = 19
FEATURE [Part::Cut] Cut041  label="top022"
  Base = -> Cut040
  Tool = -> Fusion087
FEATURE [Part::Cut] Cut039  label="top020"
  Base = -> Cut041
  Tool = -> Fusion089
FEATURE [Part::MultiFuse] Fusion090  label="removeToCreteHoleForPlugHousing037"
  Placement = pos=(70,19,36) rot=(0,1,0;1.5708rad)
  Shapes = -> [Cylinder042,Cylinder043]
FEATURE [Part::MultiFuse] Fusion088  label="removeToCreteHoleForPlugHousing033"
  Shapes = -> [Box027,Fusion090]
FEATURE [Part::Cut] Cut042  label="removeToCreteHoleForPlugHousing038"
  Base = -> Cut039
  Tool = -> Fusion088
FEATURE [Part::MultiFuse] Fusion091  label="removeFromTop"
  Shapes = -> [Fillet038,Fusion085,Fusion084,Fusion083,Extrude045]
FEATURE [Part::Cut] Cut043  label="REAL TOP ====="
  Base = -> Fillet036
  Tool = -> Fusion091
FEATURE [Part::MultiFuse] Fusion092  label="caseScrewPillarBracket016"
  Shapes = -> [Extrude030,Extrude031,Extrude032,Extrude033,Extrude034,Extrude035,Extrude036,Extrude037,Box013,Box014]
FEATURE [Sketcher::SketchObject] Sketch058  label="topSketch015"
  FullyConstrained = true
  sketch-geometry (20):
    g0: LineSegment StartX=5.21097e-06 StartY=3 StartZ=0 EndX=5.21097e-06 EndY=19 EndZ=0
    g1: ArcOfCircle CenterX=19 CenterY=19 CenterZ=0 NormalX=0 NormalY=0 NormalZ=1 AngleXU=0 Radius=19 StartAngle=1.5708 EndAngle=3.14159
    g2: ArcOfCircle CenterX=19 CenterY=19 CenterZ=0 NormalX=0 NormalY=0 NormalZ=1 AngleXU=0 Radius=16 StartAngle=1.5708 EndAngle=3.14159
    g3: LineSegment StartX=114 StartY=35 StartZ=0 EndX=19 EndY=35 EndZ=0
    g4: LineSegment StartX=5.21097e-06 StartY=3 StartZ=0 EndX=5.21097e-06 EndY=0 EndZ=0
    g5: LineSegment StartX=3 StartY=0 StartZ=0 EndX=5.21097e-06 EndY=0 EndZ=0
    g6: LineSegment StartX=3 StartY=19 StartZ=0 EndX=3 EndY=0 EndZ=0
    g7: LineSegment StartX=19 StartY=38 StartZ=0 EndX=124 EndY=38 EndZ=0
    g8: Circle CenterX=119 CenterY=35 CenterZ=0 NormalX=0 NormalY=0 NormalZ=1 AngleXU=0 Radius=1
    g9: Circle CenterX=121 CenterY=35 CenterZ=0 NormalX=0 NormalY=0 NormalZ=1 AngleXU=0 Radius=1
    g10: Circle CenterX=121 CenterY=33 CenterZ=0 NormalX=0 NormalY=0 NormalZ=1 AngleXU=0 Radius=1
    g11: BSplineCurve PolesCount=3 KnotsCount=2 Degree=2 IsPeriodic=0
    g12: GeomPoint X=119 Y=35 Z=0
    g13: GeomPoint X=121 Y=33 Z=0
    g14: LineSegment StartX=119 StartY=35 StartZ=0 EndX=114 EndY=35 EndZ=0
    g15: ArcOfCircle CenterX=105 CenterY=19 CenterZ=0 NormalX=0 NormalY=0 NormalZ=1 AngleXU=0 Radius=19 StartAngle=5.7297 EndAngle=6.28319
    g16: ArcOfCircle CenterX=105 CenterY=19 CenterZ=0 NormalX=0 NormalY=0 NormalZ=1 AngleXU=0 Radius=16 StartAngle=5.60905 EndAngle=6.28319
    g17: LineSegment StartX=121 StartY=33 StartZ=0 EndX=121 EndY=19 EndZ=0
    g18: LineSegment StartX=124 StartY=38 StartZ=0 EndX=124 EndY=19 EndZ=0
    g19: LineSegment StartX=117.5 StartY=9.01251 StartZ=0 EndX=121.163 EndY=9.0125 EndZ=0
  constraints (46):
    c: Vertical(g0)
    c: Block(g0)
    c: Coincident(g1,g0)
    c: Block(g1)
    c: Coincident(g2,g1)
    c: Block(g2)
    c: Coincident(g3,g2)
    c: Horizontal(g3)
    c: Tangent(g3,g2)
    c: Coincident(g4,g0)
    c: Distance(g4) = 3
    c: Vertical(g4)
    c: Coincident(g5,g4)
    c: Horizontal(g5)
    c: Coincident(g6,g2)
    c: Coincident(g6,g5)
    c: Vertical(g6)
    c: Horizontal(g7)
    c: Distance(g7) = 105
    c: Coincident(g7,g1)
    c: Block(g3)
    c: Weight(g8) = 1
    c: Equal(g8,g9)
    c: Equal(g8,g10)
    c: InternalAlignment(g8,g11)
    c: InternalAlignment(g9,g11)
    c: InternalAlignment(g10,g11)
    c: InternalAlignment(g12,g11)
    c: InternalAlignment(g13,g11)
    c: Block(g11)
    c: Coincident(g14,g11)
    c: Coincident(g14,g3)
    c: Horizontal(g14)
    c: Block(g15)
    c: Coincident(g16,g15)
    c: Block(g16)
    c: Coincident(g17,g11)
    c: Coincident(g17,g16)
    c: Vertical(g17)
    c: Distance(g17) = 14
    c: Coincident(g18,g7)
    c: Coincident(g18,g15)
    c: Vertical(g18)
    c: Distance(g18) = 19
    c: Coincident(g19,g16)
    c: Coincident(g19,g15)
FEATURE [Part::Extrusion] Extrude049  label="top023"
  Base = -> Sketch058
  Dir = (0,0,1)
  DirMode = 2
  FaceMakerClass = Part::FaceMakerBullseye
  LengthFwd = 72
  LengthRev = 0
  Solid = true
  Symmetric = false
FEATURE [Sketcher::SketchObject] Sketch059
  FullyConstrained = true
  MapMode = 3
  Placement = pos=(0,0,0) rot=(1,0,0;1.5708rad)
  Support = -> [Extrude049]
  sketch-geometry (8):
    g0: Circle CenterX=80.351 CenterY=-67.6202 CenterZ=0 NormalX=0 NormalY=0 NormalZ=1 AngleXU=0 Radius=2
    g1: Circle CenterX=80.351 CenterY=-67.6202 CenterZ=0 NormalX=0 NormalY=0 NormalZ=1 AngleXU=0 Radius=3
    g2: Circle CenterX=80.351 CenterY=-4.92017 CenterZ=0 NormalX=0 NormalY=0 NormalZ=1 AngleXU=0 Radius=2
    g3: Circle CenterX=80.351 CenterY=-4.92017 CenterZ=0 NormalX=0 NormalY=0 NormalZ=1 AngleXU=0 Radius=3
    g4: Circle CenterX=23.851 CenterY=-4.92017 CenterZ=0 NormalX=0 NormalY=0 NormalZ=1 AngleXU=0 Radius=2
    g5: Circle CenterX=23.851 CenterY=-4.92017 CenterZ=0 NormalX=0 NormalY=0 NormalZ=1 AngleXU=0 Radius=3
    g6: Circle CenterX=23.851 CenterY=-67.6202 CenterZ=0 NormalX=0 NormalY=0 NormalZ=1 AngleXU=0 Radius=2
    g7: Circle CenterX=23.851 CenterY=-67.6202 CenterZ=0 NormalX=0 NormalY=0 NormalZ=1 AngleXU=0 Radius=3
  constraints (8):
    c: Block(g3)
    c: Block(g2)
    c: Block(g1)
    c: Block(g0)
    c: Block(g6)
    c: Block(g7)
    c: Block(g4)
    c: Block(g5)
FEATURE [Sketcher::SketchObject] Sketch060
  FullyConstrained = true
  MapMode = 3
  Placement = pos=(0,0,0) rot=(1,0,0;1.5708rad)
  Support = -> [Extrude049]
  sketch-geometry (8):
    g0: Circle CenterX=80.351 CenterY=-67.6202 CenterZ=0 NormalX=0 NormalY=0 NormalZ=1 AngleXU=0 Radius=3
    g1: Circle CenterX=80.351 CenterY=-4.92017 CenterZ=0 NormalX=0 NormalY=0 NormalZ=1 AngleXU=0 Radius=3
    g2: Circle CenterX=23.851 CenterY=-4.92017 CenterZ=0 NormalX=0 NormalY=0 NormalZ=1 AngleXU=0 Radius=3
    g3: Circle CenterX=23.851 CenterY=-67.6202 CenterZ=0 NormalX=0 NormalY=0 NormalZ=1 AngleXU=0 Radius=3
    g4: Circle CenterX=23.851 CenterY=-67.6202 CenterZ=0 NormalX=0 NormalY=0 NormalZ=1 AngleXU=0 Radius=5
    g5: Circle CenterX=80.351 CenterY=-67.6202 CenterZ=0 NormalX=0 NormalY=0 NormalZ=1 AngleXU=0 Radius=5
    g6: Circle CenterX=23.851 CenterY=-4.92017 CenterZ=0 NormalX=0 NormalY=0 NormalZ=1 AngleXU=0 Radius=5
    g7: Circle CenterX=80.351 CenterY=-4.92017 CenterZ=0 NormalX=0 NormalY=0 NormalZ=1 AngleXU=0 Radius=5
  constraints (8):
    c: Block(g1)
    c: Block(g0)
    c: Block(g3)
    c: Block(g2)
    c: Block(g5)
    c: Block(g4)
    c: Block(g6)
    c: Block(g7)
FEATURE [Sketcher::SketchObject] Sketch061
  FullyConstrained = true
  MapMode = 3
  Placement = pos=(0,0,0) rot=(1,0,0;1.5708rad)
  sketch-geometry (8):
    g0: Circle CenterX=80.351 CenterY=-67.6202 CenterZ=0 NormalX=0 NormalY=0 NormalZ=1 AngleXU=0 Radius=3
    g1: Circle CenterX=80.351 CenterY=-4.92017 CenterZ=0 NormalX=0 NormalY=0 NormalZ=1 AngleXU=0 Radius=3
    g2: Circle CenterX=23.851 CenterY=-4.92017 CenterZ=0 NormalX=0 NormalY=0 NormalZ=1 AngleXU=0 Radius=3
    g3: Circle CenterX=23.851 CenterY=-67.6202 CenterZ=0 NormalX=0 NormalY=0 NormalZ=1 AngleXU=0 Radius=3
    g4: Circle CenterX=23.851 CenterY=-67.6202 CenterZ=0 NormalX=0 NormalY=0 NormalZ=1 AngleXU=0 Radius=5
    g5: Circle CenterX=80.351 CenterY=-67.6202 CenterZ=0 NormalX=0 NormalY=0 NormalZ=1 AngleXU=0 Radius=5
    g6: Circle CenterX=23.851 CenterY=-4.92017 CenterZ=0 NormalX=0 NormalY=0 NormalZ=1 AngleXU=0 Radius=5
    g7: Circle CenterX=80.351 CenterY=-4.92017 CenterZ=0 NormalX=0 NormalY=0 NormalZ=1 AngleXU=0 Radius=5
  constraints (8):
    c: Block(g1)
    c: Block(g0)
    c: Block(g3)
    c: Block(g2)
    c: Block(g5)
    c: Block(g4)
    c: Block(g6)
    c: Block(g7)
FEATURE [Sketcher::SketchObject] Sketch062  label="topSketch016"
  FullyConstrained = true
  sketch-geometry (20):
    g0: LineSegment StartX=5.21097e-06 StartY=3 StartZ=0 EndX=5.21097e-06 EndY=19 EndZ=0
    g1: ArcOfCircle CenterX=19 CenterY=19 CenterZ=0 NormalX=0 NormalY=0 NormalZ=1 AngleXU=0 Radius=19 StartAngle=1.5708 EndAngle=3.14159
    g2: ArcOfCircle CenterX=19 CenterY=19 CenterZ=0 NormalX=0 NormalY=0 NormalZ=1 AngleXU=0 Radius=16 StartAngle=1.5708 EndAngle=3.14159
    g3: LineSegment StartX=114 StartY=35 StartZ=0 EndX=19 EndY=35 EndZ=0
    g4: LineSegment StartX=5.21097e-06 StartY=3 StartZ=0 EndX=5.21097e-06 EndY=0 EndZ=0
    g5: LineSegment StartX=3 StartY=0 StartZ=0 EndX=5.21097e-06 EndY=0 EndZ=0
    g6: LineSegment StartX=3 StartY=19 StartZ=0 EndX=3 EndY=0 EndZ=0
    g7: LineSegment StartX=19 StartY=38 StartZ=0 EndX=124 EndY=38 EndZ=0
    g8: Circle CenterX=119 CenterY=35 CenterZ=0 NormalX=0 NormalY=0 NormalZ=1 AngleXU=0 Radius=1
    g9: Circle CenterX=121 CenterY=35 CenterZ=0 NormalX=0 NormalY=0 NormalZ=1 AngleXU=0 Radius=1
    g10: Circle CenterX=121 CenterY=33 CenterZ=0 NormalX=0 NormalY=0 NormalZ=1 AngleXU=0 Radius=1
    g11: BSplineCurve PolesCount=3 KnotsCount=2 Degree=2 IsPeriodic=0
    g12: GeomPoint X=119 Y=35 Z=0
    g13: GeomPoint X=121 Y=33 Z=0
    g14: LineSegment StartX=119 StartY=35 StartZ=0 EndX=114 EndY=35 EndZ=0
    g15: ArcOfCircle CenterX=105 CenterY=19 CenterZ=0 NormalX=0 NormalY=0 NormalZ=1 AngleXU=0 Radius=19 StartAngle=5.7297 EndAngle=6.28319
    g16: ArcOfCircle CenterX=105 CenterY=19 CenterZ=0 NormalX=0 NormalY=0 NormalZ=1 AngleXU=0 Radius=16 StartAngle=5.60905 EndAngle=6.28319
    g17: LineSegment StartX=121 StartY=33 StartZ=0 EndX=121 EndY=19 EndZ=0
    g18: LineSegment StartX=124 StartY=38 StartZ=0 EndX=124 EndY=19 EndZ=0
    g19: LineSegment StartX=117.5 StartY=9.01251 StartZ=0 EndX=121.163 EndY=9.0125 EndZ=0
  constraints (46):
    c: Vertical(g0)
    c: Block(g0)
    c: Coincident(g1,g0)
    c: Block(g1)
    c: Coincident(g2,g1)
    c: Block(g2)
    c: Coincident(g3,g2)
    c: Horizontal(g3)
    c: Tangent(g3,g2)
    c: Coincident(g4,g0)
    c: Distance(g4) = 3
    c: Vertical(g4)
    c: Coincident(g5,g4)
    c: Horizontal(g5)
    c: Coincident(g6,g2)
    c: Coincident(g6,g5)
    c: Vertical(g6)
    c: Horizontal(g7)
    c: Distance(g7) = 105
    c: Coincident(g7,g1)
    c: Block(g3)
    c: Weight(g8) = 1
    c: Equal(g8,g9)
    c: Equal(g8,g10)
    c: InternalAlignment(g8,g11)
    c: InternalAlignment(g9,g11)
    c: InternalAlignment(g10,g11)
    c: InternalAlignment(g12,g11)
    c: InternalAlignment(g13,g11)
    c: Block(g11)
    c: Coincident(g14,g11)
    c: Coincident(g14,g3)
    c: Horizontal(g14)
    c: Block(g15)
    c: Coincident(g16,g15)
    c: Block(g16)
    c: Coincident(g17,g11)
    c: Coincident(g17,g16)
    c: Vertical(g17)
    c: Distance(g17) = 14
    c: Coincident(g18,g7)
    c: Coincident(g18,g15)
    c: Vertical(g18)
    c: Distance(g18) = 19
    c: Coincident(g19,g16)
    c: Coincident(g19,g15)
FEATURE [Part::Extrusion] Extrude053  label="top024"
  Base = -> Sketch062
  Dir = (0,0,1)
  DirMode = 2
  FaceMakerClass = Part::FaceMakerBullseye
  LengthFwd = 72
  LengthRev = 0
  Solid = true
  Symmetric = false
FEATURE [Sketcher::SketchObject] Sketch063
  FullyConstrained = true
  MapMode = 3
  Placement = pos=(0,0,0) rot=(1,0,0;1.5708rad)
  Support = -> [Extrude053]
  sketch-geometry (8):
    g0: Circle CenterX=80.351 CenterY=-67.6202 CenterZ=0 NormalX=0 NormalY=0 NormalZ=1 AngleXU=0 Radius=2
    g1: Circle CenterX=80.351 CenterY=-67.6202 CenterZ=0 NormalX=0 NormalY=0 NormalZ=1 AngleXU=0 Radius=3
    g2: Circle CenterX=80.351 CenterY=-4.92017 CenterZ=0 NormalX=0 NormalY=0 NormalZ=1 AngleXU=0 Radius=2
    g3: Circle CenterX=80.351 CenterY=-4.92017 CenterZ=0 NormalX=0 NormalY=0 NormalZ=1 AngleXU=0 Radius=3
    g4: Circle CenterX=23.851 CenterY=-4.92017 CenterZ=0 NormalX=0 NormalY=0 NormalZ=1 AngleXU=0 Radius=2
    g5: Circle CenterX=23.851 CenterY=-4.92017 CenterZ=0 NormalX=0 NormalY=0 NormalZ=1 AngleXU=0 Radius=3
    g6: Circle CenterX=23.851 CenterY=-67.6202 CenterZ=0 NormalX=0 NormalY=0 NormalZ=1 AngleXU=0 Radius=2
    g7: Circle CenterX=23.851 CenterY=-67.6202 CenterZ=0 NormalX=0 NormalY=0 NormalZ=1 AngleXU=0 Radius=3
  constraints (8):
    c: Block(g3)
    c: Block(g2)
    c: Block(g1)
    c: Block(g0)
    c: Block(g6)
    c: Block(g7)
    c: Block(g4)
    c: Block(g5)
FEATURE [Part::Extrusion] Extrude054
  Base = -> Sketch063
  Dir = (0,-1,2e-16)
  DirMode = 2
  FaceMakerClass = Part::FaceMakerBullseye
  LengthFwd = 6
  LengthRev = 0
  Placement = pos=(0,9,0) rot=(0,0,1;0rad)
  Solid = true
  Symmetric = false
FEATURE [Sketcher::SketchObject] Sketch064  label="topSketch017"
  FullyConstrained = true
  sketch-geometry (20):
    g0: LineSegment StartX=5.21097e-06 StartY=3 StartZ=0 EndX=5.21097e-06 EndY=19 EndZ=0
    g1: ArcOfCircle CenterX=19 CenterY=19 CenterZ=0 NormalX=0 NormalY=0 NormalZ=1 AngleXU=0 Radius=19 StartAngle=1.5708 EndAngle=3.14159
    g2: ArcOfCircle CenterX=19 CenterY=19 CenterZ=0 NormalX=0 NormalY=0 NormalZ=1 AngleXU=0 Radius=16 StartAngle=1.5708 EndAngle=3.14159
    g3: LineSegment StartX=114 StartY=35 StartZ=0 EndX=19 EndY=35 EndZ=0
    g4: LineSegment StartX=5.21097e-06 StartY=3 StartZ=0 EndX=5.21097e-06 EndY=0 EndZ=0
    g5: LineSegment StartX=3 StartY=0 StartZ=0 EndX=5.21097e-06 EndY=0 EndZ=0
    g6: LineSegment StartX=3 StartY=19 StartZ=0 EndX=3 EndY=0 EndZ=0
    g7: LineSegment StartX=19 StartY=38 StartZ=0 EndX=124 EndY=38 EndZ=0
    g8: Circle CenterX=119 CenterY=35 CenterZ=0 NormalX=0 NormalY=0 NormalZ=1 AngleXU=0 Radius=1
    g9: Circle CenterX=121 CenterY=35 CenterZ=0 NormalX=0 NormalY=0 NormalZ=1 AngleXU=0 Radius=1
    g10: Circle CenterX=121 CenterY=33 CenterZ=0 NormalX=0 NormalY=0 NormalZ=1 AngleXU=0 Radius=1
    g11: BSplineCurve PolesCount=3 KnotsCount=2 Degree=2 IsPeriodic=0
    g12: GeomPoint X=119 Y=35 Z=0
    g13: GeomPoint X=121 Y=33 Z=0
    g14: LineSegment StartX=119 StartY=35 StartZ=0 EndX=114 EndY=35 EndZ=0
    g15: ArcOfCircle CenterX=105 CenterY=19 CenterZ=0 NormalX=0 NormalY=0 NormalZ=1 AngleXU=0 Radius=19 StartAngle=5.7297 EndAngle=6.28319
    g16: ArcOfCircle CenterX=105 CenterY=19 CenterZ=0 NormalX=0 NormalY=0 NormalZ=1 AngleXU=0 Radius=16 StartAngle=5.60905 EndAngle=6.28319
    g17: LineSegment StartX=121 StartY=33 StartZ=0 EndX=121 EndY=19 EndZ=0
    g18: LineSegment StartX=124 StartY=38 StartZ=0 EndX=124 EndY=19 EndZ=0
    g19: LineSegment StartX=117.5 StartY=9.01251 StartZ=0 EndX=121.163 EndY=9.0125 EndZ=0
  constraints (46):
    c: Vertical(g0)
    c: Block(g0)
    c: Coincident(g1,g0)
    c: Block(g1)
    c: Coincident(g2,g1)
    c: Block(g2)
    c: Coincident(g3,g2)
    c: Horizontal(g3)
    c: Tangent(g3,g2)
    c: Coincident(g4,g0)
    c: Distance(g4) = 3
    c: Vertical(g4)
    c: Coincident(g5,g4)
    c: Horizontal(g5)
    c: Coincident(g6,g2)
    c: Coincident(g6,g5)
    c: Vertical(g6)
    c: Horizontal(g7)
    c: Distance(g7) = 105
    c: Coincident(g7,g1)
    c: Block(g3)
    c: Weight(g8) = 1
    c: Equal(g8,g9)
    c: Equal(g8,g10)
    c: InternalAlignment(g8,g11)
    c: InternalAlignment(g9,g11)
    c: InternalAlignment(g10,g11)
    c: InternalAlignment(g12,g11)
    c: InternalAlignment(g13,g11)
    c: Block(g11)
    c: Coincident(g14,g11)
    c: Coincident(g14,g3)
    c: Horizontal(g14)
    c: Block(g15)
    c: Coincident(g16,g15)
    c: Block(g16)
    c: Coincident(g17,g11)
    c: Coincident(g17,g16)
    c: Vertical(g17)
    c: Distance(g17) = 14
    c: Coincident(g18,g7)
    c: Coincident(g18,g15)
    c: Vertical(g18)
    c: Distance(g18) = 19
    c: Coincident(g19,g16)
    c: Coincident(g19,g15)
FEATURE [Sketcher::SketchObject] Sketch065
  FullyConstrained = true
  MapMode = 3
  Placement = pos=(0,0,0) rot=(1,0,0;1.5708rad)
  sketch-geometry (8):
    g0: Circle CenterX=80.351 CenterY=-67.6202 CenterZ=0 NormalX=0 NormalY=0 NormalZ=1 AngleXU=0 Radius=3
    g1: Circle CenterX=80.351 CenterY=-4.92017 CenterZ=0 NormalX=0 NormalY=0 NormalZ=1 AngleXU=0 Radius=3
    g2: Circle CenterX=23.851 CenterY=-4.92017 CenterZ=0 NormalX=0 NormalY=0 NormalZ=1 AngleXU=0 Radius=3
    g3: Circle CenterX=23.851 CenterY=-67.6202 CenterZ=0 NormalX=0 NormalY=0 NormalZ=1 AngleXU=0 Radius=3
    g4: Circle CenterX=23.851 CenterY=-67.6202 CenterZ=0 NormalX=0 NormalY=0 NormalZ=1 AngleXU=0 Radius=5
    g5: Circle CenterX=80.351 CenterY=-67.6202 CenterZ=0 NormalX=0 NormalY=0 NormalZ=1 AngleXU=0 Radius=5
    g6: Circle CenterX=23.851 CenterY=-4.92017 CenterZ=0 NormalX=0 NormalY=0 NormalZ=1 AngleXU=0 Radius=5
    g7: Circle CenterX=80.351 CenterY=-4.92017 CenterZ=0 NormalX=0 NormalY=0 NormalZ=1 AngleXU=0 Radius=5
  constraints (8):
    c: Block(g1)
    c: Block(g0)
    c: Block(g3)
    c: Block(g2)
    c: Block(g5)
    c: Block(g4)
    c: Block(g6)
    c: Block(g7)
FEATURE [Part::Extrusion] Extrude056
  Base = -> Sketch065
  Dir = (0,-1,2e-16)
  DirMode = 2
  FaceMakerClass = Part::FaceMakerBullseye
  LengthFwd = 2
  LengthRev = 0
  Solid = true
  Symmetric = false
FEATURE [Part::Extrusion] Extrude057  label="top025"
  Base = -> Sketch064
  Dir = (0,0,1)
  DirMode = 2
  FaceMakerClass = Part::FaceMakerBullseye
  LengthFwd = 72
  LengthRev = 0
  Solid = true
  Symmetric = false
FEATURE [Sketcher::SketchObject] Sketch066
  FullyConstrained = true
  MapMode = 3
  Placement = pos=(0,0,0) rot=(1,0,0;1.5708rad)
  Support = -> [Extrude057]
  sketch-geometry (8):
    g0: Circle CenterX=80.351 CenterY=-67.6202 CenterZ=0 NormalX=0 NormalY=0 NormalZ=1 AngleXU=0 Radius=3
    g1: Circle CenterX=80.351 CenterY=-4.92017 CenterZ=0 NormalX=0 NormalY=0 NormalZ=1 AngleXU=0 Radius=3
    g2: Circle CenterX=23.851 CenterY=-4.92017 CenterZ=0 NormalX=0 NormalY=0 NormalZ=1 AngleXU=0 Radius=3
    g3: Circle CenterX=23.851 CenterY=-67.6202 CenterZ=0 NormalX=0 NormalY=0 NormalZ=1 AngleXU=0 Radius=3
    g4: Circle CenterX=23.851 CenterY=-67.6202 CenterZ=0 NormalX=0 NormalY=0 NormalZ=1 AngleXU=0 Radius=5
    g5: Circle CenterX=80.351 CenterY=-67.6202 CenterZ=0 NormalX=0 NormalY=0 NormalZ=1 AngleXU=0 Radius=5
    g6: Circle CenterX=23.851 CenterY=-4.92017 CenterZ=0 NormalX=0 NormalY=0 NormalZ=1 AngleXU=0 Radius=5
    g7: Circle CenterX=80.351 CenterY=-4.92017 CenterZ=0 NormalX=0 NormalY=0 NormalZ=1 AngleXU=0 Radius=5
  constraints (8):
    c: Block(g1)
    c: Block(g0)
    c: Block(g3)
    c: Block(g2)
    c: Block(g5)
    c: Block(g4)
    c: Block(g6)
    c: Block(g7)
FEATURE [Part::Extrusion] Extrude055
  Base = -> Sketch066
  Dir = (0,-1,2e-16)
  DirMode = 2
  FaceMakerClass = Part::FaceMakerBullseye
  LengthFwd = 2
  LengthRev = 0
  Solid = true
  Symmetric = false
FEATURE [Part::Fillet] Fillet041
  Base = -> Extrude056
  Edges = 4 edges r=1.99: [Edge6,Edge12,Edge18,Edge24]
FEATURE [Part::Cut] Cut045
  Base = -> Extrude055
  Placement = pos=(0,6,0) rot=(0,0,1;0rad)
  Tool = -> Fillet041
FEATURE [Part::MultiFuse] Fusion095  label="pcbScrewPillars"
  Placement = pos=(-3.2,-1,72.3) rot=(0,0,1;0rad)
  Shapes = -> [Cut045,Extrude054]
FEATURE [Part::Feature] Face113
  shape: bbox 3.2 x 1.5 x 2e-07 mm, 1 faces, 0 solids (baked)
FEATURE [Part::Revolution] Revolve121  label="backCaseScrewRetainer002"
  Angle = 360
  Axis = (0,1,0)
  Base = (0,0,0)
  FaceMakerClass = Part::FaceMakerBullseye
  Placement = pos=(12.5,3,62) rot=(0,0,1;0rad)
  Solid = false
  Source = -> Face113
  Symmetric = false
FEATURE [Part::Feature] Face114
  shape: bbox 3.2 x 1.5 x 2e-07 mm, 1 faces, 0 solids (baked)
FEATURE [Part::Feature] Face115
  shape: bbox 3.2 x 1.5 x 2e-07 mm, 1 faces, 0 solids (baked)
FEATURE [Part::Feature] Face116
  shape: bbox 3.2 x 1.5 x 2e-07 mm, 1 faces, 0 solids (baked)
FEATURE [Part::Revolution] Revolve122  label="frontCaseScrewRetainer004"
  Angle = 360
  Axis = (0,1,0)
  Base = (0,0,0)
  FaceMakerClass = Part::FaceMakerBullseye
  Placement = pos=(89.5,3,68.5) rot=(0,0,1;0rad)
  Solid = false
  Source = -> Face115
  Symmetric = false
FEATURE [Part::Revolution] Revolve123  label="frontCaseScrewRetainer005"
  Angle = 360
  Axis = (0,1,0)
  Base = (0,0,0)
  FaceMakerClass = Part::FaceMakerBullseye
  Placement = pos=(89.5,3,3.5) rot=(0,0,1;0rad)
  Solid = false
  Source = -> Face116
  Symmetric = false
FEATURE [Part::Revolution] Revolve124  label="backCaseScrewRetainer003"
  Angle = 360
  Axis = (0,1,0)
  Base = (0,0,0)
  FaceMakerClass = Part::FaceMakerBullseye
  Placement = pos=(12.5,3,10) rot=(0,0,1;0rad)
  Solid = false
  Source = -> Face114
  Symmetric = false
FEATURE [Part::Feature] Face117
  shape: bbox 3.6 x 3.2 x 2e-07 mm, 1 faces, 0 solids (baked)
FEATURE [Part::Revolution] Revolve125  label="moreFrontCaseScrewRetainer004"
  Angle = 360
  Axis = (0,1,0)
  Base = (0,0,0)
  FaceMakerClass = Part::FaceMakerBullseye
  Placement = pos=(109.5,4.5,68.5) rot=(0,0,1;0rad)
  Solid = false
  Source = -> Face117
  Symmetric = false
FEATURE [Part::Feature] Face118
  shape: bbox 3.6 x 3.2 x 2e-07 mm, 1 faces, 0 solids (baked)
FEATURE [Part::Revolution] Revolve126  label="moreFrontCaseScrewRetainer005"
  Angle = 360
  Axis = (0,1,0)
  Base = (0,0,0)
  FaceMakerClass = Part::FaceMakerBullseye
  Placement = pos=(109.5,4.5,3.5) rot=(0,0,1;0rad)
  Solid = false
  Source = -> Face118
  Symmetric = false
FEATURE [Part::MultiFuse] Fusion096  label="screwRetainers001"
  Shapes = -> [Revolve126,Revolve125,Revolve124,Revolve123,Revolve122,Revolve121]
FEATURE [Part::Feature] Face119
  shape: bbox 10 x 16.5 x 2e-07 mm, 1 faces, 0 solids (baked)
FEATURE [Part::Revolution] Revolve130  label="plugHousing050"
  Angle = 360
  Axis = (0,1,0)
  Base = (0,0,0)
  FaceMakerClass = Part::FaceMakerBullseye
  Placement = pos=(0,0,36.15) rot=(0,0,1;0rad)
  Solid = false
  Source = -> Face119
  Symmetric = false
FEATURE [Part::Feature] Face120
  shape: bbox 10 x 16.5 x 2e-07 mm, 1 faces, 0 solids (baked)
FEATURE [Part::Feature] Face121
  shape: bbox 10 x 16.5 x 2e-07 mm, 1 faces, 0 solids (baked)
FEATURE [Part::Revolution] Revolve127  label="plugHousing047"
  Angle = 360
  Axis = (0,1,0)
  Base = (0,0,0)
  FaceMakerClass = Part::FaceMakerBullseye
  Placement = pos=(0,0,36.15) rot=(0,0,1;0rad)
  Solid = false
  Source = -> Face121
  Symmetric = false
FEATURE [Part::Feature] Face122
  shape: bbox 10 x 16.5 x 2e-07 mm, 1 faces, 0 solids (baked)
FEATURE [Part::Feature] Face123
  shape: bbox 10 x 16.5 x 2e-07 mm, 1 faces, 0 solids (baked)
FEATURE [Part::Revolution] Revolve128  label="plugHousing048"
  Angle = 360
  Axis = (0,1,0)
  Base = (0,0,0)
  FaceMakerClass = Part::FaceMakerBullseye
  Placement = pos=(0,0,36.15) rot=(0,0,1;0rad)
  Solid = false
  Source = -> Face123
  Symmetric = false
FEATURE [Part::MultiFuse] Fusion100  label="plugHousing054"
  Placement = pos=(0,0,0) rot=(0,0,1;1.5708rad)
  Shapes = -> [Revolve130,Revolve128]
FEATURE [Part::Feature] Face124
  shape: bbox 10 x 16.5 x 2e-07 mm, 1 faces, 0 solids (baked)
FEATURE [Part::Feature] Face125
  shape: bbox 10 x 16.5 x 2e-07 mm, 1 faces, 0 solids (baked)
FEATURE [Part::Revolution] Revolve129  label="plugHousing049"
  Angle = 360
  Axis = (0,1,0)
  Base = (0,0,0)
  FaceMakerClass = Part::FaceMakerBullseye
  Placement = pos=(0,0,36.15) rot=(0,0,1;0rad)
  Solid = false
  Source = -> Face125
  Symmetric = false
FEATURE [Part::Feature] Face126
  shape: bbox 10 x 16.5 x 2e-07 mm, 1 faces, 0 solids (baked)
FEATURE [Part::Revolution] Revolve131  label="plugHousing058"
  Angle = 360
  Axis = (0,1,0)
  Base = (0,0,0)
  FaceMakerClass = Part::FaceMakerBullseye
  Placement = pos=(0,0,36.15) rot=(0,0,1;0rad)
  Solid = false
  Source = -> Face120
  Symmetric = false
FEATURE [Part::MultiFuse] Fusion099  label="plugHousing053"
  Placement = pos=(0,0,0) rot=(0,0,1;1.5708rad)
  Shapes = -> [Revolve127,Revolve131]
FEATURE [Part::MultiFuse] Fusion102  label="plugHousing056"
  Placement = pos=(0,19,0) rot=(0,0,1;3.14159rad)
  Shapes = -> [Fusion100,Fusion099]
FEATURE [Part::Revolution] Revolve132  label="plugHousing059"
  Angle = 360
  Axis = (0,1,0)
  Base = (0,0,0)
  FaceMakerClass = Part::FaceMakerBullseye
  Placement = pos=(0,0,36.15) rot=(0,0,1;0rad)
  Solid = false
  Source = -> Face126
  Symmetric = false
FEATURE [Part::Revolution] Revolve133  label="plugHousing060"
  Angle = 360
  Axis = (0,1,0)
  Base = (0,0,0)
  FaceMakerClass = Part::FaceMakerBullseye
  Placement = pos=(0,0,36.15) rot=(0,0,1;0rad)
  Solid = false
  Source = -> Face122
  Symmetric = false
FEATURE [Part::MultiFuse] Fusion097  label="plugHousing051"
  Placement = pos=(0,0,0) rot=(0,0,1;1.5708rad)
  Shapes = -> [Revolve133,Revolve132]
FEATURE [Part::Revolution] Revolve134  label="plugHousing061"
  Angle = 360
  Axis = (0,1,0)
  Base = (0,0,0)
  FaceMakerClass = Part::FaceMakerBullseye
  Placement = pos=(0,0,36.15) rot=(0,0,1;0rad)
  Solid = false
  Source = -> Face124
  Symmetric = false
FEATURE [Part::MultiFuse] Fusion101  label="plugHousing055"
  Placement = pos=(0,0,0) rot=(0,0,1;1.5708rad)
  Shapes = -> [Revolve129,Revolve134]
FEATURE [Part::MultiFuse] Fusion098  label="plugHousing052"
  Placement = pos=(0,19,0) rot=(0,0,1;3.14159rad)
  Shapes = -> [Fusion097,Fusion101]
FEATURE [Part::MultiFuse] Fusion103  label="plugHousing057"
  Placement = pos=(122.621,0,-0.15) rot=(0,0,1;0rad)
  Shapes = -> [Fusion102,Fusion098]
FEATURE [Part::Box] Box028  label="Cube015"
  AttacherType = Attacher::AttachEngine3D
  Height = 28
  Length = 3
  Placement = pos=(110.7,19,22) rot=(0,0,1;0rad)
  Width = 15.7
FEATURE [Part::Cylinder] Cylinder044
  Angle = 360
  AttacherType = Attacher::AttachEngine3D
  Height = 20
  Placement = pos=(0,0,36.15) rot=(0,0,1;0rad)
  Radius = 10.3
FEATURE [Part::Cylinder] Cylinder045
  Angle = 360
  AttacherType = Attacher::AttachEngine3D
  Height = 10
  Placement = pos=(0,0,36.15) rot=(0,0,1;0rad)
  Radius = 4
FEATURE [Part::MultiFuse] Fusion104  label="removeToCreteHoleForPlugHousing040"
  Placement = pos=(70,19,36) rot=(0,1,0;1.5708rad)
  Shapes = -> [Cylinder044,Cylinder045]
FEATURE [Part::Cut] Cut046  label="plugHousingTab003"
  Base = -> Box028
  Tool = -> Fusion104
FEATURE [Part::MultiFuse] Fusion105  label="plugHousing062"
  Shapes = -> [Fusion103,Cut046]
FEATURE [Part::Fillet] Fillet042
  Base = -> Fusion105
  Edges = 1 edges r=2: [Edge25]
FEATURE [Part::Fillet] Fillet043  label="plugHousing063"
  Base = -> Fillet042
  Edges = 1 edges r=2: [Edge8]
  Placement = pos=(7,0,0) rot=(0,0,1;0rad)
FEATURE [Part::Feature] Face127
  shape: bbox 10 x 16.5 x 2e-07 mm, 1 faces, 0 solids (baked)
FEATURE [Part::Feature] Face128
  shape: bbox 10 x 16.5 x 2e-07 mm, 1 faces, 0 solids (baked)
FEATURE [Part::Revolution] Revolve137  label="plugHousing070"
  Angle = 360
  Axis = (0,1,0)
  Base = (0,0,0)
  FaceMakerClass = Part::FaceMakerBullseye
  Placement = pos=(0,0,36.15) rot=(0,0,1;0rad)
  Solid = false
  Source = -> Face127
  Symmetric = false
FEATURE [Part::Revolution] Revolve140  label="plugHousing073"
  Angle = 360
  Axis = (0,1,0)
  Base = (0,0,0)
  FaceMakerClass = Part::FaceMakerBullseye
  Placement = pos=(0,0,36.15) rot=(0,0,1;0rad)
  Solid = false
  Source = -> Face128
  Symmetric = false
FEATURE [Part::Feature] Face129
  shape: bbox 10 x 16.5 x 2e-07 mm, 1 faces, 0 solids (baked)
FEATURE [Part::Revolution] Revolve138  label="plugHousing071"
  Angle = 360
  Axis = (0,1,0)
  Base = (0,0,0)
  FaceMakerClass = Part::FaceMakerBullseye
  Placement = pos=(0,0,36.15) rot=(0,0,1;0rad)
  Solid = false
  Source = -> Face129
  Symmetric = false
FEATURE [Part::Feature] Face130
  shape: bbox 10 x 16.5 x 2e-07 mm, 1 faces, 0 solids (baked)
FEATURE [Part::Revolution] Revolve139  label="plugHousing072"
  Angle = 360
  Axis = (0,1,0)
  Base = (0,0,0)
  FaceMakerClass = Part::FaceMakerBullseye
  Placement = pos=(0,0,36.15) rot=(0,0,1;0rad)
  Solid = false
  Source = -> Face130
  Symmetric = false
FEATURE [Part::Feature] Face131
  shape: bbox 10 x 16.5 x 2e-07 mm, 1 faces, 0 solids (baked)
FEATURE [Part::Revolution] Revolve135  label="plugHousing068"
  Angle = 360
  Axis = (0,1,0)
  Base = (0,0,0)
  FaceMakerClass = Part::FaceMakerBullseye
  Placement = pos=(0,0,36.15) rot=(0,0,1;0rad)
  Solid = false
  Source = -> Face131
  Symmetric = false
FEATURE [Part::MultiFuse] Fusion112  label="plugHousing078"
  Placement = pos=(0,0,0) rot=(0,0,1;1.5708rad)
  Shapes = -> [Revolve135,Revolve139]
FEATURE [Part::Feature] Face132
  shape: bbox 10 x 16.5 x 2e-07 mm, 1 faces, 0 solids (baked)
FEATURE [Part::Revolution] Revolve141  label="plugHousing074"
  Angle = 360
  Axis = (0,1,0)
  Base = (0,0,0)
  FaceMakerClass = Part::FaceMakerBullseye
  Placement = pos=(0,0,36.15) rot=(0,0,1;0rad)
  Solid = false
  Source = -> Face132
  Symmetric = false
FEATURE [Part::MultiFuse] Fusion110  label="plugHousing076"
  Placement = pos=(0,0,0) rot=(0,0,1;1.5708rad)
  Shapes = -> [Revolve141,Revolve140]
FEATURE [Part::Feature] Face133
  shape: bbox 10 x 16.5 x 2e-07 mm, 1 faces, 0 solids (baked)
FEATURE [Part::Revolution] Revolve136  label="plugHousing069"
  Angle = 360
  Axis = (0,1,0)
  Base = (0,0,0)
  FaceMakerClass = Part::FaceMakerBullseye
  Placement = pos=(0,0,36.15) rot=(0,0,1;0rad)
  Solid = false
  Source = -> Face133
  Symmetric = false
FEATURE [Part::MultiFuse] Fusion106  label="plugHousing064"
  Placement = pos=(0,0,0) rot=(0,0,1;1.5708rad)
  Shapes = -> [Revolve138,Revolve136]
FEATURE [Part::MultiFuse] Fusion108  label="plugHousing066"
  Placement = pos=(0,19,0) rot=(0,0,1;3.14159rad)
  Shapes = -> [Fusion106,Fusion112]
FEATURE [Part::Feature] Face134
  shape: bbox 10 x 16.5 x 2e-07 mm, 1 faces, 0 solids (baked)
FEATURE [Part::Revolution] Revolve142  label="plugHousing075"
  Angle = 360
  Axis = (0,1,0)
  Base = (0,0,0)
  FaceMakerClass = Part::FaceMakerBullseye
  Placement = pos=(0,0,36.15) rot=(0,0,1;0rad)
  Solid = false
  Source = -> Face134
  Symmetric = false
FEATURE [Part::MultiFuse] Fusion107  label="plugHousing065"
  Placement = pos=(0,0,0) rot=(0,0,1;1.5708rad)
  Shapes = -> [Revolve137,Revolve142]
FEATURE [Part::MultiFuse] Fusion111  label="plugHousing077"
  Placement = pos=(0,19,0) rot=(0,0,1;3.14159rad)
  Shapes = -> [Fusion110,Fusion107]
FEATURE [Part::MultiFuse] Fusion109  label="plugHousing067"
  Placement = pos=(131.236,0,-0.15) rot=(0,0,1;0rad)
  Shapes = -> [Fusion108,Fusion111]
FEATURE [Part::MultiFuse] Fusion113  label="plugHousing079"
  Shapes = -> [Fillet043,Fusion109]
FEATURE [Part::Feature] Face135
  shape: bbox 3.5 x 17.8 x 2e-07 mm, 1 faces, 0 solids (baked)
FEATURE [Part::Revolution] Revolve143  label="removeToCreateScrewAndThreadedInsertHole049"
  Angle = 360
  Axis = (0,1,0)
  Base = (0,0,0)
  FaceMakerClass = Part::FaceMakerBullseye
  Placement = pos=(12.5,0,10) rot=(0,0,1;0rad)
  Solid = false
  Source = -> Face135
  Symmetric = false
FEATURE [Part::Feature] Face136
  shape: bbox 3.5 x 17.8 x 2e-07 mm, 1 faces, 0 solids (baked)
FEATURE [Part::Revolution] Revolve144  label="removeToCreateScrewAndThreadedInsertHole050"
  Angle = 360
  Axis = (0,1,0)
  Base = (0,0,0)
  FaceMakerClass = Part::FaceMakerBullseye
  Placement = pos=(12.5,0,62) rot=(0,0,1;0rad)
  Solid = false
  Source = -> Face136
  Symmetric = false
FEATURE [Part::Feature] Face137
  shape: bbox 3.5 x 17.8 x 2e-07 mm, 1 faces, 0 solids (baked)
FEATURE [Part::Revolution] Revolve145  label="removeToCreateScrewAndThreadedInsertHole051"
  Angle = 360
  Axis = (0,1,0)
  Base = (0,0,0)
  FaceMakerClass = Part::FaceMakerBullseye
  Placement = pos=(89.5,0,68.5) rot=(0,0,1;0rad)
  Solid = false
  Source = -> Face137
  Symmetric = false
FEATURE [Part::Feature] Face138
  shape: bbox 3.5 x 17.8 x 2e-07 mm, 1 faces, 0 solids (baked)
FEATURE [Part::Revolution] Revolve146  label="removeToCreateScrewAndThreadedInsertHole052"
  Angle = 360
  Axis = (0,1,0)
  Base = (0,0,0)
  FaceMakerClass = Part::FaceMakerBullseye
  Placement = pos=(89.5,0,3.5) rot=(0,0,1;0rad)
  Solid = false
  Source = -> Face138
  Symmetric = false
FEATURE [Part::Feature] Face139
  shape: bbox 3.5 x 17.8 x 2e-07 mm, 1 faces, 0 solids (baked)
FEATURE [Part::Revolution] Revolve147  label="removeToCreateScrewAndThreadedInsertHole053"
  Angle = 360
  Axis = (0,1,0)
  Base = (0,0,0)
  FaceMakerClass = Part::FaceMakerBullseye
  Placement = pos=(109.5,4.7,3.5) rot=(0,0,1;0rad)
  Solid = false
  Source = -> Face139
  Symmetric = false
FEATURE [Part::Feature] Face140
  shape: bbox 3.5 x 17.8 x 2e-07 mm, 1 faces, 0 solids (baked)
FEATURE [Part::Revolution] Revolve148  label="removeToCreateScrewAndThreadedInsertHole054"
  Angle = 360
  Axis = (0,1,0)
  Base = (0,0,0)
  FaceMakerClass = Part::FaceMakerBullseye
  Placement = pos=(109.5,4.7,68.5) rot=(0,0,1;0rad)
  Solid = false
  Source = -> Face140
  Symmetric = false
FEATURE [Part::MultiFuse] Fusion114  label="removeToCreateScrewAndThreadedInsertHole055"
  Shapes = -> [Revolve148,Revolve147,Revolve146,Revolve145,Revolve144,Revolve143]
FEATURE [Part::Cut] Cut047  label="casePillars004"
  Base = -> Cut037
  Tool = -> Fusion114
FEATURE [Part::Feature] Face141
  shape: bbox 3.5 x 17.8 x 2e-07 mm, 1 faces, 0 solids (baked)
FEATURE [Part::Feature] Face142
  shape: bbox 3.5 x 17.8 x 2e-07 mm, 1 faces, 0 solids (baked)
FEATURE [Part::Feature] Face143
  shape: bbox 3.5 x 17.8 x 2e-07 mm, 1 faces, 0 solids (baked)
FEATURE [Part::Revolution] Revolve149  label="removeToCreateScrewAndThreadedInsertHole057"
  Angle = 360
  Axis = (0,1,0)
  Base = (0,0,0)
  FaceMakerClass = Part::FaceMakerBullseye
  Placement = pos=(12.5,0,10) rot=(0,0,1;0rad)
  Solid = false
  Source = -> Face141
  Symmetric = false
FEATURE [Part::Feature] Face144
  shape: bbox 3.5 x 17.8 x 2e-07 mm, 1 faces, 0 solids (baked)
FEATURE [Part::Feature] Face145
  shape: bbox 3.5 x 17.8 x 2e-07 mm, 1 faces, 0 solids (baked)
FEATURE [Part::Feature] Face146
  shape: bbox 3.5 x 17.8 x 2e-07 mm, 1 faces, 0 solids (baked)
FEATURE [Part::Revolution] Revolve150  label="removeToCreateScrewAndThreadedInsertHole058"
  Angle = 360
  Axis = (0,1,0)
  Base = (0,0,0)
  FaceMakerClass = Part::FaceMakerBullseye
  Placement = pos=(12.5,0,62) rot=(0,0,1;0rad)
  Solid = false
  Source = -> Face146
  Symmetric = false
FEATURE [Part::Revolution] Revolve151  label="removeToCreateScrewAndThreadedInsertHole059"
  Angle = 360
  Axis = (0,1,0)
  Base = (0,0,0)
  FaceMakerClass = Part::FaceMakerBullseye
  Placement = pos=(89.5,0,68.5) rot=(0,0,1;0rad)
  Solid = false
  Source = -> Face143
  Symmetric = false
FEATURE [Part::Revolution] Revolve152  label="removeToCreateScrewAndThreadedInsertHole060"
  Angle = 360
  Axis = (0,1,0)
  Base = (0,0,0)
  FaceMakerClass = Part::FaceMakerBullseye
  Placement = pos=(89.5,0,3.5) rot=(0,0,1;0rad)
  Solid = false
  Source = -> Face142
  Symmetric = false
FEATURE [Part::Revolution] Revolve153  label="removeToCreateScrewAndThreadedInsertHole061"
  Angle = 360
  Axis = (0,1,0)
  Base = (0,0,0)
  FaceMakerClass = Part::FaceMakerBullseye
  Placement = pos=(109.5,4.7,3.5) rot=(0,0,1;0rad)
  Solid = false
  Source = -> Face145
  Symmetric = false
FEATURE [Part::Revolution] Revolve154  label="removeToCreateScrewAndThreadedInsertHole062"
  Angle = 360
  Axis = (0,1,0)
  Base = (0,0,0)
  FaceMakerClass = Part::FaceMakerBullseye
  Placement = pos=(109.5,4.7,68.5) rot=(0,0,1;0rad)
  Solid = false
  Source = -> Face144
  Symmetric = false
FEATURE [Part::MultiFuse] Fusion115  label="removeToCreateScrewAndThreadedInsertHole056"
  Shapes = -> [Revolve154,Revolve153,Revolve152,Revolve151,Revolve150,Revolve149]
FEATURE [Part::Feature] Face147
  shape: bbox 9.8 x 26.5 x 2e-07 mm, 1 faces, 0 solids (baked)
FEATURE [Part::Revolution] Revolve155
  Angle = 360
  Axis = (0,1,0)
  Base = (0,0,0)
  FaceMakerClass = Part::FaceMakerBullseye
  Placement = pos=(0,0,0) rot=(0,0,1;1.5708rad)
  Solid = false
  Source = -> Face147
  Symmetric = false
FEATURE [Part::Feature] Face148
  shape: bbox 9.8 x 26.5 x 2e-07 mm, 1 faces, 0 solids (baked)
FEATURE [Part::Revolution] Revolve156
  Angle = 360
  Axis = (0,1,0)
  Base = (0,0,0)
  FaceMakerClass = Part::FaceMakerBullseye
  Placement = pos=(0,0,0) rot=(0,0,1;1.5708rad)
  Solid = false
  Source = -> Face148
  Symmetric = false
FEATURE [Part::MultiFuse] Fusion116
  Placement = pos=(-18,19,36) rot=(0,0,1;0rad)
  Shapes = -> [Revolve156,Revolve155]
FEATURE [Part::Box] Box029  label="Cube016"
  AttacherType = Attacher::AttachEngine3D
  Height = 28
  Length = 3
  Placement = pos=(110.7,19,22) rot=(0,0,1;0rad)
  Width = 15.7
FEATURE [Part::Cylinder] Cylinder046
  Angle = 360
  AttacherType = Attacher::AttachEngine3D
  Height = 10
  Placement = pos=(0,0,36.15) rot=(0,0,1;0rad)
  Radius = 4
FEATURE [Part::Cylinder] Cylinder047
  Angle = 360
  AttacherType = Attacher::AttachEngine3D
  Height = 20
  Placement = pos=(0,0,36.15) rot=(0,0,1;0rad)
  Radius = 10.3
FEATURE [Part::MultiFuse] Fusion117  label="removeToCreteHoleForPlugHousing041"
  Placement = pos=(70,19,36) rot=(0,1,0;1.5708rad)
  Shapes = -> [Cylinder047,Cylinder046]
FEATURE [Part::Cut] Cut049  label="plugHousingTab004"
  Base = -> Box029
  Placement = pos=(-107.4,-14,0) rot=(0,0,1;0rad)
  Tool = -> Fusion117
FEATURE [Part::Box] Box030  label="Cube017"
  AttacherType = Attacher::AttachEngine3D
  Height = 28
  Length = 3
  Placement = pos=(110.7,19,22) rot=(0,0,1;0rad)
  Width = 15.7
FEATURE [Part::Cylinder] Cylinder048
  Angle = 360
  AttacherType = Attacher::AttachEngine3D
  Height = 10
  Placement = pos=(0,0,36.15) rot=(0,0,1;0rad)
  Radius = 4
FEATURE [Part::Cylinder] Cylinder049
  Angle = 360
  AttacherType = Attacher::AttachEngine3D
  Height = 20
  Placement = pos=(0,0,36.15) rot=(0,0,1;0rad)
  Radius = 10.3
FEATURE [Part::MultiFuse] Fusion118  label="removeToCreteHoleForPlugHousing042"
  Placement = pos=(70,19,36) rot=(0,1,0;1.5708rad)
  Shapes = -> [Cylinder049,Cylinder048]
FEATURE [Part::Cut] Cut050  label="plugHousingTab005"
  Base = -> Box030
  Placement = pos=(-107.4,-14,0) rot=(0,0,1;0rad)
  Tool = -> Fusion118
FEATURE [Part::MultiFuse] Fusion119
  Placement = pos=(9.6,23,0) rot=(0,0,1;3.14159rad)
  Shapes = -> [Cut049,Cut050]
FEATURE [Part::Box] Box031  label="Cube018"
  AttacherType = Attacher::AttachEngine3D
  Height = 10
  Length = 3
  Placement = pos=(3.3,4,12) rot=(0,0,1;0rad)
  Width = 10
FEATURE [Part::Fillet] Fillet044
  Base = -> Box031
  Edges = 1 edges r=2: [Edge11]
FEATURE [Part::Box] Box032  label="Cube019"
  AttacherType = Attacher::AttachEngine3D
  Height = 10
  Length = 3
  Placement = pos=(3.3,4,50) rot=(0,0,1;0rad)
  Width = 10
FEATURE [Part::Fillet] Fillet045
  Base = -> Box032
  Edges = 1 edges r=2: [Edge12]
FEATURE [Part::Box] Box033  label="Cube020"
  AttacherType = Attacher::AttachEngine3D
  Height = 28
  Length = 4
  Placement = pos=(5,0,22) rot=(0,0,1;0rad)
  Width = 10
FEATURE [Part::Fillet] Fillet046
  Base = -> Box033
  Edges = 1 edges r=1: [Edge7]
FEATURE [Part::Fillet] Fillet047
  Base = -> Fillet046
  Edges = 1 edges r=2: [Edge5]
FEATURE [Part::Fillet] Fillet048
  Base = -> Fillet047
  Edges = 1 edges r=2: [Edge2]
FEATURE [Part::Cylinder] Cylinder050
  Angle = 360
  AttacherType = Attacher::AttachEngine3D
  Height = 20
  Placement = pos=(0,0,36.15) rot=(0,0,1;0rad)
  Radius = 8.2
FEATURE [Part::Cylinder] Cylinder051
  Angle = 360
  AttacherType = Attacher::AttachEngine3D
  Height = 10
  Placement = pos=(0,0,36.15) rot=(0,0,1;0rad)
  Radius = 4
FEATURE [Part::MultiFuse] Fusion120  label="removeToCreteHoleForPlugHousing043"
  Placement = pos=(-42,19,36) rot=(0,1,0;1.5708rad)
  Shapes = -> [Cylinder050,Cylinder051]
FEATURE [Sketcher::SketchObject] Sketch067  label="topSketch018"
  FullyConstrained = true
  sketch-geometry (4):
    g0: LineSegment StartX=16.8446 StartY=31.512 StartZ=0 EndX=16.3251 EndY=34.4666 EndZ=0
    g1: ArcOfCircle CenterX=19 CenterY=19.2524 CenterZ=0 NormalX=0 NormalY=0 NormalZ=1 AngleXU=0 Radius=15.4476 StartAngle=1.74483 EndAngle=2.72717
    g2: ArcOfCircle CenterX=19 CenterY=19.2524 CenterZ=0 NormalX=0 NormalY=0 NormalZ=1 AngleXU=0 Radius=12.4476 StartAngle=1.74483 EndAngle=2.73189
    g3: LineSegment StartX=4.86004 StartY=25.4725 StartZ=0 EndX=7.58253 EndY=24.2107 EndZ=0
  constraints (7):
    c: Block(g0)
    c: Coincident(g1,g0)
    c: Coincident(g2,g0)
    c: Coincident(g3,g1)
    c: Coincident(g3,g2)
    c: Block(g1)
    c: Block(g2)
FEATURE [Part::Extrusion] Extrude058
  Base = -> Sketch067
  Dir = (0,0,1)
  DirMode = 2
  FaceMakerClass = Part::FaceMakerBullseye
  LengthFwd = 10
  LengthRev = 0
  Placement = pos=(0,0,31) rot=(0,0,1;0rad)
  Solid = true
  Symmetric = false
FEATURE [Part::Cut] Cut051
  Base = -> Extrude058
  Tool = -> Fusion120
FEATURE [Part::Fillet] Fillet049
  Base = -> Cut051
  Edges = 1 edges r=2: [Edge1]
FEATURE [Part::Fillet] Fillet050
  Base = -> Fillet049
  Edges = 1 edges r=2.5: [Edge1]
FEATURE [Part::Fillet] Fillet051
  Base = -> Fillet050
  Edges = 1 edges r=2.5: [Edge2]
FEATURE [Part::MultiFuse] Fusion121  label="wireHolder003"
  Shapes = -> [Fusion116,Fillet051]
FEATURE [Part::MultiFuse] Fusion122
  Shapes = -> [Fillet045,Fusion121]
FEATURE [Part::MultiFuse] Fusion123  label="wireHolder004"
  Shapes = -> [Fusion122,Fillet048]
FEATURE [Part::MultiFuse] Fusion124  label="wireHolder005"
  Shapes = -> [Fillet044,Fusion119,Fusion123]
FEATURE [Sketcher::SketchObject] Sketch068  label="topSketch019"
  FullyConstrained = true
  sketch-geometry (6):
    g0: LineSegment StartX=19 StartY=38 StartZ=0 EndX=117 EndY=38 EndZ=0
    g1: ArcOfCircle CenterX=19 CenterY=19 CenterZ=0 NormalX=0 NormalY=0 NormalZ=1 AngleXU=0 Radius=19 StartAngle=1.5708 EndAngle=3.14159
    g2: LineSegment StartX=117 StartY=38 StartZ=0 EndX=117 EndY=19 EndZ=0
    g3: LineSegment StartX=98 StartY=1.0161e-12 StartZ=0 EndX=5.22862e-06 EndY=1.0161e-12 EndZ=0
    g4: LineSegment StartX=5.22862e-06 StartY=19 StartZ=0 EndX=5.22862e-06 EndY=1.0161e-12 EndZ=0
    g5: ArcOfCircle CenterX=98 CenterY=19 CenterZ=0 NormalX=0 NormalY=0 NormalZ=1 AngleXU=0 Radius=19 StartAngle=4.71239 EndAngle=6.28319
  constraints (16):
    c: Horizontal(g0)
    c: Distance(g0) = 98
    c: Coincident(g1,g0)
    c: Block(g1)
    c: Coincident(g2,g0)
    c: Vertical(g2)
    c: Distance(g2) = 19
    c: Horizontal(g3)
    c: Coincident(g4,g1)
    c: Vertical(g4)
    c: Coincident(g3,g4)
    c: Block(g3)
    c: Coincident(g5,g2)
    c: Coincident(g5,g3)
    c: Block(g0)
    c: Block(g5)
FEATURE [Part::Extrusion] Extrude059  label="sideA002"
  Base = -> Sketch068
  Dir = (0,0,1)
  DirMode = 2
  FaceMakerClass = Part::FaceMakerBullseye
  LengthFwd = 3
  LengthRev = 0
  Placement = pos=(0,0,-2.7) rot=(0,0,1;0rad)
  Solid = true
  Symmetric = false
FEATURE [Sketcher::SketchObject] Sketch069  label="topSketch020"
  FullyConstrained = true
  sketch-geometry (6):
    g0: LineSegment StartX=19 StartY=38 StartZ=0 EndX=117 EndY=38 EndZ=0
    g1: ArcOfCircle CenterX=19 CenterY=19 CenterZ=0 NormalX=0 NormalY=0 NormalZ=1 AngleXU=0 Radius=19 StartAngle=1.5708 EndAngle=3.14159
    g2: LineSegment StartX=117 StartY=38 StartZ=0 EndX=117 EndY=19 EndZ=0
    g3: LineSegment StartX=98 StartY=1.0161e-12 StartZ=0 EndX=5.22862e-06 EndY=1.0161e-12 EndZ=0
    g4: LineSegment StartX=5.22862e-06 StartY=19 StartZ=0 EndX=5.22862e-06 EndY=1.0161e-12 EndZ=0
    g5: ArcOfCircle CenterX=98 CenterY=19 CenterZ=0 NormalX=0 NormalY=0 NormalZ=1 AngleXU=0 Radius=19 StartAngle=4.71239 EndAngle=6.28319
  constraints (16):
    c: Horizontal(g0)
    c: Distance(g0) = 98
    c: Coincident(g1,g0)
    c: Block(g1)
    c: Coincident(g2,g0)
    c: Vertical(g2)
    c: Distance(g2) = 19
    c: Horizontal(g3)
    c: Coincident(g4,g1)
    c: Vertical(g4)
    c: Coincident(g3,g4)
    c: Block(g3)
    c: Coincident(g5,g2)
    c: Coincident(g5,g3)
    c: Block(g0)
    c: Block(g5)
FEATURE [Part::Extrusion] Extrude060  label="sideB002"
  Base = -> Sketch069
  Dir = (0,0,1)
  DirMode = 2
  FaceMakerClass = Part::FaceMakerBullseye
  LengthFwd = 3
  LengthRev = 0
  Placement = pos=(0,0,71.7) rot=(0,0,1;0rad)
  Solid = true
  Symmetric = false
FEATURE [Part::MultiFuse] Fusion127  label="removeFromBottom001"
  Placement = pos=(2,0,0) rot=(0,0,1;0rad)
  Shapes = -> [Extrude059,Extrude060]
FEATURE [Part::Cylinder] Cylinder052
  Angle = 360
  AttacherType = Attacher::AttachEngine3D
  Height = 20
  Placement = pos=(0,0,36.15) rot=(0,0,1;0rad)
  Radius = 14
FEATURE [Part::Cylinder] Cylinder053
  Angle = 360
  AttacherType = Attacher::AttachEngine3D
  Height = 10
  Placement = pos=(0,0,36.15) rot=(0,0,1;0rad)
  Radius = 4
FEATURE [Part::MultiFuse] Fusion128  label="removeToCreteHoleForPlugHousing044"
  Placement = pos=(70,19,36) rot=(0,1,0;1.5708rad)
  Shapes = -> [Cylinder052,Cylinder053]
FEATURE [Part::Cut] Cut052  label="bottom011"
  Base = -> Extrude043
  Tool = -> Fusion128
FEATURE [Part::Cut] Cut054  label="bottom012"
  Base = -> Cut052
  Tool = -> Fusion115
FEATURE [Sketcher::SketchObject] Sketch070
  FullyConstrained = true
  Placement = pos=(117,19,0) rot=(0.57735,0.57735,0.57735;2.0944rad)
  sketch-geometry (48):
    g0: LineSegment StartX=-49.19 StartY=69.25 StartZ=0 EndX=-49.19 EndY=66.25 EndZ=0
    g1: LineSegment StartX=-49.19 StartY=63.5 StartZ=0 EndX=-49.19 EndY=60.5 EndZ=0
    g2: LineSegment StartX=-49.19 StartY=57.75 StartZ=0 EndX=-49.19 EndY=54.75 EndZ=0
    g3: LineSegment StartX=-49.19 StartY=52 StartZ=0 EndX=-49.19 EndY=49 EndZ=0
    g4: LineSegment StartX=-49.19 StartY=46.25 StartZ=0 EndX=-49.19 EndY=43.25 EndZ=0
    g5: LineSegment StartX=-49.19 StartY=40.5 StartZ=0 EndX=-49.19 EndY=37.5 EndZ=0
    g6: LineSegment StartX=-49.19 StartY=34.5 StartZ=0 EndX=-49.19 EndY=31.5 EndZ=0
    g7: LineSegment StartX=-49.19 StartY=28.75 StartZ=0 EndX=-49.19 EndY=25.75 EndZ=0
    g8: LineSegment StartX=-49.19 StartY=23 StartZ=0 EndX=-49.19 EndY=20 EndZ=0
    g9: LineSegment StartX=-49.19 StartY=17.25 StartZ=0 EndX=-49.19 EndY=14.25 EndZ=0
    g10: LineSegment StartX=-49.19 StartY=11.5 StartZ=0 EndX=-49.19 EndY=8.5 EndZ=0
    g11: LineSegment StartX=-49.19 StartY=5.75 StartZ=0 EndX=-49.19 EndY=2.75 EndZ=0
    g12: ArcOfCircle CenterX=-1.5 CenterY=67.75 CenterZ=0 NormalX=0 NormalY=0 NormalZ=1 AngleXU=0 Radius=1.5 StartAngle=4.71239 EndAngle=7.85398
    g13: ArcOfCircle CenterX=-1.5 CenterY=62 CenterZ=0 NormalX=0 NormalY=0 NormalZ=1 AngleXU=0 Radius=1.5 StartAngle=4.71239 EndAngle=7.85398
    g14: ArcOfCircle CenterX=-1.5 CenterY=56.25 CenterZ=0 NormalX=0 NormalY=0 NormalZ=1 AngleXU=0 Radius=1.5 StartAngle=4.71239 EndAngle=7.85398
    g15: ArcOfCircle CenterX=-11.49 CenterY=50.5 CenterZ=0 NormalX=0 NormalY=0 NormalZ=1 AngleXU=0 Radius=1.5 StartAngle=4.71239 EndAngle=7.85398
    g16: ArcOfCircle CenterX=-16.28 CenterY=44.75 CenterZ=0 NormalX=0 NormalY=0 NormalZ=1 AngleXU=0 Radius=1.5 StartAngle=4.71239 EndAngle=7.85398
    g17: ArcOfCircle CenterX=-18.2337 CenterY=39 CenterZ=0 NormalX=0 NormalY=0 NormalZ=1 AngleXU=0 Radius=1.5 StartAngle=4.71485 EndAngle=7.85398
    g18: ArcOfCircle CenterX=-16.2837 CenterY=27.25 CenterZ=0 NormalX=0 NormalY=0 NormalZ=1 AngleXU=0 Radius=1.5 StartAngle=4.71485 EndAngle=7.85398
    g19: ArcOfCircle CenterX=-18.2337 CenterY=33 CenterZ=0 NormalX=0 NormalY=0 NormalZ=1 AngleXU=0 Radius=1.5 StartAngle=4.71485 EndAngle=7.85398
    g20: ArcOfCircle CenterX=-11.49 CenterY=21.5 CenterZ=0 NormalX=0 NormalY=0 NormalZ=1 AngleXU=0 Radius=1.5 StartAngle=4.71239 EndAngle=7.85398
    g21: ArcOfCircle CenterX=-1.5 CenterY=4.25 CenterZ=0 NormalX=0 NormalY=0 NormalZ=1 AngleXU=0 Radius=1.5 StartAngle=4.71239 EndAngle=7.85398
    g22: ArcOfCircle CenterX=-1.5 CenterY=10 CenterZ=0 NormalX=0 NormalY=0 NormalZ=1 AngleXU=0 Radius=1.5 StartAngle=4.71239 EndAngle=7.85398
    g23: ArcOfCircle CenterX=-1.5 CenterY=15.75 CenterZ=0 NormalX=0 NormalY=0 NormalZ=1 AngleXU=0 Radius=1.5 StartAngle=4.71239 EndAngle=7.85398
    g24: LineSegment StartX=-49.19 StartY=69.25 StartZ=0 EndX=-1.5 EndY=69.25 EndZ=0
    g25: LineSegment StartX=-49.19 StartY=66.25 StartZ=0 EndX=-1.5 EndY=66.25 EndZ=0
    g26: LineSegment StartX=-49.19 StartY=63.5 StartZ=0 EndX=-1.5 EndY=63.5 EndZ=0
    g27: LineSegment StartX=-49.19 StartY=60.5 StartZ=0 EndX=-1.5 EndY=60.5 EndZ=0
    g28: LineSegment StartX=-49.19 StartY=57.75 StartZ=0 EndX=-1.5 EndY=57.75 EndZ=0
    g29: LineSegment StartX=-49.19 StartY=54.75 StartZ=0 EndX=-1.5 EndY=54.75 EndZ=0
    g30: LineSegment StartX=-49.19 StartY=52 StartZ=0 EndX=-11.49 EndY=52 EndZ=0
    g31: LineSegment StartX=-49.19 StartY=49 StartZ=0 EndX=-11.49 EndY=49 EndZ=0
    g32: LineSegment StartX=-49.19 StartY=46.25 StartZ=0 EndX=-16.28 EndY=46.25 EndZ=0
    g33: LineSegment StartX=-49.19 StartY=43.25 StartZ=0 EndX=-16.28 EndY=43.25 EndZ=0
    g34: LineSegment StartX=-49.19 StartY=40.5 StartZ=0 EndX=-18.2337 EndY=40.5 EndZ=0
    g35: LineSegment StartX=-49.19 StartY=37.5 StartZ=0 EndX=-18.23 EndY=37.5 EndZ=0
    g36: LineSegment StartX=-49.19 StartY=34.5 StartZ=0 EndX=-18.2337 EndY=34.5 EndZ=0
    g37: LineSegment StartX=-49.19 StartY=31.5 StartZ=0 EndX=-18.23 EndY=31.5 EndZ=0
    g38: LineSegment StartX=-49.19 StartY=28.75 StartZ=0 EndX=-16.2837 EndY=28.75 EndZ=0
    g39: LineSegment StartX=-49.19 StartY=25.75 StartZ=0 EndX=-16.28 EndY=25.75 EndZ=0
    g40: LineSegment StartX=-49.19 StartY=23 StartZ=0 EndX=-11.49 EndY=23 EndZ=0
    g41: LineSegment StartX=-49.19 StartY=20 StartZ=0 EndX=-11.49 EndY=20 EndZ=0
    g42: LineSegment StartX=-49.19 StartY=17.25 StartZ=0 EndX=-1.5 EndY=17.25 EndZ=0
    g43: LineSegment StartX=-49.19 StartY=14.25 StartZ=0 EndX=-1.5 EndY=14.25 EndZ=0
    g44: LineSegment StartX=-49.19 StartY=11.5 StartZ=0 EndX=-1.5 EndY=11.5 EndZ=0
    g45: LineSegment StartX=-49.19 StartY=8.5 StartZ=0 EndX=-1.5 EndY=8.5 EndZ=0
    g46: LineSegment StartX=-49.19 StartY=5.75 StartZ=0 EndX=-1.5 EndY=5.75 EndZ=0
    g47: LineSegment StartX=-49.19 StartY=2.75 StartZ=0 EndX=-1.5 EndY=2.75 EndZ=0
  constraints (120):
    c: Vertical(g0)
    c: Distance(g0) = 3
    c: Block(g0)
    c: Vertical(g1)
    c: Distance(g1) = 3
    c: Vertical(g2)
    c: Equal(g0,g2) = 3
    c: Block(g2)
    c: Vertical(g3)
    c: Equal(g1,g3) = 3
    c: Vertical(g4)
    c: Equal(g0,g4) = 3
    c: Block(g4)
    c: Vertical(g5)
    c: Equal(g1,g5) = 3
    c: Vertical(g6)
    c: Equal(g0,g6) = 3
    c: Block(g6)
    c: Vertical(g7)
    c: Equal(g1,g7) = 3
    c: Vertical(g8)
    c: Equal(g0,g8) = 3
    c: Block(g8)
    c: Vertical(g9)
    c: Equal(g1,g9) = 3
    c: Vertical(g10)
    c: Equal(g0,g10) = 3
    c: Block(g10)
    c: Vertical(g11)
    c: Equal(g1,g11) = 3
    c: Block(g12)
    c: Block(g13)
    c: Block(g14)
    c: Block(g15)
    c: Block(g16)
    c: Block(g17)
    c: Block(g18)
    c: Block(g19)
    c: Block(g20)
    c: Block(g21)
    c: Block(g22)
    c: Block(g23)
    c: Block(g11)
    c: Block(g9)
    c: Block(g7)
    c: Block(g5)
    c: Block(g3)
    c: Block(g1)
    c: Coincident(g24,g0)
    c: Coincident(g24,g12)
    c: Horizontal(g24)
    c: Coincident(g25,g0)
    c: Coincident(g25,g12)
    c: Horizontal(g25)
    c: Coincident(g26,g1)
    c: Coincident(g26,g13)
    c: Horizontal(g26)
    c: Coincident(g27,g1)
    c: Coincident(g27,g13)
    c: Horizontal(g27)
    c: Coincident(g28,g2)
    c: Coincident(g28,g14)
    c: Horizontal(g28)
    c: Coincident(g29,g2)
    c: Coincident(g29,g14)
    c: Horizontal(g29)
    c: Coincident(g30,g3)
    c: Coincident(g30,g15)
    c: Horizontal(g30)
    c: Coincident(g31,g3)
    c: Coincident(g31,g15)
    c: Horizontal(g31)
    c: Coincident(g32,g4)
    c: Coincident(g32,g16)
    c: Horizontal(g32)
    c: Coincident(g33,g4)
    c: Coincident(g33,g16)
    c: Horizontal(g33)
    c: Coincident(g34,g5)
    c: Coincident(g34,g17)
    c: Horizontal(g34)
    c: Coincident(g35,g5)
    c: Coincident(g35,g17)
    c: Horizontal(g35)
    c: Coincident(g36,g6)
    c: Coincident(g36,g19)
    c: Horizontal(g36)
    c: Coincident(g37,g6)
    c: Coincident(g37,g19)
    c: Horizontal(g37)
    c: Coincident(g38,g7)
    c: Coincident(g38,g18)
    c: Horizontal(g38)
    c: Coincident(g39,g7)
    c: Coincident(g39,g18)
    c: Horizontal(g39)
    c: Coincident(g40,g8)
    c: Coincident(g40,g20)
    c: Horizontal(g40)
    c: Coincident(g41,g8)
    c: Coincident(g41,g20)
    c: Horizontal(g41)
    c: Coincident(g42,g9)
    c: Coincident(g42,g23)
    c: Horizontal(g42)
    c: Coincident(g43,g9)
    c: Coincident(g43,g23)
    c: Horizontal(g43)
    c: Coincident(g44,g10)
    c: Coincident(g44,g22)
    c: Horizontal(g44)
    c: Coincident(g45,g10)
    c: Coincident(g45,g22)
    c: Horizontal(g45)
    c: Coincident(g46,g11)
    c: Coincident(g46,g21)
    c: Horizontal(g46)
    c: Coincident(g47,g11)
    c: Coincident(g47,g21)
    c: Horizontal(g47)
FEATURE [Part::Extrusion] Extrude061
  Base = -> Sketch070
  Dir = (1,0,0)
  DirMode = 2
  FaceMakerClass = Part::FaceMakerBullseye
  LengthFwd = 23
  LengthRev = 0
  Placement = pos=(-19,0,0) rot=(0,0,1;0rad)
  Solid = true
  Symmetric = false
FEATURE [Part::Fillet] Fillet052  label="removeToCreateVentalationHoles002"
  Base = -> Extrude061
  Edges = <same value as first occurrence — deduplicated (x6 in doc)>
  Placement = pos=(7,0.02,0) rot=(0,0,1;0rad)
FEATURE [Part::MultiFuse] Fusion130  label="bottom013"
  Shapes = -> [Cut054,Cut034]
FEATURE [Part::Cut] Cut055
  Base = -> Fusion130
  Tool = -> Fillet052
FEATURE [Part::Cylinder] Cylinder054
  Angle = 360
  AttacherType = Attacher::AttachEngine3D
  Height = 20
  Placement = pos=(0,0,36.15) rot=(0,0,1;0rad)
  Radius = 4
FEATURE [Sketcher::SketchObject] Sketch071  label="bottomSketch002"
  FullyConstrained = true
  sketch-geometry (32):
    g0: LineSegment StartX=3.3 StartY=-6.03275e-07 StartZ=0 EndX=98 EndY=-6.03275e-07 EndZ=0
    g1: ArcOfCircle CenterX=98 CenterY=19 CenterZ=0 NormalX=0 NormalY=0 NormalZ=1 AngleXU=0 Radius=19 StartAngle=4.71239 EndAngle=5.71103
    g2: LineSegment StartX=6.3 StartY=8 StartZ=0 EndX=3.3 EndY=8 EndZ=0
    g3: LineSegment StartX=3.3 StartY=8 StartZ=0 EndX=3.3 EndY=-6.03275e-07 EndZ=0
    g4: ArcOfCircle CenterX=8.3 CenterY=5 CenterZ=0 NormalX=0 NormalY=0 NormalZ=1 AngleXU=0 Radius=2 StartAngle=3.14159 EndAngle=4.71239
    g5: LineSegment StartX=6.3 StartY=8 StartZ=0 EndX=6.3 EndY=5 EndZ=0
    g6: ArcOfCircle CenterX=98 CenterY=19 CenterZ=0 NormalX=0 NormalY=0 NormalZ=1 AngleXU=0 Radius=12.7 StartAngle=4.71239 EndAngle=6.28319
    g7: LineSegment StartX=94.7 StartY=3 StartZ=0 EndX=8.3 EndY=3 EndZ=0
    g8-g12: Circle x5 (B-spline internal-alignment scaffolding for g13; pole/knot coordinates omitted)
    g13: BSplineCurve PolesCount=5 KnotsCount=3 Degree=3 IsPeriodic=0
    g14: GeomPoint X=98 Y=6.3 Z=0
    g15: GeomPoint X=96.3938 Y=4.71946 Z=0
    g16: GeomPoint X=94.7 Y=3 Z=0
    g17-g23: Circle x7 (B-spline internal-alignment scaffolding for g24; pole/knot coordinates omitted)
    g24: BSplineCurve PolesCount=7 KnotsCount=5 Degree=3 IsPeriodic=0
    g25-g29: GeomPoint x5 (B-spline internal-alignment scaffolding for g24; pole/knot coordinates omitted)
    g30: ArcOfCircle CenterX=98 CenterY=19 CenterZ=0 NormalX=0 NormalY=0 NormalZ=1 AngleXU=0 Radius=15.7 StartAngle=5.81226 EndAngle=6.28319
    g31: LineSegment StartX=110.7 StartY=19 StartZ=0 EndX=113.7 EndY=19 EndZ=0
  constraints (41):
    c: Horizontal(g0)
    c: Coincident(g1,g0)
    c: Block(g1)
    c: Horizontal(g2)
    c: Distance(g2) = 3
    c: Coincident(g3,g2)
    c: Vertical(g3)
    c: Coincident(g3,g0)
    c: Block(g4)
    c: Block(g2)
    c: Coincident(g5,g2)
    c: Coincident(g5,g4)
    c: Vertical(g5)
    c: Coincident(g6,g1)
    c: Block(g6)
    c: Coincident(g7,g4)
    c: Horizontal(g7)
    c: Block(g0)
    c: Block(g7)
    c: Block(g3)
    c: Coincident(g13,g6)
    c: Weight(g8) = 1
    c: Equal(g8, g9-g12) x4
    c: Coincident(g13,g7)
    c: InternalAlignment(g8-g12 -> g13) x5
    c: InternalAlignment(g14,g13)
    c: InternalAlignment(g15,g13)
    c: InternalAlignment(g16,g13)
    c: Block(g13)
    c: Weight(g17) = 1
    c: Equal(g17, g18-g23) x6
    c: Coincident(g24,g1)
    c: InternalAlignment(g17-g23 -> g24) x7
    c: InternalAlignment(g25-g29 -> g24) x5
    c: Block(g24)
    c: Coincident(g30,g24)
    c: Coincident(g31,g6)
    c: Coincident(g31,g30)
    c: Horizontal(g31)
    c: Block(g31)
    c: Block(g30)
FEATURE [Part::Extrusion] Extrude062  label="bottom014"
  Base = -> Sketch071
  Dir = (0,0,1)
  DirMode = 2
  FaceMakerClass = Part::FaceMakerBullseye
  LengthFwd = 71.4
  LengthRev = 0
  Placement = pos=(0,0,0.3) rot=(0,0,1;0rad)
  Solid = true
  Symmetric = false
FEATURE [Part::Fillet] Fillet054
  Base = -> Extrude062
  Edges = 1 edges r=2.4: [Edge17]
FEATURE [Part::Fillet] Fillet055  label="bottom015"
  Base = -> Fillet054
  Edges = 1 edges r=2.4: [Edge36]
FEATURE [Part::Cylinder] Cylinder055
  Angle = 360
  AttacherType = Attacher::AttachEngine3D
  Height = 10
  Placement = pos=(0,0,36.15) rot=(0,0,1;0rad)
  Radius = 4
FEATURE [Part::MultiFuse] Fusion131  label="removeToCreateHoleForPlugHousing002"
  Placement = pos=(70,19,36.15) rot=(0,1,0;1.5708rad)
  Shapes = -> [Cylinder054,Cylinder055]
FEATURE [Part::Cut] Cut056  label="Bottom001"
  Base = -> Fillet055
  Placement = pos=(9,0,0) rot=(0,0,1;0rad)
  Tool = -> Fusion131
FEATURE [Part::Cut] Cut057
  Base = -> Cut055
  Tool = -> Cut056
FEATURE [Sketcher::SketchObject] Sketch072  label="topSketch021"
  FullyConstrained = true
  sketch-geometry (4):
    g0: ArcOfCircle CenterX=105 CenterY=19 CenterZ=0 NormalX=0 NormalY=0 NormalZ=1 AngleXU=0 Radius=20.6155 StartAngle=5.54125 EndAngle=6.28319
    g1: ArcOfCircle CenterX=105 CenterY=19 CenterZ=0 NormalX=0 NormalY=0 NormalZ=1 AngleXU=0 Radius=13 StartAngle=5.54125 EndAngle=6.28319
    g2: LineSegment StartX=118 StartY=19 StartZ=0 EndX=125.616 EndY=19 EndZ=0
    g3: LineSegment StartX=114.583 StartY=10.2157 StartZ=0 EndX=120.197 EndY=5.06982 EndZ=0
  constraints (7):
    c: Block(g0)
    c: Block(g1)
    c: Coincident(g2,g1)
    c: Coincident(g2,g0)
    c: Horizontal(g2)
    c: Coincident(g3,g1)
    c: Coincident(g3,g0)
FEATURE [Part::Extrusion] Extrude063  label="bottomPlugHousingBit003"
  Base = -> Sketch072
  Dir = (0,0,1)
  DirMode = 2
  FaceMakerClass = Part::FaceMakerBullseye
  LengthFwd = 72
  LengthRev = 0
  Solid = true
  Symmetric = false
FEATURE [Part::Cylinder] Cylinder056
  Angle = 360
  AttacherType = Attacher::AttachEngine3D
  Height = 20
  Placement = pos=(0,0,36.15) rot=(0,0,1;0rad)
  Radius = 14.3
FEATURE [Part::Cylinder] Cylinder057
  Angle = 360
  AttacherType = Attacher::AttachEngine3D
  Height = 10
  Placement = pos=(0,0,36.15) rot=(0,0,1;0rad)
  Radius = 4
FEATURE [Part::Box] Box034  label="removeToCreteHoleForPlugHousing047"
  AttacherType = Attacher::AttachEngine3D
  Height = 28.6
  Length = 20
  Placement = pos=(106.15,0,21.7) rot=(0,0,1;0rad)
  Width = 19
FEATURE [Part::Cylinder] Cylinder058
  Angle = 360
  AttacherType = Attacher::AttachEngine3D
  Height = 20
  Placement = pos=(0,0,36.15) rot=(0,0,1;0rad)
  Radius = 14.3
FEATURE [Part::Cylinder] Cylinder059
  Angle = 360
  AttacherType = Attacher::AttachEngine3D
  Height = 10
  Placement = pos=(0,0,36.15) rot=(0,0,1;0rad)
  Radius = 4
FEATURE [Part::MultiFuse] Fusion134  label="removeToCreteHoleForPlugHousing046"
  Placement = pos=(70,19,36) rot=(0,1,0;1.5708rad)
  Shapes = -> [Cylinder058,Cylinder059]
FEATURE [Part::Cylinder] Cylinder060
  Angle = 360
  AttacherType = Attacher::AttachEngine3D
  Height = 20
  Placement = pos=(0,0,36.15) rot=(0,0,1;0rad)
  Radius = 14
FEATURE [Part::Cylinder] Cylinder061
  Angle = 360
  AttacherType = Attacher::AttachEngine3D
  Height = 10
  Placement = pos=(0,0,36.15) rot=(0,0,1;0rad)
  Radius = 4
FEATURE [Part::MultiFuse] Fusion135  label="removeToCreteHoleForPlugHousing048"
  Placement = pos=(70,19,36) rot=(0,1,0;1.5708rad)
  Shapes = -> [Cylinder060,Cylinder061]
FEATURE [Part::Box] Box035  label="removeToCreteHoleForPlugHousing049"
  AttacherType = Attacher::AttachEngine3D
  Height = 28.6
  Length = 20
  Placement = pos=(106.15,0,21.7) rot=(0,0,1;0rad)
  Width = 19
FEATURE [Part::MultiFuse] Fusion133  label="removeToCreteHoleForPlugHousing045"
  Placement = pos=(0,0,-28.3) rot=(0,0,1;0rad)
  Shapes = -> [Box035,Fusion134]
FEATURE [Part::MultiFuse] Fusion138  label="removeToCreteHoleForPlugHousing051"
  Placement = pos=(70,19,36) rot=(0,1,0;1.5708rad)
  Shapes = -> [Cylinder056,Cylinder057]
FEATURE [Part::MultiFuse] Fusion137  label="removeToCreteHoleForPlugHousing050"
  Placement = pos=(0,0,28.3) rot=(0,0,1;0rad)
  Shapes = -> [Box034,Fusion138]
FEATURE [Part::MultiFuse] Fusion132  label="removeToCreatePlugHousingBottomBit002"
  Shapes = -> [Fusion133,Fusion137]
FEATURE [Part::MultiFuse] Fusion136  label="removeToCreatePlugHousingBottomBit003"
  Shapes = -> [Fusion135,Fusion132]
FEATURE [Part::Cut] Cut058  label="bottomPlugHousingBit002"
  Base = -> Extrude063
  Placement = pos=(-0.09,0,0) rot=(0,0,1;0rad)
  Tool = -> Fusion136
FEATURE [Sketcher::SketchObject] Sketch073  label="bottomSketch003"
  FullyConstrained = true
  sketch-geometry (45):
    g0: LineSegment StartX=6.29999 StartY=8 StartZ=0 EndX=3.29999 EndY=8 EndZ=0
    g1: LineSegment StartX=3.29999 StartY=8 StartZ=0 EndX=3.29999 EndY=-6.03275e-07 EndZ=0
    g2: ArcOfCircle CenterX=8.29999 CenterY=5 CenterZ=0 NormalX=0 NormalY=0 NormalZ=1 AngleXU=0 Radius=2 StartAngle=3.14159 EndAngle=4.71239
    g3: LineSegment StartX=6.29999 StartY=8 StartZ=0 EndX=6.29999 EndY=5 EndZ=0
    g4: ArcOfCircle CenterX=105 CenterY=19 CenterZ=0 NormalX=0 NormalY=0 NormalZ=1 AngleXU=0 Radius=12.7 StartAngle=4.71239 EndAngle=5.94289
    g5-g11: Circle x7 (B-spline internal-alignment scaffolding for g12; pole/knot coordinates omitted)
    g12: BSplineCurve PolesCount=7 KnotsCount=5 Degree=3 IsPeriodic=0
    g13-g17: GeomPoint x5 (B-spline internal-alignment scaffolding for g12; pole/knot coordinates omitted)
    g18: ArcOfCircle CenterX=105 CenterY=19 CenterZ=0 NormalX=0 NormalY=0 NormalZ=1 AngleXU=0 Radius=15.7 StartAngle=5.81226 EndAngle=6.28319
    g19: BSplineCurve PolesCount=5 KnotsCount=3 Degree=3 IsPeriodic=0
    g20: LineSegment StartX=8.29999 StartY=3 StartZ=0 EndX=101.7 EndY=3 EndZ=0
    g21: LineSegment StartX=3.29999 StartY=-6.03275e-07 StartZ=0 EndX=105 EndY=-6.03275e-07 EndZ=0
    g22: LineSegment StartX=120.974 StartY=8.71251 StartZ=0 EndX=122.332 EndY=7.83778 EndZ=0
    g23: LineSegment StartX=105 StartY=-6.03274e-07 StartZ=0 EndX=113 EndY=-6.03274e-07 EndZ=0
    g24: ArcOfCircle CenterX=105 CenterY=19 CenterZ=0 NormalX=0 NormalY=0 NormalZ=1 AngleXU=0 Radius=20.6155 StartAngle=5.11091 EndAngle=5.71103
    g25: ArcOfCircle CenterX=117.7 CenterY=19 CenterZ=0 NormalX=0 NormalY=0 NormalZ=1 AngleXU=0 Radius=3 StartAngle=1.2e-15 EndAngle=2.10468
    g26: Circle CenterX=116.345 CenterY=16.3232 CenterZ=0 NormalX=0 NormalY=0 NormalZ=1 AngleXU=0 Radius=1
    g27: Circle CenterX=117.24 CenterY=15.7584 CenterZ=0 NormalX=0 NormalY=0 NormalZ=1 AngleXU=0 Radius=1
    g28: Circle CenterX=116.972 CenterY=14.7612 CenterZ=0 NormalX=0 NormalY=0 NormalZ=1 AngleXU=0 Radius=1
    g29: BSplineCurve PolesCount=3 KnotsCount=2 Degree=2 IsPeriodic=0
    g30: GeomPoint X=116.345 Y=16.3232 Z=0
    g31: GeomPoint X=116.972 Y=14.7612 Z=0
    g32: Circle CenterX=115.828 CenterY=17.157 CenterZ=0 NormalX=0 NormalY=0 NormalZ=1 AngleXU=0 Radius=1
    g33: Circle CenterX=115.841 CenterY=16.639 CenterZ=0 NormalX=0 NormalY=0 NormalZ=1 AngleXU=0 Radius=1
    g34: Circle CenterX=116.345 CenterY=16.3232 CenterZ=0 NormalX=0 NormalY=0 NormalZ=1 AngleXU=0 Radius=1
    g35: BSplineCurve PolesCount=3 KnotsCount=2 Degree=2 IsPeriodic=0
    g36: GeomPoint X=115.828 Y=17.157 Z=0
    g37: GeomPoint X=116.345 Y=16.3232 Z=0
    g38: LineSegment StartX=115.828 StartY=17.157 StartZ=0 EndX=115.828 EndY=20.8307 EndZ=0
    g39: Circle CenterX=115.828 CenterY=20.8307 CenterZ=0 NormalX=0 NormalY=0 NormalZ=1 AngleXU=0 Radius=1
    g40: Circle CenterX=115.831 CenterY=21.3396 CenterZ=0 NormalX=0 NormalY=0 NormalZ=1 AngleXU=0 Radius=1
    g41: Circle CenterX=116.173 CenterY=21.5825 CenterZ=0 NormalX=0 NormalY=0 NormalZ=1 AngleXU=0 Radius=1
    g42: BSplineCurve PolesCount=3 KnotsCount=2 Degree=2 IsPeriodic=0
    g43: GeomPoint X=115.828 Y=20.8307 Z=0
    g44: GeomPoint X=116.173 Y=21.5825 Z=0
  constraints (70):
    c: Horizontal(g0)
    c: Distance(g0) = 3
    c: Coincident(g1,g0)
    c: Vertical(g1)
    c: Block(g2)
    c: Block(g0)
    c: Coincident(g3,g0)
    c: Coincident(g3,g2)
    c: Vertical(g3)
    c: Block(g1)
    c: Block(g4)
    c: Coincident(g19,g4)
    c: Block(g19)
    c: Equal(g5, g6-g11) x6
    c: InternalAlignment(g5-g11 -> g12) x7
    c: InternalAlignment(g13-g17 -> g12) x5
    c: Block(g12)
    c: Coincident(g18,g12)
    c: Block(g18)
    c: Coincident(g20,g2)
    c: Coincident(g20,g19)
    c: Horizontal(g20)
    c: Distance(g20) = 93.4
    c: Coincident(g21,g1)
    c: Horizontal(g21)
    c: Distance(g21) = 101.7
    c: Horizontal(g23)
    c: Distance(g23) = 8
    c: Coincident(g24,g23)
    c: Block(g23)
    c: Coincident(g22,g24)
    c: Block(g24)
    c: Block(g22)
    c: Distance(g22) = 1.61553
    c: Coincident(g25,g18)
    c: Block(g25)
    c: Weight(g26) = 1
    c: Equal(g26,g27)
    c: Equal(g26,g28)
    c: Coincident(g29,g4)
    c: InternalAlignment(g26,g29)
    c: InternalAlignment(g27,g29)
    c: InternalAlignment(g28,g29)
    c: InternalAlignment(g30,g29)
    c: InternalAlignment(g31,g29)
    c: Block(g29)
    c: Weight(g32) = 1
    c: Equal(g32,g33)
    c: Equal(g32,g34)
    c: Coincident(g35,g29)
    c: InternalAlignment(g32,g35)
    c: InternalAlignment(g33,g35)
    c: InternalAlignment(g34,g35)
    c: InternalAlignment(g36,g35)
    c: InternalAlignment(g37,g35)
    c: Block(g35)
    c: Coincident(g38,g35)
    c: Vertical(g38)
    c: Block(g38)
    c: Coincident(g42,g38)
    c: Weight(g39) = 1
    c: Equal(g39,g40)
    c: Equal(g39,g41)
    c: Coincident(g42,g25)
    c: InternalAlignment(g39,g42)
    c: InternalAlignment(g40,g42)
    c: InternalAlignment(g41,g42)
    c: InternalAlignment(g43,g42)
    c: InternalAlignment(g44,g42)
    c: Block(g42)
FEATURE [Part::Extrusion] Extrude064  label="bottom016"
  Base = -> Sketch073
  Dir = (0,0,1)
  DirMode = 2
  FaceMakerClass = Part::FaceMakerBullseye
  LengthFwd = 71.4
  LengthRev = 0
  Placement = pos=(0,0,0.3) rot=(0,0,1;0rad)
  Solid = true
  Symmetric = false
FEATURE [Part::Revolution] Revolve157  label="removeToCreateScrewAndThreadedInsertHole063"
  Angle = 360
  Axis = (0,1,0)
  Base = (0,0,0)
  FaceMakerClass = Part::FaceMakerBullseye
  Placement = pos=(12.5,0,10) rot=(0,0,1;0rad)
  Solid = false
  Source = -> Face141
  Symmetric = false
FEATURE [Sketcher::SketchObject] Sketch074
  FullyConstrained = true
  Placement = pos=(117,19,0) rot=(0.57735,0.57735,0.57735;2.0944rad)
  sketch-geometry (48):
    g0: LineSegment StartX=-49.19 StartY=69.25 StartZ=0 EndX=-49.19 EndY=66.25 EndZ=0
    g1: LineSegment StartX=-49.19 StartY=63.5 StartZ=0 EndX=-49.19 EndY=60.5 EndZ=0
    g2: LineSegment StartX=-49.19 StartY=57.75 StartZ=0 EndX=-49.19 EndY=54.75 EndZ=0
    g3: LineSegment StartX=-49.19 StartY=52 StartZ=0 EndX=-49.19 EndY=49 EndZ=0
    g4: LineSegment StartX=-49.19 StartY=46.25 StartZ=0 EndX=-49.19 EndY=43.25 EndZ=0
    g5: LineSegment StartX=-49.19 StartY=40.5 StartZ=0 EndX=-49.19 EndY=37.5 EndZ=0
    g6: LineSegment StartX=-49.19 StartY=34.5 StartZ=0 EndX=-49.19 EndY=31.5 EndZ=0
    g7: LineSegment StartX=-49.19 StartY=28.75 StartZ=0 EndX=-49.19 EndY=25.75 EndZ=0
    g8: LineSegment StartX=-49.19 StartY=23 StartZ=0 EndX=-49.19 EndY=20 EndZ=0
    g9: LineSegment StartX=-49.19 StartY=17.25 StartZ=0 EndX=-49.19 EndY=14.25 EndZ=0
    g10: LineSegment StartX=-49.19 StartY=11.5 StartZ=0 EndX=-49.19 EndY=8.5 EndZ=0
    g11: LineSegment StartX=-49.19 StartY=5.75 StartZ=0 EndX=-49.19 EndY=2.75 EndZ=0
    g12: ArcOfCircle CenterX=-1.5 CenterY=67.75 CenterZ=0 NormalX=0 NormalY=0 NormalZ=1 AngleXU=0 Radius=1.5 StartAngle=4.71239 EndAngle=7.85398
    g13: ArcOfCircle CenterX=-1.5 CenterY=62 CenterZ=0 NormalX=0 NormalY=0 NormalZ=1 AngleXU=0 Radius=1.5 StartAngle=4.71239 EndAngle=7.85398
    g14: ArcOfCircle CenterX=-1.5 CenterY=56.25 CenterZ=0 NormalX=0 NormalY=0 NormalZ=1 AngleXU=0 Radius=1.5 StartAngle=4.71239 EndAngle=7.85398
    g15: ArcOfCircle CenterX=-11.49 CenterY=50.5 CenterZ=0 NormalX=0 NormalY=0 NormalZ=1 AngleXU=0 Radius=1.5 StartAngle=4.71239 EndAngle=7.85398
    g16: ArcOfCircle CenterX=-16.28 CenterY=44.75 CenterZ=0 NormalX=0 NormalY=0 NormalZ=1 AngleXU=0 Radius=1.5 StartAngle=4.71239 EndAngle=7.85398
    g17: ArcOfCircle CenterX=-18.2337 CenterY=39 CenterZ=0 NormalX=0 NormalY=0 NormalZ=1 AngleXU=0 Radius=1.5 StartAngle=4.71485 EndAngle=7.85398
    g18: ArcOfCircle CenterX=-16.2837 CenterY=27.25 CenterZ=0 NormalX=0 NormalY=0 NormalZ=1 AngleXU=0 Radius=1.5 StartAngle=4.71485 EndAngle=7.85398
    g19: ArcOfCircle CenterX=-18.2337 CenterY=33 CenterZ=0 NormalX=0 NormalY=0 NormalZ=1 AngleXU=0 Radius=1.5 StartAngle=4.71485 EndAngle=7.85398
    g20: ArcOfCircle CenterX=-11.49 CenterY=21.5 CenterZ=0 NormalX=0 NormalY=0 NormalZ=1 AngleXU=0 Radius=1.5 StartAngle=4.71239 EndAngle=7.85398
    g21: ArcOfCircle CenterX=-1.5 CenterY=4.25 CenterZ=0 NormalX=0 NormalY=0 NormalZ=1 AngleXU=0 Radius=1.5 StartAngle=4.71239 EndAngle=7.85398
    g22: ArcOfCircle CenterX=-1.5 CenterY=10 CenterZ=0 NormalX=0 NormalY=0 NormalZ=1 AngleXU=0 Radius=1.5 StartAngle=4.71239 EndAngle=7.85398
    g23: ArcOfCircle CenterX=-1.5 CenterY=15.75 CenterZ=0 NormalX=0 NormalY=0 NormalZ=1 AngleXU=0 Radius=1.5 StartAngle=4.71239 EndAngle=7.85398
    g24: LineSegment StartX=-49.19 StartY=69.25 StartZ=0 EndX=-1.5 EndY=69.25 EndZ=0
    g25: LineSegment StartX=-49.19 StartY=66.25 StartZ=0 EndX=-1.5 EndY=66.25 EndZ=0
    g26: LineSegment StartX=-49.19 StartY=63.5 StartZ=0 EndX=-1.5 EndY=63.5 EndZ=0
    g27: LineSegment StartX=-49.19 StartY=60.5 StartZ=0 EndX=-1.5 EndY=60.5 EndZ=0
    g28: LineSegment StartX=-49.19 StartY=57.75 StartZ=0 EndX=-1.5 EndY=57.75 EndZ=0
    g29: LineSegment StartX=-49.19 StartY=54.75 StartZ=0 EndX=-1.5 EndY=54.75 EndZ=0
    g30: LineSegment StartX=-49.19 StartY=52 StartZ=0 EndX=-11.49 EndY=52 EndZ=0
    g31: LineSegment StartX=-49.19 StartY=49 StartZ=0 EndX=-11.49 EndY=49 EndZ=0
    g32: LineSegment StartX=-49.19 StartY=46.25 StartZ=0 EndX=-16.28 EndY=46.25 EndZ=0
    g33: LineSegment StartX=-49.19 StartY=43.25 StartZ=0 EndX=-16.28 EndY=43.25 EndZ=0
    g34: LineSegment StartX=-49.19 StartY=40.5 StartZ=0 EndX=-18.2337 EndY=40.5 EndZ=0
    g35: LineSegment StartX=-49.19 StartY=37.5 StartZ=0 EndX=-18.23 EndY=37.5 EndZ=0
    g36: LineSegment StartX=-49.19 StartY=34.5 StartZ=0 EndX=-18.2337 EndY=34.5 EndZ=0
    g37: LineSegment StartX=-49.19 StartY=31.5 StartZ=0 EndX=-18.23 EndY=31.5 EndZ=0
    g38: LineSegment StartX=-49.19 StartY=28.75 StartZ=0 EndX=-16.2837 EndY=28.75 EndZ=0
    g39: LineSegment StartX=-49.19 StartY=25.75 StartZ=0 EndX=-16.28 EndY=25.75 EndZ=0
    g40: LineSegment StartX=-49.19 StartY=23 StartZ=0 EndX=-11.49 EndY=23 EndZ=0
    g41: LineSegment StartX=-49.19 StartY=20 StartZ=0 EndX=-11.49 EndY=20 EndZ=0
    g42: LineSegment StartX=-49.19 StartY=17.25 StartZ=0 EndX=-1.5 EndY=17.25 EndZ=0
    g43: LineSegment StartX=-49.19 StartY=14.25 StartZ=0 EndX=-1.5 EndY=14.25 EndZ=0
    g44: LineSegment StartX=-49.19 StartY=11.5 StartZ=0 EndX=-1.5 EndY=11.5 EndZ=0
    g45: LineSegment StartX=-49.19 StartY=8.5 StartZ=0 EndX=-1.5 EndY=8.5 EndZ=0
    g46: LineSegment StartX=-49.19 StartY=5.75 StartZ=0 EndX=-1.5 EndY=5.75 EndZ=0
    g47: LineSegment StartX=-49.19 StartY=2.75 StartZ=0 EndX=-1.5 EndY=2.75 EndZ=0
  constraints (120):
    c: Vertical(g0)
    c: Distance(g0) = 3
    c: Block(g0)
    c: Vertical(g1)
    c: Distance(g1) = 3
    c: Vertical(g2)
    c: Equal(g0,g2) = 3
    c: Block(g2)
    c: Vertical(g3)
    c: Equal(g1,g3) = 3
    c: Vertical(g4)
    c: Equal(g0,g4) = 3
    c: Block(g4)
    c: Vertical(g5)
    c: Equal(g1,g5) = 3
    c: Vertical(g6)
    c: Equal(g0,g6) = 3
    c: Block(g6)
    c: Vertical(g7)
    c: Equal(g1,g7) = 3
    c: Vertical(g8)
    c: Equal(g0,g8) = 3
    c: Block(g8)
    c: Vertical(g9)
    c: Equal(g1,g9) = 3
    c: Vertical(g10)
    c: Equal(g0,g10) = 3
    c: Block(g10)
    c: Vertical(g11)
    c: Equal(g1,g11) = 3
    c: Block(g12)
    c: Block(g13)
    c: Block(g14)
    c: Block(g15)
    c: Block(g16)
    c: Block(g17)
    c: Block(g18)
    c: Block(g19)
    c: Block(g20)
    c: Block(g21)
    c: Block(g22)
    c: Block(g23)
    c: Block(g11)
    c: Block(g9)
    c: Block(g7)
    c: Block(g5)
    c: Block(g3)
    c: Block(g1)
    c: Coincident(g24,g0)
    c: Coincident(g24,g12)
    c: Horizontal(g24)
    c: Coincident(g25,g0)
    c: Coincident(g25,g12)
    c: Horizontal(g25)
    c: Coincident(g26,g1)
    c: Coincident(g26,g13)
    c: Horizontal(g26)
    c: Coincident(g27,g1)
    c: Coincident(g27,g13)
    c: Horizontal(g27)
    c: Coincident(g28,g2)
    c: Coincident(g28,g14)
    c: Horizontal(g28)
    c: Coincident(g29,g2)
    c: Coincident(g29,g14)
    c: Horizontal(g29)
    c: Coincident(g30,g3)
    c: Coincident(g30,g15)
    c: Horizontal(g30)
    c: Coincident(g31,g3)
    c: Coincident(g31,g15)
    c: Horizontal(g31)
    c: Coincident(g32,g4)
    c: Coincident(g32,g16)
    c: Horizontal(g32)
    c: Coincident(g33,g4)
    c: Coincident(g33,g16)
    c: Horizontal(g33)
    c: Coincident(g34,g5)
    c: Coincident(g34,g17)
    c: Horizontal(g34)
    c: Coincident(g35,g5)
    c: Coincident(g35,g17)
    c: Horizontal(g35)
    c: Coincident(g36,g6)
    c: Coincident(g36,g19)
    c: Horizontal(g36)
    c: Coincident(g37,g6)
    c: Coincident(g37,g19)
    c: Horizontal(g37)
    c: Coincident(g38,g7)
    c: Coincident(g38,g18)
    c: Horizontal(g38)
    c: Coincident(g39,g7)
    c: Coincident(g39,g18)
    c: Horizontal(g39)
    c: Coincident(g40,g8)
    c: Coincident(g40,g20)
    c: Horizontal(g40)
    c: Coincident(g41,g8)
    c: Coincident(g41,g20)
    c: Horizontal(g41)
    c: Coincident(g42,g9)
    c: Coincident(g42,g23)
    c: Horizontal(g42)
    c: Coincident(g43,g9)
    c: Coincident(g43,g23)
    c: Horizontal(g43)
    c: Coincident(g44,g10)
    c: Coincident(g44,g22)
    c: Horizontal(g44)
    c: Coincident(g45,g10)
    c: Coincident(g45,g22)
    c: Horizontal(g45)
    c: Coincident(g46,g11)
    c: Coincident(g46,g21)
    c: Horizontal(g46)
    c: Coincident(g47,g11)
    c: Coincident(g47,g21)
    c: Horizontal(g47)
FEATURE [Part::Extrusion] Extrude065
  Base = -> Sketch074
  Dir = (1,0,0)
  DirMode = 2
  FaceMakerClass = Part::FaceMakerBullseye
  LengthFwd = 23
  LengthRev = 0
  Placement = pos=(-19,0,0) rot=(0,0,1;0rad)
  Solid = true
  Symmetric = false
FEATURE [Part::Fillet] Fillet056  label="removeToCreateVentalationHoles003"
  Base = -> Extrude065
  Edges = <same value as first occurrence — deduplicated (x6 in doc)>
  Placement = pos=(7,0.02,0) rot=(0,0,1;0rad)
FEATURE [Part::Revolution] Revolve158  label="removeToCreateScrewAndThreadedInsertHole065"
  Angle = 360
  Axis = (0,1,0)
  Base = (0,0,0)
  FaceMakerClass = Part::FaceMakerBullseye
  Placement = pos=(12.5,0,62) rot=(0,0,1;0rad)
  Solid = false
  Source = -> Face146
  Symmetric = false
FEATURE [Part::Revolution] Revolve159  label="removeToCreateScrewAndThreadedInsertHole066"
  Angle = 360
  Axis = (0,1,0)
  Base = (0,0,0)
  FaceMakerClass = Part::FaceMakerBullseye
  Placement = pos=(89.5,0,68.5) rot=(0,0,1;0rad)
  Solid = false
  Source = -> Face143
  Symmetric = false
FEATURE [Part::Revolution] Revolve160  label="removeToCreateScrewAndThreadedInsertHole067"
  Angle = 360
  Axis = (0,1,0)
  Base = (0,0,0)
  FaceMakerClass = Part::FaceMakerBullseye
  Placement = pos=(89.5,0,3.5) rot=(0,0,1;0rad)
  Solid = false
  Source = -> Face142
  Symmetric = false
FEATURE [Part::Revolution] Revolve161  label="removeToCreateScrewAndThreadedInsertHole068"
  Angle = 360
  Axis = (0,1,0)
  Base = (0,0,0)
  FaceMakerClass = Part::FaceMakerBullseye
  Placement = pos=(109.5,4.7,3.5) rot=(0,0,1;0rad)
  Solid = false
  Source = -> Face145
  Symmetric = false
FEATURE [Part::Revolution] Revolve162  label="removeToCreateScrewAndThreadedInsertHole069"
  Angle = 360
  Axis = (0,1,0)
  Base = (0,0,0)
  FaceMakerClass = Part::FaceMakerBullseye
  Placement = pos=(109.5,4.7,68.5) rot=(0,0,1;0rad)
  Solid = false
  Source = -> Face144
  Symmetric = false
FEATURE [Part::MultiFuse] Fusion141  label="removeToCreateScrewAndThreadedInsertHole064"
  Shapes = -> [Revolve162,Revolve161,Revolve160,Revolve159,Revolve158,Revolve157]
FEATURE [Part::Cylinder] Cylinder062
  Angle = 360
  AttacherType = Attacher::AttachEngine3D
  Height = 20
  Placement = pos=(0,0,36.15) rot=(0,0,1;0rad)
  Radius = 14
FEATURE [Part::Cylinder] Cylinder063
  Angle = 360
  AttacherType = Attacher::AttachEngine3D
  Height = 10
  Placement = pos=(0,0,36.15) rot=(0,0,1;0rad)
  Radius = 4
FEATURE [Part::MultiFuse] Fusion139  label="removeToCreteHoleForPlugHousing052"
  Placement = pos=(70,19,36) rot=(0,1,0;1.5708rad)
  Shapes = -> [Cylinder062,Cylinder063]
FEATURE [Part::Cut] Cut060  label="bottom017"
  Base = -> Extrude064
  Tool = -> Fusion139
FEATURE [Part::Cut] Cut061  label="bottom019"
  Base = -> Cut060
  Tool = -> Fusion141
FEATURE [Part::MultiFuse] Fusion140  label="bottom018"
  Shapes = -> [Cut061,Cut058]
FEATURE [Part::Cut] Cut059  label="bottom020"
  Base = -> Fusion140
  Tool = -> Fillet056
FEATURE [Part::Box] Box036  label="Cube021"
  AttacherType = Attacher::AttachEngine3D
  Height = 80
  Length = 26
  Placement = pos=(0,-1,-5) rot=(0,0,1;0rad)
  Width = 11
FEATURE [Part::Cut] Cut062  label="removeFromBottom002"
  Base = -> Cut057
  Tool = -> Box036
FEATURE [Part::Cut] Cut063
  Base = -> Cut059
  Tool = -> Cut062
FEATURE [Part::Cut] Cut064  label="pcbStands"
  Base = -> Fusion095
  Tool = -> Fusion127
FEATURE [Sketcher::SketchObject] Sketch075  label="topSketch022"
  FullyConstrained = true
  sketch-geometry (6):
    g0: LineSegment StartX=19 StartY=38 StartZ=0 EndX=117 EndY=38 EndZ=0
    g1: ArcOfCircle CenterX=19 CenterY=19 CenterZ=0 NormalX=0 NormalY=0 NormalZ=1 AngleXU=0 Radius=19 StartAngle=1.5708 EndAngle=3.14159
    g2: LineSegment StartX=117 StartY=38 StartZ=0 EndX=117 EndY=19 EndZ=0
    g3: LineSegment StartX=98 StartY=1.0161e-12 StartZ=0 EndX=5.22862e-06 EndY=1.0161e-12 EndZ=0
    g4: LineSegment StartX=5.22862e-06 StartY=19 StartZ=0 EndX=5.22862e-06 EndY=1.0161e-12 EndZ=0
    g5: ArcOfCircle CenterX=98 CenterY=19 CenterZ=0 NormalX=0 NormalY=0 NormalZ=1 AngleXU=0 Radius=19 StartAngle=4.71239 EndAngle=6.28319
  constraints (16):
    c: Horizontal(g0)
    c: Distance(g0) = 98
    c: Coincident(g1,g0)
    c: Block(g1)
    c: Coincident(g2,g0)
    c: Vertical(g2)
    c: Distance(g2) = 19
    c: Horizontal(g3)
    c: Coincident(g4,g1)
    c: Vertical(g4)
    c: Coincident(g3,g4)
    c: Block(g3)
    c: Coincident(g5,g2)
    c: Coincident(g5,g3)
    c: Block(g0)
    c: Block(g5)
FEATURE [Part::Extrusion] Extrude067  label="sideB003"
  Base = -> Sketch075
  Dir = (0,0,1)
  DirMode = 2
  FaceMakerClass = Part::FaceMakerBullseye
  LengthFwd = 3
  LengthRev = 0
  Placement = pos=(0,0,71.7) rot=(0,0,1;0rad)
  Solid = true
  Symmetric = false
FEATURE [Sketcher::SketchObject] Sketch076  label="topSketch023"
  FullyConstrained = true
  sketch-geometry (6):
    g0: LineSegment StartX=19 StartY=38 StartZ=0 EndX=117 EndY=38 EndZ=0
    g1: ArcOfCircle CenterX=19 CenterY=19 CenterZ=0 NormalX=0 NormalY=0 NormalZ=1 AngleXU=0 Radius=19 StartAngle=1.5708 EndAngle=3.14159
    g2: LineSegment StartX=117 StartY=38 StartZ=0 EndX=117 EndY=19 EndZ=0
    g3: LineSegment StartX=98 StartY=1.0161e-12 StartZ=0 EndX=5.22862e-06 EndY=1.0161e-12 EndZ=0
    g4: LineSegment StartX=5.22862e-06 StartY=19 StartZ=0 EndX=5.22862e-06 EndY=1.0161e-12 EndZ=0
    g5: ArcOfCircle CenterX=98 CenterY=19 CenterZ=0 NormalX=0 NormalY=0 NormalZ=1 AngleXU=0 Radius=19 StartAngle=4.71239 EndAngle=6.28319
  constraints (16):
    c: Horizontal(g0)
    c: Distance(g0) = 98
    c: Coincident(g1,g0)
    c: Block(g1)
    c: Coincident(g2,g0)
    c: Vertical(g2)
    c: Distance(g2) = 19
    c: Horizontal(g3)
    c: Coincident(g4,g1)
    c: Vertical(g4)
    c: Coincident(g3,g4)
    c: Block(g3)
    c: Coincident(g5,g2)
    c: Coincident(g5,g3)
    c: Block(g0)
    c: Block(g5)
FEATURE [Part::Extrusion] Extrude066  label="sideA003"
  Base = -> Sketch076
  Dir = (0,0,1)
  DirMode = 2
  FaceMakerClass = Part::FaceMakerBullseye
  LengthFwd = 3
  LengthRev = 0
  Placement = pos=(0,0,-2.7) rot=(0,0,1;0rad)
  Solid = true
  Symmetric = false
FEATURE [Part::MultiFuse] Fusion142  label="removeFromBottom003"
  Placement = pos=(2,0,0) rot=(0,0,1;0rad)
  Shapes = -> [Extrude066,Extrude067]
FEATURE [Part::Cut] Cut065  label="screwRetainers002"
  Base = -> Fusion096
  Tool = -> Fusion142
FEATURE [Sketcher::SketchObject] Sketch077
  FullyConstrained = true
  Placement = pos=(117,19,0) rot=(0.57735,0.57735,0.57735;2.0944rad)
  sketch-geometry (8):
    g0: LineSegment StartX=-49.19 StartY=63.5 StartZ=0 EndX=-49.19 EndY=60.5 EndZ=0
    g1: LineSegment StartX=-49.19 StartY=11.5 StartZ=0 EndX=-49.19 EndY=8.5 EndZ=0
    g2: ArcOfCircle CenterX=-1.5 CenterY=62 CenterZ=0 NormalX=0 NormalY=0 NormalZ=1 AngleXU=0 Radius=1.5 StartAngle=4.71239 EndAngle=7.85398
    g3: ArcOfCircle CenterX=-1.5 CenterY=10 CenterZ=0 NormalX=0 NormalY=0 NormalZ=1 AngleXU=0 Radius=1.5 StartAngle=4.71239 EndAngle=7.85398
    g4: LineSegment StartX=-49.19 StartY=63.5 StartZ=0 EndX=-1.5 EndY=63.5 EndZ=0
    g5: LineSegment StartX=-49.19 StartY=60.5 StartZ=0 EndX=-1.5 EndY=60.5 EndZ=0
    g6: LineSegment StartX=-49.19 StartY=11.5 StartZ=0 EndX=-1.5 EndY=11.5 EndZ=0
    g7: LineSegment StartX=-49.19 StartY=8.5 StartZ=0 EndX=-1.5 EndY=8.5 EndZ=0
  constraints (19):
    c: Vertical(g0)
    c: Distance(g0) = 3
    c: Vertical(g1)
    c: Block(g1)
    c: Block(g2)
    c: Block(g3)
    c: Block(g0)
    c: Coincident(g4,g0)
    c: Coincident(g4,g2)
    c: Horizontal(g4)
    c: Coincident(g5,g0)
    c: Coincident(g5,g2)
    c: Horizontal(g5)
    c: Coincident(g6,g1)
    c: Coincident(g6,g3)
    c: Horizontal(g6)
    c: Coincident(g7,g1)
    c: Coincident(g7,g3)
    c: Horizontal(g7)
FEATURE [Part::Extrusion] Extrude068
  Base = -> Sketch077
  Dir = (1,0,0)
  DirMode = 2
  FaceMakerClass = Part::FaceMakerBullseye
  LengthFwd = 10
  LengthRev = 0
  Solid = true
  Symmetric = false
FEATURE [Part::Fillet] Fillet057  label="removeFromtMoreFrontCaseScrewRetainers002"
  Base = -> Extrude068
  Edges = 4 edges r=1.49: [Edge6,Edge11,Edge18,Edge23]
  Placement = pos=(-12,0,0) rot=(0,0,1;0rad)
FEATURE [Sketcher::SketchObject] Sketch078
  FullyConstrained = true
  Placement = pos=(117,19,0) rot=(0.57735,0.57735,0.57735;2.0944rad)
  sketch-geometry (8):
    g0: LineSegment StartX=-49.19 StartY=69.25 StartZ=0 EndX=-49.19 EndY=66.25 EndZ=0
    g1: LineSegment StartX=-49.19 StartY=5.75 StartZ=0 EndX=-49.19 EndY=2.75 EndZ=0
    g2: ArcOfCircle CenterX=-1.5 CenterY=67.75 CenterZ=0 NormalX=0 NormalY=0 NormalZ=1 AngleXU=0 Radius=1.5 StartAngle=4.71239 EndAngle=7.85398
    g3: ArcOfCircle CenterX=-1.5 CenterY=4.25 CenterZ=0 NormalX=0 NormalY=0 NormalZ=1 AngleXU=0 Radius=1.5 StartAngle=4.71239 EndAngle=7.85398
    g4: LineSegment StartX=-49.19 StartY=69.25 StartZ=0 EndX=-1.5 EndY=69.25 EndZ=0
    g5: LineSegment StartX=-49.19 StartY=66.25 StartZ=0 EndX=-1.5 EndY=66.25 EndZ=0
    g6: LineSegment StartX=-49.19 StartY=5.75 StartZ=0 EndX=-1.5 EndY=5.75 EndZ=0
    g7: LineSegment StartX=-49.19 StartY=2.75 StartZ=0 EndX=-1.5 EndY=2.75 EndZ=0
  constraints (19):
    c: Vertical(g0)
    c: Distance(g0) = 3
    c: Block(g0)
    c: Vertical(g1)
    c: Block(g2)
    c: Block(g3)
    c: Block(g1)
    c: Coincident(g4,g0)
    c: Coincident(g4,g2)
    c: Horizontal(g4)
    c: Coincident(g5,g0)
    c: Coincident(g5,g2)
    c: Horizontal(g5)
    c: Coincident(g6,g1)
    c: Coincident(g6,g3)
    c: Horizontal(g6)
    c: Coincident(g7,g1)
    c: Coincident(g7,g3)
    c: Horizontal(g7)
FEATURE [Part::Extrusion] Extrude069
  Base = -> Sketch078
  Dir = (1,0,0)
  DirMode = 2
  FaceMakerClass = Part::FaceMakerBullseye
  LengthFwd = 10
  LengthRev = 0
  Solid = true
  Symmetric = false
FEATURE [Part::Fillet] Fillet058  label="removeFromtMoreFrontCaseScrewRetainers003"
  Base = -> Extrude069
  Edges = 4 edges r=1.49: [Edge6,Edge11,Edge18,Edge23]
  Placement = pos=(-4,0,0) rot=(0,0,1;0rad)
FEATURE [Part::Cut] Cut066
  Base = -> Cut065
  Tool = -> Fillet058
FEATURE [Part::Cut] Cut067  label="screwPillars"
  Base = -> Cut066
  Tool = -> Fillet057
FEATURE [Part::MultiFuse] Fusion143  label="bottom021"
  Shapes = -> [Cut031,Cut063]
FEATURE [Part::Cylinder] Cylinder
  Angle = 360
  AttacherType = Attacher::AttachEngine3D
  Height = 10
  Placement = pos=(20.65,12,4.68) rot=(1,0,0;1.5708rad)
  Radius = 2
FEATURE [Part::Cylinder] Cylinder064
  Angle = 360
  AttacherType = Attacher::AttachEngine3D
  Height = 10
  Placement = pos=(20.65,12,67.38) rot=(1,0,0;1.5708rad)
  Radius = 2
FEATURE [Part::Cylinder] Cylinder065
  Angle = 360
  AttacherType = Attacher::AttachEngine3D
  Height = 10
  Placement = pos=(77.15,12,67.38) rot=(1,0,0;1.5708rad)
  Radius = 2
FEATURE [Part::Cylinder] Cylinder066
  Angle = 360
  AttacherType = Attacher::AttachEngine3D
  Height = 10
  Placement = pos=(77.15,12,4.68) rot=(1,0,0;1.5708rad)
  Radius = 2
FEATURE [Part::MultiFuse] Fusion144  label="removeFromThreadedInsertHousing"
  Shapes = -> [Cylinder065,Cylinder064,Cylinder,Cylinder066]
FEATURE [Part::Cut] Cut068  label="pcbStands001"
  Base = -> Cut064
  Tool = -> Fusion144
FEATURE [Part::MultiFuse] Fusion145
  Shapes = -> [Cut068,Fusion143]
FEATURE [Part::MultiFuse] Fusion146
  Shapes = -> [Fusion145]
FEATURE [Part::MultiFuse] Fusion147  label="bottom022"
  Shapes = -> [Cut067,Fusion146]
FEATURE [Part::MultiFuse] Fusion148  label="casePillars005"
  Shapes = -> [Cut047,Fusion092]
FEATURE [Part::MultiFuse] Fusion149  label="bottom023"
  Shapes = -> [Fusion124,Fusion113,Fusion147]
FEATURE [Part::MultiFuse] Fusion150  label="topBits"
  Shapes = -> [Cut025,Fusion148,Cut030,Fillet034]
FEATURE [Part::Feature] Face149 .. Face152  x4 (patterned run collapsed; names and placements below)
  shape: bbox 3.2 x 1.5 x 2e-07 mm, 1 faces, 0 solids (baked)
FEATURE [Part::Feature] Face153
  shape: bbox 3.6 x 3.2 x 2e-07 mm, 1 faces, 0 solids (baked)
FEATURE [Part::Feature] Face154
  shape: bbox 3.6 x 3.2 x 2e-07 mm, 1 faces, 0 solids (baked)
FEATURE [Sketcher::SketchObject] Sketch079  label="topSketch024"
  FullyConstrained = true
  sketch-geometry (6):
    g0: LineSegment StartX=19 StartY=38 StartZ=0 EndX=117 EndY=38 EndZ=0
    g1: ArcOfCircle CenterX=19 CenterY=19 CenterZ=0 NormalX=0 NormalY=0 NormalZ=1 AngleXU=0 Radius=19 StartAngle=1.5708 EndAngle=3.14159
    g2: LineSegment StartX=117 StartY=38 StartZ=0 EndX=117 EndY=19 EndZ=0
    g3: LineSegment StartX=98 StartY=1.0161e-12 StartZ=0 EndX=5.22862e-06 EndY=1.0161e-12 EndZ=0
    g4: LineSegment StartX=5.22862e-06 StartY=19 StartZ=0 EndX=5.22862e-06 EndY=1.0161e-12 EndZ=0
    g5: ArcOfCircle CenterX=98 CenterY=19 CenterZ=0 NormalX=0 NormalY=0 NormalZ=1 AngleXU=0 Radius=19 StartAngle=4.71239 EndAngle=6.28319
  constraints (16):
    c: Horizontal(g0)
    c: Distance(g0) = 98
    c: Coincident(g1,g0)
    c: Block(g1)
    c: Coincident(g2,g0)
    c: Vertical(g2)
    c: Distance(g2) = 19
    c: Horizontal(g3)
    c: Coincident(g4,g1)
    c: Vertical(g4)
    c: Coincident(g3,g4)
    c: Block(g3)
    c: Coincident(g5,g2)
    c: Coincident(g5,g3)
    c: Block(g0)
    c: Block(g5)
FEATURE [Sketcher::SketchObject] Sketch080  label="topSketch025"
  FullyConstrained = true
  sketch-geometry (6):
    g0: LineSegment StartX=19 StartY=38 StartZ=0 EndX=117 EndY=38 EndZ=0
    g1: ArcOfCircle CenterX=19 CenterY=19 CenterZ=0 NormalX=0 NormalY=0 NormalZ=1 AngleXU=0 Radius=19 StartAngle=1.5708 EndAngle=3.14159
    g2: LineSegment StartX=117 StartY=38 StartZ=0 EndX=117 EndY=19 EndZ=0
    g3: LineSegment StartX=98 StartY=1.0161e-12 StartZ=0 EndX=5.22862e-06 EndY=1.0161e-12 EndZ=0
    g4: LineSegment StartX=5.22862e-06 StartY=19 StartZ=0 EndX=5.22862e-06 EndY=1.0161e-12 EndZ=0
    g5: ArcOfCircle CenterX=98 CenterY=19 CenterZ=0 NormalX=0 NormalY=0 NormalZ=1 AngleXU=0 Radius=19 StartAngle=4.71239 EndAngle=6.28319
  constraints (16):
    c: Horizontal(g0)
    c: Distance(g0) = 98
    c: Coincident(g1,g0)
    c: Block(g1)
    c: Coincident(g2,g0)
    c: Vertical(g2)
    c: Distance(g2) = 19
    c: Horizontal(g3)
    c: Coincident(g4,g1)
    c: Vertical(g4)
    c: Coincident(g3,g4)
    c: Block(g3)
    c: Coincident(g5,g2)
    c: Coincident(g5,g3)
    c: Block(g0)
    c: Block(g5)
FEATURE [Part::Extrusion] Extrude070  label="sideA004"
  Base = -> Sketch080
  Dir = (0,0,1)
  DirMode = 2
  FaceMakerClass = Part::FaceMakerBullseye
  LengthFwd = 3
  LengthRev = 0
  Placement = pos=(0,0,-2.7) rot=(0,0,1;0rad)
  Solid = true
  Symmetric = false
FEATURE [Sketcher::SketchObject] Sketch081
  FullyConstrained = true
  Placement = pos=(117,19,0) rot=(0.57735,0.57735,0.57735;2.0944rad)
  sketch-geometry (8):
    g0: LineSegment StartX=-49.19 StartY=63.5 StartZ=0 EndX=-49.19 EndY=60.5 EndZ=0
    g1: LineSegment StartX=-49.19 StartY=11.5 StartZ=0 EndX=-49.19 EndY=8.5 EndZ=0
    g2: ArcOfCircle CenterX=-1.5 CenterY=62 CenterZ=0 NormalX=0 NormalY=0 NormalZ=1 AngleXU=0 Radius=1.5 StartAngle=4.71239 EndAngle=7.85398
    g3: ArcOfCircle CenterX=-1.5 CenterY=10 CenterZ=0 NormalX=0 NormalY=0 NormalZ=1 AngleXU=0 Radius=1.5 StartAngle=4.71239 EndAngle=7.85398
    g4: LineSegment StartX=-49.19 StartY=63.5 StartZ=0 EndX=-1.5 EndY=63.5 EndZ=0
    g5: LineSegment StartX=-49.19 StartY=60.5 StartZ=0 EndX=-1.5 EndY=60.5 EndZ=0
    g6: LineSegment StartX=-49.19 StartY=11.5 StartZ=0 EndX=-1.5 EndY=11.5 EndZ=0
    g7: LineSegment StartX=-49.19 StartY=8.5 StartZ=0 EndX=-1.5 EndY=8.5 EndZ=0
  constraints (19):
    c: Vertical(g0)
    c: Distance(g0) = 3
    c: Vertical(g1)
    c: Block(g1)
    c: Block(g2)
    c: Block(g3)
    c: Block(g0)
    c: Coincident(g4,g0)
    c: Coincident(g4,g2)
    c: Horizontal(g4)
    c: Coincident(g5,g0)
    c: Coincident(g5,g2)
    c: Horizontal(g5)
    c: Coincident(g6,g1)
    c: Coincident(g6,g3)
    c: Horizontal(g6)
    c: Coincident(g7,g1)
    c: Coincident(g7,g3)
    c: Horizontal(g7)
FEATURE [Part::Extrusion] Extrude071  label="sideB004"
  Base = -> Sketch079
  Dir = (0,0,1)
  DirMode = 2
  FaceMakerClass = Part::FaceMakerBullseye
  LengthFwd = 3
  LengthRev = 0
  Placement = pos=(0,0,71.7) rot=(0,0,1;0rad)
  Solid = true
  Symmetric = false
FEATURE [Part::MultiFuse] Fusion152  label="removeFromBottom004"
  Placement = pos=(2,0,0) rot=(0,0,1;0rad)
  Shapes = -> [Extrude070,Extrude071]
FEATURE [Part::Extrusion] Extrude072
  Base = -> Sketch081
  Dir = (1,0,0)
  DirMode = 2
  FaceMakerClass = Part::FaceMakerBullseye
  LengthFwd = 10
  LengthRev = 0
  Solid = true
  Symmetric = false
FEATURE [Part::Fillet] Fillet059  label="removeFromtMoreFrontCaseScrewRetainers004"
  Base = -> Extrude072
  Edges = 4 edges r=1.49: [Edge6,Edge11,Edge18,Edge23]
  Placement = pos=(-12,0,0) rot=(0,0,1;0rad)
FEATURE [Sketcher::SketchObject] Sketch082
  FullyConstrained = true
  Placement = pos=(117,19,0) rot=(0.57735,0.57735,0.57735;2.0944rad)
  sketch-geometry (8):
    g0: LineSegment StartX=-49.19 StartY=69.25 StartZ=0 EndX=-49.19 EndY=66.25 EndZ=0
    g1: LineSegment StartX=-49.19 StartY=5.75 StartZ=0 EndX=-49.19 EndY=2.75 EndZ=0
    g2: ArcOfCircle CenterX=-1.5 CenterY=67.75 CenterZ=0 NormalX=0 NormalY=0 NormalZ=1 AngleXU=0 Radius=1.5 StartAngle=4.71239 EndAngle=7.85398
    g3: ArcOfCircle CenterX=-1.5 CenterY=4.25 CenterZ=0 NormalX=0 NormalY=0 NormalZ=1 AngleXU=0 Radius=1.5 StartAngle=4.71239 EndAngle=7.85398
    g4: LineSegment StartX=-49.19 StartY=69.25 StartZ=0 EndX=-1.5 EndY=69.25 EndZ=0
    g5: LineSegment StartX=-49.19 StartY=66.25 StartZ=0 EndX=-1.5 EndY=66.25 EndZ=0
    g6: LineSegment StartX=-49.19 StartY=5.75 StartZ=0 EndX=-1.5 EndY=5.75 EndZ=0
    g7: LineSegment StartX=-49.19 StartY=2.75 StartZ=0 EndX=-1.5 EndY=2.75 EndZ=0
  constraints (19):
    c: Vertical(g0)
    c: Distance(g0) = 3
    c: Block(g0)
    c: Vertical(g1)
    c: Block(g2)
    c: Block(g3)
    c: Block(g1)
    c: Coincident(g4,g0)
    c: Coincident(g4,g2)
    c: Horizontal(g4)
    c: Coincident(g5,g0)
    c: Coincident(g5,g2)
    c: Horizontal(g5)
    c: Coincident(g6,g1)
    c: Coincident(g6,g3)
    c: Horizontal(g6)
    c: Coincident(g7,g1)
    c: Coincident(g7,g3)
    c: Horizontal(g7)
FEATURE [Part::Extrusion] Extrude073
  Base = -> Sketch082
  Dir = (1,0,0)
  DirMode = 2
  FaceMakerClass = Part::FaceMakerBullseye
  LengthFwd = 10
  LengthRev = 0
  Solid = true
  Symmetric = false
FEATURE [Part::Fillet] Fillet060  label="removeFromtMoreFrontCaseScrewRetainers005"
  Base = -> Extrude073
  Edges = 4 edges r=1.49: [Edge6,Edge11,Edge18,Edge23]
  Placement = pos=(-4,0,0) rot=(0,0,1;0rad)
FEATURE [Part::Revolution] Revolve163  label="backCaseScrewRetainer004"
  Angle = 360
  Axis = (0,1,0)
  Base = (0,0,0)
  FaceMakerClass = Part::FaceMakerBullseye
  Placement = pos=(12.5,3,62) rot=(0,0,1;0rad)
  Solid = false
  Source = -> Face149
  Symmetric = false
FEATURE [Part::Revolution] Revolve164  label="frontCaseScrewRetainer006"
  Angle = 360
  Axis = (0,1,0)
  Base = (0,0,0)
  FaceMakerClass = Part::FaceMakerBullseye
  Placement = pos=(89.5,3,68.5) rot=(0,0,1;0rad)
  Solid = false
  Source = -> Face151
  Symmetric = false
FEATURE [Part::Revolution] Revolve165  label="frontCaseScrewRetainer007"
  Angle = 360
  Axis = (0,1,0)
  Base = (0,0,0)
  FaceMakerClass = Part::FaceMakerBullseye
  Placement = pos=(89.5,3,3.5) rot=(0,0,1;0rad)
  Solid = false
  Source = -> Face152
  Symmetric = false
FEATURE [Part::Revolution] Revolve166  label="backCaseScrewRetainer005"
  Angle = 360
  Axis = (0,1,0)
  Base = (0,0,0)
  FaceMakerClass = Part::FaceMakerBullseye
  Placement = pos=(12.5,3,10) rot=(0,0,1;0rad)
  Solid = false
  Source = -> Face150
  Symmetric = false
FEATURE [Part::Revolution] Revolve167  label="moreFrontCaseScrewRetainer006"
  Angle = 360
  Axis = (0,1,0)
  Base = (0,0,0)
  FaceMakerClass = Part::FaceMakerBullseye
  Placement = pos=(109.5,4.5,68.5) rot=(0,0,1;0rad)
  Solid = false
  Source = -> Face153
  Symmetric = false
FEATURE [Part::Revolution] Revolve168  label="moreFrontCaseScrewRetainer007"
  Angle = 360
  Axis = (0,1,0)
  Base = (0,0,0)
  FaceMakerClass = Part::FaceMakerBullseye
  Placement = pos=(109.5,4.5,3.5) rot=(0,0,1;0rad)
  Solid = false
  Source = -> Face154
  Symmetric = false
FEATURE [Part::MultiFuse] Fusion151  label="screwRetainers003"
  Shapes = -> [Revolve168,Revolve167,Revolve166,Revolve165,Revolve164,Revolve163]
FEATURE [Part::Cut] Cut069  label="screwRetainers004"
  Base = -> Fusion151
  Tool = -> Fusion152
FEATURE [Part::Cut] Cut070
  Base = -> Cut069
  Tool = -> Fillet060
FEATURE [Part::Cut] Cut071  label="screwPillars001"
  Base = -> Cut070
  Tool = -> Fillet059
FEATURE [Part::MultiFuse] Fusion153  label="bottom024"
  Shapes = -> [Fusion149,Cut071]
FEATURE [Part::Cylinder] Cylinder067
  Angle = 360
  AttacherType = Attacher::AttachEngine3D
  Height = 10
  Placement = pos=(20.65,12,4.68) rot=(1,0,0;1.5708rad)
  Radius = 2
FEATURE [Part::Cylinder] Cylinder068
  Angle = 360
  AttacherType = Attacher::AttachEngine3D
  Height = 10
  Placement = pos=(20.65,12,67.38) rot=(1,0,0;1.5708rad)
  Radius = 2
FEATURE [Part::Cylinder] Cylinder069
  Angle = 360
  AttacherType = Attacher::AttachEngine3D
  Height = 10
  Placement = pos=(77.15,12,67.38) rot=(1,0,0;1.5708rad)
  Radius = 2
FEATURE [Part::Cylinder] Cylinder070
  Angle = 360
  AttacherType = Attacher::AttachEngine3D
  Height = 10
  Placement = pos=(77.15,12,4.68) rot=(1,0,0;1.5708rad)
  Radius = 2
FEATURE [Part::MultiFuse] Fusion154  label="removeFromThreadedInsertHousing001"
  Shapes = -> [Cylinder069,Cylinder068,Cylinder067,Cylinder070]
FEATURE [Part::Cut] Cut072  label="bottom025"
  Base = -> Fusion153
  Tool = -> Fusion154
FEATURE [Image::ImagePlane] ImagePlane
  XSize = 339
  YSize = 72
FEATURE [Sketcher::SketchObject] Sketch083
  FullyConstrained = true
  MapMode = 5
  Support = -> [XY_Plane]
  sketch-geometry (338):
    g0: LineSegment StartX=-151.619 StartY=28.8932 StartZ=0 EndX=-140.819 EndY=28.8932 EndZ=0
    g1: LineSegment StartX=-151.619 StartY=24.0313 StartZ=0 EndX=-151.619 EndY=28.8932 EndZ=0
    g2: LineSegment StartX=-140.819 StartY=17.7713 StartZ=0 EndX=-151.619 EndY=17.7713 EndZ=0
    g3: LineSegment StartX=-151.619 StartY=17.7713 StartZ=0 EndX=-151.619 EndY=22.6313 EndZ=0
    g4: LineSegment StartX=-151.619 StartY=22.6313 StartZ=0 EndX=-145.128 EndY=22.6313 EndZ=0
    g5: LineSegment StartX=-145.128 StartY=24.0313 StartZ=0 EndX=-140.819 EndY=28.8932 EndZ=0
    g6: LineSegment StartX=-145.128 StartY=22.6313 StartZ=0 EndX=-140.819 EndY=17.7713 EndZ=0
    g7: ArcOfCircle CenterX=-155.157 CenterY=23.3323 CenterZ=0 NormalX=0 NormalY=0 NormalZ=1 AngleXU=0 Radius=6.92354 StartAngle=1.03434 EndAngle=5.24885
    g8: ArcOfCircle CenterX=-155.157 CenterY=23.3323 CenterZ=0 NormalX=0 NormalY=0 NormalZ=1 AngleXU=0 Radius=12.6269 StartAngle=1.28675 EndAngle=4.99643
    g9: LineSegment StartX=-151.619 StartY=35.4532 StartZ=0 EndX=-151.619 EndY=29.2832 EndZ=0
    g10: LineSegment StartX=-151.619 StartY=17.3813 StartZ=0 EndX=-151.619 EndY=11.2113 EndZ=0
    g11-g21: Circle x11 (B-spline internal-alignment scaffolding for g22; pole/knot coordinates omitted)
    g22: BSplineCurve PolesCount=11 KnotsCount=9 Degree=3 IsPeriodic=0
    g23-g31: GeomPoint x9 (B-spline internal-alignment scaffolding for g22; pole/knot coordinates omitted)
    g32-g49: Circle x18 (B-spline internal-alignment scaffolding for g50; pole/knot coordinates omitted)
    g50: BSplineCurve PolesCount=18 KnotsCount=16 Degree=3 IsPeriodic=0
    g51-g66: GeomPoint x16 (B-spline internal-alignment scaffolding for g50; pole/knot coordinates omitted)
    g67: LineSegment StartX=-117.124 StartY=30.093 StartZ=0 EndX=-117.603 EndY=26.5272 EndZ=0
    g68: LineSegment StartX=-117.603 StartY=17.8472 StartZ=0 EndX=-117.124 EndY=14.2659 EndZ=0
    g69: Ellipse CenterX=-109.671 CenterY=20.025 CenterZ=0 NormalX=0 NormalY=0 NormalZ=1 MajorRadius=3.34798 MinorRadius=2.71052 AngleXU=-1.56793
    g70: GeomPoint X=-109.666 Y=18.0598 Z=0
    g71: GeomPoint X=-109.677 Y=21.9902 Z=0
    g72: Ellipse CenterX=-109.671 CenterY=20.0123 CenterZ=0 NormalX=0 NormalY=0 NormalZ=1 MajorRadius=6.93002 MinorRadius=6.36273 AngleXU=-3.13976
    g73: GeomPoint X=-112.417 Y=20.0073 Z=0
    g74: GeomPoint X=-106.925 Y=20.0173 Z=0
    g75: Ellipse CenterX=-51.7682 CenterY=20.1463 CenterZ=0 NormalX=0 NormalY=0 NormalZ=1 MajorRadius=3.19279 MinorRadius=2.71052 AngleXU=-1.52774
    g76: GeomPoint X=-51.6955 Y=18.4606 Z=0
    g77: GeomPoint X=-51.8408 Y=21.832 Z=0
    g78: GeomPoint X=-54.5142 Y=20.1413 Z=0
    g79: GeomPoint X=-49.0221 Y=20.1513 Z=0
    g80: Ellipse CenterX=-51.7682 CenterY=20.1463 CenterZ=0 NormalX=0 NormalY=0 NormalZ=1 MajorRadius=6.93002 MinorRadius=6.36273 AngleXU=-3.13976
    g81: Ellipse CenterX=-22.8436 CenterY=20.1783 CenterZ=0 NormalX=0 NormalY=0 NormalZ=1 MajorRadius=3.31512 MinorRadius=2.71052 AngleXU=-1.60214
    g82: GeomPoint X=-22.9034 Y=18.2706 Z=0
    g83: GeomPoint X=-22.7838 Y=22.0861 Z=0
    g84: GeomPoint X=-25.5897 Y=20.1733 Z=0
    g85: GeomPoint X=-20.0976 Y=20.1833 Z=0
    g86: Ellipse CenterX=-22.8436 CenterY=20.1783 CenterZ=0 NormalX=0 NormalY=0 NormalZ=1 MajorRadius=6.93002 MinorRadius=6.36273 AngleXU=-3.13976
    g87: LineSegment StartX=-101.889 StartY=14.1107 StartZ=0 EndX=-97.7455 EndY=14.1107 EndZ=0
    g88: LineSegment StartX=-93.8155 StartY=14.1107 StartZ=0 EndX=-89.6755 EndY=14.1107 EndZ=0
    g89: LineSegment StartX=-85.7455 StartY=14.1107 StartZ=0 EndX=-81.6055 EndY=14.1107 EndZ=0
    g90: LineSegment StartX=-101.889 StartY=14.1107 StartZ=0 EndX=-101.889 EndY=25.9907 EndZ=0
    g91: LineSegment StartX=-101.889 StartY=25.9907 StartZ=0 EndX=-97.8594 EndY=25.9907 EndZ=0
    g92: LineSegment StartX=-97.8594 StartY=25.9907 StartZ=0 EndX=-97.8594 EndY=24.0907 EndZ=0
    g93: LineSegment StartX=-97.7455 StartY=14.1107 StartZ=0 EndX=-97.7455 EndY=19.9107 EndZ=0
    g94: LineSegment StartX=-89.6755 StartY=14.1107 StartZ=0 EndX=-89.6755 EndY=19.9107 EndZ=0
    g95: LineSegment StartX=-93.8155 StartY=14.1107 StartZ=0 EndX=-93.8155 EndY=21.0107 EndZ=0
    g96-g106: Circle x11 (B-spline internal-alignment scaffolding for g107; pole/knot coordinates omitted)
    g107: BSplineCurve PolesCount=11 KnotsCount=9 Degree=3 IsPeriodic=0
    g108-g116: GeomPoint x9 (B-spline internal-alignment scaffolding for g107; pole/knot coordinates omitted)
    g117: BSplineCurve PolesCount=11 KnotsCount=9 Degree=3 IsPeriodic=0
    g118-g125: Circle x8 (B-spline internal-alignment scaffolding for g126; pole/knot coordinates omitted)
    g126: BSplineCurve PolesCount=8 KnotsCount=6 Degree=3 IsPeriodic=0
    g127-g132: GeomPoint x6 (B-spline internal-alignment scaffolding for g126; pole/knot coordinates omitted)
    g133: BSplineCurve PolesCount=8 KnotsCount=6 Degree=3 IsPeriodic=0
    g134: LineSegment StartX=-85.7455 StartY=21.0107 StartZ=0 EndX=-85.7455 EndY=14.1107 EndZ=0
    g135: LineSegment StartX=-80.0879 StartY=14.1107 StartZ=0 EndX=-75.944 EndY=14.1107 EndZ=0
    g136: LineSegment StartX=-72.014 StartY=14.1107 StartZ=0 EndX=-67.874 EndY=14.1107 EndZ=0
    g137: LineSegment StartX=-63.944 StartY=14.1107 StartZ=0 EndX=-59.804 EndY=14.1107 EndZ=0
    g138: LineSegment StartX=-80.0879 StartY=14.1107 StartZ=0 EndX=-80.0879 EndY=25.9907 EndZ=0
    g139: LineSegment StartX=-80.0879 StartY=25.9907 StartZ=0 EndX=-76.0579 EndY=25.9907 EndZ=0
    g140: LineSegment StartX=-76.0579 StartY=25.9907 StartZ=0 EndX=-76.0579 EndY=24.0907 EndZ=0
    g141: LineSegment StartX=-75.944 StartY=14.1107 StartZ=0 EndX=-75.944 EndY=19.9107 EndZ=0
    g142: LineSegment StartX=-67.874 StartY=14.1107 StartZ=0 EndX=-67.874 EndY=19.9107 EndZ=0
    g143: LineSegment StartX=-72.014 StartY=14.1107 StartZ=0 EndX=-72.014 EndY=21.0107 EndZ=0
    g144-g148: Circle x5 (B-spline internal-alignment scaffolding for g149; pole/knot coordinates omitted)
    g149: BSplineCurve PolesCount=11 KnotsCount=9 Degree=3 IsPeriodic=0
    g150-g158: GeomPoint x9 (B-spline internal-alignment scaffolding for g149; pole/knot coordinates omitted)
    g159: BSplineCurve PolesCount=11 KnotsCount=9 Degree=3 IsPeriodic=0
    g160-g167: Circle x8 (B-spline internal-alignment scaffolding for g168; pole/knot coordinates omitted)
    g168: BSplineCurve PolesCount=8 KnotsCount=6 Degree=3 IsPeriodic=0
    g169-g174: GeomPoint x6 (B-spline internal-alignment scaffolding for g168; pole/knot coordinates omitted)
    g175: BSplineCurve PolesCount=8 KnotsCount=6 Degree=3 IsPeriodic=0
    g176: LineSegment StartX=-63.944 StartY=21.0107 StartZ=0 EndX=-63.944 EndY=14.1107 EndZ=0
    g177: LineSegment StartX=-59.804 StartY=14.1107 StartZ=0 EndX=-59.804 EndY=21.5868 EndZ=0
    g178: BSplineCurve PolesCount=4 KnotsCount=2 Degree=3 IsPeriodic=0
    g179: GeomPoint X=-59.804 Y=21.5868 Z=0
    g180: GeomPoint X=-60.2379 Y=24.0907 Z=0
    g181: LineSegment StartX=-81.6055 StartY=14.1107 StartZ=0 EndX=-81.6055 EndY=21.5868 EndZ=0
    g182: LineSegment StartX=-151.619 StartY=24.0313 StartZ=0 EndX=-145.128 EndY=24.0313 EndZ=0
    g183: Circle CenterX=-82.0394 CenterY=24.0907 CenterZ=0 NormalX=0 NormalY=0 NormalZ=1 AngleXU=0 Radius=1
    g184: Circle CenterX=-81.7131 CenterY=23.2736 CenterZ=0 NormalX=0 NormalY=0 NormalZ=1 AngleXU=0 Radius=1
    g185: Circle CenterX=-81.6055 CenterY=21.5868 CenterZ=0 NormalX=0 NormalY=0 NormalZ=1 AngleXU=0 Radius=1
    g186: BSplineCurve PolesCount=3 KnotsCount=2 Degree=2 IsPeriodic=0
    g187: GeomPoint X=-82.0394 Y=24.0907 Z=0
    g188: GeomPoint X=-81.6055 Y=21.5868 Z=0
    g189: Ellipse CenterX=-37.3522 CenterY=19.9515 CenterZ=0 NormalX=0 NormalY=0 NormalZ=1 MajorRadius=2.99755 MinorRadius=2.49 AngleXU=1.5708
    g190: GeomPoint X=-37.3522 Y=21.6203 Z=0
    g191: GeomPoint X=-37.3522 Y=18.2826 Z=0
    g192: ArcOfEllipse CenterX=-38.7647 CenterY=20.06 CenterZ=0 NormalX=0 NormalY=0 NormalZ=1 MajorRadius=6.30025 MinorRadius=5.3849 AngleXU=1.57276 StartAngle=5.50632 EndAngle=10.3035
    g193: GeomPoint X=-38.7711 Y=23.3304 Z=0
    g194: GeomPoint X=-38.7583 Y=16.7895 Z=0
    g195: LineSegment StartX=-34.6109 StartY=14.1107 StartZ=0 EndX=-30.8984 EndY=14.1107 EndZ=0
    g196: LineSegment StartX=-30.8984 StartY=14.1107 StartZ=0 EndX=-30.8984 EndY=31.1784 EndZ=0
    g197: LineSegment StartX=-30.8984 StartY=31.1784 StartZ=0 EndX=-34.9984 EndY=31.1784 EndZ=0
    g198: LineSegment StartX=-34.9984 StartY=24.5602 StartZ=0 EndX=-34.9984 EndY=31.1784 EndZ=0
    g199: LineSegment StartX=-34.6109 StartY=16.0476 StartZ=0 EndX=-34.6109 EndY=14.1107 EndZ=0
    g200: LineSegment StartX=-14.8781 StartY=14.1107 StartZ=0 EndX=-10.5106 EndY=14.1107 EndZ=0
    g201: LineSegment StartX=-14.8781 StartY=14.1107 StartZ=0 EndX=-14.8781 EndY=25.8504 EndZ=0
    g202: LineSegment StartX=-14.8781 StartY=25.8504 StartZ=0 EndX=-10.8534 EndY=25.8504 EndZ=0
    g203: LineSegment StartX=-10.8534 StartY=25.8504 StartZ=0 EndX=-10.8534 EndY=24.0923 EndZ=0
    g204: LineSegment StartX=-10.5106 StartY=14.1107 StartZ=0 EndX=-10.5106 EndY=19.7752 EndZ=0
    g205: LineSegment StartX=-5.96397 StartY=25.9304 StartZ=0 EndX=-5.96397 EndY=22.574 EndZ=0
    g206-g214: Circle x9 (B-spline internal-alignment scaffolding for g215; pole/knot coordinates omitted)
    g215: BSplineCurve PolesCount=9 KnotsCount=7 Degree=3 IsPeriodic=0
    g216-g222: GeomPoint x7 (B-spline internal-alignment scaffolding for g215; pole/knot coordinates omitted)
    g223-g232: Circle x10 (B-spline internal-alignment scaffolding for g233; pole/knot coordinates omitted)
    g233: BSplineCurve PolesCount=10 KnotsCount=8 Degree=3 IsPeriodic=0
    g234-g241: GeomPoint x8 (B-spline internal-alignment scaffolding for g233; pole/knot coordinates omitted)
    g242: LineSegment StartX=-1.58923 StartY=21.0696 StartZ=0 EndX=2.62034 EndY=21.0696 EndZ=0
    g243: LineSegment StartX=-1.55856 StartY=18.7342 StartZ=0 EndX=6.45946 EndY=18.7342 EndZ=0
    g244: LineSegment StartX=5.29231 StartY=17.386 StartZ=0 EndX=5.29231 EndY=14.3674 EndZ=0
    g245-g269: Circle x25 (B-spline internal-alignment scaffolding for g270; pole/knot coordinates omitted)
    g270: BSplineCurve PolesCount=25 KnotsCount=23 Degree=3 IsPeriodic=0
    g271-g293: GeomPoint x23 (B-spline internal-alignment scaffolding for g270; pole/knot coordinates omitted)
    g294-g304: Circle x11 (B-spline internal-alignment scaffolding for g305; pole/knot coordinates omitted)
    g305: BSplineCurve PolesCount=11 KnotsCount=9 Degree=3 IsPeriodic=0
    g306-g314: GeomPoint x9 (B-spline internal-alignment scaffolding for g305; pole/knot coordinates omitted)
    g315-g326: Circle x12 (B-spline internal-alignment scaffolding for g327; pole/knot coordinates omitted)
    g327: BSplineCurve PolesCount=12 KnotsCount=10 Degree=3 IsPeriodic=0
    g328-g337: GeomPoint x10 (B-spline internal-alignment scaffolding for g327; pole/knot coordinates omitted)
  constraints (252):
    c: Coincident(g1,g0)
    c: Horizontal(g0)
    c: Vertical(g1)
    c: Coincident(g2,g3)
    c: Coincident(g3,g4)
    c: Horizontal(g4)
    c: Horizontal(g2)
    c: Vertical(g3)
    c: Block(g1)
    c: Distance(g3) = 4.86
    c: Block(g4)
    c: Distance(g0) = 10.8
    c: Distance(g2) = 10.8
    c: Coincident(g5,g0)
    c: Coincident(g6,g4)
    c: Coincident(g6,g2)
    c: Block(g8)
    c: Block(g7)
    c: Coincident(g9,g8)
    c: Coincident(g9,g7)
    c: Vertical(g9)
    c: Coincident(g10,g7)
    c: Coincident(g10,g8)
    c: Vertical(g10)
    c: Weight(g11) = 1
    c: Equal(g11, g12-g21) x10
    c: InternalAlignment(g11-g21 -> g22) x11
    c: InternalAlignment(g23-g31 -> g22) x9
    c: Block(g22)
    c: Weight(g32) = 1
    c: Equal(g32, g33-g49) x17
    c: InternalAlignment(g32-g49 -> g50) x18
    c: InternalAlignment(g51-g66 -> g50) x16
    c: Block(g50)
    c: Coincident(g67,g50)
    c: Coincident(g67,g22)
    c: Coincident(g68,g22)
    c: Coincident(g68,g50)
    c: InternalAlignment(g70,g69)
    c: InternalAlignment(g71,g69)
    c: Block(g69)
    c: InternalAlignment(g73,g72)
    c: InternalAlignment(g74,g72)
    c: Block(g72)
    c: InternalAlignment(g76,g75)
    c: InternalAlignment(g77,g75)
    c: InternalAlignment(g78,g80)
    c: InternalAlignment(g79,g80)
    c: Block(g80)
    c: Coincident(g75,g80)
    c: Block(g75)
    c: InternalAlignment(g82,g81)
    c: InternalAlignment(g83,g81)
    c: InternalAlignment(g84,g86)
    c: InternalAlignment(g85,g86)
    c: Block(g86)
    c: Coincident(g81,g86)
    c: Block(g81)
    c: Horizontal(g87)
    c: Block(g87)
    c: Horizontal(g88)
    c: Distance(g88) = 4.14
    c: Horizontal(g89)
    c: Equal(g88,g89) = 4.14
    c: Block(g89)
    c: Block(g88)
    c: Coincident(g90,g87)
    c: Vertical(g90)
    c: Distance(g90) = 11.88
    c: Coincident(g91,g90)
    c: Horizontal(g91)
    c: Coincident(g92,g91)
    c: Vertical(g92)
    c: Distance(g91) = 4.03
    c: Distance(g92) = 1.9
    c: Coincident(g93,g87)
    c: Vertical(g93)
    c: Vertical(g94)
    c: Coincident(g94,g88)
    c: Distance(g93) = 5.8
    c: Distance(g94) = 5.8
    c: Vertical(g95)
    c: Coincident(g95,g88)
    c: Distance(g95) = 6.9
    c: Coincident(g107,g92)
    c: Weight(g96) = 1
    c: Equal(g96, g97-g106) x10
    c: InternalAlignment(g96-g106 -> g107) x11
    c: InternalAlignment(g108-g116 -> g107) x9
    c: Block(g107)
    c: Block(g117)
    c: Coincident(g126,g93)
    c: Weight(g118) = 1
    c: Equal(g118, g119-g125) x7
    c: Coincident(g126,g95)
    c: InternalAlignment(g118-g125 -> g126) x8
    c: InternalAlignment(g127-g132 -> g126) x6
    c: Coincident(g133,g94)
    c: Block(g126)
    c: Block(g133)
    c: Coincident(g134,g133)
    c: Coincident(g134,g89)
    c: Vertical(g134)
    c: Horizontal(g135)
    c: Block(g135)
    c: Horizontal(g136)
    c: Equal(g88,g136) = 4.14
    c: Horizontal(g137)
    c: Equal(g136,g137) = 4.14
    c: Block(g137)
    c: Block(g136)
    c: Coincident(g138,g135)
    c: Vertical(g138)
    c: Equal(g90,g138) = 11.88
    c: Coincident(g139,g138)
    c: Horizontal(g139)
    c: Coincident(g140,g139)
    c: Vertical(g140)
    c: Equal(g91,g139) = 4.03
    c: Equal(g92,g140) = 1.9
    c: Coincident(g141,g135)
    c: Vertical(g141)
    c: Vertical(g142)
    c: Coincident(g142,g136)
    c: Equal(g93,g141) = 5.8
    c: Equal(g94,g142) = 5.8
    c: Vertical(g143)
    c: Coincident(g143,g136)
    c: Equal(g95,g143) = 6.9
    c: Coincident(g149,g140)
    c: Equal(g96,g144) = 1
    c: Equal(g144, g145-g148) x4
    c: InternalAlignment(g144-g148 -> g149) x5
    c: InternalAlignment(g150-g158 -> g149) x9
    c: Block(g149)
    c: Block(g159)
    c: Coincident(g168,g141)
    c: Equal(g118,g160) = 1
    c: Equal(g160, g161-g167) x7
    c: Coincident(g168,g143)
    c: InternalAlignment(g160-g167 -> g168) x8
    c: InternalAlignment(g169-g174 -> g168) x6
    c: Coincident(g175,g142)
    c: Block(g168)
    c: Block(g175)
    c: Coincident(g176,g175)
    c: Coincident(g176,g137)
    c: Vertical(g176)
    c: Coincident(g177,g137)
    c: Vertical(g177)
    c: Coincident(g178,g177)
    c: Coincident(g178,g159)
    c: InternalAlignment(g179,g178)
    c: InternalAlignment(g180,g178)
    c: Block(g178)
    c: Vertical(g181)
    c: Coincident(g181,g89)
    c: Block(g5)
    c: Coincident(g182,g1)
    c: Coincident(g182,g5)
    c: Horizontal(g182)
    c: Coincident(g186,g117)
    c: Weight(g183) = 1
    c: Equal(g183,g184)
    c: Equal(g183,g185)
    c: Coincident(g186,g181)
    c: InternalAlignment(g183,g186)
    c: InternalAlignment(g184,g186)
    c: InternalAlignment(g185,g186)
    c: InternalAlignment(g187,g186)
    c: InternalAlignment(g188,g186)
    c: Block(g186)
    c: InternalAlignment(g190,g189)
    c: InternalAlignment(g191,g189)
    c: Block(g189)
    c: InternalAlignment(g193,g192)
    c: InternalAlignment(g194,g192)
    c: Block(g192)
    c: Horizontal(g195)
    c: Block(g195)
    c: Coincident(g196,g195)
    c: Vertical(g196)
    c: Block(g196)
    c: Distance(g195) = 3.71244
    c: Coincident(g197,g196)
    c: Horizontal(g197)
    c: Distance(g197) = 4.1
    c: Coincident(g198,g192)
    c: Coincident(g198,g197)
    c: Vertical(g198)
    c: Block(g198)
    c: Coincident(g199,g192)
    c: Coincident(g199,g195)
    c: Vertical(g199)
    c: Block(g199)
    c: Horizontal(g200)
    c: Block(g200)
    c: Coincident(g201,g200)
    c: Vertical(g201)
    c: Block(g201)
    c: Coincident(g202,g201)
    c: Horizontal(g202)
    c: Block(g202)
    c: Coincident(g203,g202)
    c: Vertical(g203)
    c: Block(g203)
    c: Coincident(g204,g200)
    c: Vertical(g204)
    c: Block(g204)
    c: Coincident(g215,g203)
    c: Weight(g206) = 1
    c: Equal(g206, g207-g214) x8
    c: Coincident(g215,g205)
    c: InternalAlignment(g206-g214 -> g215) x9
    c: InternalAlignment(g216-g222 -> g215) x7
    c: Coincident(g233,g204)
    c: Weight(g223) = 1
    c: Equal(g223, g224-g232) x9
    c: Coincident(g233,g205)
    c: InternalAlignment(g223-g232 -> g233) x10
    c: InternalAlignment(g234-g241 -> g233) x8
    c: Vertical(g205)
    c: Block(g205)
    c: Block(g215)
    c: Block(g233)
    c: Horizontal(g242)
    c: Horizontal(g243)
    c: Block(g242)
    c: Block(g243)
    c: Vertical(g244)
    c: Block(g244)
    c: Coincident(g270,g243)
    c: Weight(g245) = 1
    c: Equal(g245, g246-g269) x24
    c: Coincident(g270,g244)
    c: InternalAlignment(g245-g269 -> g270) x25
    c: InternalAlignment(g271-g293 -> g270) x23
    c: Coincident(g305,g242)
    c: Weight(g294) = 1
    c: Equal(g294, g295-g304) x10
    c: Coincident(g305,g242)
    c: InternalAlignment(g294-g304 -> g305) x11
    c: InternalAlignment(g306-g314 -> g305) x9
    c: Block(g305)
    c: Coincident(g327,g243)
    c: Weight(g315) = 1
    c: Equal(g315, g316-g326) x11
    c: Coincident(g327,g244)
    c: InternalAlignment(g315-g326 -> g327) x12
    c: InternalAlignment(g328-g337 -> g327) x10
    c: Block(g327)
    c: Block(g270)
FEATURE [PartDesign::Body] Body  label="CommodoreLogoAndText"
  Group = -> [Sketch083]
  Origin = -> Origin
FEATURE [Part::Extrusion] Extrude074  label="CommodoreLogoAndText001"
  Base = -> Sketch083
  Dir = (0,0,1)
  DirMode = 2
  FaceMakerClass = Part::FaceMakerBullseye
  LengthFwd = 10
  LengthRev = 0
  Solid = true
  Symmetric = false
FEATURE [Part::FeaturePython] Clone  label="CommodoreLogoAndTextScale"  # Draft clone (typed FeaturePython)
  AttacherType = Attacher::AttachEngine3D
  Fuse = false
  Objects = -> [Extrude074]
  Placement = pos=(111,5.37,-11.6) rot=(0,0,1;0rad)
  Scale = (0.62,0.62,1)
FEATURE [Part::Mirroring] Part__Mirroring  label="CommodoreLogoAndTextScale (Mirror #1)"
  Base = (0,0,0)
  Normal = (1,0,0)
  Placement = pos=(123.576,0,0) rot=(0,0,1;0rad)
  Source = -> Clone
FEATURE [Sketcher::SketchObject] Sketch084
  FullyConstrained = true
  MapMode = 5
  Support = -> [XY_Plane001]
  sketch-geometry (338):
    g0: LineSegment StartX=-151.619 StartY=28.8932 StartZ=0 EndX=-140.819 EndY=28.8932 EndZ=0
    g1: LineSegment StartX=-151.619 StartY=24.0313 StartZ=0 EndX=-151.619 EndY=28.8932 EndZ=0
    g2: LineSegment StartX=-140.819 StartY=17.7713 StartZ=0 EndX=-151.619 EndY=17.7713 EndZ=0
    g3: LineSegment StartX=-151.619 StartY=17.7713 StartZ=0 EndX=-151.619 EndY=22.6313 EndZ=0
    g4: LineSegment StartX=-151.619 StartY=22.6313 StartZ=0 EndX=-145.128 EndY=22.6313 EndZ=0
    g5: LineSegment StartX=-145.128 StartY=24.0313 StartZ=0 EndX=-140.819 EndY=28.8932 EndZ=0
    g6: LineSegment StartX=-145.128 StartY=22.6313 StartZ=0 EndX=-140.819 EndY=17.7713 EndZ=0
    g7: ArcOfCircle CenterX=-155.157 CenterY=23.3323 CenterZ=0 NormalX=0 NormalY=0 NormalZ=1 AngleXU=0 Radius=6.92354 StartAngle=1.03434 EndAngle=5.24885
    g8: ArcOfCircle CenterX=-155.157 CenterY=23.3323 CenterZ=0 NormalX=0 NormalY=0 NormalZ=1 AngleXU=0 Radius=12.6269 StartAngle=1.28675 EndAngle=4.99643
    g9: LineSegment StartX=-151.619 StartY=35.4532 StartZ=0 EndX=-151.619 EndY=29.2832 EndZ=0
    g10: LineSegment StartX=-151.619 StartY=17.3813 StartZ=0 EndX=-151.619 EndY=11.2113 EndZ=0
    g11-g21: Circle x11 (B-spline internal-alignment scaffolding for g22; pole/knot coordinates omitted)
    g22: BSplineCurve PolesCount=11 KnotsCount=9 Degree=3 IsPeriodic=0
    g23-g31: GeomPoint x9 (B-spline internal-alignment scaffolding for g22; pole/knot coordinates omitted)
    g32-g49: Circle x18 (B-spline internal-alignment scaffolding for g50; pole/knot coordinates omitted)
    g50: BSplineCurve PolesCount=18 KnotsCount=16 Degree=3 IsPeriodic=0
    g51-g66: GeomPoint x16 (B-spline internal-alignment scaffolding for g50; pole/knot coordinates omitted)
    g67: LineSegment StartX=-117.124 StartY=30.093 StartZ=0 EndX=-117.603 EndY=26.5272 EndZ=0
    g68: LineSegment StartX=-117.603 StartY=17.8472 StartZ=0 EndX=-117.124 EndY=14.2659 EndZ=0
    g69: Ellipse CenterX=-109.671 CenterY=20.025 CenterZ=0 NormalX=0 NormalY=0 NormalZ=1 MajorRadius=3.34798 MinorRadius=2.71052 AngleXU=-1.56793
    g70: GeomPoint X=-109.666 Y=18.0598 Z=0
    g71: GeomPoint X=-109.677 Y=21.9902 Z=0
    g72: Ellipse CenterX=-109.671 CenterY=20.0123 CenterZ=0 NormalX=0 NormalY=0 NormalZ=1 MajorRadius=6.93002 MinorRadius=6.36273 AngleXU=-3.13976
    g73: GeomPoint X=-112.417 Y=20.0073 Z=0
    g74: GeomPoint X=-106.925 Y=20.0173 Z=0
    g75: Ellipse CenterX=-51.7682 CenterY=20.1463 CenterZ=0 NormalX=0 NormalY=0 NormalZ=1 MajorRadius=3.19279 MinorRadius=2.71052 AngleXU=-1.52774
    g76: GeomPoint X=-51.6955 Y=18.4606 Z=0
    g77: GeomPoint X=-51.8408 Y=21.832 Z=0
    g78: GeomPoint X=-54.5142 Y=20.1413 Z=0
    g79: GeomPoint X=-49.0221 Y=20.1513 Z=0
    g80: Ellipse CenterX=-51.7682 CenterY=20.1463 CenterZ=0 NormalX=0 NormalY=0 NormalZ=1 MajorRadius=6.93002 MinorRadius=6.36273 AngleXU=-3.13976
    g81: Ellipse CenterX=-22.8436 CenterY=20.1783 CenterZ=0 NormalX=0 NormalY=0 NormalZ=1 MajorRadius=3.31512 MinorRadius=2.71052 AngleXU=-1.60214
    g82: GeomPoint X=-22.9034 Y=18.2706 Z=0
    g83: GeomPoint X=-22.7838 Y=22.0861 Z=0
    g84: GeomPoint X=-25.5897 Y=20.1733 Z=0
    g85: GeomPoint X=-20.0976 Y=20.1833 Z=0
    g86: Ellipse CenterX=-22.8436 CenterY=20.1783 CenterZ=0 NormalX=0 NormalY=0 NormalZ=1 MajorRadius=6.93002 MinorRadius=6.36273 AngleXU=-3.13976
    g87: LineSegment StartX=-101.889 StartY=14.1107 StartZ=0 EndX=-97.7455 EndY=14.1107 EndZ=0
    g88: LineSegment StartX=-93.8155 StartY=14.1107 StartZ=0 EndX=-89.6755 EndY=14.1107 EndZ=0
    g89: LineSegment StartX=-85.7455 StartY=14.1107 StartZ=0 EndX=-81.6055 EndY=14.1107 EndZ=0
    g90: LineSegment StartX=-101.889 StartY=14.1107 StartZ=0 EndX=-101.889 EndY=25.9907 EndZ=0
    g91: LineSegment StartX=-101.889 StartY=25.9907 StartZ=0 EndX=-97.8594 EndY=25.9907 EndZ=0
    g92: LineSegment StartX=-97.8594 StartY=25.9907 StartZ=0 EndX=-97.8594 EndY=24.0907 EndZ=0
    g93: LineSegment StartX=-97.7455 StartY=14.1107 StartZ=0 EndX=-97.7455 EndY=19.9107 EndZ=0
    g94: LineSegment StartX=-89.6755 StartY=14.1107 StartZ=0 EndX=-89.6755 EndY=19.9107 EndZ=0
    g95: LineSegment StartX=-93.8155 StartY=14.1107 StartZ=0 EndX=-93.8155 EndY=21.0107 EndZ=0
    g96-g106: Circle x11 (B-spline internal-alignment scaffolding for g107; pole/knot coordinates omitted)
    g107: BSplineCurve PolesCount=11 KnotsCount=9 Degree=3 IsPeriodic=0
    g108-g116: GeomPoint x9 (B-spline internal-alignment scaffolding for g107; pole/knot coordinates omitted)
    g117: BSplineCurve PolesCount=11 KnotsCount=9 Degree=3 IsPeriodic=0
    g118-g125: Circle x8 (B-spline internal-alignment scaffolding for g126; pole/knot coordinates omitted)
    g126: BSplineCurve PolesCount=8 KnotsCount=6 Degree=3 IsPeriodic=0
    g127-g132: GeomPoint x6 (B-spline internal-alignment scaffolding for g126; pole/knot coordinates omitted)
    g133: BSplineCurve PolesCount=8 KnotsCount=6 Degree=3 IsPeriodic=0
    g134: LineSegment StartX=-85.7455 StartY=21.0107 StartZ=0 EndX=-85.7455 EndY=14.1107 EndZ=0
    g135: LineSegment StartX=-80.0879 StartY=14.1107 StartZ=0 EndX=-75.944 EndY=14.1107 EndZ=0
    g136: LineSegment StartX=-72.014 StartY=14.1107 StartZ=0 EndX=-67.874 EndY=14.1107 EndZ=0
    g137: LineSegment StartX=-63.944 StartY=14.1107 StartZ=0 EndX=-59.804 EndY=14.1107 EndZ=0
    g138: LineSegment StartX=-80.0879 StartY=14.1107 StartZ=0 EndX=-80.0879 EndY=25.9907 EndZ=0
    g139: LineSegment StartX=-80.0879 StartY=25.9907 StartZ=0 EndX=-76.0579 EndY=25.9907 EndZ=0
    g140: LineSegment StartX=-76.0579 StartY=25.9907 StartZ=0 EndX=-76.0579 EndY=24.0907 EndZ=0
    g141: LineSegment StartX=-75.944 StartY=14.1107 StartZ=0 EndX=-75.944 EndY=19.9107 EndZ=0
    g142: LineSegment StartX=-67.874 StartY=14.1107 StartZ=0 EndX=-67.874 EndY=19.9107 EndZ=0
    g143: LineSegment StartX=-72.014 StartY=14.1107 StartZ=0 EndX=-72.014 EndY=21.0107 EndZ=0
    g144-g148: Circle x5 (B-spline internal-alignment scaffolding for g149; pole/knot coordinates omitted)
    g149: BSplineCurve PolesCount=11 KnotsCount=9 Degree=3 IsPeriodic=0
    g150-g158: GeomPoint x9 (B-spline internal-alignment scaffolding for g149; pole/knot coordinates omitted)
    g159: BSplineCurve PolesCount=11 KnotsCount=9 Degree=3 IsPeriodic=0
    g160-g167: Circle x8 (B-spline internal-alignment scaffolding for g168; pole/knot coordinates omitted)
    g168: BSplineCurve PolesCount=8 KnotsCount=6 Degree=3 IsPeriodic=0
    g169-g174: GeomPoint x6 (B-spline internal-alignment scaffolding for g168; pole/knot coordinates omitted)
    g175: BSplineCurve PolesCount=8 KnotsCount=6 Degree=3 IsPeriodic=0
    g176: LineSegment StartX=-63.944 StartY=21.0107 StartZ=0 EndX=-63.944 EndY=14.1107 EndZ=0
    g177: LineSegment StartX=-59.804 StartY=14.1107 StartZ=0 EndX=-59.804 EndY=21.5868 EndZ=0
    g178: BSplineCurve PolesCount=4 KnotsCount=2 Degree=3 IsPeriodic=0
    g179: GeomPoint X=-59.804 Y=21.5868 Z=0
    g180: GeomPoint X=-60.2379 Y=24.0907 Z=0
    g181: LineSegment StartX=-81.6055 StartY=14.1107 StartZ=0 EndX=-81.6055 EndY=21.5868 EndZ=0
    g182: LineSegment StartX=-151.619 StartY=24.0313 StartZ=0 EndX=-145.128 EndY=24.0313 EndZ=0
    g183: Circle CenterX=-82.0394 CenterY=24.0907 CenterZ=0 NormalX=0 NormalY=0 NormalZ=1 AngleXU=0 Radius=1
    g184: Circle CenterX=-81.7131 CenterY=23.2736 CenterZ=0 NormalX=0 NormalY=0 NormalZ=1 AngleXU=0 Radius=1
    g185: Circle CenterX=-81.6055 CenterY=21.5868 CenterZ=0 NormalX=0 NormalY=0 NormalZ=1 AngleXU=0 Radius=1
    g186: BSplineCurve PolesCount=3 KnotsCount=2 Degree=2 IsPeriodic=0
    g187: GeomPoint X=-82.0394 Y=24.0907 Z=0
    g188: GeomPoint X=-81.6055 Y=21.5868 Z=0
    g189: Ellipse CenterX=-37.3522 CenterY=19.9515 CenterZ=0 NormalX=0 NormalY=0 NormalZ=1 MajorRadius=2.99755 MinorRadius=2.49 AngleXU=1.5708
    g190: GeomPoint X=-37.3522 Y=21.6203 Z=0
    g191: GeomPoint X=-37.3522 Y=18.2826 Z=0
    g192: ArcOfEllipse CenterX=-38.7647 CenterY=20.06 CenterZ=0 NormalX=0 NormalY=0 NormalZ=1 MajorRadius=6.30025 MinorRadius=5.3849 AngleXU=1.57276 StartAngle=5.50632 EndAngle=10.3035
    g193: GeomPoint X=-38.7711 Y=23.3304 Z=0
    g194: GeomPoint X=-38.7583 Y=16.7895 Z=0
    g195: LineSegment StartX=-34.6109 StartY=14.1107 StartZ=0 EndX=-30.8984 EndY=14.1107 EndZ=0
    g196: LineSegment StartX=-30.8984 StartY=14.1107 StartZ=0 EndX=-30.8984 EndY=31.1784 EndZ=0
    g197: LineSegment StartX=-30.8984 StartY=31.1784 StartZ=0 EndX=-34.9984 EndY=31.1784 EndZ=0
    g198: LineSegment StartX=-34.9984 StartY=24.5602 StartZ=0 EndX=-34.9984 EndY=31.1784 EndZ=0
    g199: LineSegment StartX=-34.6109 StartY=16.0476 StartZ=0 EndX=-34.6109 EndY=14.1107 EndZ=0
    g200: LineSegment StartX=-14.8781 StartY=14.1107 StartZ=0 EndX=-10.5106 EndY=14.1107 EndZ=0
    g201: LineSegment StartX=-14.8781 StartY=14.1107 StartZ=0 EndX=-14.8781 EndY=25.8504 EndZ=0
    g202: LineSegment StartX=-14.8781 StartY=25.8504 StartZ=0 EndX=-10.8534 EndY=25.8504 EndZ=0
    g203: LineSegment StartX=-10.8534 StartY=25.8504 StartZ=0 EndX=-10.8534 EndY=24.0923 EndZ=0
    g204: LineSegment StartX=-10.5106 StartY=14.1107 StartZ=0 EndX=-10.5106 EndY=19.7752 EndZ=0
    g205: LineSegment StartX=-5.96397 StartY=25.9304 StartZ=0 EndX=-5.96397 EndY=22.574 EndZ=0
    g206-g214: Circle x9 (B-spline internal-alignment scaffolding for g215; pole/knot coordinates omitted)
    g215: BSplineCurve PolesCount=9 KnotsCount=7 Degree=3 IsPeriodic=0
    g216-g222: GeomPoint x7 (B-spline internal-alignment scaffolding for g215; pole/knot coordinates omitted)
    g223-g232: Circle x10 (B-spline internal-alignment scaffolding for g233; pole/knot coordinates omitted)
    g233: BSplineCurve PolesCount=10 KnotsCount=8 Degree=3 IsPeriodic=0
    g234-g241: GeomPoint x8 (B-spline internal-alignment scaffolding for g233; pole/knot coordinates omitted)
    g242: LineSegment StartX=-1.58923 StartY=21.0696 StartZ=0 EndX=2.62034 EndY=21.0696 EndZ=0
    g243: LineSegment StartX=-1.55856 StartY=18.7342 StartZ=0 EndX=6.45946 EndY=18.7342 EndZ=0
    g244: LineSegment StartX=5.29231 StartY=17.386 StartZ=0 EndX=5.29231 EndY=14.3674 EndZ=0
    g245-g269: Circle x25 (B-spline internal-alignment scaffolding for g270; pole/knot coordinates omitted)
    g270: BSplineCurve PolesCount=25 KnotsCount=23 Degree=3 IsPeriodic=0
    g271-g293: GeomPoint x23 (B-spline internal-alignment scaffolding for g270; pole/knot coordinates omitted)
    g294-g304: Circle x11 (B-spline internal-alignment scaffolding for g305; pole/knot coordinates omitted)
    g305: BSplineCurve PolesCount=11 KnotsCount=9 Degree=3 IsPeriodic=0
    g306-g314: GeomPoint x9 (B-spline internal-alignment scaffolding for g305; pole/knot coordinates omitted)
    g315-g326: Circle x12 (B-spline internal-alignment scaffolding for g327; pole/knot coordinates omitted)
    g327: BSplineCurve PolesCount=12 KnotsCount=10 Degree=3 IsPeriodic=0
    g328-g337: GeomPoint x10 (B-spline internal-alignment scaffolding for g327; pole/knot coordinates omitted)
  constraints (252):
    c: Coincident(g1,g0)
    c: Horizontal(g0)
    c: Vertical(g1)
    c: Coincident(g2,g3)
    c: Coincident(g3,g4)
    c: Horizontal(g4)
    c: Horizontal(g2)
    c: Vertical(g3)
    c: Block(g1)
    c: Distance(g3) = 4.86
    c: Block(g4)
    c: Distance(g0) = 10.8
    c: Distance(g2) = 10.8
    c: Coincident(g5,g0)
    c: Coincident(g6,g4)
    c: Coincident(g6,g2)
    c: Block(g8)
    c: Block(g7)
    c: Coincident(g9,g8)
    c: Coincident(g9,g7)
    c: Vertical(g9)
    c: Coincident(g10,g7)
    c: Coincident(g10,g8)
    c: Vertical(g10)
    c: Weight(g11) = 1
    c: Equal(g11, g12-g21) x10
    c: InternalAlignment(g11-g21 -> g22) x11
    c: InternalAlignment(g23-g31 -> g22) x9
    c: Block(g22)
    c: Weight(g32) = 1
    c: Equal(g32, g33-g49) x17
    c: InternalAlignment(g32-g49 -> g50) x18
    c: InternalAlignment(g51-g66 -> g50) x16
    c: Block(g50)
    c: Coincident(g67,g50)
    c: Coincident(g67,g22)
    c: Coincident(g68,g22)
    c: Coincident(g68,g50)
    c: InternalAlignment(g70,g69)
    c: InternalAlignment(g71,g69)
    c: Block(g69)
    c: InternalAlignment(g73,g72)
    c: InternalAlignment(g74,g72)
    c: Block(g72)
    c: InternalAlignment(g76,g75)
    c: InternalAlignment(g77,g75)
    c: InternalAlignment(g78,g80)
    c: InternalAlignment(g79,g80)
    c: Block(g80)
    c: Coincident(g75,g80)
    c: Block(g75)
    c: InternalAlignment(g82,g81)
    c: InternalAlignment(g83,g81)
    c: InternalAlignment(g84,g86)
    c: InternalAlignment(g85,g86)
    c: Block(g86)
    c: Coincident(g81,g86)
    c: Block(g81)
    c: Horizontal(g87)
    c: Block(g87)
    c: Horizontal(g88)
    c: Distance(g88) = 4.14
    c: Horizontal(g89)
    c: Equal(g88,g89) = 4.14
    c: Block(g89)
    c: Block(g88)
    c: Coincident(g90,g87)
    c: Vertical(g90)
    c: Distance(g90) = 11.88
    c: Coincident(g91,g90)
    c: Horizontal(g91)
    c: Coincident(g92,g91)
    c: Vertical(g92)
    c: Distance(g91) = 4.03
    c: Distance(g92) = 1.9
    c: Coincident(g93,g87)
    c: Vertical(g93)
    c: Vertical(g94)
    c: Coincident(g94,g88)
    c: Distance(g93) = 5.8
    c: Distance(g94) = 5.8
    c: Vertical(g95)
    c: Coincident(g95,g88)
    c: Distance(g95) = 6.9
    c: Coincident(g107,g92)
    c: Weight(g96) = 1
    c: Equal(g96, g97-g106) x10
    c: InternalAlignment(g96-g106 -> g107) x11
    c: InternalAlignment(g108-g116 -> g107) x9
    c: Block(g107)
    c: Block(g117)
    c: Coincident(g126,g93)
    c: Weight(g118) = 1
    c: Equal(g118, g119-g125) x7
    c: Coincident(g126,g95)
    c: InternalAlignment(g118-g125 -> g126) x8
    c: InternalAlignment(g127-g132 -> g126) x6
    c: Coincident(g133,g94)
    c: Block(g126)
    c: Block(g133)
    c: Coincident(g134,g133)
    c: Coincident(g134,g89)
    c: Vertical(g134)
    c: Horizontal(g135)
    c: Block(g135)
    c: Horizontal(g136)
    c: Equal(g88,g136) = 4.14
    c: Horizontal(g137)
    c: Equal(g136,g137) = 4.14
    c: Block(g137)
    c: Block(g136)
    c: Coincident(g138,g135)
    c: Vertical(g138)
    c: Equal(g90,g138) = 11.88
    c: Coincident(g139,g138)
    c: Horizontal(g139)
    c: Coincident(g140,g139)
    c: Vertical(g140)
    c: Equal(g91,g139) = 4.03
    c: Equal(g92,g140) = 1.9
    c: Coincident(g141,g135)
    c: Vertical(g141)
    c: Vertical(g142)
    c: Coincident(g142,g136)
    c: Equal(g93,g141) = 5.8
    c: Equal(g94,g142) = 5.8
    c: Vertical(g143)
    c: Coincident(g143,g136)
    c: Equal(g95,g143) = 6.9
    c: Coincident(g149,g140)
    c: Equal(g96,g144) = 1
    c: Equal(g144, g145-g148) x4
    c: InternalAlignment(g144-g148 -> g149) x5
    c: InternalAlignment(g150-g158 -> g149) x9
    c: Block(g149)
    c: Block(g159)
    c: Coincident(g168,g141)
    c: Equal(g118,g160) = 1
    c: Equal(g160, g161-g167) x7
    c: Coincident(g168,g143)
    c: InternalAlignment(g160-g167 -> g168) x8
    c: InternalAlignment(g169-g174 -> g168) x6
    c: Coincident(g175,g142)
    c: Block(g168)
    c: Block(g175)
    c: Coincident(g176,g175)
    c: Coincident(g176,g137)
    c: Vertical(g176)
    c: Coincident(g177,g137)
    c: Vertical(g177)
    c: Coincident(g178,g177)
    c: Coincident(g178,g159)
    c: InternalAlignment(g179,g178)
    c: InternalAlignment(g180,g178)
    c: Block(g178)
    c: Vertical(g181)
    c: Coincident(g181,g89)
    c: Block(g5)
    c: Coincident(g182,g1)
    c: Coincident(g182,g5)
    c: Horizontal(g182)
    c: Coincident(g186,g117)
    c: Weight(g183) = 1
    c: Equal(g183,g184)
    c: Equal(g183,g185)
    c: Coincident(g186,g181)
    c: InternalAlignment(g183,g186)
    c: InternalAlignment(g184,g186)
    c: InternalAlignment(g185,g186)
    c: InternalAlignment(g187,g186)
    c: InternalAlignment(g188,g186)
    c: Block(g186)
    c: InternalAlignment(g190,g189)
    c: InternalAlignment(g191,g189)
    c: Block(g189)
    c: InternalAlignment(g193,g192)
    c: InternalAlignment(g194,g192)
    c: Block(g192)
    c: Horizontal(g195)
    c: Block(g195)
    c: Coincident(g196,g195)
    c: Vertical(g196)
    c: Block(g196)
    c: Distance(g195) = 3.71244
    c: Coincident(g197,g196)
    c: Horizontal(g197)
    c: Distance(g197) = 4.1
    c: Coincident(g198,g192)
    c: Coincident(g198,g197)
    c: Vertical(g198)
    c: Block(g198)
    c: Coincident(g199,g192)
    c: Coincident(g199,g195)
    c: Vertical(g199)
    c: Block(g199)
    c: Horizontal(g200)
    c: Block(g200)
    c: Coincident(g201,g200)
    c: Vertical(g201)
    c: Block(g201)
    c: Coincident(g202,g201)
    c: Horizontal(g202)
    c: Block(g202)
    c: Coincident(g203,g202)
    c: Vertical(g203)
    c: Block(g203)
    c: Coincident(g204,g200)
    c: Vertical(g204)
    c: Block(g204)
    c: Coincident(g215,g203)
    c: Weight(g206) = 1
    c: Equal(g206, g207-g214) x8
    c: Coincident(g215,g205)
    c: InternalAlignment(g206-g214 -> g215) x9
    c: InternalAlignment(g216-g222 -> g215) x7
    c: Coincident(g233,g204)
    c: Weight(g223) = 1
    c: Equal(g223, g224-g232) x9
    c: Coincident(g233,g205)
    c: InternalAlignment(g223-g232 -> g233) x10
    c: InternalAlignment(g234-g241 -> g233) x8
    c: Vertical(g205)
    c: Block(g205)
    c: Block(g215)
    c: Block(g233)
    c: Horizontal(g242)
    c: Horizontal(g243)
    c: Block(g242)
    c: Block(g243)
    c: Vertical(g244)
    c: Block(g244)
    c: Coincident(g270,g243)
    c: Weight(g245) = 1
    c: Equal(g245, g246-g269) x24
    c: Coincident(g270,g244)
    c: InternalAlignment(g245-g269 -> g270) x25
    c: InternalAlignment(g271-g293 -> g270) x23
    c: Coincident(g305,g242)
    c: Weight(g294) = 1
    c: Equal(g294, g295-g304) x10
    c: Coincident(g305,g242)
    c: InternalAlignment(g294-g304 -> g305) x11
    c: InternalAlignment(g306-g314 -> g305) x9
    c: Block(g305)
    c: Coincident(g327,g243)
    c: Weight(g315) = 1
    c: Equal(g315, g316-g326) x11
    c: Coincident(g327,g244)
    c: InternalAlignment(g315-g326 -> g327) x12
    c: InternalAlignment(g328-g337 -> g327) x10
    c: Block(g327)
    c: Block(g270)
FEATURE [Part::Extrusion] Extrude075  label="CommodoreLogoAndText002"
  Base = -> Sketch084
  Dir = (0,0,1)
  DirMode = 2
  FaceMakerClass = Part::FaceMakerBullseye
  LengthFwd = 10
  LengthRev = 0
  Solid = true
  Symmetric = false
FEATURE [Part::FeaturePython] Clone001  label="CommodoreLogoAndTextScale001"  # Draft clone (typed FeaturePython)
  AttacherType = Attacher::AttachEngine3D
  Fuse = false
  Objects = -> [Extrude075]
  Placement = pos=(112.566,5.37,73.6) rot=(0,0,1;0rad)
  Scale = (0.62,0.62,1)
FEATURE [Part::Cut] Cut073  label="sideA005"
  Base = -> Extrude002
  Tool = -> Part__Mirroring
FEATURE [Part::Cut] Cut074  label="sideB005"
  Base = -> Extrude028
  Tool = -> Clone001
FEATURE [Sketcher::SketchObject] Sketch085
  FullyConstrained = true
  Placement = pos=(0,0,0) rot=(-1,0,0;4.71239rad)
  sketch-geometry (10):
    g0: LineSegment StartX=0 StartY=0 StartZ=0 EndX=-7 EndY=0 EndZ=0
    g1: LineSegment StartX=-7 StartY=10 StartZ=0 EndX=-6.5 EndY=10 EndZ=0
    g2: LineSegment StartX=0 StartY=10 StartZ=0 EndX=-0.5 EndY=10 EndZ=0
    g3: ArcOfCircle CenterX=-3.5 CenterY=10 CenterZ=0 NormalX=0 NormalY=0 NormalZ=1 AngleXU=0 Radius=3 StartAngle=3.14159 EndAngle=6.28319
    g4: LineSegment StartX=-7 StartY=0 StartZ=0 EndX=-10.5 EndY=0 EndZ=0
    g5: LineSegment StartX=0 StartY=0 StartZ=0 EndX=3.5 EndY=0 EndZ=0
    g6: ArcOfCircle CenterX=-10.5 CenterY=3.5 CenterZ=0 NormalX=0 NormalY=0 NormalZ=1 AngleXU=0 Radius=3.5 StartAngle=4.71239 EndAngle=6.28319
    g7: ArcOfCircle CenterX=3.5 CenterY=3.5 CenterZ=0 NormalX=0 NormalY=0 NormalZ=1 AngleXU=0 Radius=3.5 StartAngle=3.14159 EndAngle=4.71239
    g8: LineSegment StartX=-7 StartY=3.5 StartZ=0 EndX=-7 EndY=10 EndZ=0
    g9: LineSegment StartX=0 StartY=10 StartZ=0 EndX=0 EndY=3.5 EndZ=0
  constraints (26):
    c: Coincident(g0,g-1)
    c: Horizontal(g0)
    c: Distance(g0) = 7
    c: Horizontal(g1)
    c: Distance(g1) = 0.5
    c: Horizontal(g2)
    c: Distance(g2) = 0.5
    c: Coincident(g3,g1)
    c: Coincident(g3,g2)
    c: Block(g3)
    c: Coincident(g4,g0)
    c: Horizontal(g4)
    c: Distance(g4) = 3.5
    c: Coincident(g5,g0)
    c: Distance(g5) = 3.5
    c: Horizontal(g5)
    c: Coincident(g6,g4)
    c: Block(g6)
    c: Coincident(g7,g5)
    c: Block(g7)
    c: Coincident(g8,g6)
    c: Coincident(g8,g1)
    c: Vertical(g8)
    c: Coincident(g9,g2)
    c: Coincident(g9,g7)
    c: Vertical(g9)
FEATURE [Part::Extrusion] Extrude076  label="backRightCasePillarSideBracket"
  Base = -> Sketch085
  Dir = (0,-1,3e-16)
  DirMode = 2
  FaceMakerClass = Part::FaceMakerBullseye
  LengthFwd = 6.7
  LengthRev = 0
  Placement = pos=(16,11.5,0) rot=(0,0,1;0rad)
  Solid = true
  Symmetric = false
FEATURE [Sketcher::SketchObject] Sketch086
  FullyConstrained = true
  Placement = pos=(0,0,0) rot=(1,0,0;1.5708rad)
  sketch-geometry (10):
    g0: LineSegment StartX=0 StartY=0 StartZ=0 EndX=-7 EndY=0 EndZ=0
    g1: LineSegment StartX=-7 StartY=10 StartZ=0 EndX=-6.5 EndY=10 EndZ=0
    g2: LineSegment StartX=0 StartY=10 StartZ=0 EndX=-0.5 EndY=10 EndZ=0
    g3: ArcOfCircle CenterX=-3.5 CenterY=10 CenterZ=0 NormalX=0 NormalY=0 NormalZ=1 AngleXU=0 Radius=3 StartAngle=3.14159 EndAngle=6.28319
    g4: LineSegment StartX=-7 StartY=0 StartZ=0 EndX=-10.5 EndY=0 EndZ=0
    g5: LineSegment StartX=0 StartY=0 StartZ=0 EndX=3.5 EndY=0 EndZ=0
    g6: ArcOfCircle CenterX=-10.5 CenterY=3.5 CenterZ=0 NormalX=0 NormalY=0 NormalZ=1 AngleXU=0 Radius=3.5 StartAngle=4.71239 EndAngle=6.28319
    g7: ArcOfCircle CenterX=3.5 CenterY=3.5 CenterZ=0 NormalX=0 NormalY=0 NormalZ=1 AngleXU=0 Radius=3.5 StartAngle=3.14159 EndAngle=4.71239
    g8: LineSegment StartX=-7 StartY=3.5 StartZ=0 EndX=-7 EndY=10 EndZ=0
    g9: LineSegment StartX=0 StartY=10 StartZ=0 EndX=0 EndY=3.5 EndZ=0
  constraints (26):
    c: Coincident(g0,g-1)
    c: Horizontal(g0)
    c: Distance(g0) = 7
    c: Horizontal(g1)
    c: Distance(g1) = 0.5
    c: Horizontal(g2)
    c: Distance(g2) = 0.5
    c: Coincident(g3,g1)
    c: Coincident(g3,g2)
    c: Block(g3)
    c: Coincident(g4,g0)
    c: Horizontal(g4)
    c: Distance(g4) = 3.5
    c: Coincident(g5,g0)
    c: Distance(g5) = 3.5
    c: Horizontal(g5)
    c: Coincident(g6,g4)
    c: Block(g6)
    c: Coincident(g7,g5)
    c: Block(g7)
    c: Coincident(g8,g6)
    c: Coincident(g8,g1)
    c: Vertical(g8)
    c: Coincident(g9,g2)
    c: Coincident(g9,g7)
    c: Vertical(g9)
FEATURE [Part::Extrusion] Extrude077  label="backLeftCasePillarSideBracket001"
  Base = -> Sketch086
  Dir = (0,-1,3e-16)
  DirMode = 2
  FaceMakerClass = Part::FaceMakerBullseye
  LengthFwd = 6.7
  LengthRev = 0
  Placement = pos=(9,11.5,72) rot=(0,1,0;3.14159rad)
  Solid = true
  Symmetric = false
FEATURE [Sketcher::SketchObject] Sketch087
  FullyConstrained = true
  Placement = pos=(0,0,0) rot=(1,0,0;1.5708rad)
  sketch-geometry (8):
    g0: LineSegment StartX=0 StartY=4e-16 StartZ=0 EndX=-7 EndY=4e-16 EndZ=0
    g1: LineSegment StartX=-7 StartY=4e-16 StartZ=0 EndX=-10.5 EndY=4e-16 EndZ=0
    g2: LineSegment StartX=0 StartY=4e-16 StartZ=0 EndX=3.5 EndY=4e-16 EndZ=0
    g3: ArcOfCircle CenterX=-10.5 CenterY=3.5 CenterZ=0 NormalX=0 NormalY=0 NormalZ=1 AngleXU=0 Radius=3.5 StartAngle=4.71239 EndAngle=6.28319
    g4: ArcOfCircle CenterX=3.5 CenterY=3.5 CenterZ=0 NormalX=0 NormalY=0 NormalZ=1 AngleXU=0 Radius=3.5 StartAngle=3.14159 EndAngle=4.71239
    g5: ArcOfCircle CenterX=-3.5 CenterY=3.5 CenterZ=0 NormalX=0 NormalY=0 NormalZ=1 AngleXU=0 Radius=3 StartAngle=3.14159 EndAngle=6.28319
    g6: LineSegment StartX=-7 StartY=3.5 StartZ=0 EndX=-6.5 EndY=3.5 EndZ=0
    g7: LineSegment StartX=-0.5 StartY=3.5 StartZ=0 EndX=0 EndY=3.5 EndZ=0
  constraints (20):
    c: Coincident(g0,g-1)
    c: Horizontal(g0)
    c: Distance(g0) = 7
    c: Coincident(g1,g0)
    c: Horizontal(g1)
    c: Distance(g1) = 3.5
    c: Coincident(g2,g0)
    c: Distance(g2) = 3.5
    c: Horizontal(g2)
    c: Coincident(g3,g1)
    c: Block(g3)
    c: Coincident(g4,g2)
    c: Block(g4)
    c: Horizontal(g6)
    c: Coincident(g5,g6)
    c: Block(g5)
    c: Coincident(g6,g3)
    c: Coincident(g7,g5)
    c: Coincident(g7,g4)
    c: Horizontal(g7)
FEATURE [Part::Extrusion] Extrude078  label="frontBackLeftCasePillarSideBracket001"
  Base = -> Sketch087
  Dir = (0,-1,2e-16)
  DirMode = 2
  FaceMakerClass = Part::FaceMakerBullseye
  LengthFwd = 6.7
  LengthRev = 0
  Placement = pos=(93,11.5,0) rot=(0,0,1;0rad)
  Solid = true
  Symmetric = false
FEATURE [Sketcher::SketchObject] Sketch088
  FullyConstrained = true
  Placement = pos=(0,0,0) rot=(1,0,0;1.5708rad)
  sketch-geometry (8):
    g0: LineSegment StartX=0 StartY=4e-16 StartZ=0 EndX=-7 EndY=4e-16 EndZ=0
    g1: LineSegment StartX=-7 StartY=4e-16 StartZ=0 EndX=-10.5 EndY=4e-16 EndZ=0
    g2: LineSegment StartX=0 StartY=4e-16 StartZ=0 EndX=3.5 EndY=4e-16 EndZ=0
    g3: ArcOfCircle CenterX=-10.5 CenterY=3.5 CenterZ=0 NormalX=0 NormalY=0 NormalZ=1 AngleXU=0 Radius=3.5 StartAngle=4.71239 EndAngle=6.28319
    g4: ArcOfCircle CenterX=3.5 CenterY=3.5 CenterZ=0 NormalX=0 NormalY=0 NormalZ=1 AngleXU=0 Radius=3.5 StartAngle=3.14159 EndAngle=4.71239
    g5: ArcOfCircle CenterX=-3.5 CenterY=3.5 CenterZ=0 NormalX=0 NormalY=0 NormalZ=1 AngleXU=0 Radius=3 StartAngle=3.14159 EndAngle=6.28319
    g6: LineSegment StartX=-7 StartY=3.5 StartZ=0 EndX=-6.5 EndY=3.5 EndZ=0
    g7: LineSegment StartX=-0.5 StartY=3.5 StartZ=0 EndX=0 EndY=3.5 EndZ=0
  constraints (20):
    c: Coincident(g0,g-1)
    c: Horizontal(g0)
    c: Distance(g0) = 7
    c: Coincident(g1,g0)
    c: Horizontal(g1)
    c: Distance(g1) = 3.5
    c: Coincident(g2,g0)
    c: Distance(g2) = 3.5
    c: Horizontal(g2)
    c: Coincident(g3,g1)
    c: Block(g3)
    c: Coincident(g4,g2)
    c: Block(g4)
    c: Horizontal(g6)
    c: Coincident(g5,g6)
    c: Block(g5)
    c: Coincident(g6,g3)
    c: Coincident(g7,g5)
    c: Coincident(g7,g4)
    c: Horizontal(g7)
FEATURE [Part::Extrusion] Extrude079  label="frontFrontRightCasePillarSideBracket002"
  Base = -> Sketch088
  Dir = (0,-1,2e-16)
  DirMode = 2
  FaceMakerClass = Part::FaceMakerBullseye
  LengthFwd = 2
  LengthRev = 0
  Placement = pos=(106,11.5,72) rot=(0,1,0;3.14159rad)
  Solid = true
  Symmetric = false
FEATURE [Part::Chamfer] Chamfer
  Base = -> Extrude076
  Edges = 1 edges r=3: [Edge19]
FEATURE [Part::Chamfer] Chamfer002
  Base = -> Extrude077
  Edges = 1 edges r=3: [Edge7]
FEATURE [Part::Chamfer] Chamfer003  label="backLeftCasePillarSideBracket002"
  Base = -> Chamfer002
  Edges = 1 edges r=3.8: [Edge29]
FEATURE [Part::Chamfer] Chamfer004  label="backRightCasePillarSideBracket001"
  Base = -> Chamfer
  Edges = 1 edges r=3.8: [Edge24]
FEATURE [Sketcher::SketchObject] Sketch089
  FullyConstrained = true
  Placement = pos=(0,0,0) rot=(1,0,0;1.5708rad)
  sketch-geometry (8):
    g0: LineSegment StartX=0 StartY=4e-16 StartZ=0 EndX=-7 EndY=4e-16 EndZ=0
    g1: LineSegment StartX=-7 StartY=4e-16 StartZ=0 EndX=-10.5 EndY=4e-16 EndZ=0
    g2: LineSegment StartX=0 StartY=4e-16 StartZ=0 EndX=3.5 EndY=4e-16 EndZ=0
    g3: ArcOfCircle CenterX=-10.5 CenterY=3.5 CenterZ=0 NormalX=0 NormalY=0 NormalZ=1 AngleXU=0 Radius=3.5 StartAngle=4.71239 EndAngle=6.28319
    g4: ArcOfCircle CenterX=3.5 CenterY=3.5 CenterZ=0 NormalX=0 NormalY=0 NormalZ=1 AngleXU=0 Radius=3.5 StartAngle=3.14159 EndAngle=4.71239
    g5: ArcOfCircle CenterX=-3.5 CenterY=3.5 CenterZ=0 NormalX=0 NormalY=0 NormalZ=1 AngleXU=0 Radius=3 StartAngle=3.14159 EndAngle=6.28319
    g6: LineSegment StartX=-7 StartY=3.5 StartZ=0 EndX=-6.5 EndY=3.5 EndZ=0
    g7: LineSegment StartX=-0.5 StartY=3.5 StartZ=0 EndX=0 EndY=3.5 EndZ=0
  constraints (20):
    c: Coincident(g0,g-1)
    c: Horizontal(g0)
    c: Distance(g0) = 7
    c: Coincident(g1,g0)
    c: Horizontal(g1)
    c: Distance(g1) = 3.5
    c: Coincident(g2,g0)
    c: Distance(g2) = 3.5
    c: Horizontal(g2)
    c: Coincident(g3,g1)
    c: Block(g3)
    c: Coincident(g4,g2)
    c: Block(g4)
    c: Horizontal(g6)
    c: Coincident(g5,g6)
    c: Block(g5)
    c: Coincident(g6,g3)
    c: Coincident(g7,g5)
    c: Coincident(g7,g4)
    c: Horizontal(g7)
FEATURE [Part::Extrusion] Extrude080  label="frontBackLeftCasePillarSideBracket002"
  Base = -> Sketch089
  Dir = (0,-1,2e-16)
  DirMode = 2
  FaceMakerClass = Part::FaceMakerBullseye
  LengthFwd = 6.7
  LengthRev = 0
  Placement = pos=(86,11.5,72) rot=(0,1,0;3.14159rad)
  Solid = true
  Symmetric = false
